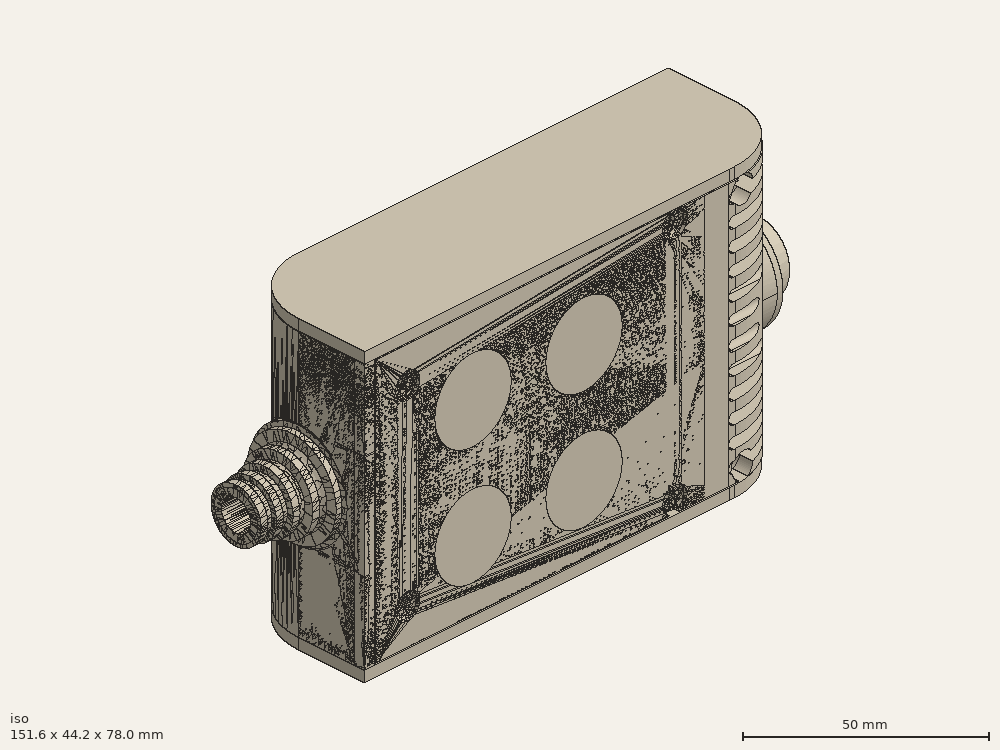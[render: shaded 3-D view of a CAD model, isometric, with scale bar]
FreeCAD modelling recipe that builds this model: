
FCSTD DOCUMENT  (FreeCAD 0.19R0.19.2)
Label: enclosure_199FCStd
License: All rights reserved
LicenseURL: http://en.wikipedia.org/wiki/All_rights_reserved
objects: Part::Revolution×152, Part::MultiFuse×146, Part::Feature×146, Sketcher::SketchObject×84, Part::Cut×70, Part::Cylinder×70, Part::Extrusion×67, Part::Fillet×58, Part::Box×36, App::MeasureDistance×4, PartDesign::Body×2, Image::ImagePlane×1
note: 831 computed .brp shape members not serialized (recipe doc carries the construction recipe); baked Part::Feature solids carry a one-line shape summary decoded from their .brp

FEATURE [Sketcher::SketchObject] Sketch  label="topSketch"
  FullyConstrained = true
  sketch-geometry (20):
    g0: LineSegment StartX=5.21097e-06 StartY=3 StartZ=0 EndX=5.21097e-06 EndY=19 EndZ=0
    g1: ArcOfCircle CenterX=19 CenterY=19 CenterZ=0 NormalX=0 NormalY=0 NormalZ=1 AngleXU=0 Radius=19 StartAngle=1.5708 EndAngle=3.14159
    g2: ArcOfCircle CenterX=19 CenterY=19 CenterZ=0 NormalX=0 NormalY=0 NormalZ=1 AngleXU=0 Radius=16 StartAngle=1.5708 EndAngle=3.14159
    g3: LineSegment StartX=114 StartY=35 StartZ=0 EndX=19 EndY=35 EndZ=0
    g4: LineSegment StartX=5.21097e-06 StartY=3 StartZ=0 EndX=5.21097e-06 EndY=0 EndZ=0
    g5: LineSegment StartX=3 StartY=0 StartZ=0 EndX=5.21097e-06 EndY=0 EndZ=0
    g6: LineSegment StartX=3 StartY=19 StartZ=0 EndX=3 EndY=0 EndZ=0
    g7: LineSegment StartX=19 StartY=38 StartZ=0 EndX=124 EndY=38 EndZ=0
    g8: Circle CenterX=119 CenterY=35 CenterZ=0 NormalX=0 NormalY=0 NormalZ=1 AngleXU=0 Radius=1
    g9: Circle CenterX=121 CenterY=35 CenterZ=0 NormalX=0 NormalY=0 NormalZ=1 AngleXU=0 Radius=1
    g10: Circle CenterX=121 CenterY=33 CenterZ=0 NormalX=0 NormalY=0 NormalZ=1 AngleXU=0 Radius=1
    g11: BSplineCurve PolesCount=3 KnotsCount=2 Degree=2 IsPeriodic=0
    g12: GeomPoint X=119 Y=35 Z=0
    g13: GeomPoint X=121 Y=33 Z=0
    g14: LineSegment StartX=119 StartY=35 StartZ=0 EndX=114 EndY=35 EndZ=0
    g15: ArcOfCircle CenterX=105 CenterY=19 CenterZ=0 NormalX=0 NormalY=0 NormalZ=1 AngleXU=0 Radius=19 StartAngle=5.7297 EndAngle=6.28319
    g16: ArcOfCircle CenterX=105 CenterY=19 CenterZ=0 NormalX=0 NormalY=0 NormalZ=1 AngleXU=0 Radius=16 StartAngle=5.60905 EndAngle=6.28319
    g17: LineSegment StartX=121 StartY=33 StartZ=0 EndX=121 EndY=19 EndZ=0
    g18: LineSegment StartX=124 StartY=38 StartZ=0 EndX=124 EndY=19 EndZ=0
    g19: LineSegment StartX=117.5 StartY=9.01251 StartZ=0 EndX=121.163 EndY=9.0125 EndZ=0
  constraints (46):
    c: Vertical(g0)
    c: Block(g0)
    c: Coincident(g1,g0)
    c: Block(g1)
    c: Coincident(g2,g1)
    c: Block(g2)
    c: Coincident(g3,g2)
    c: Horizontal(g3)
    c: Tangent(g3,g2)
    c: Coincident(g4,g0)
    c: Distance(g4) = 3
    c: Vertical(g4)
    c: Coincident(g5,g4)
    c: Horizontal(g5)
    c: Coincident(g6,g2)
    c: Coincident(g6,g5)
    c: Vertical(g6)
    c: Horizontal(g7)
    c: Distance(g7) = 105
    c: Coincident(g7,g1)
    c: Block(g3)
    c: Weight(g8) = 1
    c: Equal(g8,g9)
    c: Equal(g8,g10)
    c: InternalAlignment(g8,g11)
    c: InternalAlignment(g9,g11)
    c: InternalAlignment(g10,g11)
    c: InternalAlignment(g12,g11)
    c: InternalAlignment(g13,g11)
    c: Block(g11)
    c: Coincident(g14,g11)
    c: Coincident(g14,g3)
    c: Horizontal(g14)
    c: Block(g15)
    c: Coincident(g16,g15)
    c: Block(g16)
    c: Coincident(g17,g11)
    c: Coincident(g17,g16)
    c: Vertical(g17)
    c: Distance(g17) = 14
    c: Coincident(g18,g7)
    c: Coincident(g18,g15)
    c: Vertical(g18)
    c: Distance(g18) = 19
    c: Coincident(g19,g16)
    c: Coincident(g19,g15)
FEATURE [Sketcher::SketchObject] Sketch001  label="bottomSketch"
  FullyConstrained = true
  sketch-geometry (32):
    g0: LineSegment StartX=3.3 StartY=-6.03275e-07 StartZ=0 EndX=98 EndY=-6.03275e-07 EndZ=0
    g1: ArcOfCircle CenterX=98 CenterY=19 CenterZ=0 NormalX=0 NormalY=0 NormalZ=1 AngleXU=0 Radius=19 StartAngle=4.71239 EndAngle=5.71103
    g2: LineSegment StartX=6.3 StartY=8 StartZ=0 EndX=3.3 EndY=8 EndZ=0
    g3: LineSegment StartX=3.3 StartY=8 StartZ=0 EndX=3.3 EndY=-6.03275e-07 EndZ=0
    g4: ArcOfCircle CenterX=8.3 CenterY=5 CenterZ=0 NormalX=0 NormalY=0 NormalZ=1 AngleXU=0 Radius=2 StartAngle=3.14159 EndAngle=4.71239
    g5: LineSegment StartX=6.3 StartY=8 StartZ=0 EndX=6.3 EndY=5 EndZ=0
    g6: ArcOfCircle CenterX=98 CenterY=19 CenterZ=0 NormalX=0 NormalY=0 NormalZ=1 AngleXU=0 Radius=12.7 StartAngle=4.71239 EndAngle=6.28319
    g7: LineSegment StartX=94.7 StartY=3 StartZ=0 EndX=8.3 EndY=3 EndZ=0
    g8-g12: Circle x5 (B-spline internal-alignment scaffolding for g13; pole/knot coordinates omitted)
    g13: BSplineCurve PolesCount=5 KnotsCount=3 Degree=3 IsPeriodic=0
    g14: GeomPoint X=98 Y=6.3 Z=0
    g15: GeomPoint X=96.3938 Y=4.71946 Z=0
    g16: GeomPoint X=94.7 Y=3 Z=0
    g17-g23: Circle x7 (B-spline internal-alignment scaffolding for g24; pole/knot coordinates omitted)
    g24: BSplineCurve PolesCount=7 KnotsCount=5 Degree=3 IsPeriodic=0
    g25-g29: GeomPoint x5 (B-spline internal-alignment scaffolding for g24; pole/knot coordinates omitted)
    g30: ArcOfCircle CenterX=98 CenterY=19 CenterZ=0 NormalX=0 NormalY=0 NormalZ=1 AngleXU=0 Radius=15.7 StartAngle=5.81226 EndAngle=6.28319
    g31: LineSegment StartX=110.7 StartY=19 StartZ=0 EndX=113.7 EndY=19 EndZ=0
  constraints (41):
    c: Horizontal(g0)
    c: Coincident(g1,g0)
    c: Block(g1)
    c: Horizontal(g2)
    c: Distance(g2) = 3
    c: Coincident(g3,g2)
    c: Vertical(g3)
    c: Coincident(g3,g0)
    c: Block(g4)
    c: Block(g2)
    c: Coincident(g5,g2)
    c: Coincident(g5,g4)
    c: Vertical(g5)
    c: Coincident(g6,g1)
    c: Block(g6)
    c: Coincident(g7,g4)
    c: Horizontal(g7)
    c: Block(g0)
    c: Block(g7)
    c: Block(g3)
    c: Coincident(g13,g6)
    c: Weight(g8) = 1
    c: Equal(g8, g9-g12) x4
    c: Coincident(g13,g7)
    c: InternalAlignment(g8-g12 -> g13) x5
    c: InternalAlignment(g14,g13)
    c: InternalAlignment(g15,g13)
    c: InternalAlignment(g16,g13)
    c: Block(g13)
    c: Weight(g17) = 1
    c: Equal(g17, g18-g23) x6
    c: Coincident(g24,g1)
    c: InternalAlignment(g17-g23 -> g24) x7
    c: InternalAlignment(g25-g29 -> g24) x5
    c: Block(g24)
    c: Coincident(g30,g24)
    c: Coincident(g31,g6)
    c: Coincident(g31,g30)
    c: Horizontal(g31)
    c: Block(g31)
    c: Block(g30)
FEATURE [Part::Extrusion] Extrude  label="top"
  Base = -> Sketch
  Dir = (0,0,1)
  DirMode = 2
  FaceMakerClass = Part::FaceMakerBullseye
  LengthFwd = 72
  LengthRev = 0
  Solid = true
  Symmetric = false
FEATURE [Part::Extrusion] Extrude001  label="bottom"
  Base = -> Sketch001
  Dir = (0,0,1)
  DirMode = 2
  FaceMakerClass = Part::FaceMakerBullseye
  LengthFwd = 71.4
  LengthRev = 0
  Placement = pos=(0,0,0.3) rot=(0,0,1;0rad)
  Solid = true
  Symmetric = false
FEATURE [Sketcher::SketchObject] Sketch002  label="topSketch001"
  FullyConstrained = true
  sketch-geometry (8):
    g0: ArcOfCircle CenterX=19 CenterY=19.0975 CenterZ=0 NormalX=0 NormalY=0 NormalZ=1 AngleXU=0 Radius=18.9025 StartAngle=1.5708 EndAngle=3.14674
    g1: LineSegment StartX=0.0977805 StartY=19.0003 StartZ=0 EndX=0.0977805 EndY=0.000251602 EndZ=0
    g2: LineSegment StartX=19 StartY=38 StartZ=0 EndX=124 EndY=38 EndZ=0
    g3: LineSegment StartX=0.0977805 StartY=0.000251602 StartZ=0 EndX=105.098 EndY=0.000251602 EndZ=0
    g4: LineSegment StartX=124 StartY=38 StartZ=0 EndX=125.616 EndY=38 EndZ=0
    g5: LineSegment StartX=105.098 StartY=0.000251602 StartZ=0 EndX=106.713 EndY=0.000251602 EndZ=0
    g6: ArcOfCircle CenterX=106.616 CenterY=19 CenterZ=0 NormalX=0 NormalY=0 NormalZ=1 AngleXU=0 Radius=19 StartAngle=4.71754 EndAngle=6.28319
    g7: LineSegment StartX=125.616 StartY=38 StartZ=0 EndX=125.616 EndY=19 EndZ=0
  constraints (21):
    c: Block(g0)
    c: Coincident(g1,g0)
    c: Vertical(g1)
    c: Horizontal(g2)
    c: Distance(g2) = 105
    c: Coincident(g2,g0)
    c: Distance(g1) = 19
    c: Coincident(g3,g1)
    c: Horizontal(g3)
    c: Distance(g3) = 105
    c: Coincident(g4,g2)
    c: Horizontal(g4)
    c: Distance(g4) = 1.61553
    c: Horizontal(g5)
    c: Equal(g4,g5) = 1.61553
    c: Coincident(g5,g3)
    c: Block(g6)
    c: Coincident(g6,g5)
    c: Coincident(g7,g4)
    c: Coincident(g7,g6)
    c: Vertical(g7)
FEATURE [Part::Extrusion] Extrude002  label="sideA"
  Base = -> Sketch002
  Dir = (0,0,1)
  DirMode = 2
  FaceMakerClass = Part::FaceMakerBullseye
  LengthFwd = 3
  LengthRev = 0
  Placement = pos=(0,0,-3) rot=(0,0,1;0rad)
  Solid = true
  Symmetric = false
FEATURE [Sketcher::SketchObject] Sketch003  label="topSketch002"
  FullyConstrained = true
  sketch-geometry (6):
    g0: LineSegment StartX=19 StartY=38 StartZ=0 EndX=117 EndY=38 EndZ=0
    g1: ArcOfCircle CenterX=19 CenterY=19 CenterZ=0 NormalX=0 NormalY=0 NormalZ=1 AngleXU=0 Radius=19 StartAngle=1.5708 EndAngle=3.14159
    g2: LineSegment StartX=117 StartY=38 StartZ=0 EndX=117 EndY=19 EndZ=0
    g3: LineSegment StartX=98 StartY=1.0161e-12 StartZ=0 EndX=5.22862e-06 EndY=1.0161e-12 EndZ=0
    g4: LineSegment StartX=5.22862e-06 StartY=19 StartZ=0 EndX=5.22862e-06 EndY=1.0161e-12 EndZ=0
    g5: ArcOfCircle CenterX=98 CenterY=19 CenterZ=0 NormalX=0 NormalY=0 NormalZ=1 AngleXU=0 Radius=19 StartAngle=4.71239 EndAngle=6.28319
  constraints (16):
    c: Horizontal(g0)
    c: Distance(g0) = 98
    c: Coincident(g1,g0)
    c: Block(g1)
    c: Coincident(g2,g0)
    c: Vertical(g2)
    c: Distance(g2) = 19
    c: Horizontal(g3)
    c: Coincident(g4,g1)
    c: Vertical(g4)
    c: Coincident(g3,g4)
    c: Block(g3)
    c: Coincident(g5,g2)
    c: Coincident(g5,g3)
    c: Block(g0)
    c: Block(g5)
FEATURE [Sketcher::SketchObject] Sketch004
  FullyConstrained = true
  MapMode = 3
  Placement = pos=(0,0,0) rot=(1,0,0;1.5708rad)
  Support = -> [Extrude]
  sketch-geometry (8):
    g0: Circle CenterX=80.351 CenterY=-67.6202 CenterZ=0 NormalX=0 NormalY=0 NormalZ=1 AngleXU=0 Radius=2
    g1: Circle CenterX=80.351 CenterY=-67.6202 CenterZ=0 NormalX=0 NormalY=0 NormalZ=1 AngleXU=0 Radius=3
    g2: Circle CenterX=80.351 CenterY=-4.92017 CenterZ=0 NormalX=0 NormalY=0 NormalZ=1 AngleXU=0 Radius=2
    g3: Circle CenterX=80.351 CenterY=-4.92017 CenterZ=0 NormalX=0 NormalY=0 NormalZ=1 AngleXU=0 Radius=3
    g4: Circle CenterX=23.851 CenterY=-4.92017 CenterZ=0 NormalX=0 NormalY=0 NormalZ=1 AngleXU=0 Radius=2
    g5: Circle CenterX=23.851 CenterY=-4.92017 CenterZ=0 NormalX=0 NormalY=0 NormalZ=1 AngleXU=0 Radius=3
    g6: Circle CenterX=23.851 CenterY=-67.6202 CenterZ=0 NormalX=0 NormalY=0 NormalZ=1 AngleXU=0 Radius=2
    g7: Circle CenterX=23.851 CenterY=-67.6202 CenterZ=0 NormalX=0 NormalY=0 NormalZ=1 AngleXU=0 Radius=3
  constraints (8):
    c: Block(g3)
    c: Block(g2)
    c: Block(g1)
    c: Block(g0)
    c: Block(g6)
    c: Block(g7)
    c: Block(g4)
    c: Block(g5)
FEATURE [Part::Extrusion] Extrude004
  Base = -> Sketch004
  Dir = (0,-1,2e-16)
  DirMode = 2
  FaceMakerClass = Part::FaceMakerBullseye
  LengthFwd = 6
  LengthRev = 0
  Placement = pos=(0,9,0) rot=(0,0,1;0rad)
  Solid = true
  Symmetric = false
FEATURE [Sketcher::SketchObject] Sketch005
  FullyConstrained = true
  MapMode = 3
  Placement = pos=(0,0,0) rot=(1,0,0;1.5708rad)
  Support = -> [Extrude]
  sketch-geometry (8):
    g0: Circle CenterX=80.351 CenterY=-67.6202 CenterZ=0 NormalX=0 NormalY=0 NormalZ=1 AngleXU=0 Radius=3
    g1: Circle CenterX=80.351 CenterY=-4.92017 CenterZ=0 NormalX=0 NormalY=0 NormalZ=1 AngleXU=0 Radius=3
    g2: Circle CenterX=23.851 CenterY=-4.92017 CenterZ=0 NormalX=0 NormalY=0 NormalZ=1 AngleXU=0 Radius=3
    g3: Circle CenterX=23.851 CenterY=-67.6202 CenterZ=0 NormalX=0 NormalY=0 NormalZ=1 AngleXU=0 Radius=3
    g4: Circle CenterX=23.851 CenterY=-67.6202 CenterZ=0 NormalX=0 NormalY=0 NormalZ=1 AngleXU=0 Radius=5
    g5: Circle CenterX=80.351 CenterY=-67.6202 CenterZ=0 NormalX=0 NormalY=0 NormalZ=1 AngleXU=0 Radius=5
    g6: Circle CenterX=23.851 CenterY=-4.92017 CenterZ=0 NormalX=0 NormalY=0 NormalZ=1 AngleXU=0 Radius=5
    g7: Circle CenterX=80.351 CenterY=-4.92017 CenterZ=0 NormalX=0 NormalY=0 NormalZ=1 AngleXU=0 Radius=5
  constraints (8):
    c: Block(g1)
    c: Block(g0)
    c: Block(g3)
    c: Block(g2)
    c: Block(g5)
    c: Block(g4)
    c: Block(g6)
    c: Block(g7)
FEATURE [Part::Extrusion] Extrude005
  Base = -> Sketch005
  Dir = (0,-1,2e-16)
  DirMode = 2
  FaceMakerClass = Part::FaceMakerBullseye
  LengthFwd = 2
  LengthRev = 0
  Solid = true
  Symmetric = false
FEATURE [Sketcher::SketchObject] Sketch006
  FullyConstrained = true
  MapMode = 3
  Placement = pos=(0,0,0) rot=(1,0,0;1.5708rad)
  sketch-geometry (8):
    g0: Circle CenterX=80.351 CenterY=-67.6202 CenterZ=0 NormalX=0 NormalY=0 NormalZ=1 AngleXU=0 Radius=3
    g1: Circle CenterX=80.351 CenterY=-4.92017 CenterZ=0 NormalX=0 NormalY=0 NormalZ=1 AngleXU=0 Radius=3
    g2: Circle CenterX=23.851 CenterY=-4.92017 CenterZ=0 NormalX=0 NormalY=0 NormalZ=1 AngleXU=0 Radius=3
    g3: Circle CenterX=23.851 CenterY=-67.6202 CenterZ=0 NormalX=0 NormalY=0 NormalZ=1 AngleXU=0 Radius=3
    g4: Circle CenterX=23.851 CenterY=-67.6202 CenterZ=0 NormalX=0 NormalY=0 NormalZ=1 AngleXU=0 Radius=5
    g5: Circle CenterX=80.351 CenterY=-67.6202 CenterZ=0 NormalX=0 NormalY=0 NormalZ=1 AngleXU=0 Radius=5
    g6: Circle CenterX=23.851 CenterY=-4.92017 CenterZ=0 NormalX=0 NormalY=0 NormalZ=1 AngleXU=0 Radius=5
    g7: Circle CenterX=80.351 CenterY=-4.92017 CenterZ=0 NormalX=0 NormalY=0 NormalZ=1 AngleXU=0 Radius=5
  constraints (8):
    c: Block(g1)
    c: Block(g0)
    c: Block(g3)
    c: Block(g2)
    c: Block(g5)
    c: Block(g4)
    c: Block(g6)
    c: Block(g7)
FEATURE [Part::Extrusion] Extrude007
  Base = -> Sketch006
  Dir = (0,-1,2e-16)
  DirMode = 2
  FaceMakerClass = Part::FaceMakerBullseye
  LengthFwd = 2
  LengthRev = 0
  Solid = true
  Symmetric = false
FEATURE [Part::Fillet] Fillet
  Base = -> Extrude007
  Edges = 4 edges r=1.99: [Edge6,Edge12,Edge18,Edge24]
FEATURE [Part::Cut] Cut
  Base = -> Extrude005
  Placement = pos=(0,5,0) rot=(0,0,1;0rad)
  Tool = -> Fillet
FEATURE [Part::MultiFuse] Fusion  label="pCBScrews"
  Placement = pos=(-2.5,0,72.3) rot=(0,0,1;0rad)
  Shapes = -> [Extrude004,Cut]
FEATURE [App::MeasureDistance] Distance  label="Distance: 0.69 mm"
  Distance = 0.685967
  P1 = (24.0138,2.9647,0.3)
  P2 = (23.8901,3,-0.373787)
FEATURE [App::MeasureDistance] Distance001  label="Distance: 0.53 mm"
  Distance = 0.533607
  P1 = (80.2939,3,72.2334)
  P2 = (80.281,2.99661,71.7)
FEATURE [Part::Fillet] Fillet001
  Base = -> Extrude001
  Edges = 1 edges r=2.4: [Edge17]
FEATURE [Part::Fillet] Fillet002  label="bottom001"
  Base = -> Fillet001
  Edges = 1 edges r=2.4: [Edge36]
FEATURE [Part::Fillet] Fillet003  label="top001"
  Base = -> Extrude
  Edges = 1 edges r=2: [Edge1]
FEATURE [Sketcher::SketchObject] Sketch007
  FullyConstrained = true
  sketch-geometry (16):
    g0: LineSegment StartX=4 StartY=0 StartZ=0 EndX=4 EndY=2.4 EndZ=0
    g1: LineSegment StartX=4 StartY=2.4 StartZ=0 EndX=7 EndY=2.4 EndZ=0
    g2: LineSegment StartX=4 StartY=0 StartZ=0 EndX=5.7 EndY=0 EndZ=0
    g3: LineSegment StartX=5.7 StartY=0 StartZ=0 EndX=5.7 EndY=-5.6 EndZ=0
    g4-g8: Circle x5 (B-spline internal-alignment scaffolding for g9; pole/knot coordinates omitted)
    g9: BSplineCurve PolesCount=5 KnotsCount=3 Degree=3 IsPeriodic=0
    g10: GeomPoint X=7 Y=2.4 Z=0
    g11: GeomPoint X=10.4582 Y=-1.55472 Z=0
    g12: GeomPoint X=14 Y=-5.6 Z=0
    g13: LineSegment StartX=14 StartY=-5.6 StartZ=0 EndX=14 EndY=-14.1 EndZ=0
    g14: LineSegment StartX=14 StartY=-14.1 StartZ=0 EndX=6.5 EndY=-14.1 EndZ=0
    g15: LineSegment StartX=5.7 StartY=-5.6 StartZ=0 EndX=6.5 EndY=-14.1 EndZ=0
  constraints (28):
    c: Distance(g0) = 2.4
    c: Vertical(g0)
    c: Block(g0)
    c: Coincident(g1,g0)
    c: Horizontal(g1)
    c: Distance(g1) = 3
    c: Coincident(g2,g0)
    c: Horizontal(g2)
    c: Distance(g2) = 1.7
    c: Coincident(g3,g2)
    c: Vertical(g3)
    c: Distance(g3) = 5.6
    c: Coincident(g9,g1)
    c: Weight(g4) = 1
    c: Equal(g4, g5-g8) x4
    c: InternalAlignment(g4-g8 -> g9) x5
    c: InternalAlignment(g10,g9)
    c: InternalAlignment(g11,g9)
    c: InternalAlignment(g12,g9)
    c: Block(g9)
    c: Coincident(g13,g9)
    c: Vertical(g13)
    c: Distance(g13) = 8.5
    c: Coincident(g14,g13)
    c: Horizontal(g14)
    c: Distance(g14) = 7.5
    c: Coincident(g15,g3)
    c: Coincident(g15,g14)
FEATURE [Part::Feature] Face
  shape: bbox 10 x 16.5 x 2e-07 mm, 1 faces, 0 solids (baked)
FEATURE [Part::Revolution] Revolve  label="plugHousing"
  Angle = 360
  Axis = (0,1,0)
  Base = (0,0,0)
  FaceMakerClass = Part::FaceMakerBullseye
  Placement = pos=(0,0,36.15) rot=(0,0,1;0rad)
  Solid = false
  Source = -> Face
  Symmetric = false
FEATURE [Part::Feature] Face001
  shape: bbox 10 x 16.5 x 2e-07 mm, 1 faces, 0 solids (baked)
FEATURE [Part::Revolution] Revolve001  label="plugHousing001"
  Angle = 360
  Axis = (0,1,0)
  Base = (0,0,0)
  FaceMakerClass = Part::FaceMakerBullseye
  Placement = pos=(0,0,36.15) rot=(0,0,1;0rad)
  Solid = false
  Source = -> Face001
  Symmetric = false
FEATURE [Part::MultiFuse] Fusion001  label="plugHousing002"
  Placement = pos=(0,0,0) rot=(0,0,1;1.5708rad)
  Shapes = -> [Revolve001,Revolve]
FEATURE [Part::Feature] Face002
  shape: bbox 10 x 16.5 x 2e-07 mm, 1 faces, 0 solids (baked)
FEATURE [Part::Revolution] Revolve003  label="plugHousing005"
  Angle = 360
  Axis = (0,1,0)
  Base = (0,0,0)
  FaceMakerClass = Part::FaceMakerBullseye
  Placement = pos=(0,0,36.15) rot=(0,0,1;0rad)
  Solid = false
  Source = -> Face002
  Symmetric = false
FEATURE [Part::Feature] Face003
  shape: bbox 10 x 16.5 x 2e-07 mm, 1 faces, 0 solids (baked)
FEATURE [Part::Revolution] Revolve002  label="plugHousing003"
  Angle = 360
  Axis = (0,1,0)
  Base = (0,0,0)
  FaceMakerClass = Part::FaceMakerBullseye
  Placement = pos=(0,0,36.15) rot=(0,0,1;0rad)
  Solid = false
  Source = -> Face003
  Symmetric = false
FEATURE [Part::MultiFuse] Fusion002  label="plugHousing004"
  Placement = pos=(0,0,0) rot=(0,0,1;1.5708rad)
  Shapes = -> [Revolve002,Revolve003]
FEATURE [Part::MultiFuse] Fusion003  label="plugHousing006"
  Placement = pos=(0,19,0) rot=(0,0,1;3.14159rad)
  Shapes = -> [Fusion002,Fusion001]
FEATURE [Part::Feature] Face004
  shape: bbox 10 x 16.5 x 2e-07 mm, 1 faces, 0 solids (baked)
FEATURE [Part::Revolution] Revolve006  label="plugHousing010"
  Angle = 360
  Axis = (0,1,0)
  Base = (0,0,0)
  FaceMakerClass = Part::FaceMakerBullseye
  Placement = pos=(0,0,36.15) rot=(0,0,1;0rad)
  Solid = false
  Source = -> Face004
  Symmetric = false
FEATURE [Part::Feature] Face005
  shape: bbox 10 x 16.5 x 2e-07 mm, 1 faces, 0 solids (baked)
FEATURE [Part::Revolution] Revolve007  label="plugHousing011"
  Angle = 360
  Axis = (0,1,0)
  Base = (0,0,0)
  FaceMakerClass = Part::FaceMakerBullseye
  Placement = pos=(0,0,36.15) rot=(0,0,1;0rad)
  Solid = false
  Source = -> Face005
  Symmetric = false
FEATURE [Part::Feature] Face006
  shape: bbox 10 x 16.5 x 2e-07 mm, 1 faces, 0 solids (baked)
FEATURE [Part::Revolution] Revolve004  label="plugHousing007"
  Angle = 360
  Axis = (0,1,0)
  Base = (0,0,0)
  FaceMakerClass = Part::FaceMakerBullseye
  Placement = pos=(0,0,36.15) rot=(0,0,1;0rad)
  Solid = false
  Source = -> Face006
  Symmetric = false
FEATURE [Part::MultiFuse] Fusion004  label="plugHousing009"
  Placement = pos=(0,0,0) rot=(0,0,1;1.5708rad)
  Shapes = -> [Revolve004,Revolve007]
FEATURE [Part::Feature] Face007
  shape: bbox 10 x 16.5 x 2e-07 mm, 1 faces, 0 solids (baked)
FEATURE [Part::Revolution] Revolve005  label="plugHousing008"
  Angle = 360
  Axis = (0,1,0)
  Base = (0,0,0)
  FaceMakerClass = Part::FaceMakerBullseye
  Placement = pos=(0,0,36.15) rot=(0,0,1;0rad)
  Solid = false
  Source = -> Face007
  Symmetric = false
FEATURE [Part::MultiFuse] Fusion005  label="plugHousing012"
  Placement = pos=(0,0,0) rot=(0,0,1;1.5708rad)
  Shapes = -> [Revolve006,Revolve005]
FEATURE [Part::MultiFuse] Fusion006  label="plugHousing013"
  Placement = pos=(0,19,0) rot=(0,0,1;3.14159rad)
  Shapes = -> [Fusion005,Fusion004]
FEATURE [Part::MultiFuse] Fusion007  label="plugHousing014"
  Placement = pos=(122.621,0,-0.15) rot=(0,0,1;0rad)
  Shapes = -> [Fusion003,Fusion006]
FEATURE [Part::Cylinder] Cylinder002
  Angle = 360
  AttacherType = Attacher::AttachEngine3D
  Height = 20
  Placement = pos=(0,0,36.15) rot=(0,0,1;0rad)
  Radius = 4
FEATURE [Part::Cylinder] Cylinder003
  Angle = 360
  AttacherType = Attacher::AttachEngine3D
  Height = 10
  Placement = pos=(0,0,36.15) rot=(0,0,1;0rad)
  Radius = 4
FEATURE [Part::MultiFuse] Fusion009  label="removeToCreateHoleForPlugHousing"
  Placement = pos=(70,19,36.15) rot=(0,1,0;1.5708rad)
  Shapes = -> [Cylinder002,Cylinder003]
FEATURE [Part::Cylinder] Cylinder004
  Angle = 360
  AttacherType = Attacher::AttachEngine3D
  Height = 20
  Placement = pos=(0,0,36.15) rot=(0,0,1;0rad)
  Radius = 4
FEATURE [Part::Cylinder] Cylinder005
  Angle = 360
  AttacherType = Attacher::AttachEngine3D
  Height = 10
  Placement = pos=(0,0,36.15) rot=(0,0,1;0rad)
  Radius = 4
FEATURE [Part::MultiFuse] Fusion010  label="removeToCreateHoleForPlugHousing001"
  Placement = pos=(70,19,36.15) rot=(0,1,0;1.5708rad)
  Shapes = -> [Cylinder004,Cylinder005]
FEATURE [Part::Cut] Cut001
  Base = -> Fillet003
  Tool = -> Fusion010
FEATURE [Part::Cut] Cut002  label="Bottom"
  Base = -> Fillet002
  Tool = -> Fusion009
FEATURE [Part::Feature] Face008
  shape: bbox 10 x 16.5 x 2e-07 mm, 1 faces, 0 solids (baked)
FEATURE [Part::Revolution] Revolve011  label="plugHousing021"
  Angle = 360
  Axis = (0,1,0)
  Base = (0,0,0)
  FaceMakerClass = Part::FaceMakerBullseye
  Placement = pos=(0,0,36.15) rot=(0,0,1;0rad)
  Solid = false
  Source = -> Face008
  Symmetric = false
FEATURE [Part::Feature] Face009
  shape: bbox 10 x 16.5 x 2e-07 mm, 1 faces, 0 solids (baked)
FEATURE [Part::Revolution] Revolve012  label="plugHousing022"
  Angle = 360
  Axis = (0,1,0)
  Base = (0,0,0)
  FaceMakerClass = Part::FaceMakerBullseye
  Placement = pos=(0,0,36.15) rot=(0,0,1;0rad)
  Solid = false
  Source = -> Face009
  Symmetric = false
FEATURE [Part::Feature] Face010 .. Face013  x4 (patterned run collapsed; names and placements below)
  shape: bbox 10 x 16.5 x 2e-07 mm, 1 faces, 0 solids (baked)
FEATURE [Part::Revolution] Revolve015  label="plugHousing027"
  Angle = 360
  Axis = (0,1,0)
  Base = (0,0,0)
  FaceMakerClass = Part::FaceMakerBullseye
  Placement = pos=(0,0,36.15) rot=(0,0,1;0rad)
  Solid = false
  Source = -> Face013
  Symmetric = false
FEATURE [Part::Feature] Face014
  shape: bbox 10 x 16.5 x 2e-07 mm, 1 faces, 0 solids (baked)
FEATURE [Part::Feature] Face015
  shape: bbox 10 x 16.5 x 2e-07 mm, 1 faces, 0 solids (baked)
FEATURE [Part::Feature] Face016
  shape: bbox 10 x 16.5 x 2e-07 mm, 1 faces, 0 solids (baked)
FEATURE [Part::Revolution] Revolve019  label="plugHousing033"
  Angle = 360
  Axis = (0,1,0)
  Base = (0,0,0)
  FaceMakerClass = Part::FaceMakerBullseye
  Placement = pos=(0,0,36.15) rot=(0,0,1;0rad)
  Solid = false
  Source = -> Face016
  Symmetric = false
FEATURE [Part::Feature] Face017
  shape: bbox 10 x 16.5 x 2e-07 mm, 1 faces, 0 solids (baked)
FEATURE [Part::Revolution] Revolve020  label="plugHousing034"
  Angle = 360
  Axis = (0,1,0)
  Base = (0,0,0)
  FaceMakerClass = Part::FaceMakerBullseye
  Placement = pos=(0,0,36.15) rot=(0,0,1;0rad)
  Solid = false
  Source = -> Face017
  Symmetric = false
FEATURE [Part::Feature] Face018
  shape: bbox 10 x 16.5 x 2e-07 mm, 1 faces, 0 solids (baked)
FEATURE [Part::Revolution] Revolve016  label="plugHousing030"
  Angle = 360
  Axis = (0,1,0)
  Base = (0,0,0)
  FaceMakerClass = Part::FaceMakerBullseye
  Placement = pos=(0,0,36.15) rot=(0,0,1;0rad)
  Solid = false
  Source = -> Face018
  Symmetric = false
FEATURE [Part::MultiFuse] Fusion020  label="plugHousing038"
  Placement = pos=(0,0,0) rot=(0,0,1;1.5708rad)
  Shapes = -> [Revolve016,Revolve020]
FEATURE [Part::Feature] Face019
  shape: bbox 10 x 16.5 x 2e-07 mm, 1 faces, 0 solids (baked)
FEATURE [Part::Feature] Face020
  shape: bbox 10 x 16.5 x 2e-07 mm, 1 faces, 0 solids (baked)
FEATURE [Part::Revolution] Revolve017  label="plugHousing031"
  Angle = 360
  Axis = (0,1,0)
  Base = (0,0,0)
  FaceMakerClass = Part::FaceMakerBullseye
  Placement = pos=(0,0,36.15) rot=(0,0,1;0rad)
  Solid = false
  Source = -> Face020
  Symmetric = false
FEATURE [Part::MultiFuse] Fusion021  label="plugHousing039"
  Placement = pos=(0,0,0) rot=(0,0,1;1.5708rad)
  Shapes = -> [Revolve019,Revolve017]
FEATURE [Part::MultiFuse] Fusion023  label="plugHousing041"
  Placement = pos=(0,19,0) rot=(0,0,1;3.14159rad)
  Shapes = -> [Fusion021,Fusion020]
FEATURE [Part::Revolution] Revolve022  label="plugHousing043"
  Angle = 360
  Axis = (0,1,0)
  Base = (0,0,0)
  FaceMakerClass = Part::FaceMakerBullseye
  Placement = pos=(0,0,36.15) rot=(0,0,1;0rad)
  Solid = false
  Source = -> Face019
  Symmetric = false
FEATURE [Part::Feature] Face021
  shape: bbox 10 x 16.5 x 2e-07 mm, 1 faces, 0 solids (baked)
FEATURE [Part::Revolution] Revolve023  label="plugHousing044"
  Angle = 360
  Axis = (0,1,0)
  Base = (0,0,0)
  FaceMakerClass = Part::FaceMakerBullseye
  Placement = pos=(0,0,36.15) rot=(0,0,1;0rad)
  Solid = false
  Source = -> Face021
  Symmetric = false
FEATURE [Part::Feature] Face022
  shape: bbox 10 x 16.5 x 2e-07 mm, 1 faces, 0 solids (baked)
FEATURE [Part::Revolution] Revolve018  label="plugHousing032"
  Angle = 360
  Axis = (0,1,0)
  Base = (0,0,0)
  FaceMakerClass = Part::FaceMakerBullseye
  Placement = pos=(0,0,36.15) rot=(0,0,1;0rad)
  Solid = false
  Source = -> Face022
  Symmetric = false
FEATURE [Part::MultiFuse] Fusion022  label="plugHousing040"
  Placement = pos=(0,0,0) rot=(0,0,1;1.5708rad)
  Shapes = -> [Revolve018,Revolve023]
FEATURE [Part::Feature] Face023
  shape: bbox 10 x 16.5 x 2e-07 mm, 1 faces, 0 solids (baked)
FEATURE [Part::Revolution] Revolve021  label="plugHousing035"
  Angle = 360
  Axis = (0,1,0)
  Base = (0,0,0)
  FaceMakerClass = Part::FaceMakerBullseye
  Placement = pos=(0,0,36.15) rot=(0,0,1;0rad)
  Solid = false
  Source = -> Face023
  Symmetric = false
FEATURE [Part::MultiFuse] Fusion018  label="plugHousing036"
  Placement = pos=(0,0,0) rot=(0,0,1;1.5708rad)
  Shapes = -> [Revolve022,Revolve021]
FEATURE [Part::MultiFuse] Fusion019  label="plugHousing037"
  Placement = pos=(0,19,0) rot=(0,0,1;3.14159rad)
  Shapes = -> [Fusion018,Fusion022]
FEATURE [Part::MultiFuse] Fusion024  label="plugHousing042"
  Placement = pos=(122.621,0,-0.15) rot=(0,0,1;0rad)
  Shapes = -> [Fusion023,Fusion019]
FEATURE [Part::Cylinder] Cylinder006
  Angle = 360
  AttacherType = Attacher::AttachEngine3D
  Height = 20
  Placement = pos=(0,0,36.15) rot=(0,0,1;0rad)
  Radius = 14.3
FEATURE [Part::Cylinder] Cylinder007
  Angle = 360
  AttacherType = Attacher::AttachEngine3D
  Height = 10
  Placement = pos=(0,0,36.15) rot=(0,0,1;0rad)
  Radius = 4
FEATURE [Part::MultiFuse] Fusion026  label="removeToCreteHoleForPlugHousing"
  Placement = pos=(70,19,36) rot=(0,1,0;1.5708rad)
  Shapes = -> [Cylinder006,Cylinder007]
FEATURE [Part::Box] Box001  label="Cube001"
  AttacherType = Attacher::AttachEngine3D
  Height = 28
  Length = 3
  Placement = pos=(110.7,19,22) rot=(0,0,1;0rad)
  Width = 15.7
FEATURE [Part::Cut] Cut003  label="top002"
  Base = -> Cut001
  Tool = -> Fusion007
FEATURE [Part::Revolution] Revolve008  label="plugHousing015"
  Angle = 360
  Axis = (0,1,0)
  Base = (0,0,0)
  FaceMakerClass = Part::FaceMakerBullseye
  Placement = pos=(0,0,36.15) rot=(0,0,1;0rad)
  Solid = false
  Source = -> Face010
  Symmetric = false
FEATURE [Part::MultiFuse] Fusion013  label="plugHousing020"
  Placement = pos=(0,0,0) rot=(0,0,1;1.5708rad)
  Shapes = -> [Revolve008,Revolve012]
FEATURE [Part::Cut] Cut004  label="top003"
  Base = -> Cut003
  Placement = pos=(1,0,0) rot=(0,0,1;0rad)
  Tool = -> Fusion026
FEATURE [Part::Cylinder] Cylinder008
  Angle = 360
  AttacherType = Attacher::AttachEngine3D
  Height = 20
  Placement = pos=(0,0,36.15) rot=(0,0,1;0rad)
  Radius = 10.3
FEATURE [Part::Cylinder] Cylinder009
  Angle = 360
  AttacherType = Attacher::AttachEngine3D
  Height = 10
  Placement = pos=(0,0,36.15) rot=(0,0,1;0rad)
  Radius = 4
FEATURE [Part::MultiFuse] Fusion027  label="removeToCreteHoleForPlugHousing001"
  Placement = pos=(70,19,36) rot=(0,1,0;1.5708rad)
  Shapes = -> [Cylinder008,Cylinder009]
FEATURE [Part::Cut] Cut005  label="plugHousingTab"
  Base = -> Box001
  Tool = -> Fusion027
FEATURE [Part::MultiFuse] Fusion028  label="plugHousing045"
  Shapes = -> [Fusion024,Cut005]
FEATURE [Part::Box] Box002  label="Cube002"
  AttacherType = Attacher::AttachEngine3D
  Height = 28.8
  Length = 3
  Placement = pos=(107.3,28,21.6) rot=(0,0,1;0rad)
  Width = 7
FEATURE [Part::Box] Box003  label="Cube003"
  AttacherType = Attacher::AttachEngine3D
  Height = 3
  Length = 6.4
  Placement = pos=(107.3,28,18.6) rot=(0,0,1;0rad)
  Width = 7
FEATURE [Part::Box] Box004  label="Cube004"
  AttacherType = Attacher::AttachEngine3D
  Height = 3
  Length = 6.4
  Placement = pos=(107.3,28,50.4) rot=(0,0,1;0rad)
  Width = 7
FEATURE [Part::MultiFuse] Fusion029  label="plugHousingBracketHolder"
  Shapes = -> [Box004,Box002,Box003]
FEATURE [Part::Cylinder] Cylinder010
  Angle = 360
  AttacherType = Attacher::AttachEngine3D
  Height = 20
  Placement = pos=(0,0,36.15) rot=(0,0,1;0rad)
  Radius = 14.3
FEATURE [Part::Cylinder] Cylinder011
  Angle = 360
  AttacherType = Attacher::AttachEngine3D
  Height = 10
  Placement = pos=(0,0,36.15) rot=(0,0,1;0rad)
  Radius = 4
FEATURE [Part::MultiFuse] Fusion030  label="removeToCreteHoleForPlugHousing002"
  Placement = pos=(70,19,36) rot=(0,1,0;1.5708rad)
  Shapes = -> [Cylinder010,Cylinder011]
FEATURE [Part::Cut] Cut006  label="plugHousingBracketHolder001"
  Base = -> Fusion029
  Tool = -> Fusion030
FEATURE [Part::Cylinder] Cylinder012
  Angle = 360
  AttacherType = Attacher::AttachEngine3D
  Height = 20
  Placement = pos=(0,0,36.15) rot=(0,0,1;0rad)
  Radius = 7
FEATURE [Part::Cylinder] Cylinder013
  Angle = 360
  AttacherType = Attacher::AttachEngine3D
  Height = 10
  Placement = pos=(0,0,36.15) rot=(0,0,1;0rad)
  Radius = 4
FEATURE [Part::MultiFuse] Fusion032  label="removeToCreteHoleForPlugHousing003"
  Placement = pos=(70,19,36) rot=(0,1,0;1.5708rad)
  Shapes = -> [Cylinder012,Cylinder013]
FEATURE [Part::Cut] Cut007  label="bottom002"
  Base = -> Cut002
  Tool = -> Fusion032
FEATURE [Sketcher::SketchObject] Sketch008
  FullyConstrained = true
  sketch-geometry (54):
    g0: LineSegment StartX=-4.2 StartY=0 StartZ=0 EndX=-6.2 EndY=0 EndZ=0
    g1: LineSegment StartX=-14 StartY=-18 StartZ=0 EndX=-14 EndY=-26.5 EndZ=0
    g2: LineSegment StartX=-4.2 StartY=0 StartZ=0 EndX=-4.2 EndY=-13.4877 EndZ=0
    g3: Circle CenterX=-4.2 CenterY=-13.4877 CenterZ=0 NormalX=0 NormalY=0 NormalZ=1 AngleXU=0 Radius=1
    g4: Circle CenterX=-4.2 CenterY=-26.5 CenterZ=0 NormalX=0 NormalY=0 NormalZ=1 AngleXU=0 Radius=1
    g5: Circle CenterX=-8.2 CenterY=-26.5 CenterZ=0 NormalX=0 NormalY=0 NormalZ=1 AngleXU=0 Radius=1
    g6: BSplineCurve PolesCount=3 KnotsCount=2 Degree=2 IsPeriodic=0
    g7: GeomPoint X=-4.2 Y=-13.4877 Z=0
    g8: GeomPoint X=-8.2 Y=-26.5 Z=0
    g9: LineSegment StartX=-14 StartY=-26.5 StartZ=0 EndX=-8.2 EndY=-26.5 EndZ=0
    g10: LineSegment StartX=-10.15 StartY=-12 StartZ=0 EndX=-10.15 EndY=-14 EndZ=0
    g11: LineSegment StartX=-12.8401 StartY=-16 StartZ=0 EndX=-10.1571 EndY=-16 EndZ=0
    g12: LineSegment StartX=-10.15 StartY=-14 StartZ=0 EndX=-8.70761 EndY=-14 EndZ=0
    g13: LineSegment StartX=-12.8401 StartY=-16 StartZ=0 EndX=-12.8401 EndY=-17.6958 EndZ=0
    g14: LineSegment StartX=-10.15 StartY=-12 StartZ=0 EndX=-7.79258 EndY=-12 EndZ=0
    g15: Circle CenterX=-6.2215 CenterY=-2 CenterZ=0 NormalX=0 NormalY=0 NormalZ=1 AngleXU=0 Radius=1
    g16: Circle CenterX=-6.22762 CenterY=-2.58724 CenterZ=0 NormalX=0 NormalY=0 NormalZ=1 AngleXU=0 Radius=1
    g17: Circle CenterX=-6.32538 CenterY=-4 CenterZ=0 NormalX=0 NormalY=0 NormalZ=1 AngleXU=0 Radius=1
    g18: BSplineCurve PolesCount=3 KnotsCount=2 Degree=2 IsPeriodic=0
    g19: GeomPoint X=-6.2215 Y=-2 Z=0
    g20: GeomPoint X=-6.32538 Y=-4 Z=0
    g21: Circle CenterX=-6.48644 CenterY=-5.99526 CenterZ=0 NormalX=0 NormalY=0 NormalZ=1 AngleXU=0 Radius=1
    g22: Circle CenterX=-6.58486 CenterY=-6.99526 CenterZ=0 NormalX=0 NormalY=0 NormalZ=1 AngleXU=0 Radius=1
    g23: Circle CenterX=-6.77343 CenterY=-8 CenterZ=0 NormalX=0 NormalY=0 NormalZ=1 AngleXU=0 Radius=1
    g24: BSplineCurve PolesCount=3 KnotsCount=2 Degree=2 IsPeriodic=0
    g25: GeomPoint X=-6.48644 Y=-5.99526 Z=0
    g26: GeomPoint X=-6.77343 Y=-8 Z=0
    g27: Circle CenterX=-7.19003 CenterY=-10 CenterZ=0 NormalX=0 NormalY=0 NormalZ=1 AngleXU=0 Radius=1
    g28: Circle CenterX=-7.44407 CenterY=-11.0915 CenterZ=0 NormalX=0 NormalY=0 NormalZ=1 AngleXU=0 Radius=1
    g29: Circle CenterX=-7.79258 CenterY=-12 CenterZ=0 NormalX=0 NormalY=0 NormalZ=1 AngleXU=0 Radius=1
    g30: BSplineCurve PolesCount=3 KnotsCount=2 Degree=2 IsPeriodic=0
    g31: GeomPoint X=-7.19003 Y=-10 Z=0
    g32: GeomPoint X=-7.79258 Y=-12 Z=0
    g33: Circle CenterX=-8.70761 CenterY=-14 CenterZ=0 NormalX=0 NormalY=0 NormalZ=1 AngleXU=0 Radius=1
    g34: Circle CenterX=-9.33087 CenterY=-15.1837 CenterZ=0 NormalX=0 NormalY=0 NormalZ=1 AngleXU=0 Radius=1
    g35: Circle CenterX=-10.1571 CenterY=-16 CenterZ=0 NormalX=0 NormalY=0 NormalZ=1 AngleXU=0 Radius=1
    g36: BSplineCurve PolesCount=3 KnotsCount=2 Degree=2 IsPeriodic=0
    g37: GeomPoint X=-8.70761 Y=-14 Z=0
    g38: GeomPoint X=-10.1571 Y=-16 Z=0
    g39: Circle CenterX=-12.8401 CenterY=-17.6958 CenterZ=0 NormalX=0 NormalY=0 NormalZ=1 AngleXU=0 Radius=1
    g40: Circle CenterX=-13.3521 CenterY=-17.9027 CenterZ=0 NormalX=0 NormalY=0 NormalZ=1 AngleXU=0 Radius=1
    g41: Circle CenterX=-14 CenterY=-18 CenterZ=0 NormalX=0 NormalY=0 NormalZ=1 AngleXU=0 Radius=1
    g42: BSplineCurve PolesCount=3 KnotsCount=2 Degree=2 IsPeriodic=0
    g43: GeomPoint X=-12.8401 Y=-17.6958 Z=0
    g44: GeomPoint X=-14 Y=-18 Z=0
    g45: LineSegment StartX=-6.2 StartY=0 StartZ=0 EndX=-7.2 EndY=0 EndZ=0
    g46: LineSegment StartX=-7.2 StartY=0 StartZ=0 EndX=-7.2 EndY=-2 EndZ=0
    g47: LineSegment StartX=-7.2 StartY=-2 StartZ=0 EndX=-6.2215 EndY=-2 EndZ=0
    g48: LineSegment StartX=-6.32538 StartY=-4 StartZ=0 EndX=-7.65538 EndY=-4 EndZ=0
    g49: LineSegment StartX=-7.65538 StartY=-4 StartZ=0 EndX=-7.65538 EndY=-5.99526 EndZ=0
    g50: LineSegment StartX=-7.65538 StartY=-5.99526 StartZ=0 EndX=-6.48644 EndY=-5.99526 EndZ=0
    g51: LineSegment StartX=-6.77343 StartY=-8 StartZ=0 EndX=-8.43343 EndY=-8 EndZ=0
    g52: LineSegment StartX=-8.43343 StartY=-8 StartZ=0 EndX=-8.43343 EndY=-10 EndZ=0
    g53: LineSegment StartX=-8.43343 StartY=-10 StartZ=0 EndX=-7.19003 EndY=-10 EndZ=0
  constraints (112):
    c: Horizontal(g0)
    c: Distance(g0) = 2
    c: Block(g0)
    c: Vertical(g1)
    c: Coincident(g2,g0)
    c: Vertical(g2)
    c: Block(g2)
    c: Coincident(g6,g2)
    c: Weight(g3) = 1
    c: Equal(g3,g4)
    c: Equal(g3,g5)
    c: InternalAlignment(g3,g6)
    c: InternalAlignment(g4,g6)
    c: InternalAlignment(g5,g6)
    c: InternalAlignment(g7,g6)
    c: InternalAlignment(g8,g6)
    c: Block(g6)
    c: Coincident(g9,g1)
    c: Coincident(g9,g6)
    c: Horizontal(g9)
    c: Vertical(g10)
    c: Block(g10)
    c: Horizontal(g11)
    c: Block(g11)
    c: Coincident(g12,g10)
    c: Horizontal(g12)
    c: Block(g12)
    c: Coincident(g13,g11)
    c: Vertical(g13)
    c: Block(g13)
    c: Coincident(g14,g10)
    c: Horizontal(g14)
    c: Block(g14)
    c: Block(g9)
    c: Block(g1)
    c: Weight(g15) = 1
    c: Equal(g15,g16)
    c: Equal(g15,g17)
    c: InternalAlignment(g15,g18)
    c: InternalAlignment(g16,g18)
    c: InternalAlignment(g17,g18)
    c: InternalAlignment(g19,g18)
    c: InternalAlignment(g20,g18)
    c: Weight(g21) = 1
    c: Equal(g21,g22)
    c: Equal(g21,g23)
    c: InternalAlignment(g21,g24)
    c: InternalAlignment(g22,g24)
    c: InternalAlignment(g23,g24)
    c: InternalAlignment(g25,g24)
    c: InternalAlignment(g26,g24)
    c: Weight(g27) = 1
    c: Equal(g27,g28)
    c: Equal(g27,g29)
    c: Coincident(g30,g14)
    c: InternalAlignment(g27,g30)
    c: InternalAlignment(g28,g30)
    c: InternalAlignment(g29,g30)
    c: InternalAlignment(g31,g30)
    c: InternalAlignment(g32,g30)
    c: Coincident(g36,g12)
    c: Weight(g33) = 1
    c: Equal(g33,g34)
    c: Equal(g33,g35)
    c: Coincident(g36,g11)
    c: InternalAlignment(g33,g36)
    c: InternalAlignment(g34,g36)
    c: InternalAlignment(g35,g36)
    c: InternalAlignment(g37,g36)
    c: InternalAlignment(g38,g36)
    c: Coincident(g42,g13)
    c: Weight(g39) = 1
    c: Equal(g39,g40)
    c: Equal(g39,g41)
    c: Coincident(g42,g1)
    c: InternalAlignment(g39,g42)
    c: InternalAlignment(g40,g42)
    c: InternalAlignment(g41,g42)
    c: InternalAlignment(g43,g42)
    c: InternalAlignment(g44,g42)
    c: Block(g18)
    c: Block(g24)
    c: Block(g30)
    c: Block(g36)
    c: Block(g42)
    c: Horizontal(g45)
    c: Coincident(g45,g0)
    c: Vertical(g46)
    c: Coincident(g46,g45)
    c: Coincident(g47,g46)
    c: Coincident(g47,g18)
    c: Horizontal(g47)
    c: Block(g46)
    c: Coincident(g48,g18)
    c: Horizontal(g48)
    c: Distance(g48) = 1.33
    c: Vertical(g49)
    c: Coincident(g49,g48)
    c: Coincident(g50,g49)
    c: Coincident(g50,g24)
    c: Horizontal(g50)
    c: Tangent(g50,g22)
    c: Horizontal(g51)
    c: Coincident(g51,g24)
    c: Block(g51)
    c: Vertical(g52)
    c: Block(g52)
    c: Coincident(g52,g51)
    c: Coincident(g53,g52)
    c: Coincident(g53,g30)
    c: Horizontal(g53)
    c: Distance(g1) = 8.5
FEATURE [Part::Feature] Face024
  shape: bbox 9.8 x 26.5 x 2e-07 mm, 1 faces, 0 solids (baked)
FEATURE [Part::Revolution] Revolve024
  Angle = 360
  Axis = (0,1,0)
  Base = (0,0,0)
  FaceMakerClass = Part::FaceMakerBullseye
  Placement = pos=(0,0,0) rot=(0,0,1;1.5708rad)
  Solid = false
  Source = -> Face024
  Symmetric = false
FEATURE [Part::Feature] Face025
  shape: bbox 9.8 x 26.5 x 2e-07 mm, 1 faces, 0 solids (baked)
FEATURE [Part::Revolution] Revolve025
  Angle = 360
  Axis = (0,1,0)
  Base = (0,0,0)
  FaceMakerClass = Part::FaceMakerBullseye
  Placement = pos=(0,0,0) rot=(0,0,1;1.5708rad)
  Solid = false
  Source = -> Face025
  Symmetric = false
FEATURE [Part::MultiFuse] Fusion033
  Placement = pos=(-18,19,36) rot=(0,0,1;0rad)
  Shapes = -> [Revolve025,Revolve024]
FEATURE [Part::Cylinder] Cylinder014
  Angle = 360
  AttacherType = Attacher::AttachEngine3D
  Height = 20
  Placement = pos=(0,0,36.15) rot=(0,0,1;0rad)
  Radius = 14.3
FEATURE [Part::Cylinder] Cylinder015
  Angle = 360
  AttacherType = Attacher::AttachEngine3D
  Height = 10
  Placement = pos=(0,0,36.15) rot=(0,0,1;0rad)
  Radius = 4
FEATURE [Part::MultiFuse] Fusion034  label="removeToCreteHoleForPlugHousing004"
  Placement = pos=(-42,19,36) rot=(0,1,0;1.5708rad)
  Shapes = -> [Cylinder014,Cylinder015]
FEATURE [Part::Cut] Cut008  label="top004"
  Base = -> Cut004
  Placement = pos=(-1,0,0) rot=(0,0,1;0rad)
  Tool = -> Fusion034
FEATURE [Part::Box] Box005  label="Cube005"
  AttacherType = Attacher::AttachEngine3D
  Height = 28
  Length = 3
  Placement = pos=(110.7,19,22) rot=(0,0,1;0rad)
  Width = 15.7
FEATURE [Part::Cylinder] Cylinder016
  Angle = 360
  AttacherType = Attacher::AttachEngine3D
  Height = 10
  Placement = pos=(0,0,36.15) rot=(0,0,1;0rad)
  Radius = 4
FEATURE [Part::Cylinder] Cylinder017
  Angle = 360
  AttacherType = Attacher::AttachEngine3D
  Height = 20
  Placement = pos=(0,0,36.15) rot=(0,0,1;0rad)
  Radius = 10.3
FEATURE [Part::MultiFuse] Fusion035  label="removeToCreteHoleForPlugHousing005"
  Placement = pos=(70,19,36) rot=(0,1,0;1.5708rad)
  Shapes = -> [Cylinder017,Cylinder016]
FEATURE [Part::Cut] Cut009  label="plugHousingTab001"
  Base = -> Box005
  Placement = pos=(-107.4,-14,0) rot=(0,0,1;0rad)
  Tool = -> Fusion035
FEATURE [Part::Box] Box006  label="Cube006"
  AttacherType = Attacher::AttachEngine3D
  Height = 28
  Length = 3
  Placement = pos=(110.7,19,22) rot=(0,0,1;0rad)
  Width = 15.7
FEATURE [Part::Cylinder] Cylinder018
  Angle = 360
  AttacherType = Attacher::AttachEngine3D
  Height = 10
  Placement = pos=(0,0,36.15) rot=(0,0,1;0rad)
  Radius = 4
FEATURE [Part::Cylinder] Cylinder019
  Angle = 360
  AttacherType = Attacher::AttachEngine3D
  Height = 20
  Placement = pos=(0,0,36.15) rot=(0,0,1;0rad)
  Radius = 10.3
FEATURE [Part::MultiFuse] Fusion036  label="removeToCreteHoleForPlugHousing006"
  Placement = pos=(70,19,36) rot=(0,1,0;1.5708rad)
  Shapes = -> [Cylinder019,Cylinder018]
FEATURE [Part::Cut] Cut010  label="plugHousingTab002"
  Base = -> Box006
  Placement = pos=(-107.4,-14,0) rot=(0,0,1;0rad)
  Tool = -> Fusion036
FEATURE [Part::MultiFuse] Fusion037
  Placement = pos=(9.6,23,0) rot=(0,0,1;3.14159rad)
  Shapes = -> [Cut009,Cut010]
FEATURE [Part::Box] Box  label="Cube"
  AttacherType = Attacher::AttachEngine3D
  Height = 10
  Length = 3
  Placement = pos=(3.3,4,12) rot=(0,0,1;0rad)
  Width = 10
FEATURE [Part::Fillet] Fillet004
  Base = -> Fusion028
  Edges = 1 edges r=2: [Edge25]
FEATURE [Part::Fillet] Fillet005  label="plugHousing046"
  Base = -> Fillet004
  Edges = 1 edges r=2: [Edge8]
FEATURE [Part::Fillet] Fillet006
  Base = -> Box
  Edges = 1 edges r=2: [Edge11]
FEATURE [Part::Box] Box007  label="Cube007"
  AttacherType = Attacher::AttachEngine3D
  Height = 10
  Length = 3
  Placement = pos=(3.3,4,50) rot=(0,0,1;0rad)
  Width = 10
FEATURE [Part::Fillet] Fillet007
  Base = -> Box007
  Edges = 1 edges r=2: [Edge12]
FEATURE [Part::Box] Box008  label="Cube008"
  AttacherType = Attacher::AttachEngine3D
  Height = 28
  Length = 4
  Placement = pos=(5,0,22) rot=(0,0,1;0rad)
  Width = 10
FEATURE [Part::Fillet] Fillet008
  Base = -> Box008
  Edges = 1 edges r=1: [Edge7]
FEATURE [Part::Fillet] Fillet009
  Base = -> Fillet008
  Edges = 1 edges r=2: [Edge5]
FEATURE [Part::Fillet] Fillet010
  Base = -> Fillet009
  Edges = 1 edges r=2: [Edge2]
FEATURE [Sketcher::SketchObject] Sketch009  label="topSketch003"
  FullyConstrained = true
  sketch-geometry (4):
    g0: LineSegment StartX=16.8446 StartY=31.512 StartZ=0 EndX=16.3251 EndY=34.4666 EndZ=0
    g1: ArcOfCircle CenterX=19 CenterY=19.2524 CenterZ=0 NormalX=0 NormalY=0 NormalZ=1 AngleXU=0 Radius=15.4476 StartAngle=1.74483 EndAngle=2.72717
    g2: ArcOfCircle CenterX=19 CenterY=19.2524 CenterZ=0 NormalX=0 NormalY=0 NormalZ=1 AngleXU=0 Radius=12.4476 StartAngle=1.74483 EndAngle=2.73189
    g3: LineSegment StartX=4.86004 StartY=25.4725 StartZ=0 EndX=7.58253 EndY=24.2107 EndZ=0
  constraints (7):
    c: Block(g0)
    c: Coincident(g1,g0)
    c: Coincident(g2,g0)
    c: Coincident(g3,g1)
    c: Coincident(g3,g2)
    c: Block(g1)
    c: Block(g2)
FEATURE [Part::Extrusion] Extrude008
  Base = -> Sketch009
  Dir = (0,0,1)
  DirMode = 2
  FaceMakerClass = Part::FaceMakerBullseye
  LengthFwd = 10
  LengthRev = 0
  Placement = pos=(0,0,31) rot=(0,0,1;0rad)
  Solid = true
  Symmetric = false
FEATURE [Part::Cylinder] Cylinder020
  Angle = 360
  AttacherType = Attacher::AttachEngine3D
  Height = 20
  Placement = pos=(0,0,36.15) rot=(0,0,1;0rad)
  Radius = 8.2
FEATURE [Part::Cylinder] Cylinder021
  Angle = 360
  AttacherType = Attacher::AttachEngine3D
  Height = 10
  Placement = pos=(0,0,36.15) rot=(0,0,1;0rad)
  Radius = 4
FEATURE [Part::MultiFuse] Fusion038  label="removeToCreteHoleForPlugHousing007"
  Placement = pos=(-42,19,36) rot=(0,1,0;1.5708rad)
  Shapes = -> [Cylinder020,Cylinder021]
FEATURE [Part::Cut] Cut011
  Base = -> Extrude008
  Tool = -> Fusion038
FEATURE [Part::Fillet] Fillet011
  Base = -> Cut011
  Edges = 1 edges r=2: [Edge1]
FEATURE [Part::Fillet] Fillet012
  Base = -> Fillet011
  Edges = 1 edges r=2.5: [Edge1]
FEATURE [Part::Fillet] Fillet013
  Base = -> Fillet012
  Edges = 1 edges r=2.5: [Edge2]
FEATURE [Part::Box] Box010  label="Cube010"
  AttacherType = Attacher::AttachEngine3D
  Height = 16
  Length = 8
  Placement = pos=(12.7,31.52,28) rot=(0,0,1;0rad)
  Width = 4
FEATURE [Sketcher::SketchObject] Sketch010  label="topSketch004"
  FullyConstrained = true
  sketch-geometry (4):
    g0: LineSegment StartX=16.8446 StartY=31.512 StartZ=0 EndX=16.3251 EndY=34.4666 EndZ=0
    g1: ArcOfCircle CenterX=19 CenterY=19.2524 CenterZ=0 NormalX=0 NormalY=0 NormalZ=1 AngleXU=0 Radius=15.4476 StartAngle=1.74483 EndAngle=2.72717
    g2: ArcOfCircle CenterX=19 CenterY=19.2524 CenterZ=0 NormalX=0 NormalY=0 NormalZ=1 AngleXU=0 Radius=12.4476 StartAngle=1.74483 EndAngle=2.73189
    g3: LineSegment StartX=4.86004 StartY=25.4725 StartZ=0 EndX=7.58253 EndY=24.2107 EndZ=0
  constraints (7):
    c: Block(g0)
    c: Coincident(g1,g0)
    c: Coincident(g2,g0)
    c: Coincident(g3,g1)
    c: Coincident(g3,g2)
    c: Block(g1)
    c: Block(g2)
FEATURE [Part::Cylinder] Cylinder022
  Angle = 360
  AttacherType = Attacher::AttachEngine3D
  Height = 10
  Placement = pos=(0,0,36.15) rot=(0,0,1;0rad)
  Radius = 4
FEATURE [Sketcher::SketchObject] Sketch011  label="topSketch005"
  FullyConstrained = true
  sketch-geometry (4):
    g0: LineSegment StartX=16.8446 StartY=31.512 StartZ=0 EndX=16.3251 EndY=34.4666 EndZ=0
    g1: ArcOfCircle CenterX=19 CenterY=19.2524 CenterZ=0 NormalX=0 NormalY=0 NormalZ=1 AngleXU=0 Radius=15.4476 StartAngle=1.74483 EndAngle=2.72717
    g2: ArcOfCircle CenterX=19 CenterY=19.2524 CenterZ=0 NormalX=0 NormalY=0 NormalZ=1 AngleXU=0 Radius=12.4476 StartAngle=1.74483 EndAngle=2.73189
    g3: LineSegment StartX=4.86004 StartY=25.4725 StartZ=0 EndX=7.58253 EndY=24.2107 EndZ=0
  constraints (7):
    c: Block(g0)
    c: Coincident(g1,g0)
    c: Coincident(g2,g0)
    c: Coincident(g3,g1)
    c: Coincident(g3,g2)
    c: Block(g1)
    c: Block(g2)
FEATURE [Part::Extrusion] Extrude010
  Base = -> Sketch011
  Dir = (0,0,1)
  DirMode = 2
  FaceMakerClass = Part::FaceMakerBullseye
  LengthFwd = 10.6
  LengthRev = 0
  Placement = pos=(0,0,31) rot=(0,0,1;0rad)
  Solid = true
  Symmetric = false
FEATURE [Part::Cylinder] Cylinder023
  Angle = 360
  AttacherType = Attacher::AttachEngine3D
  Height = 20
  Placement = pos=(0,0,36.15) rot=(0,0,1;0rad)
  Radius = 8.2
FEATURE [Part::MultiFuse] Fusion039  label="removeToCreteHoleForPlugHousing008"
  Placement = pos=(-42,19,36) rot=(0,1,0;1.5708rad)
  Shapes = -> [Cylinder023,Cylinder022]
FEATURE [Part::Cut] Cut012
  Base = -> Extrude010
  Placement = pos=(0,0,-0.3) rot=(0,0,1;0rad)
  Tool = -> Fusion039
FEATURE [Part::Cut] Cut013
  Base = -> Box010
  Tool = -> Cut012
FEATURE [Part::Fillet] Fillet014
  Base = -> Cut013
  Edges = 1 edges r=0.7: [Edge13]
FEATURE [Part::Fillet] Fillet015
  Base = -> Fillet014
  Edges = 1 edges r=0.7: [Edge13]
FEATURE [Part::Fillet] Fillet016
  Base = -> Fillet015
  Edges = 1 edges r=0.7: [Edge16]
FEATURE [Part::Fillet] Fillet017
  Base = -> Fillet016
  Edges = 1 edges r=0.7: [Edge11]
FEATURE [Part::Fillet] Fillet018
  Base = -> Fillet017
  Edges = 1 edges r=0.7: [Edge10]
FEATURE [Part::Fillet] Fillet019
  Base = -> Fillet018
  Edges = 1 edges r=1.2: [Edge5]
FEATURE [Part::Fillet] Fillet020
  Base = -> Fillet019
  Edges = 1 edges r=1.2: [Edge12]
FEATURE [Part::Fillet] Fillet021
  Base = -> Fillet020
  Edges = 1 edges r=2: [Edge1]
  Placement = pos=(0.3,0,0) rot=(0,0,1;0rad)
FEATURE [Part::MultiFuse] Fusion040  label="top005"
  Shapes = -> [Cut008,Fillet021]
FEATURE [Part::MultiFuse] Fusion041  label="wireHolder"
  Shapes = -> [Fusion033,Fillet013]
FEATURE [Part::MultiFuse] Fusion042
  Shapes = -> [Fillet007,Fusion041]
FEATURE [Part::MultiFuse] Fusion043  label="wireHolder001"
  Shapes = -> [Fusion042,Fillet010]
FEATURE [Part::MultiFuse] Fusion044  label="wireHolder002"
  Shapes = -> [Fillet006,Fusion037,Fusion043]
FEATURE [Part::Feature] Face026
  shape: bbox 11 x 6 x 2e-07 mm, 1 faces, 0 solids (baked)
FEATURE [Part::Revolution] Revolve026
  Angle = 360
  Axis = (0,1,0)
  Base = (0,0,0)
  FaceMakerClass = Part::FaceMakerBullseye
  Placement = pos=(30.3,-1,19.7) rot=(0,0,1;0rad)
  Solid = false
  Source = -> Face026
  Symmetric = false
FEATURE [Sketcher::SketchObject] Sketch013  label="topSketch006"
  FullyConstrained = true
  sketch-geometry (13):
    g0: LineSegment StartX=117 StartY=19 StartZ=0 EndX=117 EndY=38 EndZ=0
    g1: ArcOfCircle CenterX=98 CenterY=19 CenterZ=0 NormalX=0 NormalY=0 NormalZ=1 AngleXU=0 Radius=19 StartAngle=5.7297 EndAngle=6.28319
    g2: LineSegment StartX=0 StartY=3 StartZ=0 EndX=0 EndY=19 EndZ=0
    g3: LineSegment StartX=19 StartY=38 StartZ=0 EndX=117 EndY=38 EndZ=0
    g4: ArcOfCircle CenterX=19 CenterY=19 CenterZ=0 NormalX=0 NormalY=0 NormalZ=1 AngleXU=0 Radius=19 StartAngle=1.5708 EndAngle=3.14159
    g5: ArcOfCircle CenterX=19 CenterY=19 CenterZ=0 NormalX=0 NormalY=0 NormalZ=1 AngleXU=0 Radius=16 StartAngle=1.5708 EndAngle=3.14159
    g6: ArcOfCircle CenterX=98 CenterY=19 CenterZ=0 NormalX=0 NormalY=0 NormalZ=1 AngleXU=0 Radius=16 StartAngle=5.60905 EndAngle=6.28319
    g7: LineSegment StartX=114 StartY=19 StartZ=0 EndX=114 EndY=35 EndZ=0
    g8: LineSegment StartX=110.5 StartY=9.01251 StartZ=0 EndX=114.163 EndY=9.01251 EndZ=0
    g9: LineSegment StartX=114 StartY=35 StartZ=0 EndX=19 EndY=35 EndZ=0
    g10: LineSegment StartX=0 StartY=3 StartZ=0 EndX=0 EndY=0 EndZ=0
    g11: LineSegment StartX=3 StartY=0 StartZ=0 EndX=0 EndY=0 EndZ=0
    g12: LineSegment StartX=3 StartY=19 StartZ=0 EndX=3 EndY=0 EndZ=0
  constraints (33):
    c: Vertical(g0)
    c: Distance(g0) = 19
    c: Block(g0)
    c: Coincident(g1,g0)
    c: Block(g1)
    c: Vertical(g2)
    c: Block(g2)
    c: Coincident(g3,g0)
    c: Horizontal(g3)
    c: Distance(g3) = 98
    c: Coincident(g4,g3)
    c: Coincident(g4,g2)
    c: Block(g4)
    c: Coincident(g5,g4)
    c: Coincident(g6,g1)
    c: Block(g6)
    c: Block(g5)
    c: Coincident(g7,g6)
    c: Vertical(g7)
    c: Coincident(g8,g6)
    c: Coincident(g8,g1)
    c: Coincident(g9,g7)
    c: Coincident(g9,g5)
    c: Horizontal(g9)
    c: Tangent(g9,g5)
    c: Coincident(g10,g2)
    c: Distance(g10) = 3
    c: Vertical(g10)
    c: Coincident(g11,g10)
    c: Horizontal(g11)
    c: Coincident(g12,g5)
    c: Coincident(g12,g11)
    c: Vertical(g12)
FEATURE [Part::Extrusion] Extrude011  label="top006"
  Base = -> Sketch013
  Dir = (0,0,1)
  DirMode = 2
  FaceMakerClass = Part::FaceMakerBullseye
  LengthFwd = 72
  LengthRev = 0
  Solid = true
  Symmetric = false
FEATURE [Sketcher::SketchObject] Sketch014
  FullyConstrained = true
  MapMode = 3
  Placement = pos=(0,0,0) rot=(1,0,0;1.5708rad)
  Support = -> [Extrude011]
  sketch-geometry (8):
    g0: Circle CenterX=80.351 CenterY=-67.6202 CenterZ=0 NormalX=0 NormalY=0 NormalZ=1 AngleXU=0 Radius=2
    g1: Circle CenterX=80.351 CenterY=-67.6202 CenterZ=0 NormalX=0 NormalY=0 NormalZ=1 AngleXU=0 Radius=3
    g2: Circle CenterX=80.351 CenterY=-4.92017 CenterZ=0 NormalX=0 NormalY=0 NormalZ=1 AngleXU=0 Radius=2
    g3: Circle CenterX=80.351 CenterY=-4.92017 CenterZ=0 NormalX=0 NormalY=0 NormalZ=1 AngleXU=0 Radius=3
    g4: Circle CenterX=23.851 CenterY=-4.92017 CenterZ=0 NormalX=0 NormalY=0 NormalZ=1 AngleXU=0 Radius=2
    g5: Circle CenterX=23.851 CenterY=-4.92017 CenterZ=0 NormalX=0 NormalY=0 NormalZ=1 AngleXU=0 Radius=3
    g6: Circle CenterX=23.851 CenterY=-67.6202 CenterZ=0 NormalX=0 NormalY=0 NormalZ=1 AngleXU=0 Radius=2
    g7: Circle CenterX=23.851 CenterY=-67.6202 CenterZ=0 NormalX=0 NormalY=0 NormalZ=1 AngleXU=0 Radius=3
  constraints (8):
    c: Block(g3)
    c: Block(g2)
    c: Block(g1)
    c: Block(g0)
    c: Block(g6)
    c: Block(g7)
    c: Block(g4)
    c: Block(g5)
FEATURE [Part::Feature] Face027
  shape: bbox 11 x 6 x 2e-07 mm, 1 faces, 0 solids (baked)
FEATURE [Part::Revolution] Revolve027
  Angle = 360
  Axis = (0,1,0)
  Base = (0,0,0)
  FaceMakerClass = Part::FaceMakerBullseye
  Placement = pos=(30.3,-1,51.7) rot=(0,0,1;0rad)
  Solid = false
  Source = -> Face027
  Symmetric = false
FEATURE [Part::Feature] Face028
  shape: bbox 11 x 6 x 2e-07 mm, 1 faces, 0 solids (baked)
FEATURE [Part::Revolution] Revolve028
  Angle = 360
  Axis = (0,1,0)
  Base = (0,0,0)
  FaceMakerClass = Part::FaceMakerBullseye
  Placement = pos=(62.3,-1,19.7) rot=(0,0,1;0rad)
  Solid = false
  Source = -> Face028
  Symmetric = false
FEATURE [Part::Feature] Face029
  shape: bbox 11 x 6 x 2e-07 mm, 1 faces, 0 solids (baked)
FEATURE [Part::Revolution] Revolve029
  Angle = 360
  Axis = (0,1,0)
  Base = (0,0,0)
  FaceMakerClass = Part::FaceMakerBullseye
  Placement = pos=(62.3,-1,51.7) rot=(0,0,1;0rad)
  Solid = false
  Source = -> Face029
  Symmetric = false
FEATURE [Part::Feature] Wire
  shape: bbox 11 x 5.2 x 2e-07 mm, 0 faces, 0 solids (baked)
FEATURE [Part::Revolution] Revolve030
  Angle = 360
  Axis = (0,1,0)
  Base = (0,0,0)
  FaceMakerClass = Part::FaceMakerBullseye
  Placement = pos=(30.3,38,19.7) rot=(0,0,1;0rad)
  Solid = true
  Source = -> Wire
  Symmetric = false
FEATURE [Part::Feature] Wire001
  shape: bbox 11 x 5.2 x 2e-07 mm, 0 faces, 0 solids (baked)
FEATURE [Part::Revolution] Revolve031
  Angle = 360
  Axis = (0,1,0)
  Base = (0,0,0)
  FaceMakerClass = Part::FaceMakerBullseye
  Placement = pos=(30.3,38,51.7) rot=(0,0,1;0rad)
  Solid = true
  Source = -> Wire001
  Symmetric = false
FEATURE [Part::Feature] Wire002
  shape: bbox 11 x 5.2 x 2e-07 mm, 0 faces, 0 solids (baked)
FEATURE [Part::Revolution] Revolve032
  Angle = 360
  Axis = (0,1,0)
  Base = (0,0,0)
  FaceMakerClass = Part::FaceMakerBullseye
  Placement = pos=(62.3,38,51.7) rot=(0,0,1;0rad)
  Solid = true
  Source = -> Wire002
  Symmetric = false
FEATURE [Part::Feature] Wire003
  shape: bbox 11 x 5.2 x 2e-07 mm, 0 faces, 0 solids (baked)
FEATURE [Part::Revolution] Revolve033
  Angle = 360
  Axis = (0,1,0)
  Base = (0,0,0)
  FaceMakerClass = Part::FaceMakerBullseye
  Placement = pos=(62.3,38,19.7) rot=(0,0,1;0rad)
  Solid = true
  Source = -> Wire003
  Symmetric = false
FEATURE [Part::MultiFuse] Fusion045  label="altRandScrewHousing"
  Shapes = -> [Revolve029,Revolve027,Revolve028,Revolve026]
FEATURE [Part::MultiFuse] Fusion046  label="fanScrewHousing"
  Shapes = -> [Revolve033,Revolve032,Revolve031,Revolve030]
FEATURE [Sketcher::SketchObject] Sketch015
  FullyConstrained = true
  sketch-geometry (17):
    g0: Circle CenterX=-3.5 CenterY=23.5 CenterZ=0 NormalX=0 NormalY=0 NormalZ=1 AngleXU=0 Radius=1
    g1: Circle CenterX=-1 CenterY=15.25 CenterZ=0 NormalX=0 NormalY=0 NormalZ=1 AngleXU=0 Radius=1
    g2: Circle CenterX=-3.5 CenterY=7 CenterZ=0 NormalX=0 NormalY=0 NormalZ=1 AngleXU=0 Radius=1
    g3: BSplineCurve PolesCount=3 KnotsCount=2 Degree=2 IsPeriodic=0
    g4: GeomPoint X=-3.5 Y=23.5 Z=0
    g5: GeomPoint X=-3.5 Y=7 Z=0
    g6: Circle CenterX=-4.8 CenterY=30.5 CenterZ=0 NormalX=0 NormalY=0 NormalZ=1 AngleXU=0 Radius=1
    g7: Circle CenterX=-3.5 CenterY=30.5 CenterZ=0 NormalX=0 NormalY=0 NormalZ=1 AngleXU=0 Radius=1
    g8: Circle CenterX=-3.5 CenterY=29.2 CenterZ=0 NormalX=0 NormalY=0 NormalZ=1 AngleXU=0 Radius=1
    g9: BSplineCurve PolesCount=3 KnotsCount=2 Degree=2 IsPeriodic=0
    g10: GeomPoint X=-4.8 Y=30.5 Z=0
    g11: GeomPoint X=-3.5 Y=29.2 Z=0
    g12: LineSegment StartX=-3.5 StartY=29.2 StartZ=0 EndX=-3.5 EndY=23.5 EndZ=0
    g13: LineSegment StartX=-4.8 StartY=30.5 StartZ=0 EndX=0 EndY=30.5 EndZ=0
    g14: LineSegment StartX=-3.5 StartY=0.3 StartZ=0 EndX=0 EndY=0.3 EndZ=0
    g15: LineSegment StartX=-3.5 StartY=0.3 StartZ=0 EndX=-3.5 EndY=7 EndZ=0
    g16: LineSegment StartX=0 StartY=0.3 StartZ=0 EndX=0 EndY=30.5 EndZ=0
  constraints (33):
    c: Weight(g0) = 1
    c: Equal(g0,g1)
    c: Equal(g0,g2)
    c: InternalAlignment(g0,g3)
    c: InternalAlignment(g1,g3)
    c: InternalAlignment(g2,g3)
    c: InternalAlignment(g4,g3)
    c: InternalAlignment(g5,g3)
    c: Block(g3)
    c: Weight(g6) = 1
    c: Equal(g6,g7)
    c: Equal(g6,g8)
    c: InternalAlignment(g6,g9)
    c: InternalAlignment(g7,g9)
    c: InternalAlignment(g8,g9)
    c: InternalAlignment(g10,g9)
    c: InternalAlignment(g11,g9)
    c: Block(g9)
    c: Coincident(g12,g9)
    c: Coincident(g12,g3)
    c: Vertical(g12)
    c: Coincident(g13,g9)
    c: Horizontal(g13)
    c: Distance(g13) = 4.8
    c: Horizontal(g14)
    c: Block(g14)
    c: Coincident(g15,g14)
    c: Coincident(g15,g3)
    c: Vertical(g15)
    c: Coincident(g16,g14)
    c: Coincident(g16,g13)
    c: Vertical(g16)
    c: Tangent(g16,g1)
FEATURE [Sketcher::SketchObject] Sketch016
  FullyConstrained = true
  sketch-geometry (16):
    g0: Circle CenterX=-3.5 CenterY=23.5 CenterZ=0 NormalX=0 NormalY=0 NormalZ=1 AngleXU=0 Radius=1
    g1: Circle CenterX=-1 CenterY=15.25 CenterZ=0 NormalX=0 NormalY=0 NormalZ=1 AngleXU=0 Radius=1
    g2: Circle CenterX=-3.5 CenterY=7 CenterZ=0 NormalX=0 NormalY=0 NormalZ=1 AngleXU=0 Radius=1
    g3: BSplineCurve PolesCount=3 KnotsCount=2 Degree=2 IsPeriodic=0
    g4: GeomPoint X=-3.5 Y=23.5 Z=0
    g5: GeomPoint X=-3.5 Y=7 Z=0
    g6: LineSegment StartX=-3.5 StartY=28.2 StartZ=0 EndX=-3.5 EndY=23.5 EndZ=0
    g7: LineSegment StartX=0 StartY=29.5 StartZ=0 EndX=0 EndY=30 EndZ=0
    g8: LineSegment StartX=-3.5 StartY=28.2 StartZ=0 EndX=-3.5 EndY=30 EndZ=0
    g9: LineSegment StartX=0 StartY=30 StartZ=0 EndX=0 EndY=30.5 EndZ=0
    g10: LineSegment StartX=0 StartY=30.5 StartZ=0 EndX=-3.5 EndY=30.5 EndZ=0
    g11: LineSegment StartX=-3.5 StartY=30.5 StartZ=0 EndX=-3.5 EndY=30 EndZ=0
    g12: LineSegment StartX=0 StartY=29.5 StartZ=0 EndX=0 EndY=5 EndZ=0
    g13: LineSegment StartX=-3.5 StartY=0.3 StartZ=0 EndX=-3.5 EndY=7 EndZ=0
    g14: LineSegment StartX=-3.5 StartY=0.3 StartZ=0 EndX=0 EndY=0.3 EndZ=0
    g15: LineSegment StartX=0 StartY=5 StartZ=0 EndX=0 EndY=0.3 EndZ=0
  constraints (39):
    c: Weight(g0) = 1
    c: Equal(g0,g1)
    c: Equal(g0,g2)
    c: InternalAlignment(g0,g3)
    c: InternalAlignment(g1,g3)
    c: InternalAlignment(g2,g3)
    c: InternalAlignment(g4,g3)
    c: InternalAlignment(g5,g3)
    c: Block(g3)
    c: Coincident(g6,g3)
    c: Vertical(g6)
    c: Vertical(g7)
    c: Distance(g7) = 0.5
    c: Coincident(g8,g6)
    c: Vertical(g8)
    c: Block(g6)
    c: Block(g7)
    c: Vertical(g9)
    c: Equal(g7,g9) = 0.5
    c: Block(g9)
    c: Coincident(g9,g7)
    c: Horizontal(g10)
    c: Coincident(g10,g9)
    c: Coincident(g11,g10)
    c: Coincident(g11,g8)
    c: Vertical(g11)
    c: Block(g11)
    c: Coincident(g12,g7)
    c: Vertical(g12)
    c: Coincident(g13,g3)
    c: Vertical(g13)
    c: Distance(g13) = 6.7
    c: Coincident(g14,g13)
    c: Horizontal(g14)
    c: Block(g14)
    c: Coincident(g15,g12)
    c: Coincident(g15,g14)
    c: Vertical(g15)
    c: Block(g15)
FEATURE [Sketcher::SketchObject] Sketch017
  FullyConstrained = true
  sketch-geometry (11):
    g0: LineSegment StartX=-3.5 StartY=1e-16 StartZ=0 EndX=-1.6 EndY=1e-16 EndZ=0
    g1: LineSegment StartX=-1.6 StartY=1e-16 StartZ=0 EndX=-1.6 EndY=1.5 EndZ=0
    g2: LineSegment StartX=-3.5 StartY=1.5 StartZ=0 EndX=-1.6 EndY=1.5 EndZ=0
    g3: LineSegment StartX=-3.5 StartY=1e-16 StartZ=0 EndX=-4.8 EndY=1e-16 EndZ=0
    g4: Circle CenterX=-3.5 CenterY=1.3 CenterZ=0 NormalX=0 NormalY=0 NormalZ=1 AngleXU=0 Radius=1
    g5: Circle CenterX=-3.5 CenterY=1e-16 CenterZ=0 NormalX=0 NormalY=0 NormalZ=1 AngleXU=0 Radius=1
    g6: Circle CenterX=-4.8 CenterY=1e-16 CenterZ=0 NormalX=0 NormalY=0 NormalZ=1 AngleXU=0 Radius=1
    g7: BSplineCurve PolesCount=3 KnotsCount=2 Degree=2 IsPeriodic=0
    g8: GeomPoint X=-3.5 Y=1.3 Z=0
    g9: GeomPoint X=-4.8 Y=1e-16 Z=0
    g10: LineSegment StartX=-3.5 StartY=1.3 StartZ=0 EndX=-3.5 EndY=1.5 EndZ=0
  constraints (24):
    c: Horizontal(g0)
    c: Distance(g0) = 1.9
    c: Block(g0)
    c: Coincident(g1,g0)
    c: Vertical(g1)
    c: Coincident(g2,g1)
    c: Horizontal(g2)
    c: Coincident(g3,g0)
    c: Horizontal(g3)
    c: Distance(g3) = 1.3
    c: Weight(g4) = 1
    c: Equal(g4,g5)
    c: Coincident(g5,g0)
    c: Equal(g4,g6)
    c: Coincident(g7,g3)
    c: InternalAlignment(g4,g7)
    c: InternalAlignment(g5,g7)
    c: InternalAlignment(g6,g7)
    c: InternalAlignment(g8,g7)
    c: InternalAlignment(g9,g7)
    c: Coincident(g10,g7)
    c: Coincident(g10,g2)
    c: Vertical(g10)
    c: Block(g10)
FEATURE [Part::Feature] Face035
  shape: bbox 3.2 x 1.5 x 2e-07 mm, 1 faces, 0 solids (baked)
FEATURE [Part::Revolution] Revolve039  label="backCaseScrewRetainer"
  Angle = 360
  Axis = (0,1,0)
  Base = (0,0,0)
  FaceMakerClass = Part::FaceMakerBullseye
  Placement = pos=(12.5,3,62) rot=(0,0,1;0rad)
  Solid = false
  Source = -> Face035
  Symmetric = false
FEATURE [Part::Feature] Face036
  shape: bbox 3.2 x 1.5 x 2e-07 mm, 1 faces, 0 solids (baked)
FEATURE [Part::Feature] Face039
  shape: bbox 4.8 x 30.2 x 2e-07 mm, 1 faces, 0 solids (baked)
FEATURE [Part::Revolution] Revolve043  label="frontCaseScrewPost002"
  Angle = 360
  Axis = (0,1,0)
  Base = (0,0,0)
  FaceMakerClass = Part::FaceMakerBullseye
  Placement = pos=(89.5,4.5,3.5) rot=(0,0,1;0rad)
  Solid = false
  Source = -> Face039
  Symmetric = false
FEATURE [Part::Feature] Face042
  shape: bbox 4.8 x 30.2 x 2e-07 mm, 1 faces, 0 solids (baked)
FEATURE [Part::Revolution] Revolve046  label="frontCaseScrewPost003"
  Angle = 360
  Axis = (0,1,0)
  Base = (0,0,0)
  FaceMakerClass = Part::FaceMakerBullseye
  Placement = pos=(89.5,4.5,68.5) rot=(0,0,1;0rad)
  Solid = false
  Source = -> Face042
  Symmetric = false
FEATURE [Part::Feature] Face043
  shape: bbox 3.2 x 1.5 x 2e-07 mm, 1 faces, 0 solids (baked)
FEATURE [Part::Revolution] Revolve047  label="frontCaseScrewRetainer002"
  Angle = 360
  Axis = (0,1,0)
  Base = (0,0,0)
  FaceMakerClass = Part::FaceMakerBullseye
  Placement = pos=(89.5,3,68.5) rot=(0,0,1;0rad)
  Solid = false
  Source = -> Face043
  Symmetric = false
FEATURE [Part::Feature] Face044
  shape: bbox 3.2 x 1.5 x 2e-07 mm, 1 faces, 0 solids (baked)
FEATURE [Part::Revolution] Revolve048  label="frontCaseScrewRetainer003"
  Angle = 360
  Axis = (0,1,0)
  Base = (0,0,0)
  FaceMakerClass = Part::FaceMakerBullseye
  Placement = pos=(89.5,3,3.5) rot=(0,0,1;0rad)
  Solid = false
  Source = -> Face044
  Symmetric = false
FEATURE [App::MeasureDistance] Distance002  label="Distance: 1.67 mm"
  Distance = 1.66921
  P1 = (99.2361,4.7524,71.7)
  P2 = (99.2347,6.42161,71.7)
FEATURE [Sketcher::SketchObject] Sketch018
  FullyConstrained = true
  sketch-geometry (7):
    g0: LineSegment StartX=0 StartY=0 StartZ=0 EndX=0 EndY=6 EndZ=0
    g1: Circle CenterX=0 CenterY=0 CenterZ=0 NormalX=0 NormalY=0 NormalZ=1 AngleXU=0 Radius=1
    g2: Circle CenterX=8 CenterY=6 CenterZ=0 NormalX=0 NormalY=0 NormalZ=1 AngleXU=0 Radius=1
    g3: BSplineCurve PolesCount=3 KnotsCount=2 Degree=2 IsPeriodic=0
    g4: GeomPoint X=0 Y=0 Z=0
    g5: GeomPoint X=8 Y=6 Z=0
    g6: LineSegment StartX=0 StartY=6 StartZ=0 EndX=8 EndY=6 EndZ=0
  constraints (14):
    c: Coincident(g0,g-1)
    c: Distance(g0) = 6
    c: Vertical(g0)
    c: Coincident(g3,g0)
    c: Weight(g1) = 1
    c: Equal(g1,g2)
    c: InternalAlignment(g1,g3)
    c: InternalAlignment(g2,g3)
    c: InternalAlignment(g4,g3)
    c: InternalAlignment(g5,g3)
    c: Block(g3)
    c: Coincident(g6,g0)
    c: Coincident(g6,g3)
    c: Horizontal(g6)
FEATURE [Part::Extrusion] Extrude012  label="caseScrewPillarBracket"
  Base = -> Sketch018
  Dir = (0,0,1)
  DirMode = 2
  FaceMakerClass = Part::FaceMakerBullseye
  LengthFwd = 2.4
  LengthRev = 0
  Placement = pos=(15.76,29,8.8) rot=(0,1,0;0rad)
  Solid = true
  Symmetric = false
FEATURE [Sketcher::SketchObject] Sketch019
  FullyConstrained = true
  sketch-geometry (7):
    g0: LineSegment StartX=0 StartY=0 StartZ=0 EndX=0 EndY=6 EndZ=0
    g1: Circle CenterX=0 CenterY=0 CenterZ=0 NormalX=0 NormalY=0 NormalZ=1 AngleXU=0 Radius=1
    g2: Circle CenterX=8 CenterY=6 CenterZ=0 NormalX=0 NormalY=0 NormalZ=1 AngleXU=0 Radius=1
    g3: BSplineCurve PolesCount=3 KnotsCount=2 Degree=2 IsPeriodic=0
    g4: GeomPoint X=0 Y=0 Z=0
    g5: GeomPoint X=8 Y=6 Z=0
    g6: LineSegment StartX=0 StartY=6 StartZ=0 EndX=8 EndY=6 EndZ=0
  constraints (14):
    c: Coincident(g0,g-1)
    c: Distance(g0) = 6
    c: Vertical(g0)
    c: Coincident(g3,g0)
    c: Weight(g1) = 1
    c: Equal(g1,g2)
    c: InternalAlignment(g1,g3)
    c: InternalAlignment(g2,g3)
    c: InternalAlignment(g4,g3)
    c: InternalAlignment(g5,g3)
    c: Block(g3)
    c: Coincident(g6,g0)
    c: Coincident(g6,g3)
    c: Horizontal(g6)
FEATURE [Part::Extrusion] Extrude013  label="caseScrewPillarBracket001"
  Base = -> Sketch019
  Dir = (0,0,1)
  DirMode = 2
  FaceMakerClass = Part::FaceMakerBullseye
  LengthFwd = 2.4
  LengthRev = 0
  Placement = pos=(15.76,29,60.8) rot=(0,0,1;0rad)
  Solid = true
  Symmetric = false
FEATURE [Sketcher::SketchObject] Sketch020
  FullyConstrained = true
  sketch-geometry (7):
    g0: LineSegment StartX=0 StartY=0 StartZ=0 EndX=0 EndY=6 EndZ=0
    g1: Circle CenterX=0 CenterY=0 CenterZ=0 NormalX=0 NormalY=0 NormalZ=1 AngleXU=0 Radius=1
    g2: Circle CenterX=8 CenterY=6 CenterZ=0 NormalX=0 NormalY=0 NormalZ=1 AngleXU=0 Radius=1
    g3: BSplineCurve PolesCount=3 KnotsCount=2 Degree=2 IsPeriodic=0
    g4: GeomPoint X=0 Y=0 Z=0
    g5: GeomPoint X=8 Y=6 Z=0
    g6: LineSegment StartX=0 StartY=6 StartZ=0 EndX=8 EndY=6 EndZ=0
  constraints (14):
    c: Coincident(g0,g-1)
    c: Distance(g0) = 6
    c: Vertical(g0)
    c: Coincident(g3,g0)
    c: Weight(g1) = 1
    c: Equal(g1,g2)
    c: InternalAlignment(g1,g3)
    c: InternalAlignment(g2,g3)
    c: InternalAlignment(g4,g3)
    c: InternalAlignment(g5,g3)
    c: Block(g3)
    c: Coincident(g6,g0)
    c: Coincident(g6,g3)
    c: Horizontal(g6)
FEATURE [Part::Extrusion] Extrude014  label="caseScrewPillarBracket002"
  Base = -> Sketch020
  Dir = (0,0,1)
  DirMode = 2
  FaceMakerClass = Part::FaceMakerBullseye
  LengthFwd = 2.4
  LengthRev = 0
  Placement = pos=(13.7,29,13.26) rot=(0,-1,0;1.5708rad)
  Solid = true
  Symmetric = false
FEATURE [Sketcher::SketchObject] Sketch021
  FullyConstrained = true
  sketch-geometry (7):
    g0: LineSegment StartX=0 StartY=0 StartZ=0 EndX=0 EndY=6 EndZ=0
    g1: Circle CenterX=0 CenterY=0 CenterZ=0 NormalX=0 NormalY=0 NormalZ=1 AngleXU=0 Radius=1
    g2: Circle CenterX=8 CenterY=6 CenterZ=0 NormalX=0 NormalY=0 NormalZ=1 AngleXU=0 Radius=1
    g3: BSplineCurve PolesCount=3 KnotsCount=2 Degree=2 IsPeriodic=0
    g4: GeomPoint X=0 Y=0 Z=0
    g5: GeomPoint X=8 Y=6 Z=0
    g6: LineSegment StartX=0 StartY=6 StartZ=0 EndX=8 EndY=6 EndZ=0
  constraints (14):
    c: Coincident(g0,g-1)
    c: Distance(g0) = 6
    c: Vertical(g0)
    c: Coincident(g3,g0)
    c: Weight(g1) = 1
    c: Equal(g1,g2)
    c: InternalAlignment(g1,g3)
    c: InternalAlignment(g2,g3)
    c: InternalAlignment(g4,g3)
    c: InternalAlignment(g5,g3)
    c: Block(g3)
    c: Coincident(g6,g0)
    c: Coincident(g6,g3)
    c: Horizontal(g6)
FEATURE [Part::Extrusion] Extrude015  label="caseScrewPillarBracket003"
  Base = -> Sketch021
  Dir = (0,0,1)
  DirMode = 2
  FaceMakerClass = Part::FaceMakerBullseye
  LengthFwd = 2.4
  LengthRev = 0
  Placement = pos=(11.3,29,58.74) rot=(0,1,0;1.5708rad)
  Solid = true
  Symmetric = false
FEATURE [Sketcher::SketchObject] Sketch022
  FullyConstrained = true
  sketch-geometry (7):
    g0: LineSegment StartX=0 StartY=0 StartZ=0 EndX=0 EndY=6 EndZ=0
    g1: Circle CenterX=0 CenterY=0 CenterZ=0 NormalX=0 NormalY=0 NormalZ=1 AngleXU=0 Radius=1
    g2: Circle CenterX=8 CenterY=6 CenterZ=0 NormalX=0 NormalY=0 NormalZ=1 AngleXU=0 Radius=1
    g3: BSplineCurve PolesCount=3 KnotsCount=2 Degree=2 IsPeriodic=0
    g4: GeomPoint X=0 Y=0 Z=0
    g5: GeomPoint X=8 Y=6 Z=0
    g6: LineSegment StartX=0 StartY=6 StartZ=0 EndX=8 EndY=6 EndZ=0
  constraints (14):
    c: Coincident(g0,g-1)
    c: Distance(g0) = 6
    c: Vertical(g0)
    c: Coincident(g3,g0)
    c: Weight(g1) = 1
    c: Equal(g1,g2)
    c: InternalAlignment(g1,g3)
    c: InternalAlignment(g2,g3)
    c: InternalAlignment(g4,g3)
    c: InternalAlignment(g5,g3)
    c: Block(g3)
    c: Coincident(g6,g0)
    c: Coincident(g6,g3)
    c: Horizontal(g6)
FEATURE [Part::Extrusion] Extrude016  label="caseScrewPillarBracket004"
  Base = -> Sketch022
  Dir = (0,0,1)
  DirMode = 2
  FaceMakerClass = Part::FaceMakerBullseye
  LengthFwd = 2.4
  LengthRev = 0
  Placement = pos=(88.3,29,65.23) rot=(0,1,0;1.5708rad)
  Solid = true
  Symmetric = false
FEATURE [Sketcher::SketchObject] Sketch023
  FullyConstrained = true
  sketch-geometry (7):
    g0: LineSegment StartX=0 StartY=0 StartZ=0 EndX=0 EndY=6 EndZ=0
    g1: Circle CenterX=0 CenterY=0 CenterZ=0 NormalX=0 NormalY=0 NormalZ=1 AngleXU=0 Radius=1
    g2: Circle CenterX=8 CenterY=6 CenterZ=0 NormalX=0 NormalY=0 NormalZ=1 AngleXU=0 Radius=1
    g3: BSplineCurve PolesCount=3 KnotsCount=2 Degree=2 IsPeriodic=0
    g4: GeomPoint X=0 Y=0 Z=0
    g5: GeomPoint X=8 Y=6 Z=0
    g6: LineSegment StartX=0 StartY=6 StartZ=0 EndX=8 EndY=6 EndZ=0
  constraints (14):
    c: Coincident(g0,g-1)
    c: Distance(g0) = 6
    c: Vertical(g0)
    c: Coincident(g3,g0)
    c: Weight(g1) = 1
    c: Equal(g1,g2)
    c: InternalAlignment(g1,g3)
    c: InternalAlignment(g2,g3)
    c: InternalAlignment(g4,g3)
    c: InternalAlignment(g5,g3)
    c: Block(g3)
    c: Coincident(g6,g0)
    c: Coincident(g6,g3)
    c: Horizontal(g6)
FEATURE [Part::Extrusion] Extrude017  label="caseScrewPillarBracket005"
  Base = -> Sketch023
  Dir = (0,0,1)
  DirMode = 2
  FaceMakerClass = Part::FaceMakerBullseye
  LengthFwd = 2.4
  LengthRev = 0
  Placement = pos=(90.7,29,6.77) rot=(0,-1,0;1.5708rad)
  Solid = true
  Symmetric = false
FEATURE [Sketcher::SketchObject] Sketch024
  FullyConstrained = true
  sketch-geometry (7):
    g0: LineSegment StartX=0 StartY=0 StartZ=0 EndX=0 EndY=6 EndZ=0
    g1: Circle CenterX=0 CenterY=0 CenterZ=0 NormalX=0 NormalY=0 NormalZ=1 AngleXU=0 Radius=1
    g2: Circle CenterX=8 CenterY=6 CenterZ=0 NormalX=0 NormalY=0 NormalZ=1 AngleXU=0 Radius=1
    g3: BSplineCurve PolesCount=3 KnotsCount=2 Degree=2 IsPeriodic=0
    g4: GeomPoint X=0 Y=0 Z=0
    g5: GeomPoint X=8 Y=6 Z=0
    g6: LineSegment StartX=0 StartY=6 StartZ=0 EndX=8 EndY=6 EndZ=0
  constraints (14):
    c: Coincident(g0,g-1)
    c: Distance(g0) = 6
    c: Vertical(g0)
    c: Coincident(g3,g0)
    c: Weight(g1) = 1
    c: Equal(g1,g2)
    c: InternalAlignment(g1,g3)
    c: InternalAlignment(g2,g3)
    c: InternalAlignment(g4,g3)
    c: InternalAlignment(g5,g3)
    c: Block(g3)
    c: Coincident(g6,g0)
    c: Coincident(g6,g3)
    c: Horizontal(g6)
FEATURE [Part::Extrusion] Extrude018  label="caseScrewPillarBracket006"
  Base = -> Sketch024
  Dir = (0,0,1)
  DirMode = 2
  FaceMakerClass = Part::FaceMakerBullseye
  LengthFwd = 2.4
  LengthRev = 0
  Placement = pos=(103.7,29,6.77) rot=(0,-1,0;1.5708rad)
  Solid = true
  Symmetric = false
FEATURE [Sketcher::SketchObject] Sketch025
  FullyConstrained = true
  sketch-geometry (7):
    g0: LineSegment StartX=0 StartY=0 StartZ=0 EndX=0 EndY=6 EndZ=0
    g1: Circle CenterX=0 CenterY=0 CenterZ=0 NormalX=0 NormalY=0 NormalZ=1 AngleXU=0 Radius=1
    g2: Circle CenterX=8 CenterY=6 CenterZ=0 NormalX=0 NormalY=0 NormalZ=1 AngleXU=0 Radius=1
    g3: BSplineCurve PolesCount=3 KnotsCount=2 Degree=2 IsPeriodic=0
    g4: GeomPoint X=0 Y=0 Z=0
    g5: GeomPoint X=8 Y=6 Z=0
    g6: LineSegment StartX=0 StartY=6 StartZ=0 EndX=8 EndY=6 EndZ=0
  constraints (14):
    c: Coincident(g0,g-1)
    c: Distance(g0) = 6
    c: Vertical(g0)
    c: Coincident(g3,g0)
    c: Weight(g1) = 1
    c: Equal(g1,g2)
    c: InternalAlignment(g1,g3)
    c: InternalAlignment(g2,g3)
    c: InternalAlignment(g4,g3)
    c: InternalAlignment(g5,g3)
    c: Block(g3)
    c: Coincident(g6,g0)
    c: Coincident(g6,g3)
    c: Horizontal(g6)
FEATURE [Part::Extrusion] Extrude019  label="caseScrewPillarBracket007"
  Base = -> Sketch025
  Dir = (0,0,1)
  DirMode = 2
  FaceMakerClass = Part::FaceMakerBullseye
  LengthFwd = 2.4
  LengthRev = 0
  Placement = pos=(101.3,29,65.23) rot=(0,1,0;1.5708rad)
  Solid = true
  Symmetric = false
FEATURE [Part::Box] Box011  label="frontCaseScrewPillarBracket"
  AttacherType = Attacher::AttachEngine3D
  Height = 2.4
  Length = 16
  Placement = pos=(87,28,2.3) rot=(0,0,1;0rad)
  Width = 7
FEATURE [Part::Box] Box012  label="frontCaseScrewPillarBracket001"
  AttacherType = Attacher::AttachEngine3D
  Height = 2.4
  Length = 16
  Placement = pos=(87,28,67.3) rot=(0,0,1;0rad)
  Width = 7
FEATURE [Sketcher::SketchObject] Sketch026
  FullyConstrained = true
  sketch-geometry (17):
    g0: Circle CenterX=-3.5 CenterY=23.5 CenterZ=0 NormalX=0 NormalY=0 NormalZ=1 AngleXU=0 Radius=1
    g1: Circle CenterX=-1 CenterY=15.25 CenterZ=0 NormalX=0 NormalY=0 NormalZ=1 AngleXU=0 Radius=1
    g2: Circle CenterX=-3.5 CenterY=7 CenterZ=0 NormalX=0 NormalY=0 NormalZ=1 AngleXU=0 Radius=1
    g3: BSplineCurve PolesCount=3 KnotsCount=2 Degree=2 IsPeriodic=0
    g4: GeomPoint X=-3.5 Y=23.5 Z=0
    g5: GeomPoint X=-3.5 Y=7 Z=0
    g6: Circle CenterX=-4.8 CenterY=30.5 CenterZ=0 NormalX=0 NormalY=0 NormalZ=1 AngleXU=0 Radius=1
    g7: Circle CenterX=-3.5 CenterY=30.5 CenterZ=0 NormalX=0 NormalY=0 NormalZ=1 AngleXU=0 Radius=1
    g8: Circle CenterX=-3.5 CenterY=29.2 CenterZ=0 NormalX=0 NormalY=0 NormalZ=1 AngleXU=0 Radius=1
    g9: BSplineCurve PolesCount=3 KnotsCount=2 Degree=2 IsPeriodic=0
    g10: GeomPoint X=-4.8 Y=30.5 Z=0
    g11: GeomPoint X=-3.5 Y=29.2 Z=0
    g12: LineSegment StartX=-3.5 StartY=29.2 StartZ=0 EndX=-3.5 EndY=23.5 EndZ=0
    g13: LineSegment StartX=-4.8 StartY=30.5 StartZ=0 EndX=0 EndY=30.5 EndZ=0
    g14: LineSegment StartX=-3.5 StartY=5 StartZ=0 EndX=-3.5 EndY=7 EndZ=0
    g15: LineSegment StartX=0 StartY=5 StartZ=0 EndX=0 EndY=30.5 EndZ=0
    g16: LineSegment StartX=-3.5 StartY=5 StartZ=0 EndX=0 EndY=5 EndZ=0
  constraints (33):
    c: Weight(g0) = 1
    c: Equal(g0,g1)
    c: Equal(g0,g2)
    c: InternalAlignment(g0,g3)
    c: InternalAlignment(g1,g3)
    c: InternalAlignment(g2,g3)
    c: InternalAlignment(g4,g3)
    c: InternalAlignment(g5,g3)
    c: Block(g3)
    c: Weight(g6) = 1
    c: Equal(g6,g7)
    c: Equal(g6,g8)
    c: InternalAlignment(g6,g9)
    c: InternalAlignment(g7,g9)
    c: InternalAlignment(g8,g9)
    c: InternalAlignment(g10,g9)
    c: InternalAlignment(g11,g9)
    c: Block(g9)
    c: Coincident(g12,g9)
    c: Coincident(g12,g3)
    c: Vertical(g12)
    c: Coincident(g13,g9)
    c: Horizontal(g13)
    c: Distance(g13) = 4.8
    c: Coincident(g14,g3)
    c: Vertical(g14)
    c: Coincident(g15,g13)
    c: Vertical(g15)
    c: Tangent(g15,g1)
    c: Distance(g14) = 2
    c: Coincident(g16,g14)
    c: Horizontal(g16)
    c: Coincident(g15,g16)
FEATURE [Part::Feature] Face050
  shape: bbox 4.8 x 25.5 x 2e-07 mm, 1 faces, 0 solids (baked)
FEATURE [Part::Revolution] Revolve054  label="moreFrontCaseScrewPost001"
  Angle = 360
  Axis = (0,1,0)
  Base = (0,0,0)
  FaceMakerClass = Part::FaceMakerBullseye
  Placement = pos=(102.5,4.5,3.5) rot=(0,0,1;0rad)
  Solid = false
  Source = -> Face050
  Symmetric = false
FEATURE [Part::Feature] Face051
  shape: bbox 4.8 x 25.5 x 2e-07 mm, 1 faces, 0 solids (baked)
FEATURE [Part::Revolution] Revolve055  label="moreFrontCaseScrewPost002"
  Angle = 360
  Axis = (0,1,0)
  Base = (0,0,0)
  FaceMakerClass = Part::FaceMakerBullseye
  Placement = pos=(102.5,4.5,68.5) rot=(0,0,1;0rad)
  Solid = false
  Source = -> Face051
  Symmetric = false
FEATURE [Sketcher::SketchObject] Sketch027
  FullyConstrained = true
  sketch-geometry (10):
    g0: LineSegment StartX=-1.6 StartY=4.7 StartZ=0 EndX=-1.6 EndY=1.7 EndZ=0
    g1: LineSegment StartX=-3.5 StartY=4.7 StartZ=0 EndX=-1.6 EndY=4.7 EndZ=0
    g2: LineSegment StartX=-1.6 StartY=1.7 StartZ=0 EndX=-1.6 EndY=1.5 EndZ=0
    g3: LineSegment StartX=-1.6 StartY=1.5 StartZ=0 EndX=-5.2 EndY=1.5 EndZ=0
    g4: Circle CenterX=-3.5 CenterY=4.7 CenterZ=0 NormalX=0 NormalY=0 NormalZ=1 AngleXU=0 Radius=1
    g5: Circle CenterX=-3.59627 CenterY=2.99743 CenterZ=0 NormalX=0 NormalY=0 NormalZ=1 AngleXU=0 Radius=1
    g6: Circle CenterX=-5.2 CenterY=1.5 CenterZ=0 NormalX=0 NormalY=0 NormalZ=1 AngleXU=0 Radius=1
    g7: BSplineCurve PolesCount=3 KnotsCount=2 Degree=2 IsPeriodic=0
    g8: GeomPoint X=-3.5 Y=4.7 Z=0
    g9: GeomPoint X=-5.2 Y=1.5 Z=0
  constraints (23):
    c: Vertical(g0)
    c: Distance(g0) = 3
    c: Coincident(g1,g0)
    c: Horizontal(g1)
    c: Block(g0)
    c: Block(g1)
    c: Coincident(g2,g0)
    c: Vertical(g2)
    c: Distance(g2) = 0.2
    c: Coincident(g3,g2)
    c: Horizontal(g3)
    c: Block(g3)
    c: Coincident(g7,g1)
    c: Weight(g4) = 1
    c: Equal(g4,g5)
    c: Equal(g4,g6)
    c: Coincident(g7,g3)
    c: InternalAlignment(g4,g7)
    c: InternalAlignment(g5,g7)
    c: InternalAlignment(g6,g7)
    c: InternalAlignment(g8,g7)
    c: InternalAlignment(g9,g7)
    c: Block(g7)
FEATURE [Sketcher::SketchObject] Sketch028
  FullyConstrained = true
  sketch-geometry (18):
    g0: LineSegment StartX=0 StartY=3e-16 StartZ=0 EndX=0 EndY=1.7 EndZ=0
    g1: LineSegment StartX=-3.5 StartY=0 StartZ=0 EndX=-3.5 EndY=0.9 EndZ=0
    g2: Circle CenterX=-2.7 CenterY=1.7 CenterZ=0 NormalX=0 NormalY=0 NormalZ=1 AngleXU=0 Radius=1
    g3: Circle CenterX=-3.5 CenterY=1.7 CenterZ=0 NormalX=0 NormalY=0 NormalZ=1 AngleXU=0 Radius=1
    g4: Circle CenterX=-3.5 CenterY=0.9 CenterZ=0 NormalX=0 NormalY=0 NormalZ=1 AngleXU=0 Radius=1
    g5: BSplineCurve PolesCount=3 KnotsCount=2 Degree=2 IsPeriodic=0
    g6: GeomPoint X=-2.7 Y=1.7 Z=0
    g7: GeomPoint X=-3.5 Y=0.9 Z=0
    g8: LineSegment StartX=-3.5 StartY=0 StartZ=0 EndX=-3.5 EndY=-7 EndZ=0
    g9: LineSegment StartX=0 StartY=3e-16 StartZ=0 EndX=0 EndY=-7 EndZ=0
    g10: LineSegment StartX=-3.5 StartY=-7 StartZ=0 EndX=0 EndY=-7 EndZ=0
    g11: LineSegment StartX=-2.7 StartY=1.7 StartZ=0 EndX=-1.6 EndY=1.7 EndZ=0
    g12: LineSegment StartX=0 StartY=1.7 StartZ=0 EndX=0 EndY=4.5 EndZ=0
    g13: LineSegment StartX=0 StartY=4.5 StartZ=0 EndX=0 EndY=10.8 EndZ=0
    g14: LineSegment StartX=0 StartY=10.8 StartZ=0 EndX=-2 EndY=10.8 EndZ=0
    g15: LineSegment StartX=-1.6 StartY=4.7 StartZ=0 EndX=-1.6 EndY=1.7 EndZ=0
    g16: LineSegment StartX=-1.6 StartY=4.7 StartZ=0 EndX=-2 EndY=4.7 EndZ=0
    g17: LineSegment StartX=-2 StartY=4.7 StartZ=0 EndX=-2 EndY=10.8 EndZ=0
  constraints (44):
    c: Vertical(g0)
    c: Vertical(g1)
    c: Distance(g1) = 0.9
    c: Block(g0)
    c: Distance(g0) = 1.7
    c: Weight(g2) = 1
    c: Equal(g2,g3)
    c: Equal(g2,g4)
    c: Coincident(g5,g1)
    c: InternalAlignment(g2,g5)
    c: InternalAlignment(g3,g5)
    c: InternalAlignment(g4,g5)
    c: InternalAlignment(g6,g5)
    c: InternalAlignment(g7,g5)
    c: Block(g5)
    c: Coincident(g8,g1)
    c: Vertical(g8)
    c: Distance(g8) = 7
    c: Vertical(g9)
    c: Equal(g8,g9) = 7
    c: Coincident(g9,g0)
    c: Coincident(g10,g8)
    c: Coincident(g10,g9)
    c: Horizontal(g10)
    c: Coincident(g11,g5)
    c: Horizontal(g11)
    c: Coincident(g12,g0)
    c: Vertical(g12)
    c: Distance(g12) = 2.8
    c: Coincident(g13,g12)
    c: Vertical(g13)
    c: Distance(g13) = 6.3
    c: Coincident(g14,g13)
    c: Horizontal(g14)
    c: Distance(g14) = 2
    c: Vertical(g15)
    c: Distance(g15) = 3
    c: Block(g11)
    c: Coincident(g15,g11)
    c: Coincident(g16,g15)
    c: Horizontal(g16)
    c: Coincident(g17,g16)
    c: Coincident(g17,g14)
    c: Vertical(g17)
FEATURE [Part::Revolution] Revolve040  label="backCaseScrewRetainer001"
  Angle = 360
  Axis = (0,1,0)
  Base = (0,0,0)
  FaceMakerClass = Part::FaceMakerBullseye
  Placement = pos=(12.5,3,10) rot=(0,0,1;0rad)
  Solid = false
  Source = -> Face036
  Symmetric = false
FEATURE [Part::Feature] Face055
  shape: bbox 3.5 x 30.2 x 2e-07 mm, 1 faces, 0 solids (baked)
FEATURE [Part::Revolution] Revolve059  label="backCaseScrewPost"
  Angle = 360
  Axis = (0,1,0)
  Base = (0,0,0)
  FaceMakerClass = Part::FaceMakerBullseye
  Placement = pos=(12.5,4.5,10) rot=(0,0,1;0rad)
  Solid = false
  Source = -> Face055
  Symmetric = false
FEATURE [Part::Feature] Face056
  shape: bbox 3.5 x 30.2 x 2e-07 mm, 1 faces, 0 solids (baked)
FEATURE [Part::Revolution] Revolve060  label="backCaseScrewPost001"
  Angle = 360
  Axis = (0,1,0)
  Base = (0,0,0)
  FaceMakerClass = Part::FaceMakerBullseye
  Placement = pos=(12.5,4.5,62) rot=(0,0,1;0rad)
  Solid = false
  Source = -> Face056
  Symmetric = false
FEATURE [Part::Feature] Face057
  shape: bbox 3.5 x 17.8 x 2e-07 mm, 1 faces, 0 solids (baked)
FEATURE [Part::Revolution] Revolve061  label="removeToCreateScrewAndThreadedInsertHole"
  Angle = 360
  Axis = (0,1,0)
  Base = (0,0,0)
  FaceMakerClass = Part::FaceMakerBullseye
  Placement = pos=(12.5,0,10) rot=(0,0,1;0rad)
  Solid = false
  Source = -> Face057
  Symmetric = false
FEATURE [Part::Feature] Face058
  shape: bbox 3.5 x 17.8 x 2e-07 mm, 1 faces, 0 solids (baked)
FEATURE [Part::Revolution] Revolve062  label="removeToCreateScrewAndThreadedInsertHole001"
  Angle = 360
  Axis = (0,1,0)
  Base = (0,0,0)
  FaceMakerClass = Part::FaceMakerBullseye
  Placement = pos=(12.5,0,62) rot=(0,0,1;0rad)
  Solid = false
  Source = -> Face058
  Symmetric = false
FEATURE [Part::Feature] Face059
  shape: bbox 3.5 x 17.8 x 2e-07 mm, 1 faces, 0 solids (baked)
FEATURE [Part::Revolution] Revolve063  label="removeToCreateScrewAndThreadedInsertHole002"
  Angle = 360
  Axis = (0,1,0)
  Base = (0,0,0)
  FaceMakerClass = Part::FaceMakerBullseye
  Placement = pos=(89.5,0,68.5) rot=(0,0,1;0rad)
  Solid = false
  Source = -> Face059
  Symmetric = false
FEATURE [Part::Feature] Face060
  shape: bbox 3.5 x 17.8 x 2e-07 mm, 1 faces, 0 solids (baked)
FEATURE [Part::Revolution] Revolve064  label="removeToCreateScrewAndThreadedInsertHole003"
  Angle = 360
  Axis = (0,1,0)
  Base = (0,0,0)
  FaceMakerClass = Part::FaceMakerBullseye
  Placement = pos=(89.5,0,3.5) rot=(0,0,1;0rad)
  Solid = false
  Source = -> Face060
  Symmetric = false
FEATURE [Part::Feature] Face061
  shape: bbox 3.5 x 17.8 x 2e-07 mm, 1 faces, 0 solids (baked)
FEATURE [Part::Revolution] Revolve065  label="removeToCreateScrewAndThreadedInsertHole004"
  Angle = 360
  Axis = (0,1,0)
  Base = (0,0,0)
  FaceMakerClass = Part::FaceMakerBullseye
  Placement = pos=(102.5,4.7,3.5) rot=(0,0,1;0rad)
  Solid = false
  Source = -> Face061
  Symmetric = false
FEATURE [Part::Feature] Face062
  shape: bbox 3.5 x 17.8 x 2e-07 mm, 1 faces, 0 solids (baked)
FEATURE [Part::Revolution] Revolve066  label="removeToCreateScrewAndThreadedInsertHole005"
  Angle = 360
  Axis = (0,1,0)
  Base = (0,0,0)
  FaceMakerClass = Part::FaceMakerBullseye
  Placement = pos=(102.5,4.7,68.5) rot=(0,0,1;0rad)
  Solid = false
  Source = -> Face062
  Symmetric = false
FEATURE [Part::MultiFuse] Fusion047  label="makeHoles"
  Shapes = -> [Revolve066,Revolve065,Revolve064,Revolve063,Revolve062,Revolve061]
FEATURE [Part::Feature] Face063
  shape: bbox 3.6 x 3.2 x 2e-07 mm, 1 faces, 0 solids (baked)
FEATURE [Part::Revolution] Revolve067  label="moreFrontCaseScrewRetainer002"
  Angle = 360
  Axis = (0,1,0)
  Base = (0,0,0)
  FaceMakerClass = Part::FaceMakerBullseye
  Placement = pos=(102.5,4.5,68.5) rot=(0,0,1;0rad)
  Solid = false
  Source = -> Face063
  Symmetric = false
FEATURE [Part::Feature] Face064
  shape: bbox 3.6 x 3.2 x 2e-07 mm, 1 faces, 0 solids (baked)
FEATURE [Part::Revolution] Revolve068  label="moreFrontCaseScrewRetainer003"
  Angle = 360
  Axis = (0,1,0)
  Base = (0,0,0)
  FaceMakerClass = Part::FaceMakerBullseye
  Placement = pos=(102.5,4.5,3.5) rot=(0,0,1;0rad)
  Solid = false
  Source = -> Face064
  Symmetric = false
FEATURE [Part::Feature] Face065
  shape: bbox 3.5 x 17.8 x 2e-07 mm, 1 faces, 0 solids (baked)
FEATURE [Part::Revolution] Revolve069  label="removeToCreateScrewAndThreadedInsertHole006"
  Angle = 360
  Axis = (0,1,0)
  Base = (0,0,0)
  FaceMakerClass = Part::FaceMakerBullseye
  Placement = pos=(12.5,0,10) rot=(0,0,1;0rad)
  Solid = false
  Source = -> Face065
  Symmetric = false
FEATURE [Part::Feature] Face066
  shape: bbox 3.5 x 17.8 x 2e-07 mm, 1 faces, 0 solids (baked)
FEATURE [Part::Revolution] Revolve070  label="removeToCreateScrewAndThreadedInsertHole007"
  Angle = 360
  Axis = (0,1,0)
  Base = (0,0,0)
  FaceMakerClass = Part::FaceMakerBullseye
  Placement = pos=(12.5,0,62) rot=(0,0,1;0rad)
  Solid = false
  Source = -> Face066
  Symmetric = false
FEATURE [Part::Feature] Face067
  shape: bbox 3.5 x 17.8 x 2e-07 mm, 1 faces, 0 solids (baked)
FEATURE [Part::Revolution] Revolve071  label="removeToCreateScrewAndThreadedInsertHole008"
  Angle = 360
  Axis = (0,1,0)
  Base = (0,0,0)
  FaceMakerClass = Part::FaceMakerBullseye
  Placement = pos=(89.5,0,68.5) rot=(0,0,1;0rad)
  Solid = false
  Source = -> Face067
  Symmetric = false
FEATURE [Part::Feature] Face068
  shape: bbox 3.5 x 17.8 x 2e-07 mm, 1 faces, 0 solids (baked)
FEATURE [Part::Revolution] Revolve072  label="removeToCreateScrewAndThreadedInsertHole009"
  Angle = 360
  Axis = (0,1,0)
  Base = (0,0,0)
  FaceMakerClass = Part::FaceMakerBullseye
  Placement = pos=(89.5,0,3.5) rot=(0,0,1;0rad)
  Solid = false
  Source = -> Face068
  Symmetric = false
FEATURE [Part::Feature] Face069
  shape: bbox 3.5 x 17.8 x 2e-07 mm, 1 faces, 0 solids (baked)
FEATURE [Part::Feature] Face070
  shape: bbox 3.5 x 17.8 x 2e-07 mm, 1 faces, 0 solids (baked)
FEATURE [Part::Revolution] Revolve073  label="removeToCreateScrewAndThreadedInsertHole010"
  Angle = 360
  Axis = (0,1,0)
  Base = (0,0,0)
  FaceMakerClass = Part::FaceMakerBullseye
  Placement = pos=(102.5,4.7,3.5) rot=(0,0,1;0rad)
  Solid = false
  Source = -> Face069
  Symmetric = false
FEATURE [Part::Revolution] Revolve074  label="removeToCreateScrewAndThreadedInsertHole011"
  Angle = 360
  Axis = (0,1,0)
  Base = (0,0,0)
  FaceMakerClass = Part::FaceMakerBullseye
  Placement = pos=(102.5,4.7,68.5) rot=(0,0,1;0rad)
  Solid = false
  Source = -> Face070
  Symmetric = false
FEATURE [Part::MultiFuse] Fusion048  label="makeHoles001"
  Shapes = -> [Revolve074,Revolve073,Revolve072,Revolve071,Revolve070,Revolve069]
FEATURE [Part::MultiFuse] Fusion049  label="caseScrewRetainers"
  Shapes = -> [Revolve067,Revolve068,Revolve048,Revolve047,Revolve039,Revolve040]
FEATURE [Part::Cut] Cut015  label="caseScrewRetainers001"
  Base = -> Fusion049
  Tool = -> Fusion048
FEATURE [Part::MultiFuse] Fusion050  label="casePillars"
  Shapes = -> [Revolve055,Revolve054,Revolve043,Revolve046,Revolve059,Revolve060]
FEATURE [Part::Feature] Face071 .. Face076  x6 (patterned run collapsed; names and placements below)
  shape: bbox 3.5 x 17.8 x 2e-07 mm, 1 faces, 0 solids (baked)
FEATURE [Part::Revolution] Revolve075  label="removeToCreateScrewAndThreadedInsertHole012"
  Angle = 360
  Axis = (0,1,0)
  Base = (0,0,0)
  FaceMakerClass = Part::FaceMakerBullseye
  Placement = pos=(12.5,0,10) rot=(0,0,1;0rad)
  Solid = false
  Source = -> Face071
  Symmetric = false
FEATURE [Part::Revolution] Revolve076  label="removeToCreateScrewAndThreadedInsertHole013"
  Angle = 360
  Axis = (0,1,0)
  Base = (0,0,0)
  FaceMakerClass = Part::FaceMakerBullseye
  Placement = pos=(12.5,0,62) rot=(0,0,1;0rad)
  Solid = false
  Source = -> Face072
  Symmetric = false
FEATURE [Part::Revolution] Revolve077  label="removeToCreateScrewAndThreadedInsertHole014"
  Angle = 360
  Axis = (0,1,0)
  Base = (0,0,0)
  FaceMakerClass = Part::FaceMakerBullseye
  Placement = pos=(89.5,0,68.5) rot=(0,0,1;0rad)
  Solid = false
  Source = -> Face073
  Symmetric = false
FEATURE [Part::Revolution] Revolve078  label="removeToCreateScrewAndThreadedInsertHole015"
  Angle = 360
  Axis = (0,1,0)
  Base = (0,0,0)
  FaceMakerClass = Part::FaceMakerBullseye
  Placement = pos=(89.5,0,3.5) rot=(0,0,1;0rad)
  Solid = false
  Source = -> Face074
  Symmetric = false
FEATURE [Part::Revolution] Revolve079  label="removeToCreateScrewAndThreadedInsertHole016"
  Angle = 360
  Axis = (0,1,0)
  Base = (0,0,0)
  FaceMakerClass = Part::FaceMakerBullseye
  Placement = pos=(102.5,4.7,3.5) rot=(0,0,1;0rad)
  Solid = false
  Source = -> Face075
  Symmetric = false
FEATURE [Part::Revolution] Revolve080  label="removeToCreateScrewAndThreadedInsertHole017"
  Angle = 360
  Axis = (0,1,0)
  Base = (0,0,0)
  FaceMakerClass = Part::FaceMakerBullseye
  Placement = pos=(102.5,4.7,68.5) rot=(0,0,1;0rad)
  Solid = false
  Source = -> Face076
  Symmetric = false
FEATURE [Part::MultiFuse] Fusion051  label="makeHoles002"
  Shapes = -> [Revolve080,Revolve079,Revolve078,Revolve077,Revolve076,Revolve075]
FEATURE [Part::Cut] Cut016  label="caesPillars"
  Base = -> Fusion050
  Tool = -> Fusion051
FEATURE [Part::Revolution] Revolve009  label="plugHousing016"
  Angle = 360
  Axis = (0,1,0)
  Base = (0,0,0)
  FaceMakerClass = Part::FaceMakerBullseye
  Placement = pos=(0,0,36.15) rot=(0,0,1;0rad)
  Solid = false
  Source = -> Face012
  Symmetric = false
FEATURE [Part::MultiFuse] Fusion014  label="plugHousing023"
  Placement = pos=(0,0,0) rot=(0,0,1;1.5708rad)
  Shapes = -> [Revolve011,Revolve009]
FEATURE [Part::Revolution] Revolve010  label="plugHousing017"
  Angle = 360
  Axis = (0,1,0)
  Base = (0,0,0)
  FaceMakerClass = Part::FaceMakerBullseye
  Placement = pos=(0,0,36.15) rot=(0,0,1;0rad)
  Solid = false
  Source = -> Face014
  Symmetric = false
FEATURE [Part::MultiFuse] Fusion015  label="plugHousing024"
  Placement = pos=(0,0,0) rot=(0,0,1;1.5708rad)
  Shapes = -> [Revolve010,Revolve015]
FEATURE [Part::Revolution] Revolve014  label="plugHousing026"
  Angle = 360
  Axis = (0,1,0)
  Base = (0,0,0)
  FaceMakerClass = Part::FaceMakerBullseye
  Placement = pos=(0,0,36.15) rot=(0,0,1;0rad)
  Solid = false
  Source = -> Face011
  Symmetric = false
FEATURE [Part::Revolution] Revolve013  label="plugHousing025"
  Angle = 360
  Axis = (0,1,0)
  Base = (0,0,0)
  FaceMakerClass = Part::FaceMakerBullseye
  Placement = pos=(0,0,36.15) rot=(0,0,1;0rad)
  Solid = false
  Source = -> Face015
  Symmetric = false
FEATURE [Part::MultiFuse] Fusion016  label="plugHousing028"
  Placement = pos=(0,19,0) rot=(0,0,1;3.14159rad)
  Shapes = -> [Fusion014,Fusion013]
FEATURE [Part::MultiFuse] Fusion011  label="plugHousing018"
  Placement = pos=(0,0,0) rot=(0,0,1;1.5708rad)
  Shapes = -> [Revolve014,Revolve013]
FEATURE [Part::MultiFuse] Fusion012  label="plugHousing019"
  Placement = pos=(0,19,0) rot=(0,0,1;3.14159rad)
  Shapes = -> [Fusion011,Fusion015]
FEATURE [Part::MultiFuse] Fusion017  label="plugHousing029"
  Placement = pos=(122.621,0,-0.15) rot=(0,0,1;0rad)
  Shapes = -> [Fusion016,Fusion012]
FEATURE [Part::MultiFuse] Fusion052  label="casePillarRetainers"
  Shapes = -> [Extrude012,Extrude013,Extrude014,Extrude015,Extrude016,Extrude017,Extrude018,Extrude019,Box011,Box012]
FEATURE [Part::Feature] Face077
  shape: bbox 3.5 x 17.8 x 2e-07 mm, 1 faces, 0 solids (baked)
FEATURE [Part::Revolution] Revolve081  label="removeToCreateScrewAndThreadedInsertHole018"
  Angle = 360
  Axis = (0,1,0)
  Base = (0,0,0)
  FaceMakerClass = Part::FaceMakerBullseye
  Placement = pos=(62.3,30.3,19.7) rot=(0,0,1;0rad)
  Solid = false
  Source = -> Face077
  Symmetric = false
FEATURE [Part::Feature] Face078
  shape: bbox 3.5 x 17.8 x 2e-07 mm, 1 faces, 0 solids (baked)
FEATURE [Part::Revolution] Revolve082  label="removeToCreateScrewAndThreadedInsertHole019"
  Angle = 360
  Axis = (0,1,0)
  Base = (0,0,0)
  FaceMakerClass = Part::FaceMakerBullseye
  Placement = pos=(62.3,30.3,51.7) rot=(0,0,1;0rad)
  Solid = false
  Source = -> Face078
  Symmetric = false
FEATURE [Part::Feature] Face079
  shape: bbox 3.5 x 17.8 x 2e-07 mm, 1 faces, 0 solids (baked)
FEATURE [Part::Revolution] Revolve083  label="removeToCreateScrewAndThreadedInsertHole020"
  Angle = 360
  Axis = (0,1,0)
  Base = (0,0,0)
  FaceMakerClass = Part::FaceMakerBullseye
  Placement = pos=(30.3,30.3,19.7) rot=(0,0,1;0rad)
  Solid = false
  Source = -> Face079
  Symmetric = false
FEATURE [Part::Feature] Face080
  shape: bbox 3.5 x 17.8 x 2e-07 mm, 1 faces, 0 solids (baked)
FEATURE [Part::Revolution] Revolve084  label="removeToCreateScrewAndThreadedInsertHole021"
  Angle = 360
  Axis = (0,1,0)
  Base = (0,0,0)
  FaceMakerClass = Part::FaceMakerBullseye
  Placement = pos=(30.3,30.3,51.7) rot=(0,0,1;0rad)
  Solid = false
  Source = -> Face080
  Symmetric = false
FEATURE [Part::MultiFuse] Fusion053  label="createThreadedInsertHolesForFan"
  Shapes = -> [Revolve081,Revolve082,Revolve083,Revolve084]
FEATURE [Part::Cut] Cut017  label="fanScrewHousing001"
  Base = -> Fusion046
  Tool = -> Fusion053
FEATURE [Part::Feature] Face081
  shape: bbox 3.5 x 17.8 x 2e-07 mm, 1 faces, 0 solids (baked)
FEATURE [Part::Revolution] Revolve085  label="removeToCreateScrewAndThreadedInsertHole022"
  Angle = 360
  Axis = (0,1,0)
  Base = (0,0,0)
  FaceMakerClass = Part::FaceMakerBullseye
  Placement = pos=(62.3,30.3,19.7) rot=(0,0,1;0rad)
  Solid = false
  Source = -> Face081
  Symmetric = false
FEATURE [Part::Feature] Face082
  shape: bbox 3.5 x 17.8 x 2e-07 mm, 1 faces, 0 solids (baked)
FEATURE [Part::Revolution] Revolve086  label="removeToCreateScrewAndThreadedInsertHole023"
  Angle = 360
  Axis = (0,1,0)
  Base = (0,0,0)
  FaceMakerClass = Part::FaceMakerBullseye
  Placement = pos=(62.3,30.3,51.7) rot=(0,0,1;0rad)
  Solid = false
  Source = -> Face082
  Symmetric = false
FEATURE [Part::Feature] Face083
  shape: bbox 3.5 x 17.8 x 2e-07 mm, 1 faces, 0 solids (baked)
FEATURE [Part::Revolution] Revolve087  label="removeToCreateScrewAndThreadedInsertHole024"
  Angle = 360
  Axis = (0,1,0)
  Base = (0,0,0)
  FaceMakerClass = Part::FaceMakerBullseye
  Placement = pos=(30.3,30.3,19.7) rot=(0,0,1;0rad)
  Solid = false
  Source = -> Face083
  Symmetric = false
FEATURE [Part::Feature] Face084
  shape: bbox 3.5 x 17.8 x 2e-07 mm, 1 faces, 0 solids (baked)
FEATURE [Part::Revolution] Revolve088  label="removeToCreateScrewAndThreadedInsertHole025"
  Angle = 360
  Axis = (0,1,0)
  Base = (0,0,0)
  FaceMakerClass = Part::FaceMakerBullseye
  Placement = pos=(30.3,30.3,51.7) rot=(0,0,1;0rad)
  Solid = false
  Source = -> Face084
  Symmetric = false
FEATURE [Part::MultiFuse] Fusion054  label="createThreadedInsertHolesForFan001"
  Shapes = -> [Revolve085,Revolve086,Revolve087,Revolve088]
FEATURE [Part::Cut] Cut018  label="top007"
  Base = -> Fusion040
  Tool = -> Fusion054
FEATURE [Sketcher::SketchObject] Sketch029
  FullyConstrained = false
  Placement = pos=(0,0,0) rot=(1,0,0;1.5708rad)
  sketch-geometry (24):
    g0: ArcOfCircle CenterX=-4 CenterY=-10.5 CenterZ=0 NormalX=0 NormalY=0 NormalZ=1 AngleXU=0 Radius=1.5 StartAngle=6e-16 EndAngle=3.14159
    g1: ArcOfCircle CenterX=-34.2 CenterY=-10.5 CenterZ=0 NormalX=0 NormalY=0 NormalZ=1 AngleXU=0 Radius=1.5 StartAngle=0 EndAngle=3.14159
    g2: ArcOfCircle CenterX=-34.2 CenterY=-27.7 CenterZ=0 NormalX=0 NormalY=0 NormalZ=1 AngleXU=0 Radius=1.5 StartAngle=3.14159 EndAngle=6.28319
    g3: ArcOfCircle CenterX=-4 CenterY=-27.7 CenterZ=0 NormalX=0 NormalY=0 NormalZ=1 AngleXU=0 Radius=1.5 StartAngle=3.1416 EndAngle=6.28319
    g4: ArcOfCircle CenterX=-10 CenterY=-4.3 CenterZ=0 NormalX=0 NormalY=0 NormalZ=1 AngleXU=0 Radius=1.5 StartAngle=2e-16 EndAngle=3.14159
    g5: ArcOfCircle CenterX=-16.1 CenterY=-1.8 CenterZ=0 NormalX=0 NormalY=0 NormalZ=1 AngleXU=0 Radius=1.5 StartAngle=5e-16 EndAngle=3.14159
    g6: ArcOfCircle CenterX=-22.1 CenterY=-1.8 CenterZ=0 NormalX=0 NormalY=0 NormalZ=1 AngleXU=0 Radius=1.5 StartAngle=5e-16 EndAngle=3.14159
    g7: ArcOfCircle CenterX=-28.2 CenterY=-4.3 CenterZ=0 NormalX=0 NormalY=0 NormalZ=1 AngleXU=0 Radius=1.5 StartAngle=2e-16 EndAngle=3.14159
    g8: ArcOfCircle CenterX=-10 CenterY=-33.9 CenterZ=0 NormalX=0 NormalY=0 NormalZ=1 AngleXU=0 Radius=1.5 StartAngle=3.14159 EndAngle=6.28319
    g9: ArcOfCircle CenterX=-16.1 CenterY=-36.4 CenterZ=0 NormalX=0 NormalY=0 NormalZ=1 AngleXU=0 Radius=1.5 StartAngle=3.14159 EndAngle=6.28319
    g10: ArcOfCircle CenterX=-22.1 CenterY=-36.4 CenterZ=0 NormalX=0 NormalY=0 NormalZ=1 AngleXU=0 Radius=1.5 StartAngle=3.14159 EndAngle=6.28319
    g11: ArcOfCircle CenterX=-28.2 CenterY=-33.9 CenterZ=0 NormalX=0 NormalY=0 NormalZ=1 AngleXU=0 Radius=1.5 StartAngle=3.14159 EndAngle=6.28319
    g12: LineSegment StartX=-35.7 StartY=-10.5 StartZ=0 EndX=-35.7 EndY=-27.7 EndZ=0
    g13: LineSegment StartX=-32.7 StartY=-10.5 StartZ=0 EndX=-32.7 EndY=-27.7 EndZ=0
    g14: LineSegment StartX=-29.7 StartY=-33.9 StartZ=0 EndX=-29.7 EndY=-4.3 EndZ=0
    g15: LineSegment StartX=-26.7 StartY=-33.9 StartZ=0 EndX=-26.7 EndY=-4.3 EndZ=0
    g16: LineSegment StartX=-2.5 StartY=-10.5 StartZ=0 EndX=-2.5 EndY=-27.7 EndZ=0
    g17: LineSegment StartX=-8.5 StartY=-4.3 StartZ=0 EndX=-8.5 EndY=-33.9 EndZ=0
    g18: LineSegment StartX=-5.5 StartY=-10.5 StartZ=0 EndX=-5.5 EndY=-27.7 EndZ=0
    g19: LineSegment StartX=-11.5 StartY=-4.3 StartZ=0 EndX=-11.5 EndY=-33.9 EndZ=0
    g20: LineSegment StartX=-14.6 StartY=-1.8 StartZ=0 EndX=-14.6 EndY=-36.4 EndZ=0
    g21: LineSegment StartX=-17.6 StartY=-1.8 StartZ=0 EndX=-17.6 EndY=-36.4 EndZ=0
    g22: LineSegment StartX=-20.6 StartY=-36.4 StartZ=0 EndX=-20.6 EndY=-1.8 EndZ=0
    g23: LineSegment StartX=-23.6 StartY=-1.8 StartZ=0 EndX=-23.6 EndY=-36.4 EndZ=0
  constraints (48):
    c: Block(g0)
    c: Block(g1)
    c: Block(g2)
    c: Block(g3)
    c: Block(g4)
    c: Block(g5)
    c: Block(g6)
    c: Block(g7)
    c: Block(g8)
    c: Block(g9)
    c: Block(g10)
    c: Block(g11)
    c: Coincident(g12,g1)
    c: Coincident(g12,g2)
    c: Vertical(g12)
    c: Coincident(g13,g1)
    c: Coincident(g13,g2)
    c: Vertical(g13)
    c: Coincident(g14,g11)
    c: Coincident(g14,g7)
    c: Vertical(g14)
    c: Coincident(g15,g11)
    c: Coincident(g15,g7)
    c: Vertical(g15)
    c: Coincident(g16,g0)
    c: Coincident(g16,g3)
    c: Vertical(g16)
    c: Coincident(g17,g4)
    c: Coincident(g17,g8)
    c: Vertical(g17)
    c: Coincident(g18,g0)
    c: Coincident(g18,g3)
    c: Vertical(g18)
    c: Coincident(g19,g4)
    c: Coincident(g19,g8)
    c: Vertical(g19)
    c: Coincident(g20,g5)
    c: Coincident(g20,g9)
    c: Vertical(g20)
    c: Coincident(g21,g5)
    c: Coincident(g21,g9)
    c: Vertical(g21)
    c: Coincident(g22,g10)
    c: Coincident(g22,g6)
    c: Vertical(g22)
    c: Coincident(g23,g6)
    c: Coincident(g23,g10)
    c: Vertical(g23)
FEATURE [Part::Extrusion] Extrude020  label="removeToCreateFanGrillHoles"
  Base = -> Sketch029
  Dir = (0,-1,6e-16)
  DirMode = 2
  FaceMakerClass = Part::FaceMakerBullseye
  LengthFwd = 10
  LengthRev = 0
  Placement = pos=(65.4,44,54.82) rot=(0,0,1;0rad)
  Solid = true
  Symmetric = false
FEATURE [Part::MultiFuse] Fusion055  label="top008"
  Shapes = -> [Cut017,Cut018]
FEATURE [Part::Cut] Cut019  label="top009"
  Base = -> Fusion055
  Tool = -> Extrude020
FEATURE [App::MeasureDistance] Distance003  label="Distance: 71.95 mm"
  Distance = 71.9513
  P1 = (117,38,72)
  P2 = (117,38,0.0487319)
FEATURE [Sketcher::SketchObject] Sketch030
  FullyConstrained = true
  Placement = pos=(117,19,0) rot=(0.57735,0.57735,0.57735;2.0944rad)
  sketch-geometry (48):
    g0: LineSegment StartX=-49.19 StartY=69.25 StartZ=0 EndX=-49.19 EndY=66.25 EndZ=0
    g1: LineSegment StartX=-49.19 StartY=63.5 StartZ=0 EndX=-49.19 EndY=60.5 EndZ=0
    g2: LineSegment StartX=-49.19 StartY=57.75 StartZ=0 EndX=-49.19 EndY=54.75 EndZ=0
    g3: LineSegment StartX=-49.19 StartY=52 StartZ=0 EndX=-49.19 EndY=49 EndZ=0
    g4: LineSegment StartX=-49.19 StartY=46.25 StartZ=0 EndX=-49.19 EndY=43.25 EndZ=0
    g5: LineSegment StartX=-49.19 StartY=40.5 StartZ=0 EndX=-49.19 EndY=37.5 EndZ=0
    g6: LineSegment StartX=-49.19 StartY=34.5 StartZ=0 EndX=-49.19 EndY=31.5 EndZ=0
    g7: LineSegment StartX=-49.19 StartY=28.75 StartZ=0 EndX=-49.19 EndY=25.75 EndZ=0
    g8: LineSegment StartX=-49.19 StartY=23 StartZ=0 EndX=-49.19 EndY=20 EndZ=0
    g9: LineSegment StartX=-49.19 StartY=17.25 StartZ=0 EndX=-49.19 EndY=14.25 EndZ=0
    g10: LineSegment StartX=-49.19 StartY=11.5 StartZ=0 EndX=-49.19 EndY=8.5 EndZ=0
    g11: LineSegment StartX=-49.19 StartY=5.75 StartZ=0 EndX=-49.19 EndY=2.75 EndZ=0
    g12: ArcOfCircle CenterX=-1.5 CenterY=67.75 CenterZ=0 NormalX=0 NormalY=0 NormalZ=1 AngleXU=0 Radius=1.5 StartAngle=4.71239 EndAngle=7.85398
    g13: ArcOfCircle CenterX=-1.5 CenterY=62 CenterZ=0 NormalX=0 NormalY=0 NormalZ=1 AngleXU=0 Radius=1.5 StartAngle=4.71239 EndAngle=7.85398
    g14: ArcOfCircle CenterX=-1.5 CenterY=56.25 CenterZ=0 NormalX=0 NormalY=0 NormalZ=1 AngleXU=0 Radius=1.5 StartAngle=4.71239 EndAngle=7.85398
    g15: ArcOfCircle CenterX=-11.49 CenterY=50.5 CenterZ=0 NormalX=0 NormalY=0 NormalZ=1 AngleXU=0 Radius=1.5 StartAngle=4.71239 EndAngle=7.85398
    g16: ArcOfCircle CenterX=-16.28 CenterY=44.75 CenterZ=0 NormalX=0 NormalY=0 NormalZ=1 AngleXU=0 Radius=1.5 StartAngle=4.71239 EndAngle=7.85398
    g17: ArcOfCircle CenterX=-18.2337 CenterY=39 CenterZ=0 NormalX=0 NormalY=0 NormalZ=1 AngleXU=0 Radius=1.5 StartAngle=4.71485 EndAngle=7.85398
    g18: ArcOfCircle CenterX=-16.2837 CenterY=27.25 CenterZ=0 NormalX=0 NormalY=0 NormalZ=1 AngleXU=0 Radius=1.5 StartAngle=4.71485 EndAngle=7.85398
    g19: ArcOfCircle CenterX=-18.2337 CenterY=33 CenterZ=0 NormalX=0 NormalY=0 NormalZ=1 AngleXU=0 Radius=1.5 StartAngle=4.71485 EndAngle=7.85398
    g20: ArcOfCircle CenterX=-11.49 CenterY=21.5 CenterZ=0 NormalX=0 NormalY=0 NormalZ=1 AngleXU=0 Radius=1.5 StartAngle=4.71239 EndAngle=7.85398
    g21: ArcOfCircle CenterX=-1.5 CenterY=4.25 CenterZ=0 NormalX=0 NormalY=0 NormalZ=1 AngleXU=0 Radius=1.5 StartAngle=4.71239 EndAngle=7.85398
    g22: ArcOfCircle CenterX=-1.5 CenterY=10 CenterZ=0 NormalX=0 NormalY=0 NormalZ=1 AngleXU=0 Radius=1.5 StartAngle=4.71239 EndAngle=7.85398
    g23: ArcOfCircle CenterX=-1.5 CenterY=15.75 CenterZ=0 NormalX=0 NormalY=0 NormalZ=1 AngleXU=0 Radius=1.5 StartAngle=4.71239 EndAngle=7.85398
    g24: LineSegment StartX=-49.19 StartY=69.25 StartZ=0 EndX=-1.5 EndY=69.25 EndZ=0
    g25: LineSegment StartX=-49.19 StartY=66.25 StartZ=0 EndX=-1.5 EndY=66.25 EndZ=0
    g26: LineSegment StartX=-49.19 StartY=63.5 StartZ=0 EndX=-1.5 EndY=63.5 EndZ=0
    g27: LineSegment StartX=-49.19 StartY=60.5 StartZ=0 EndX=-1.5 EndY=60.5 EndZ=0
    g28: LineSegment StartX=-49.19 StartY=57.75 StartZ=0 EndX=-1.5 EndY=57.75 EndZ=0
    g29: LineSegment StartX=-49.19 StartY=54.75 StartZ=0 EndX=-1.5 EndY=54.75 EndZ=0
    g30: LineSegment StartX=-49.19 StartY=52 StartZ=0 EndX=-11.49 EndY=52 EndZ=0
    g31: LineSegment StartX=-49.19 StartY=49 StartZ=0 EndX=-11.49 EndY=49 EndZ=0
    g32: LineSegment StartX=-49.19 StartY=46.25 StartZ=0 EndX=-16.28 EndY=46.25 EndZ=0
    g33: LineSegment StartX=-49.19 StartY=43.25 StartZ=0 EndX=-16.28 EndY=43.25 EndZ=0
    g34: LineSegment StartX=-49.19 StartY=40.5 StartZ=0 EndX=-18.2337 EndY=40.5 EndZ=0
    g35: LineSegment StartX=-49.19 StartY=37.5 StartZ=0 EndX=-18.23 EndY=37.5 EndZ=0
    g36: LineSegment StartX=-49.19 StartY=34.5 StartZ=0 EndX=-18.2337 EndY=34.5 EndZ=0
    g37: LineSegment StartX=-49.19 StartY=31.5 StartZ=0 EndX=-18.23 EndY=31.5 EndZ=0
    g38: LineSegment StartX=-49.19 StartY=28.75 StartZ=0 EndX=-16.2837 EndY=28.75 EndZ=0
    g39: LineSegment StartX=-49.19 StartY=25.75 StartZ=0 EndX=-16.28 EndY=25.75 EndZ=0
    g40: LineSegment StartX=-49.19 StartY=23 StartZ=0 EndX=-11.49 EndY=23 EndZ=0
    g41: LineSegment StartX=-49.19 StartY=20 StartZ=0 EndX=-11.49 EndY=20 EndZ=0
    g42: LineSegment StartX=-49.19 StartY=17.25 StartZ=0 EndX=-1.5 EndY=17.25 EndZ=0
    g43: LineSegment StartX=-49.19 StartY=14.25 StartZ=0 EndX=-1.5 EndY=14.25 EndZ=0
    g44: LineSegment StartX=-49.19 StartY=11.5 StartZ=0 EndX=-1.5 EndY=11.5 EndZ=0
    g45: LineSegment StartX=-49.19 StartY=8.5 StartZ=0 EndX=-1.5 EndY=8.5 EndZ=0
    g46: LineSegment StartX=-49.19 StartY=5.75 StartZ=0 EndX=-1.5 EndY=5.75 EndZ=0
    g47: LineSegment StartX=-49.19 StartY=2.75 StartZ=0 EndX=-1.5 EndY=2.75 EndZ=0
  constraints (120):
    c: Vertical(g0)
    c: Distance(g0) = 3
    c: Block(g0)
    c: Vertical(g1)
    c: Distance(g1) = 3
    c: Vertical(g2)
    c: Equal(g0,g2) = 3
    c: Block(g2)
    c: Vertical(g3)
    c: Equal(g1,g3) = 3
    c: Vertical(g4)
    c: Equal(g0,g4) = 3
    c: Block(g4)
    c: Vertical(g5)
    c: Equal(g1,g5) = 3
    c: Vertical(g6)
    c: Equal(g0,g6) = 3
    c: Block(g6)
    c: Vertical(g7)
    c: Equal(g1,g7) = 3
    c: Vertical(g8)
    c: Equal(g0,g8) = 3
    c: Block(g8)
    c: Vertical(g9)
    c: Equal(g1,g9) = 3
    c: Vertical(g10)
    c: Equal(g0,g10) = 3
    c: Block(g10)
    c: Vertical(g11)
    c: Equal(g1,g11) = 3
    c: Block(g12)
    c: Block(g13)
    c: Block(g14)
    c: Block(g15)
    c: Block(g16)
    c: Block(g17)
    c: Block(g18)
    c: Block(g19)
    c: Block(g20)
    c: Block(g21)
    c: Block(g22)
    c: Block(g23)
    c: Block(g11)
    c: Block(g9)
    c: Block(g7)
    c: Block(g5)
    c: Block(g3)
    c: Block(g1)
    c: Coincident(g24,g0)
    c: Coincident(g24,g12)
    c: Horizontal(g24)
    c: Coincident(g25,g0)
    c: Coincident(g25,g12)
    c: Horizontal(g25)
    c: Coincident(g26,g1)
    c: Coincident(g26,g13)
    c: Horizontal(g26)
    c: Coincident(g27,g1)
    c: Coincident(g27,g13)
    c: Horizontal(g27)
    c: Coincident(g28,g2)
    c: Coincident(g28,g14)
    c: Horizontal(g28)
    c: Coincident(g29,g2)
    c: Coincident(g29,g14)
    c: Horizontal(g29)
    c: Coincident(g30,g3)
    c: Coincident(g30,g15)
    c: Horizontal(g30)
    c: Coincident(g31,g3)
    c: Coincident(g31,g15)
    c: Horizontal(g31)
    c: Coincident(g32,g4)
    c: Coincident(g32,g16)
    c: Horizontal(g32)
    c: Coincident(g33,g4)
    c: Coincident(g33,g16)
    c: Horizontal(g33)
    c: Coincident(g34,g5)
    c: Coincident(g34,g17)
    c: Horizontal(g34)
    c: Coincident(g35,g5)
    c: Coincident(g35,g17)
    c: Horizontal(g35)
    c: Coincident(g36,g6)
    c: Coincident(g36,g19)
    c: Horizontal(g36)
    c: Coincident(g37,g6)
    c: Coincident(g37,g19)
    c: Horizontal(g37)
    c: Coincident(g38,g7)
    c: Coincident(g38,g18)
    c: Horizontal(g38)
    c: Coincident(g39,g7)
    c: Coincident(g39,g18)
    c: Horizontal(g39)
    c: Coincident(g40,g8)
    c: Coincident(g40,g20)
    c: Horizontal(g40)
    c: Coincident(g41,g8)
    c: Coincident(g41,g20)
    c: Horizontal(g41)
    c: Coincident(g42,g9)
    c: Coincident(g42,g23)
    c: Horizontal(g42)
    c: Coincident(g43,g9)
    c: Coincident(g43,g23)
    c: Horizontal(g43)
    c: Coincident(g44,g10)
    c: Coincident(g44,g22)
    c: Horizontal(g44)
    c: Coincident(g45,g10)
    c: Coincident(g45,g22)
    c: Horizontal(g45)
    c: Coincident(g46,g11)
    c: Coincident(g46,g21)
    c: Horizontal(g46)
    c: Coincident(g47,g11)
    c: Coincident(g47,g21)
    c: Horizontal(g47)
FEATURE [Sketcher::SketchObject] Sketch031
  FullyConstrained = true
  Placement = pos=(117,19,0) rot=(0.57735,0.57735,0.57735;2.0944rad)
  sketch-geometry (24):
    g0: ArcOfCircle CenterX=-49.19 CenterY=67.75 CenterZ=0 NormalX=0 NormalY=0 NormalZ=1 AngleXU=0 Radius=1.5 StartAngle=1.5708 EndAngle=4.71239
    g1: ArcOfCircle CenterX=-49.19 CenterY=62 CenterZ=0 NormalX=0 NormalY=0 NormalZ=1 AngleXU=0 Radius=1.5 StartAngle=1.5708 EndAngle=4.71239
    g2: ArcOfCircle CenterX=-49.19 CenterY=56.25 CenterZ=0 NormalX=0 NormalY=0 NormalZ=1 AngleXU=0 Radius=1.5 StartAngle=1.5708 EndAngle=4.71239
    g3: ArcOfCircle CenterX=-49.19 CenterY=50.5 CenterZ=0 NormalX=0 NormalY=0 NormalZ=1 AngleXU=0 Radius=1.5 StartAngle=1.5708 EndAngle=4.71239
    g4: ArcOfCircle CenterX=-49.19 CenterY=44.75 CenterZ=0 NormalX=0 NormalY=0 NormalZ=1 AngleXU=0 Radius=1.5 StartAngle=1.5708 EndAngle=4.71239
    g5: ArcOfCircle CenterX=-49.19 CenterY=39 CenterZ=0 NormalX=0 NormalY=0 NormalZ=1 AngleXU=0 Radius=1.5 StartAngle=1.5708 EndAngle=4.71239
    g6: ArcOfCircle CenterX=-49.19 CenterY=33 CenterZ=0 NormalX=0 NormalY=0 NormalZ=1 AngleXU=0 Radius=1.5 StartAngle=1.5708 EndAngle=4.71239
    g7: ArcOfCircle CenterX=-49.19 CenterY=27.25 CenterZ=0 NormalX=0 NormalY=0 NormalZ=1 AngleXU=0 Radius=1.5 StartAngle=1.5708 EndAngle=4.71239
    g8: ArcOfCircle CenterX=-49.19 CenterY=21.5 CenterZ=0 NormalX=0 NormalY=0 NormalZ=1 AngleXU=0 Radius=1.5 StartAngle=1.5708 EndAngle=4.71239
    g9: ArcOfCircle CenterX=-49.19 CenterY=15.75 CenterZ=0 NormalX=0 NormalY=0 NormalZ=1 AngleXU=0 Radius=1.5 StartAngle=1.5708 EndAngle=4.71239
    g10: ArcOfCircle CenterX=-49.19 CenterY=10 CenterZ=0 NormalX=0 NormalY=0 NormalZ=1 AngleXU=0 Radius=1.5 StartAngle=1.5708 EndAngle=4.71239
    g11: ArcOfCircle CenterX=-49.19 CenterY=4.25 CenterZ=0 NormalX=0 NormalY=0 NormalZ=1 AngleXU=0 Radius=1.5 StartAngle=1.5708 EndAngle=4.71239
    g12: LineSegment StartX=-49.19 StartY=69.25 StartZ=0 EndX=-49.19 EndY=66.25 EndZ=0
    g13: LineSegment StartX=-49.19 StartY=63.5 StartZ=0 EndX=-49.19 EndY=60.5 EndZ=0
    g14: LineSegment StartX=-49.19 StartY=57.75 StartZ=0 EndX=-49.19 EndY=54.75 EndZ=0
    g15: LineSegment StartX=-49.19 StartY=52 StartZ=0 EndX=-49.19 EndY=49 EndZ=0
    g16: LineSegment StartX=-49.19 StartY=46.25 StartZ=0 EndX=-49.19 EndY=43.25 EndZ=0
    g17: LineSegment StartX=-49.19 StartY=40.5 StartZ=0 EndX=-49.19 EndY=37.5 EndZ=0
    g18: LineSegment StartX=-49.19 StartY=34.5 StartZ=0 EndX=-49.19 EndY=31.5 EndZ=0
    g19: LineSegment StartX=-49.19 StartY=28.75 StartZ=0 EndX=-49.19 EndY=25.75 EndZ=0
    g20: LineSegment StartX=-49.19 StartY=23 StartZ=0 EndX=-49.19 EndY=20 EndZ=0
    g21: LineSegment StartX=-49.19 StartY=17.25 StartZ=0 EndX=-49.19 EndY=14.25 EndZ=0
    g22: LineSegment StartX=-49.19 StartY=11.5 StartZ=0 EndX=-49.19 EndY=8.5 EndZ=0
    g23: LineSegment StartX=-49.19 StartY=5.75 StartZ=0 EndX=-49.19 EndY=2.75 EndZ=0
  constraints (48):
    c: Block(g0)
    c: Block(g1)
    c: Block(g2)
    c: Block(g3)
    c: Block(g4)
    c: Block(g5)
    c: Block(g6)
    c: Block(g7)
    c: Block(g8)
    c: Block(g9)
    c: Block(g10)
    c: Block(g11)
    c: Coincident(g12,g0)
    c: Coincident(g12,g0)
    c: Vertical(g12)
    c: Vertical(g13)
    c: Coincident(g13,g1)
    c: Vertical(g14)
    c: Coincident(g14,g2)
    c: Vertical(g15)
    c: Coincident(g15,g3)
    c: Vertical(g16)
    c: Coincident(g16,g4)
    c: Vertical(g17)
    c: Coincident(g17,g5)
    c: Vertical(g18)
    c: Coincident(g18,g6)
    c: Vertical(g19)
    c: Coincident(g19,g7)
    c: Vertical(g20)
    c: Coincident(g20,g8)
    c: Vertical(g21)
    c: Coincident(g21,g9)
    c: Vertical(g22)
    c: Coincident(g22,g10)
    c: Vertical(g23)
    c: Coincident(g23,g11)
    c: Block(g23)
    c: Block(g22)
    c: Block(g21)
    c: Block(g20)
    c: Block(g13)
    c: Block(g14)
    c: Block(g15)
    c: Block(g16)
    c: Block(g17)
    c: Block(g18)
    c: Block(g19)
FEATURE [Part::Extrusion] Extrude022
  Base = -> Sketch030
  Dir = (1,-2e-16,2e-16)
  DirMode = 2
  FaceMakerClass = Part::FaceMakerBullseye
  LengthFwd = 19
  LengthRev = 0
  Placement = pos=(-19,0,0) rot=(0,0,1;0rad)
  Solid = true
  Symmetric = false
FEATURE [Part::Fillet] Fillet022
  Base = -> Extrude022
  Edges = 24 edges r=1.49: [Edge6,Edge11,Edge18,Edge23,Edge30,Edge35,Edge42,Edge47,Edge54,Edge59,Edge66,Edge71,Edge78,Edge83,Edge90,Edge95,Edge102,Edge107,Edge114,Edge119,Edge126,Edge131,Edge138,Edge143]
FEATURE [Part::Cut] Cut020  label="top010"
  Base = -> Cut019
  Tool = -> Fillet022
FEATURE [Sketcher::SketchObject] Sketch032
  FullyConstrained = true
  Placement = pos=(117,19,0) rot=(0.57735,0.57735,0.57735;2.0944rad)
  sketch-geometry (48):
    g0: LineSegment StartX=-49.19 StartY=69.25 StartZ=0 EndX=-49.19 EndY=66.25 EndZ=0
    g1: LineSegment StartX=-49.19 StartY=63.5 StartZ=0 EndX=-49.19 EndY=60.5 EndZ=0
    g2: LineSegment StartX=-49.19 StartY=57.75 StartZ=0 EndX=-49.19 EndY=54.75 EndZ=0
    g3: LineSegment StartX=-49.19 StartY=52 StartZ=0 EndX=-49.19 EndY=49 EndZ=0
    g4: LineSegment StartX=-49.19 StartY=46.25 StartZ=0 EndX=-49.19 EndY=43.25 EndZ=0
    g5: LineSegment StartX=-49.19 StartY=40.5 StartZ=0 EndX=-49.19 EndY=37.5 EndZ=0
    g6: LineSegment StartX=-49.19 StartY=34.5 StartZ=0 EndX=-49.19 EndY=31.5 EndZ=0
    g7: LineSegment StartX=-49.19 StartY=28.75 StartZ=0 EndX=-49.19 EndY=25.75 EndZ=0
    g8: LineSegment StartX=-49.19 StartY=23 StartZ=0 EndX=-49.19 EndY=20 EndZ=0
    g9: LineSegment StartX=-49.19 StartY=17.25 StartZ=0 EndX=-49.19 EndY=14.25 EndZ=0
    g10: LineSegment StartX=-49.19 StartY=11.5 StartZ=0 EndX=-49.19 EndY=8.5 EndZ=0
    g11: LineSegment StartX=-49.19 StartY=5.75 StartZ=0 EndX=-49.19 EndY=2.75 EndZ=0
    g12: ArcOfCircle CenterX=-1.5 CenterY=67.75 CenterZ=0 NormalX=0 NormalY=0 NormalZ=1 AngleXU=0 Radius=1.5 StartAngle=4.71239 EndAngle=7.85398
    g13: ArcOfCircle CenterX=-1.5 CenterY=62 CenterZ=0 NormalX=0 NormalY=0 NormalZ=1 AngleXU=0 Radius=1.5 StartAngle=4.71239 EndAngle=7.85398
    g14: ArcOfCircle CenterX=-1.5 CenterY=56.25 CenterZ=0 NormalX=0 NormalY=0 NormalZ=1 AngleXU=0 Radius=1.5 StartAngle=4.71239 EndAngle=7.85398
    g15: ArcOfCircle CenterX=-11.49 CenterY=50.5 CenterZ=0 NormalX=0 NormalY=0 NormalZ=1 AngleXU=0 Radius=1.5 StartAngle=4.71239 EndAngle=7.85398
    g16: ArcOfCircle CenterX=-16.28 CenterY=44.75 CenterZ=0 NormalX=0 NormalY=0 NormalZ=1 AngleXU=0 Radius=1.5 StartAngle=4.71239 EndAngle=7.85398
    g17: ArcOfCircle CenterX=-18.2337 CenterY=39 CenterZ=0 NormalX=0 NormalY=0 NormalZ=1 AngleXU=0 Radius=1.5 StartAngle=4.71485 EndAngle=7.85398
    g18: ArcOfCircle CenterX=-16.2837 CenterY=27.25 CenterZ=0 NormalX=0 NormalY=0 NormalZ=1 AngleXU=0 Radius=1.5 StartAngle=4.71485 EndAngle=7.85398
    g19: ArcOfCircle CenterX=-18.2337 CenterY=33 CenterZ=0 NormalX=0 NormalY=0 NormalZ=1 AngleXU=0 Radius=1.5 StartAngle=4.71485 EndAngle=7.85398
    g20: ArcOfCircle CenterX=-11.49 CenterY=21.5 CenterZ=0 NormalX=0 NormalY=0 NormalZ=1 AngleXU=0 Radius=1.5 StartAngle=4.71239 EndAngle=7.85398
    g21: ArcOfCircle CenterX=-1.5 CenterY=4.25 CenterZ=0 NormalX=0 NormalY=0 NormalZ=1 AngleXU=0 Radius=1.5 StartAngle=4.71239 EndAngle=7.85398
    g22: ArcOfCircle CenterX=-1.5 CenterY=10 CenterZ=0 NormalX=0 NormalY=0 NormalZ=1 AngleXU=0 Radius=1.5 StartAngle=4.71239 EndAngle=7.85398
    g23: ArcOfCircle CenterX=-1.5 CenterY=15.75 CenterZ=0 NormalX=0 NormalY=0 NormalZ=1 AngleXU=0 Radius=1.5 StartAngle=4.71239 EndAngle=7.85398
    g24: LineSegment StartX=-49.19 StartY=69.25 StartZ=0 EndX=-1.5 EndY=69.25 EndZ=0
    g25: LineSegment StartX=-49.19 StartY=66.25 StartZ=0 EndX=-1.5 EndY=66.25 EndZ=0
    g26: LineSegment StartX=-49.19 StartY=63.5 StartZ=0 EndX=-1.5 EndY=63.5 EndZ=0
    g27: LineSegment StartX=-49.19 StartY=60.5 StartZ=0 EndX=-1.5 EndY=60.5 EndZ=0
    g28: LineSegment StartX=-49.19 StartY=57.75 StartZ=0 EndX=-1.5 EndY=57.75 EndZ=0
    g29: LineSegment StartX=-49.19 StartY=54.75 StartZ=0 EndX=-1.5 EndY=54.75 EndZ=0
    g30: LineSegment StartX=-49.19 StartY=52 StartZ=0 EndX=-11.49 EndY=52 EndZ=0
    g31: LineSegment StartX=-49.19 StartY=49 StartZ=0 EndX=-11.49 EndY=49 EndZ=0
    g32: LineSegment StartX=-49.19 StartY=46.25 StartZ=0 EndX=-16.28 EndY=46.25 EndZ=0
    g33: LineSegment StartX=-49.19 StartY=43.25 StartZ=0 EndX=-16.28 EndY=43.25 EndZ=0
    g34: LineSegment StartX=-49.19 StartY=40.5 StartZ=0 EndX=-18.2337 EndY=40.5 EndZ=0
    g35: LineSegment StartX=-49.19 StartY=37.5 StartZ=0 EndX=-18.23 EndY=37.5 EndZ=0
    g36: LineSegment StartX=-49.19 StartY=34.5 StartZ=0 EndX=-18.2337 EndY=34.5 EndZ=0
    g37: LineSegment StartX=-49.19 StartY=31.5 StartZ=0 EndX=-18.23 EndY=31.5 EndZ=0
    g38: LineSegment StartX=-49.19 StartY=28.75 StartZ=0 EndX=-16.2837 EndY=28.75 EndZ=0
    g39: LineSegment StartX=-49.19 StartY=25.75 StartZ=0 EndX=-16.28 EndY=25.75 EndZ=0
    g40: LineSegment StartX=-49.19 StartY=23 StartZ=0 EndX=-11.49 EndY=23 EndZ=0
    g41: LineSegment StartX=-49.19 StartY=20 StartZ=0 EndX=-11.49 EndY=20 EndZ=0
    g42: LineSegment StartX=-49.19 StartY=17.25 StartZ=0 EndX=-1.5 EndY=17.25 EndZ=0
    g43: LineSegment StartX=-49.19 StartY=14.25 StartZ=0 EndX=-1.5 EndY=14.25 EndZ=0
    g44: LineSegment StartX=-49.19 StartY=11.5 StartZ=0 EndX=-1.5 EndY=11.5 EndZ=0
    g45: LineSegment StartX=-49.19 StartY=8.5 StartZ=0 EndX=-1.5 EndY=8.5 EndZ=0
    g46: LineSegment StartX=-49.19 StartY=5.75 StartZ=0 EndX=-1.5 EndY=5.75 EndZ=0
    g47: LineSegment StartX=-49.19 StartY=2.75 StartZ=0 EndX=-1.5 EndY=2.75 EndZ=0
  constraints (120):
    c: Vertical(g0)
    c: Distance(g0) = 3
    c: Block(g0)
    c: Vertical(g1)
    c: Distance(g1) = 3
    c: Vertical(g2)
    c: Equal(g0,g2) = 3
    c: Block(g2)
    c: Vertical(g3)
    c: Equal(g1,g3) = 3
    c: Vertical(g4)
    c: Equal(g0,g4) = 3
    c: Block(g4)
    c: Vertical(g5)
    c: Equal(g1,g5) = 3
    c: Vertical(g6)
    c: Equal(g0,g6) = 3
    c: Block(g6)
    c: Vertical(g7)
    c: Equal(g1,g7) = 3
    c: Vertical(g8)
    c: Equal(g0,g8) = 3
    c: Block(g8)
    c: Vertical(g9)
    c: Equal(g1,g9) = 3
    c: Vertical(g10)
    c: Equal(g0,g10) = 3
    c: Block(g10)
    c: Vertical(g11)
    c: Equal(g1,g11) = 3
    c: Block(g12)
    c: Block(g13)
    c: Block(g14)
    c: Block(g15)
    c: Block(g16)
    c: Block(g17)
    c: Block(g18)
    c: Block(g19)
    c: Block(g20)
    c: Block(g21)
    c: Block(g22)
    c: Block(g23)
    c: Block(g11)
    c: Block(g9)
    c: Block(g7)
    c: Block(g5)
    c: Block(g3)
    c: Block(g1)
    c: Coincident(g24,g0)
    c: Coincident(g24,g12)
    c: Horizontal(g24)
    c: Coincident(g25,g0)
    c: Coincident(g25,g12)
    c: Horizontal(g25)
    c: Coincident(g26,g1)
    c: Coincident(g26,g13)
    c: Horizontal(g26)
    c: Coincident(g27,g1)
    c: Coincident(g27,g13)
    c: Horizontal(g27)
    c: Coincident(g28,g2)
    c: Coincident(g28,g14)
    c: Horizontal(g28)
    c: Coincident(g29,g2)
    c: Coincident(g29,g14)
    c: Horizontal(g29)
    c: Coincident(g30,g3)
    c: Coincident(g30,g15)
    c: Horizontal(g30)
    c: Coincident(g31,g3)
    c: Coincident(g31,g15)
    c: Horizontal(g31)
    c: Coincident(g32,g4)
    c: Coincident(g32,g16)
    c: Horizontal(g32)
    c: Coincident(g33,g4)
    c: Coincident(g33,g16)
    c: Horizontal(g33)
    c: Coincident(g34,g5)
    c: Coincident(g34,g17)
    c: Horizontal(g34)
    c: Coincident(g35,g5)
    c: Coincident(g35,g17)
    c: Horizontal(g35)
    c: Coincident(g36,g6)
    c: Coincident(g36,g19)
    c: Horizontal(g36)
    c: Coincident(g37,g6)
    c: Coincident(g37,g19)
    c: Horizontal(g37)
    c: Coincident(g38,g7)
    c: Coincident(g38,g18)
    c: Horizontal(g38)
    c: Coincident(g39,g7)
    c: Coincident(g39,g18)
    c: Horizontal(g39)
    c: Coincident(g40,g8)
    c: Coincident(g40,g20)
    c: Horizontal(g40)
    c: Coincident(g41,g8)
    c: Coincident(g41,g20)
    c: Horizontal(g41)
    c: Coincident(g42,g9)
    c: Coincident(g42,g23)
    c: Horizontal(g42)
    c: Coincident(g43,g9)
    c: Coincident(g43,g23)
    c: Horizontal(g43)
    c: Coincident(g44,g10)
    c: Coincident(g44,g22)
    c: Horizontal(g44)
    c: Coincident(g45,g10)
    c: Coincident(g45,g22)
    c: Horizontal(g45)
    c: Coincident(g46,g11)
    c: Coincident(g46,g21)
    c: Horizontal(g46)
    c: Coincident(g47,g11)
    c: Coincident(g47,g21)
    c: Horizontal(g47)
FEATURE [Part::Extrusion] Extrude023
  Base = -> Sketch032
  Dir = (1,-2e-16,2e-16)
  DirMode = 2
  FaceMakerClass = Part::FaceMakerBullseye
  LengthFwd = 19
  LengthRev = 0
  Placement = pos=(-19,0,0) rot=(0,0,1;0rad)
  Solid = true
  Symmetric = false
FEATURE [Part::Fillet] Fillet023
  Base = -> Extrude023
  Edges = <same value as first occurrence — deduplicated (x6 in doc)>
  Placement = pos=(0,0.05,0) rot=(0,0,1;0rad)
FEATURE [Part::Cut] Cut014  label="bottom003"
  Base = -> Cut007
  Tool = -> Fusion047
FEATURE [Part::Cut] Cut021  label="bottom004"
  Base = -> Cut014
  Tool = -> Fillet023
FEATURE [Sketcher::SketchObject] Sketch033
  FullyConstrained = true
  Placement = pos=(117,19,0) rot=(0.57735,0.57735,0.57735;2.0944rad)
  sketch-geometry (8):
    g0: LineSegment StartX=-49.19 StartY=69.25 StartZ=0 EndX=-49.19 EndY=66.25 EndZ=0
    g1: LineSegment StartX=-49.19 StartY=5.75 StartZ=0 EndX=-49.19 EndY=2.75 EndZ=0
    g2: ArcOfCircle CenterX=-1.5 CenterY=67.75 CenterZ=0 NormalX=0 NormalY=0 NormalZ=1 AngleXU=0 Radius=1.5 StartAngle=4.71239 EndAngle=7.85398
    g3: ArcOfCircle CenterX=-1.5 CenterY=4.25 CenterZ=0 NormalX=0 NormalY=0 NormalZ=1 AngleXU=0 Radius=1.5 StartAngle=4.71239 EndAngle=7.85398
    g4: LineSegment StartX=-49.19 StartY=69.25 StartZ=0 EndX=-1.5 EndY=69.25 EndZ=0
    g5: LineSegment StartX=-49.19 StartY=66.25 StartZ=0 EndX=-1.5 EndY=66.25 EndZ=0
    g6: LineSegment StartX=-49.19 StartY=5.75 StartZ=0 EndX=-1.5 EndY=5.75 EndZ=0
    g7: LineSegment StartX=-49.19 StartY=2.75 StartZ=0 EndX=-1.5 EndY=2.75 EndZ=0
  constraints (19):
    c: Vertical(g0)
    c: Distance(g0) = 3
    c: Block(g0)
    c: Vertical(g1)
    c: Block(g2)
    c: Block(g3)
    c: Block(g1)
    c: Coincident(g4,g0)
    c: Coincident(g4,g2)
    c: Horizontal(g4)
    c: Coincident(g5,g0)
    c: Coincident(g5,g2)
    c: Horizontal(g5)
    c: Coincident(g6,g1)
    c: Coincident(g6,g3)
    c: Horizontal(g6)
    c: Coincident(g7,g1)
    c: Coincident(g7,g3)
    c: Horizontal(g7)
FEATURE [Sketcher::SketchObject] Sketch034
  FullyConstrained = true
  Placement = pos=(117,19,0) rot=(0.57735,0.57735,0.57735;2.0944rad)
  sketch-geometry (8):
    g0: LineSegment StartX=-49.19 StartY=63.5 StartZ=0 EndX=-49.19 EndY=60.5 EndZ=0
    g1: LineSegment StartX=-49.19 StartY=11.5 StartZ=0 EndX=-49.19 EndY=8.5 EndZ=0
    g2: ArcOfCircle CenterX=-1.5 CenterY=62 CenterZ=0 NormalX=0 NormalY=0 NormalZ=1 AngleXU=0 Radius=1.5 StartAngle=4.71239 EndAngle=7.85398
    g3: ArcOfCircle CenterX=-1.5 CenterY=10 CenterZ=0 NormalX=0 NormalY=0 NormalZ=1 AngleXU=0 Radius=1.5 StartAngle=4.71239 EndAngle=7.85398
    g4: LineSegment StartX=-49.19 StartY=63.5 StartZ=0 EndX=-1.5 EndY=63.5 EndZ=0
    g5: LineSegment StartX=-49.19 StartY=60.5 StartZ=0 EndX=-1.5 EndY=60.5 EndZ=0
    g6: LineSegment StartX=-49.19 StartY=11.5 StartZ=0 EndX=-1.5 EndY=11.5 EndZ=0
    g7: LineSegment StartX=-49.19 StartY=8.5 StartZ=0 EndX=-1.5 EndY=8.5 EndZ=0
  constraints (19):
    c: Vertical(g0)
    c: Distance(g0) = 3
    c: Vertical(g1)
    c: Block(g1)
    c: Block(g2)
    c: Block(g3)
    c: Block(g0)
    c: Coincident(g4,g0)
    c: Coincident(g4,g2)
    c: Horizontal(g4)
    c: Coincident(g5,g0)
    c: Coincident(g5,g2)
    c: Horizontal(g5)
    c: Coincident(g6,g1)
    c: Coincident(g6,g3)
    c: Horizontal(g6)
    c: Coincident(g7,g1)
    c: Coincident(g7,g3)
    c: Horizontal(g7)
FEATURE [Part::Extrusion] Extrude024
  Base = -> Sketch033
  Dir = (1,0,0)
  DirMode = 2
  FaceMakerClass = Part::FaceMakerBullseye
  LengthFwd = 10
  LengthRev = 0
  Solid = true
  Symmetric = false
FEATURE [Part::Extrusion] Extrude025
  Base = -> Sketch034
  Dir = (1,0,0)
  DirMode = 2
  FaceMakerClass = Part::FaceMakerBullseye
  LengthFwd = 10
  LengthRev = 0
  Solid = true
  Symmetric = false
FEATURE [Part::Fillet] Fillet024  label="removeFromtMoreFrontCaseScrewRetainers"
  Base = -> Extrude024
  Edges = 4 edges r=1.49: [Edge6,Edge11,Edge18,Edge23]
  Placement = pos=(-11,0,0) rot=(0,0,1;0rad)
FEATURE [Part::Fillet] Fillet025  label="removeFromtMoreFrontCaseScrewRetainers001"
  Base = -> Extrude025
  Edges = 4 edges r=1.49: [Edge6,Edge11,Edge18,Edge23]
  Placement = pos=(-19,0,0) rot=(0,0,1;0rad)
FEATURE [Part::Cut] Cut022
  Base = -> Cut015
  Tool = -> Fillet025
FEATURE [Part::Cut] Cut023  label="screwRetainers"
  Base = -> Cut022
  Tool = -> Fillet024
FEATURE [Part::MultiFuse] Fusion056  label="bottom005"
  Shapes = -> [Fusion044,Cut021]
FEATURE [Part::MultiFuse] Fusion057  label="casePillars001"
  Shapes = -> [Cut016,Fusion052]
FEATURE [Part::MultiFuse] Fusion058  label="bottom006"
  Shapes = -> [Fusion056,Cut023]
FEATURE [Part::MultiFuse] Fusion059  label="bottom007"
  Shapes = -> [Fusion058,Fillet005]
FEATURE [Part::MultiFuse] Fusion060  label="bottom008"
  Shapes = -> [Fusion059,Fusion]
FEATURE [Part::MultiFuse] Fusion061  label="top011"
  Shapes = -> [Cut006,Cut020]
FEATURE [Part::MultiFuse] Fusion062  label="top012"
  Shapes = -> [Fusion057,Fusion061]
FEATURE [Sketcher::SketchObject] Sketch035  label="topSketch007"
  FullyConstrained = true
  sketch-geometry (6):
    g0: LineSegment StartX=19 StartY=38 StartZ=0 EndX=117 EndY=38 EndZ=0
    g1: ArcOfCircle CenterX=19 CenterY=19 CenterZ=0 NormalX=0 NormalY=0 NormalZ=1 AngleXU=0 Radius=19 StartAngle=1.5708 EndAngle=3.14159
    g2: LineSegment StartX=117 StartY=38 StartZ=0 EndX=117 EndY=19 EndZ=0
    g3: LineSegment StartX=98 StartY=1.0161e-12 StartZ=0 EndX=5.22862e-06 EndY=1.0161e-12 EndZ=0
    g4: LineSegment StartX=5.22862e-06 StartY=19 StartZ=0 EndX=5.22862e-06 EndY=1.0161e-12 EndZ=0
    g5: ArcOfCircle CenterX=98 CenterY=19 CenterZ=0 NormalX=0 NormalY=0 NormalZ=1 AngleXU=0 Radius=19 StartAngle=4.71239 EndAngle=6.28319
  constraints (16):
    c: Horizontal(g0)
    c: Distance(g0) = 98
    c: Coincident(g1,g0)
    c: Block(g1)
    c: Coincident(g2,g0)
    c: Vertical(g2)
    c: Distance(g2) = 19
    c: Horizontal(g3)
    c: Coincident(g4,g1)
    c: Vertical(g4)
    c: Coincident(g3,g4)
    c: Block(g3)
    c: Coincident(g5,g2)
    c: Coincident(g5,g3)
    c: Block(g0)
    c: Block(g5)
FEATURE [Part::Extrusion] Extrude026  label="sideA001"
  Base = -> Sketch035
  Dir = (0,0,1)
  DirMode = 2
  FaceMakerClass = Part::FaceMakerBullseye
  LengthFwd = 3
  LengthRev = 0
  Placement = pos=(0,0,-2.7) rot=(0,0,1;0rad)
  Solid = true
  Symmetric = false
FEATURE [Sketcher::SketchObject] Sketch036  label="topSketch008"
  FullyConstrained = true
  sketch-geometry (6):
    g0: LineSegment StartX=19 StartY=38 StartZ=0 EndX=117 EndY=38 EndZ=0
    g1: ArcOfCircle CenterX=19 CenterY=19 CenterZ=0 NormalX=0 NormalY=0 NormalZ=1 AngleXU=0 Radius=19 StartAngle=1.5708 EndAngle=3.14159
    g2: LineSegment StartX=117 StartY=38 StartZ=0 EndX=117 EndY=19 EndZ=0
    g3: LineSegment StartX=98 StartY=1.0161e-12 StartZ=0 EndX=5.22862e-06 EndY=1.0161e-12 EndZ=0
    g4: LineSegment StartX=5.22862e-06 StartY=19 StartZ=0 EndX=5.22862e-06 EndY=1.0161e-12 EndZ=0
    g5: ArcOfCircle CenterX=98 CenterY=19 CenterZ=0 NormalX=0 NormalY=0 NormalZ=1 AngleXU=0 Radius=19 StartAngle=4.71239 EndAngle=6.28319
  constraints (16):
    c: Horizontal(g0)
    c: Distance(g0) = 98
    c: Coincident(g1,g0)
    c: Block(g1)
    c: Coincident(g2,g0)
    c: Vertical(g2)
    c: Distance(g2) = 19
    c: Horizontal(g3)
    c: Coincident(g4,g1)
    c: Vertical(g4)
    c: Coincident(g3,g4)
    c: Block(g3)
    c: Coincident(g5,g2)
    c: Coincident(g5,g3)
    c: Block(g0)
    c: Block(g5)
FEATURE [Part::Extrusion] Extrude027  label="sideB001"
  Base = -> Sketch036
  Dir = (0,0,1)
  DirMode = 2
  FaceMakerClass = Part::FaceMakerBullseye
  LengthFwd = 3
  LengthRev = 0
  Placement = pos=(0,0,71.7) rot=(0,0,1;0rad)
  Solid = true
  Symmetric = false
FEATURE [Part::MultiFuse] Fusion064  label="removeFromBottom"
  Shapes = -> [Extrude026,Extrude027]
FEATURE [Part::Cut] Cut024  label="bottom009"
  Base = -> Fusion060
  Tool = -> Fusion064
FEATURE [Sketcher::SketchObject] Sketch037  label="topSketch009"
  FullyConstrained = true
  sketch-geometry (8):
    g0: ArcOfCircle CenterX=19 CenterY=19.1201 CenterZ=0 NormalX=0 NormalY=0 NormalZ=1 AngleXU=0 Radius=18.8799 StartAngle=1.5708 EndAngle=3.14793
    g1: LineSegment StartX=0.120501 StartY=19.0004 StartZ=0 EndX=0.120501 EndY=0.000382114 EndZ=0
    g2: LineSegment StartX=19 StartY=38 StartZ=0 EndX=124 EndY=38 EndZ=0
    g3: LineSegment StartX=0.120501 StartY=0.000382114 StartZ=0 EndX=105.121 EndY=0.000382114 EndZ=0
    g4: LineSegment StartX=124 StartY=38 StartZ=0 EndX=125.616 EndY=38 EndZ=0
    g5: LineSegment StartX=105.121 StartY=0.000382114 StartZ=0 EndX=106.736 EndY=0.000382114 EndZ=0
    g6: ArcOfCircle CenterX=106.616 CenterY=19 CenterZ=0 NormalX=0 NormalY=0 NormalZ=1 AngleXU=0 Radius=19 StartAngle=4.71873 EndAngle=6.28319
    g7: LineSegment StartX=125.616 StartY=38 StartZ=0 EndX=125.616 EndY=19 EndZ=0
  constraints (21):
    c: Block(g0)
    c: Coincident(g1,g0)
    c: Vertical(g1)
    c: Horizontal(g2)
    c: Distance(g2) = 105
    c: Coincident(g2,g0)
    c: Distance(g1) = 19
    c: Coincident(g3,g1)
    c: Horizontal(g3)
    c: Distance(g3) = 105
    c: Coincident(g4,g2)
    c: Horizontal(g4)
    c: Distance(g4) = 1.61553
    c: Horizontal(g5)
    c: Equal(g4,g5) = 1.61553
    c: Coincident(g5,g3)
    c: Block(g6)
    c: Coincident(g6,g5)
    c: Coincident(g7,g4)
    c: Coincident(g7,g6)
    c: Vertical(g7)
FEATURE [Part::Extrusion] Extrude028  label="sideB"
  Base = -> Sketch037
  Dir = (0,0,1)
  DirMode = 2
  FaceMakerClass = Part::FaceMakerBullseye
  LengthFwd = 3
  LengthRev = 0
  Placement = pos=(0,0,72) rot=(0,0,1;0rad)
  Solid = true
  Symmetric = false
FEATURE [Sketcher::SketchObject] Sketch038  label="topSketch010"
  FullyConstrained = true
  sketch-geometry (22):
    g0: LineSegment StartX=5.21097e-06 StartY=3 StartZ=0 EndX=5.21097e-06 EndY=19 EndZ=0
    g1: ArcOfCircle CenterX=19 CenterY=19 CenterZ=0 NormalX=0 NormalY=0 NormalZ=1 AngleXU=0 Radius=19 StartAngle=1.5708 EndAngle=3.14159
    g2: ArcOfCircle CenterX=19 CenterY=19 CenterZ=0 NormalX=0 NormalY=0 NormalZ=1 AngleXU=0 Radius=16 StartAngle=1.5708 EndAngle=3.14159
    g3: LineSegment StartX=114 StartY=35 StartZ=0 EndX=19 EndY=35 EndZ=0
    g4: LineSegment StartX=5.21097e-06 StartY=3 StartZ=0 EndX=5.21097e-06 EndY=0 EndZ=0
    g5: LineSegment StartX=3 StartY=0 StartZ=0 EndX=5.21097e-06 EndY=0 EndZ=0
    g6: LineSegment StartX=3 StartY=19 StartZ=0 EndX=3 EndY=0 EndZ=0
    g7: LineSegment StartX=19 StartY=38 StartZ=0 EndX=124 EndY=38 EndZ=0
    g8: Circle CenterX=119 CenterY=35 CenterZ=0 NormalX=0 NormalY=0 NormalZ=1 AngleXU=0 Radius=1
    g9: Circle CenterX=121 CenterY=35 CenterZ=0 NormalX=0 NormalY=0 NormalZ=1 AngleXU=0 Radius=1
    g10: Circle CenterX=121 CenterY=33 CenterZ=0 NormalX=0 NormalY=0 NormalZ=1 AngleXU=0 Radius=1
    g11: BSplineCurve PolesCount=3 KnotsCount=2 Degree=2 IsPeriodic=0
    g12: GeomPoint X=119 Y=35 Z=0
    g13: GeomPoint X=121 Y=33 Z=0
    g14: LineSegment StartX=119 StartY=35 StartZ=0 EndX=114 EndY=35 EndZ=0
    g15: ArcOfCircle CenterX=105 CenterY=19 CenterZ=0 NormalX=0 NormalY=0 NormalZ=1 AngleXU=0 Radius=16 StartAngle=5.60905 EndAngle=6.28319
    g16: LineSegment StartX=121 StartY=33 StartZ=0 EndX=121 EndY=19 EndZ=0
    g17: LineSegment StartX=117.5 StartY=9.01251 StartZ=0 EndX=121.163 EndY=9.0125 EndZ=0
    g18: ArcOfCircle CenterX=105 CenterY=19 CenterZ=0 NormalX=0 NormalY=0 NormalZ=1 AngleXU=0 Radius=20.6155 StartAngle=5.7297 EndAngle=6.28319
    g19: LineSegment StartX=121.163 StartY=9.0125 StartZ=0 EndX=122.538 EndY=8.16329 EndZ=0
    g20: LineSegment StartX=124 StartY=38 StartZ=0 EndX=125.616 EndY=38 EndZ=0
    g21: LineSegment StartX=125.616 StartY=19 StartZ=0 EndX=125.616 EndY=38 EndZ=0
  constraints (49):
    c: Vertical(g0)
    c: Block(g0)
    c: Coincident(g1,g0)
    c: Block(g1)
    c: Coincident(g2,g1)
    c: Block(g2)
    c: Coincident(g3,g2)
    c: Horizontal(g3)
    c: Tangent(g3,g2)
    c: Coincident(g4,g0)
    c: Distance(g4) = 3
    c: Vertical(g4)
    c: Coincident(g5,g4)
    c: Horizontal(g5)
    c: Coincident(g6,g2)
    c: Coincident(g6,g5)
    c: Vertical(g6)
    c: Horizontal(g7)
    c: Distance(g7) = 105
    c: Coincident(g7,g1)
    c: Block(g3)
    c: Weight(g8) = 1
    c: Equal(g8,g9)
    c: Equal(g8,g10)
    c: InternalAlignment(g8,g11)
    c: InternalAlignment(g9,g11)
    c: InternalAlignment(g10,g11)
    c: InternalAlignment(g12,g11)
    c: InternalAlignment(g13,g11)
    c: Block(g11)
    c: Coincident(g14,g11)
    c: Coincident(g14,g3)
    c: Horizontal(g14)
    c: Block(g15)
    c: Coincident(g16,g11)
    c: Coincident(g16,g15)
    c: Vertical(g16)
    c: Distance(g16) = 14
    c: Coincident(g17,g15)
    c: Block(g18)
    c: Coincident(g19,g18)
    c: Coincident(g20,g7)
    c: Horizontal(g20)
    c: Vertical(g21)
    c: Coincident(g20,g21)
    c: Block(g20)
    c: Block(g21)
    c: Block(g19)
    c: Block(g17)
FEATURE [Part::Extrusion] Extrude029
  Base = -> Sketch038
  Dir = (0,0,1)
  DirMode = 2
  FaceMakerClass = Part::FaceMakerBullseye
  LengthFwd = 72
  LengthRev = 0
  Solid = true
  Symmetric = false
FEATURE [Part::Feature] Face085
  shape: bbox 4.8 x 25.5 x 2e-07 mm, 1 faces, 0 solids (baked)
FEATURE [Part::Revolution] Revolve089  label="moreFrontCaseScrewPost003"
  Angle = 360
  Axis = (0,1,0)
  Base = (0,0,0)
  FaceMakerClass = Part::FaceMakerBullseye
  Placement = pos=(109.5,4.5,3.5) rot=(0,0,1;0rad)
  Solid = false
  Source = -> Face085
  Symmetric = false
FEATURE [Part::Feature] Face086
  shape: bbox 4.8 x 25.5 x 2e-07 mm, 1 faces, 0 solids (baked)
FEATURE [Part::Revolution] Revolve090  label="moreFrontCaseScrewPost004"
  Angle = 360
  Axis = (0,1,0)
  Base = (0,0,0)
  FaceMakerClass = Part::FaceMakerBullseye
  Placement = pos=(109.5,4.5,68.5) rot=(0,0,1;0rad)
  Solid = false
  Source = -> Face086
  Symmetric = false
FEATURE [Part::Fillet] Fillet026  label="top013"
  Base = -> Extrude029
  Edges = 1 edges r=2: [Edge35]
FEATURE [Sketcher::SketchObject] Sketch039
  FullyConstrained = true
  sketch-geometry (7):
    g0: LineSegment StartX=0 StartY=0 StartZ=0 EndX=0 EndY=6 EndZ=0
    g1: Circle CenterX=0 CenterY=0 CenterZ=0 NormalX=0 NormalY=0 NormalZ=1 AngleXU=0 Radius=1
    g2: Circle CenterX=8 CenterY=6 CenterZ=0 NormalX=0 NormalY=0 NormalZ=1 AngleXU=0 Radius=1
    g3: BSplineCurve PolesCount=3 KnotsCount=2 Degree=2 IsPeriodic=0
    g4: GeomPoint X=0 Y=0 Z=0
    g5: GeomPoint X=8 Y=6 Z=0
    g6: LineSegment StartX=0 StartY=6 StartZ=0 EndX=8 EndY=6 EndZ=0
  constraints (14):
    c: Coincident(g0,g-1)
    c: Distance(g0) = 6
    c: Vertical(g0)
    c: Coincident(g3,g0)
    c: Weight(g1) = 1
    c: Equal(g1,g2)
    c: InternalAlignment(g1,g3)
    c: InternalAlignment(g2,g3)
    c: InternalAlignment(g4,g3)
    c: InternalAlignment(g5,g3)
    c: Block(g3)
    c: Coincident(g6,g0)
    c: Coincident(g6,g3)
    c: Horizontal(g6)
FEATURE [Sketcher::SketchObject] Sketch040
  FullyConstrained = true
  sketch-geometry (7):
    g0: LineSegment StartX=0 StartY=0 StartZ=0 EndX=0 EndY=6 EndZ=0
    g1: Circle CenterX=0 CenterY=0 CenterZ=0 NormalX=0 NormalY=0 NormalZ=1 AngleXU=0 Radius=1
    g2: Circle CenterX=8 CenterY=6 CenterZ=0 NormalX=0 NormalY=0 NormalZ=1 AngleXU=0 Radius=1
    g3: BSplineCurve PolesCount=3 KnotsCount=2 Degree=2 IsPeriodic=0
    g4: GeomPoint X=0 Y=0 Z=0
    g5: GeomPoint X=8 Y=6 Z=0
    g6: LineSegment StartX=0 StartY=6 StartZ=0 EndX=8 EndY=6 EndZ=0
  constraints (14):
    c: Coincident(g0,g-1)
    c: Distance(g0) = 6
    c: Vertical(g0)
    c: Coincident(g3,g0)
    c: Weight(g1) = 1
    c: Equal(g1,g2)
    c: InternalAlignment(g1,g3)
    c: InternalAlignment(g2,g3)
    c: InternalAlignment(g4,g3)
    c: InternalAlignment(g5,g3)
    c: Block(g3)
    c: Coincident(g6,g0)
    c: Coincident(g6,g3)
    c: Horizontal(g6)
FEATURE [Sketcher::SketchObject] Sketch041
  FullyConstrained = true
  sketch-geometry (7):
    g0: LineSegment StartX=0 StartY=0 StartZ=0 EndX=0 EndY=6 EndZ=0
    g1: Circle CenterX=0 CenterY=0 CenterZ=0 NormalX=0 NormalY=0 NormalZ=1 AngleXU=0 Radius=1
    g2: Circle CenterX=8 CenterY=6 CenterZ=0 NormalX=0 NormalY=0 NormalZ=1 AngleXU=0 Radius=1
    g3: BSplineCurve PolesCount=3 KnotsCount=2 Degree=2 IsPeriodic=0
    g4: GeomPoint X=0 Y=0 Z=0
    g5: GeomPoint X=8 Y=6 Z=0
    g6: LineSegment StartX=0 StartY=6 StartZ=0 EndX=8 EndY=6 EndZ=0
  constraints (14):
    c: Coincident(g0,g-1)
    c: Distance(g0) = 6
    c: Vertical(g0)
    c: Coincident(g3,g0)
    c: Weight(g1) = 1
    c: Equal(g1,g2)
    c: InternalAlignment(g1,g3)
    c: InternalAlignment(g2,g3)
    c: InternalAlignment(g4,g3)
    c: InternalAlignment(g5,g3)
    c: Block(g3)
    c: Coincident(g6,g0)
    c: Coincident(g6,g3)
    c: Horizontal(g6)
FEATURE [Sketcher::SketchObject] Sketch042
  FullyConstrained = true
  sketch-geometry (7):
    g0: LineSegment StartX=0 StartY=0 StartZ=0 EndX=0 EndY=6 EndZ=0
    g1: Circle CenterX=0 CenterY=0 CenterZ=0 NormalX=0 NormalY=0 NormalZ=1 AngleXU=0 Radius=1
    g2: Circle CenterX=8 CenterY=6 CenterZ=0 NormalX=0 NormalY=0 NormalZ=1 AngleXU=0 Radius=1
    g3: BSplineCurve PolesCount=3 KnotsCount=2 Degree=2 IsPeriodic=0
    g4: GeomPoint X=0 Y=0 Z=0
    g5: GeomPoint X=8 Y=6 Z=0
    g6: LineSegment StartX=0 StartY=6 StartZ=0 EndX=8 EndY=6 EndZ=0
  constraints (14):
    c: Coincident(g0,g-1)
    c: Distance(g0) = 6
    c: Vertical(g0)
    c: Coincident(g3,g0)
    c: Weight(g1) = 1
    c: Equal(g1,g2)
    c: InternalAlignment(g1,g3)
    c: InternalAlignment(g2,g3)
    c: InternalAlignment(g4,g3)
    c: InternalAlignment(g5,g3)
    c: Block(g3)
    c: Coincident(g6,g0)
    c: Coincident(g6,g3)
    c: Horizontal(g6)
FEATURE [Part::Extrusion] Extrude030  label="caseScrewPillarBracket008"
  Base = -> Sketch039
  Dir = (0,0,1)
  DirMode = 2
  FaceMakerClass = Part::FaceMakerBullseye
  LengthFwd = 2.4
  LengthRev = 0
  Placement = pos=(15.76,29,8.8) rot=(0,1,0;0rad)
  Solid = true
  Symmetric = false
FEATURE [Part::Extrusion] Extrude031  label="caseScrewPillarBracket009"
  Base = -> Sketch040
  Dir = (0,0,1)
  DirMode = 2
  FaceMakerClass = Part::FaceMakerBullseye
  LengthFwd = 2.4
  LengthRev = 0
  Placement = pos=(15.76,29,60.8) rot=(0,0,1;0rad)
  Solid = true
  Symmetric = false
FEATURE [Part::Extrusion] Extrude032  label="caseScrewPillarBracket010"
  Base = -> Sketch041
  Dir = (0,0,1)
  DirMode = 2
  FaceMakerClass = Part::FaceMakerBullseye
  LengthFwd = 2.4
  LengthRev = 0
  Placement = pos=(13.7,29,13.26) rot=(0,-1,0;1.5708rad)
  Solid = true
  Symmetric = false
FEATURE [Part::Extrusion] Extrude033  label="caseScrewPillarBracket011"
  Base = -> Sketch042
  Dir = (0,0,1)
  DirMode = 2
  FaceMakerClass = Part::FaceMakerBullseye
  LengthFwd = 2.4
  LengthRev = 0
  Placement = pos=(11.3,29,58.74) rot=(0,1,0;1.5708rad)
  Solid = true
  Symmetric = false
FEATURE [Sketcher::SketchObject] Sketch043
  FullyConstrained = true
  sketch-geometry (7):
    g0: LineSegment StartX=0 StartY=0 StartZ=0 EndX=0 EndY=6 EndZ=0
    g1: Circle CenterX=0 CenterY=0 CenterZ=0 NormalX=0 NormalY=0 NormalZ=1 AngleXU=0 Radius=1
    g2: Circle CenterX=8 CenterY=6 CenterZ=0 NormalX=0 NormalY=0 NormalZ=1 AngleXU=0 Radius=1
    g3: BSplineCurve PolesCount=3 KnotsCount=2 Degree=2 IsPeriodic=0
    g4: GeomPoint X=0 Y=0 Z=0
    g5: GeomPoint X=8 Y=6 Z=0
    g6: LineSegment StartX=0 StartY=6 StartZ=0 EndX=8 EndY=6 EndZ=0
  constraints (14):
    c: Coincident(g0,g-1)
    c: Distance(g0) = 6
    c: Vertical(g0)
    c: Coincident(g3,g0)
    c: Weight(g1) = 1
    c: Equal(g1,g2)
    c: InternalAlignment(g1,g3)
    c: InternalAlignment(g2,g3)
    c: InternalAlignment(g4,g3)
    c: InternalAlignment(g5,g3)
    c: Block(g3)
    c: Coincident(g6,g0)
    c: Coincident(g6,g3)
    c: Horizontal(g6)
FEATURE [Part::Extrusion] Extrude034  label="caseScrewPillarBracket012"
  Base = -> Sketch043
  Dir = (0,0,1)
  DirMode = 2
  FaceMakerClass = Part::FaceMakerBullseye
  LengthFwd = 2.4
  LengthRev = 0
  Placement = pos=(88.3,29,65.23) rot=(0,1,0;1.5708rad)
  Solid = true
  Symmetric = false
FEATURE [Sketcher::SketchObject] Sketch044
  FullyConstrained = true
  sketch-geometry (7):
    g0: LineSegment StartX=0 StartY=0 StartZ=0 EndX=0 EndY=6 EndZ=0
    g1: Circle CenterX=0 CenterY=0 CenterZ=0 NormalX=0 NormalY=0 NormalZ=1 AngleXU=0 Radius=1
    g2: Circle CenterX=8 CenterY=6 CenterZ=0 NormalX=0 NormalY=0 NormalZ=1 AngleXU=0 Radius=1
    g3: BSplineCurve PolesCount=3 KnotsCount=2 Degree=2 IsPeriodic=0
    g4: GeomPoint X=0 Y=0 Z=0
    g5: GeomPoint X=8 Y=6 Z=0
    g6: LineSegment StartX=0 StartY=6 StartZ=0 EndX=8 EndY=6 EndZ=0
  constraints (14):
    c: Coincident(g0,g-1)
    c: Distance(g0) = 6
    c: Vertical(g0)
    c: Coincident(g3,g0)
    c: Weight(g1) = 1
    c: Equal(g1,g2)
    c: InternalAlignment(g1,g3)
    c: InternalAlignment(g2,g3)
    c: InternalAlignment(g4,g3)
    c: InternalAlignment(g5,g3)
    c: Block(g3)
    c: Coincident(g6,g0)
    c: Coincident(g6,g3)
    c: Horizontal(g6)
FEATURE [Part::Extrusion] Extrude035  label="caseScrewPillarBracket013"
  Base = -> Sketch044
  Dir = (0,0,1)
  DirMode = 2
  FaceMakerClass = Part::FaceMakerBullseye
  LengthFwd = 2.4
  LengthRev = 0
  Placement = pos=(90.7,29,6.77) rot=(0,-1,0;1.5708rad)
  Solid = true
  Symmetric = false
FEATURE [Sketcher::SketchObject] Sketch045
  FullyConstrained = true
  sketch-geometry (7):
    g0: LineSegment StartX=0 StartY=0 StartZ=0 EndX=0 EndY=6 EndZ=0
    g1: Circle CenterX=0 CenterY=0 CenterZ=0 NormalX=0 NormalY=0 NormalZ=1 AngleXU=0 Radius=1
    g2: Circle CenterX=8 CenterY=6 CenterZ=0 NormalX=0 NormalY=0 NormalZ=1 AngleXU=0 Radius=1
    g3: BSplineCurve PolesCount=3 KnotsCount=2 Degree=2 IsPeriodic=0
    g4: GeomPoint X=0 Y=0 Z=0
    g5: GeomPoint X=8 Y=6 Z=0
    g6: LineSegment StartX=0 StartY=6 StartZ=0 EndX=8 EndY=6 EndZ=0
  constraints (14):
    c: Coincident(g0,g-1)
    c: Distance(g0) = 6
    c: Vertical(g0)
    c: Coincident(g3,g0)
    c: Weight(g1) = 1
    c: Equal(g1,g2)
    c: InternalAlignment(g1,g3)
    c: InternalAlignment(g2,g3)
    c: InternalAlignment(g4,g3)
    c: InternalAlignment(g5,g3)
    c: Block(g3)
    c: Coincident(g6,g0)
    c: Coincident(g6,g3)
    c: Horizontal(g6)
FEATURE [Sketcher::SketchObject] Sketch046
  FullyConstrained = true
  sketch-geometry (7):
    g0: LineSegment StartX=0 StartY=0 StartZ=0 EndX=0 EndY=6 EndZ=0
    g1: Circle CenterX=0 CenterY=0 CenterZ=0 NormalX=0 NormalY=0 NormalZ=1 AngleXU=0 Radius=1
    g2: Circle CenterX=8 CenterY=6 CenterZ=0 NormalX=0 NormalY=0 NormalZ=1 AngleXU=0 Radius=1
    g3: BSplineCurve PolesCount=3 KnotsCount=2 Degree=2 IsPeriodic=0
    g4: GeomPoint X=0 Y=0 Z=0
    g5: GeomPoint X=8 Y=6 Z=0
    g6: LineSegment StartX=0 StartY=6 StartZ=0 EndX=8 EndY=6 EndZ=0
  constraints (14):
    c: Coincident(g0,g-1)
    c: Distance(g0) = 6
    c: Vertical(g0)
    c: Coincident(g3,g0)
    c: Weight(g1) = 1
    c: Equal(g1,g2)
    c: InternalAlignment(g1,g3)
    c: InternalAlignment(g2,g3)
    c: InternalAlignment(g4,g3)
    c: InternalAlignment(g5,g3)
    c: Block(g3)
    c: Coincident(g6,g0)
    c: Coincident(g6,g3)
    c: Horizontal(g6)
FEATURE [Part::Extrusion] Extrude036  label="caseScrewPillarBracket014"
  Base = -> Sketch045
  Dir = (0,0,1)
  DirMode = 2
  FaceMakerClass = Part::FaceMakerBullseye
  LengthFwd = 2.4
  LengthRev = 0
  Placement = pos=(110.7,29,6.77) rot=(0,-1,0;1.5708rad)
  Solid = true
  Symmetric = false
FEATURE [Part::Extrusion] Extrude037  label="caseScrewPillarBracket015"
  Base = -> Sketch046
  Dir = (0,0,1)
  DirMode = 2
  FaceMakerClass = Part::FaceMakerBullseye
  LengthFwd = 2.4
  LengthRev = 0
  Placement = pos=(108.3,29,65.23) rot=(0,1,0;1.5708rad)
  Solid = true
  Symmetric = false
FEATURE [Part::Box] Box013  label="frontCaseScrewPillarBracket002"
  AttacherType = Attacher::AttachEngine3D
  Height = 2.4
  Length = 22
  Placement = pos=(87,28,2.3) rot=(0,0,1;0rad)
  Width = 7
FEATURE [Part::Box] Box014  label="frontCaseScrewPillarBracket003"
  AttacherType = Attacher::AttachEngine3D
  Height = 2.4
  Length = 22
  Placement = pos=(87,28,67.3) rot=(0,0,1;0rad)
  Width = 7
FEATURE [Part::Feature] Face087
  shape: bbox 4.8 x 30.2 x 2e-07 mm, 1 faces, 0 solids (baked)
FEATURE [Part::Revolution] Revolve091  label="frontCaseScrewPost004"
  Angle = 360
  Axis = (0,1,0)
  Base = (0,0,0)
  FaceMakerClass = Part::FaceMakerBullseye
  Placement = pos=(89.5,4.5,3.5) rot=(0,0,1;0rad)
  Solid = false
  Source = -> Face087
  Symmetric = false
FEATURE [Part::Feature] Face088
  shape: bbox 4.8 x 30.2 x 2e-07 mm, 1 faces, 0 solids (baked)
FEATURE [Part::Revolution] Revolve092  label="frontCaseScrewPost005"
  Angle = 360
  Axis = (0,1,0)
  Base = (0,0,0)
  FaceMakerClass = Part::FaceMakerBullseye
  Placement = pos=(89.5,4.5,68.5) rot=(0,0,1;0rad)
  Solid = false
  Source = -> Face088
  Symmetric = false
FEATURE [Part::Feature] Face089
  shape: bbox 3.5 x 30.2 x 2e-07 mm, 1 faces, 0 solids (baked)
FEATURE [Part::Revolution] Revolve093  label="backCaseScrewPost002"
  Angle = 360
  Axis = (0,1,0)
  Base = (0,0,0)
  FaceMakerClass = Part::FaceMakerBullseye
  Placement = pos=(12.5,4.5,10) rot=(0,0,1;0rad)
  Solid = false
  Source = -> Face089
  Symmetric = false
FEATURE [Part::Feature] Face090
  shape: bbox 3.5 x 30.2 x 2e-07 mm, 1 faces, 0 solids (baked)
FEATURE [Part::Revolution] Revolve094  label="backCaseScrewPost003"
  Angle = 360
  Axis = (0,1,0)
  Base = (0,0,0)
  FaceMakerClass = Part::FaceMakerBullseye
  Placement = pos=(12.5,4.5,62) rot=(0,0,1;0rad)
  Solid = false
  Source = -> Face090
  Symmetric = false
FEATURE [Part::Box] Box015  label="Cube011"
  AttacherType = Attacher::AttachEngine3D
  Height = 28.8
  Length = 3
  Placement = pos=(107.3,28,21.6) rot=(0,0,1;0rad)
  Width = 7
FEATURE [Part::Box] Box016  label="Cube012"
  AttacherType = Attacher::AttachEngine3D
  Height = 3
  Length = 7.4
  Placement = pos=(107.3,28,18.6) rot=(0,0,1;0rad)
  Width = 7
FEATURE [Part::Box] Box017  label="Cube013"
  AttacherType = Attacher::AttachEngine3D
  Height = 3
  Length = 7.4
  Placement = pos=(107.3,28,50.4) rot=(0,0,1;0rad)
  Width = 7
FEATURE [Part::Cylinder] Cylinder024
  Angle = 360
  AttacherType = Attacher::AttachEngine3D
  Height = 20
  Placement = pos=(0,0,36.15) rot=(0,0,1;0rad)
  Radius = 14.3
FEATURE [Part::Cylinder] Cylinder025
  Angle = 360
  AttacherType = Attacher::AttachEngine3D
  Height = 10
  Placement = pos=(0,0,36.15) rot=(0,0,1;0rad)
  Radius = 4
FEATURE [Part::MultiFuse] Fusion066  label="removeToCreteHoleForPlugHousing009"
  Placement = pos=(70,19,36) rot=(0,1,0;1.5708rad)
  Shapes = -> [Cylinder024,Cylinder025]
FEATURE [Part::MultiFuse] Fusion065  label="plugHousingBracketHolder002"
  Shapes = -> [Box017,Box015,Box016]
FEATURE [Part::Cut] Cut025  label="plugHousingBracketHolder003"
  Base = -> Fusion065
  Placement = pos=(7,0,0) rot=(0,0,1;0rad)
  Tool = -> Fusion066
FEATURE [Sketcher::SketchObject] Sketch047
  FullyConstrained = false
  Placement = pos=(0,0,0) rot=(1,0,0;1.5708rad)
  sketch-geometry (24):
    g0: ArcOfCircle CenterX=-4 CenterY=-10.5 CenterZ=0 NormalX=0 NormalY=0 NormalZ=1 AngleXU=0 Radius=1.5 StartAngle=6e-16 EndAngle=3.14159
    g1: ArcOfCircle CenterX=-34.2 CenterY=-10.5 CenterZ=0 NormalX=0 NormalY=0 NormalZ=1 AngleXU=0 Radius=1.5 StartAngle=0 EndAngle=3.14159
    g2: ArcOfCircle CenterX=-34.2 CenterY=-27.7 CenterZ=0 NormalX=0 NormalY=0 NormalZ=1 AngleXU=0 Radius=1.5 StartAngle=3.14159 EndAngle=6.28319
    g3: ArcOfCircle CenterX=-4 CenterY=-27.7 CenterZ=0 NormalX=0 NormalY=0 NormalZ=1 AngleXU=0 Radius=1.5 StartAngle=3.1416 EndAngle=6.28319
    g4: ArcOfCircle CenterX=-10 CenterY=-4.3 CenterZ=0 NormalX=0 NormalY=0 NormalZ=1 AngleXU=0 Radius=1.5 StartAngle=2e-16 EndAngle=3.14159
    g5: ArcOfCircle CenterX=-16.1 CenterY=-1.8 CenterZ=0 NormalX=0 NormalY=0 NormalZ=1 AngleXU=0 Radius=1.5 StartAngle=5e-16 EndAngle=3.14159
    g6: ArcOfCircle CenterX=-22.1 CenterY=-1.8 CenterZ=0 NormalX=0 NormalY=0 NormalZ=1 AngleXU=0 Radius=1.5 StartAngle=5e-16 EndAngle=3.14159
    g7: ArcOfCircle CenterX=-28.2 CenterY=-4.3 CenterZ=0 NormalX=0 NormalY=0 NormalZ=1 AngleXU=0 Radius=1.5 StartAngle=2e-16 EndAngle=3.14159
    g8: ArcOfCircle CenterX=-10 CenterY=-33.9 CenterZ=0 NormalX=0 NormalY=0 NormalZ=1 AngleXU=0 Radius=1.5 StartAngle=3.14159 EndAngle=6.28319
    g9: ArcOfCircle CenterX=-16.1 CenterY=-36.4 CenterZ=0 NormalX=0 NormalY=0 NormalZ=1 AngleXU=0 Radius=1.5 StartAngle=3.14159 EndAngle=6.28319
    g10: ArcOfCircle CenterX=-22.1 CenterY=-36.4 CenterZ=0 NormalX=0 NormalY=0 NormalZ=1 AngleXU=0 Radius=1.5 StartAngle=3.14159 EndAngle=6.28319
    g11: ArcOfCircle CenterX=-28.2 CenterY=-33.9 CenterZ=0 NormalX=0 NormalY=0 NormalZ=1 AngleXU=0 Radius=1.5 StartAngle=3.14159 EndAngle=6.28319
    g12: LineSegment StartX=-35.7 StartY=-10.5 StartZ=0 EndX=-35.7 EndY=-27.7 EndZ=0
    g13: LineSegment StartX=-32.7 StartY=-10.5 StartZ=0 EndX=-32.7 EndY=-27.7 EndZ=0
    g14: LineSegment StartX=-29.7 StartY=-33.9 StartZ=0 EndX=-29.7 EndY=-4.3 EndZ=0
    g15: LineSegment StartX=-26.7 StartY=-33.9 StartZ=0 EndX=-26.7 EndY=-4.3 EndZ=0
    g16: LineSegment StartX=-2.5 StartY=-10.5 StartZ=0 EndX=-2.5 EndY=-27.7 EndZ=0
    g17: LineSegment StartX=-8.5 StartY=-4.3 StartZ=0 EndX=-8.5 EndY=-33.9 EndZ=0
    g18: LineSegment StartX=-5.5 StartY=-10.5 StartZ=0 EndX=-5.5 EndY=-27.7 EndZ=0
    g19: LineSegment StartX=-11.5 StartY=-4.3 StartZ=0 EndX=-11.5 EndY=-33.9 EndZ=0
    g20: LineSegment StartX=-14.6 StartY=-1.8 StartZ=0 EndX=-14.6 EndY=-36.4 EndZ=0
    g21: LineSegment StartX=-17.6 StartY=-1.8 StartZ=0 EndX=-17.6 EndY=-36.4 EndZ=0
    g22: LineSegment StartX=-20.6 StartY=-36.4 StartZ=0 EndX=-20.6 EndY=-1.8 EndZ=0
    g23: LineSegment StartX=-23.6 StartY=-1.8 StartZ=0 EndX=-23.6 EndY=-36.4 EndZ=0
  constraints (48):
    c: Block(g0)
    c: Block(g1)
    c: Block(g2)
    c: Block(g3)
    c: Block(g4)
    c: Block(g5)
    c: Block(g6)
    c: Block(g7)
    c: Block(g8)
    c: Block(g9)
    c: Block(g10)
    c: Block(g11)
    c: Coincident(g12,g1)
    c: Coincident(g12,g2)
    c: Vertical(g12)
    c: Coincident(g13,g1)
    c: Coincident(g13,g2)
    c: Vertical(g13)
    c: Coincident(g14,g11)
    c: Coincident(g14,g7)
    c: Vertical(g14)
    c: Coincident(g15,g11)
    c: Coincident(g15,g7)
    c: Vertical(g15)
    c: Coincident(g16,g0)
    c: Coincident(g16,g3)
    c: Vertical(g16)
    c: Coincident(g17,g4)
    c: Coincident(g17,g8)
    c: Vertical(g17)
    c: Coincident(g18,g0)
    c: Coincident(g18,g3)
    c: Vertical(g18)
    c: Coincident(g19,g4)
    c: Coincident(g19,g8)
    c: Vertical(g19)
    c: Coincident(g20,g5)
    c: Coincident(g20,g9)
    c: Vertical(g20)
    c: Coincident(g21,g5)
    c: Coincident(g21,g9)
    c: Vertical(g21)
    c: Coincident(g22,g10)
    c: Coincident(g22,g6)
    c: Vertical(g22)
    c: Coincident(g23,g6)
    c: Coincident(g23,g10)
    c: Vertical(g23)
FEATURE [Part::Extrusion] Extrude038  label="removeToCreateFanGrillHoles001"
  Base = -> Sketch047
  Dir = (0,-1,6e-16)
  DirMode = 2
  FaceMakerClass = Part::FaceMakerBullseye
  LengthFwd = 10
  LengthRev = 0
  Placement = pos=(65.4,44,54.82) rot=(0,0,1;0rad)
  Solid = true
  Symmetric = false
FEATURE [Part::Feature] Wire004
  shape: bbox 11 x 5.2 x 2e-07 mm, 0 faces, 0 solids (baked)
FEATURE [Part::Revolution] Revolve095
  Angle = 360
  Axis = (0,1,0)
  Base = (0,0,0)
  FaceMakerClass = Part::FaceMakerBullseye
  Placement = pos=(30.3,38,19.7) rot=(0,0,1;0rad)
  Solid = true
  Source = -> Wire004
  Symmetric = false
FEATURE [Part::Feature] Wire005
  shape: bbox 11 x 5.2 x 2e-07 mm, 0 faces, 0 solids (baked)
FEATURE [Part::Revolution] Revolve096
  Angle = 360
  Axis = (0,1,0)
  Base = (0,0,0)
  FaceMakerClass = Part::FaceMakerBullseye
  Placement = pos=(30.3,38,51.7) rot=(0,0,1;0rad)
  Solid = true
  Source = -> Wire005
  Symmetric = false
FEATURE [Part::Feature] Wire006
  shape: bbox 11 x 5.2 x 2e-07 mm, 0 faces, 0 solids (baked)
FEATURE [Part::Revolution] Revolve097
  Angle = 360
  Axis = (0,1,0)
  Base = (0,0,0)
  FaceMakerClass = Part::FaceMakerBullseye
  Placement = pos=(62.3,38,51.7) rot=(0,0,1;0rad)
  Solid = true
  Source = -> Wire006
  Symmetric = false
FEATURE [Part::Feature] Wire007
  shape: bbox 11 x 5.2 x 2e-07 mm, 0 faces, 0 solids (baked)
FEATURE [Part::Revolution] Revolve098
  Angle = 360
  Axis = (0,1,0)
  Base = (0,0,0)
  FaceMakerClass = Part::FaceMakerBullseye
  Placement = pos=(62.3,38,19.7) rot=(0,0,1;0rad)
  Solid = true
  Source = -> Wire007
  Symmetric = false
FEATURE [Part::MultiFuse] Fusion067  label="fanScrewHousing002"
  Shapes = -> [Revolve098,Revolve097,Revolve096,Revolve095]
FEATURE [Part::Feature] Face091 .. Face094  x4 (patterned run collapsed; names and placements below)
  shape: bbox 3.5 x 17.8 x 2e-07 mm, 1 faces, 0 solids (baked)
FEATURE [Part::Revolution] Revolve099  label="removeToCreateScrewAndThreadedInsertHole026"
  Angle = 360
  Axis = (0,1,0)
  Base = (0,0,0)
  FaceMakerClass = Part::FaceMakerBullseye
  Placement = pos=(62.3,30.3,19.7) rot=(0,0,1;0rad)
  Solid = false
  Source = -> Face091
  Symmetric = false
FEATURE [Part::Revolution] Revolve100  label="removeToCreateScrewAndThreadedInsertHole027"
  Angle = 360
  Axis = (0,1,0)
  Base = (0,0,0)
  FaceMakerClass = Part::FaceMakerBullseye
  Placement = pos=(62.3,30.3,51.7) rot=(0,0,1;0rad)
  Solid = false
  Source = -> Face092
  Symmetric = false
FEATURE [Part::Revolution] Revolve101  label="removeToCreateScrewAndThreadedInsertHole028"
  Angle = 360
  Axis = (0,1,0)
  Base = (0,0,0)
  FaceMakerClass = Part::FaceMakerBullseye
  Placement = pos=(30.3,30.3,19.7) rot=(0,0,1;0rad)
  Solid = false
  Source = -> Face093
  Symmetric = false
FEATURE [Part::Revolution] Revolve102  label="removeToCreateScrewAndThreadedInsertHole029"
  Angle = 360
  Axis = (0,1,0)
  Base = (0,0,0)
  FaceMakerClass = Part::FaceMakerBullseye
  Placement = pos=(30.3,30.3,51.7) rot=(0,0,1;0rad)
  Solid = false
  Source = -> Face094
  Symmetric = false
FEATURE [Part::MultiFuse] Fusion068  label="createThreadedInsertHolesForFan002"
  Shapes = -> [Revolve099,Revolve100,Revolve101,Revolve102]
FEATURE [Part::Cut] Cut026  label="fanScrewHousing003"
  Base = -> Fusion067
  Tool = -> Fusion068
FEATURE [Sketcher::SketchObject] Sketch048
  FullyConstrained = false
  Placement = pos=(0,0,0) rot=(1,0,0;1.5708rad)
  sketch-geometry (24):
    g0: ArcOfCircle CenterX=-4 CenterY=-10.5 CenterZ=0 NormalX=0 NormalY=0 NormalZ=1 AngleXU=0 Radius=1.5 StartAngle=6e-16 EndAngle=3.14159
    g1: ArcOfCircle CenterX=-34.2 CenterY=-10.5 CenterZ=0 NormalX=0 NormalY=0 NormalZ=1 AngleXU=0 Radius=1.5 StartAngle=0 EndAngle=3.14159
    g2: ArcOfCircle CenterX=-34.2 CenterY=-27.7 CenterZ=0 NormalX=0 NormalY=0 NormalZ=1 AngleXU=0 Radius=1.5 StartAngle=3.14159 EndAngle=6.28319
    g3: ArcOfCircle CenterX=-4 CenterY=-27.7 CenterZ=0 NormalX=0 NormalY=0 NormalZ=1 AngleXU=0 Radius=1.5 StartAngle=3.1416 EndAngle=6.28319
    g4: ArcOfCircle CenterX=-10 CenterY=-4.3 CenterZ=0 NormalX=0 NormalY=0 NormalZ=1 AngleXU=0 Radius=1.5 StartAngle=2e-16 EndAngle=3.14159
    g5: ArcOfCircle CenterX=-16.1 CenterY=-1.8 CenterZ=0 NormalX=0 NormalY=0 NormalZ=1 AngleXU=0 Radius=1.5 StartAngle=5e-16 EndAngle=3.14159
    g6: ArcOfCircle CenterX=-22.1 CenterY=-1.8 CenterZ=0 NormalX=0 NormalY=0 NormalZ=1 AngleXU=0 Radius=1.5 StartAngle=5e-16 EndAngle=3.14159
    g7: ArcOfCircle CenterX=-28.2 CenterY=-4.3 CenterZ=0 NormalX=0 NormalY=0 NormalZ=1 AngleXU=0 Radius=1.5 StartAngle=2e-16 EndAngle=3.14159
    g8: ArcOfCircle CenterX=-10 CenterY=-33.9 CenterZ=0 NormalX=0 NormalY=0 NormalZ=1 AngleXU=0 Radius=1.5 StartAngle=3.14159 EndAngle=6.28319
    g9: ArcOfCircle CenterX=-16.1 CenterY=-36.4 CenterZ=0 NormalX=0 NormalY=0 NormalZ=1 AngleXU=0 Radius=1.5 StartAngle=3.14159 EndAngle=6.28319
    g10: ArcOfCircle CenterX=-22.1 CenterY=-36.4 CenterZ=0 NormalX=0 NormalY=0 NormalZ=1 AngleXU=0 Radius=1.5 StartAngle=3.14159 EndAngle=6.28319
    g11: ArcOfCircle CenterX=-28.2 CenterY=-33.9 CenterZ=0 NormalX=0 NormalY=0 NormalZ=1 AngleXU=0 Radius=1.5 StartAngle=3.14159 EndAngle=6.28319
    g12: LineSegment StartX=-35.7 StartY=-10.5 StartZ=0 EndX=-35.7 EndY=-27.7 EndZ=0
    g13: LineSegment StartX=-32.7 StartY=-10.5 StartZ=0 EndX=-32.7 EndY=-27.7 EndZ=0
    g14: LineSegment StartX=-29.7 StartY=-33.9 StartZ=0 EndX=-29.7 EndY=-4.3 EndZ=0
    g15: LineSegment StartX=-26.7 StartY=-33.9 StartZ=0 EndX=-26.7 EndY=-4.3 EndZ=0
    g16: LineSegment StartX=-2.5 StartY=-10.5 StartZ=0 EndX=-2.5 EndY=-27.7 EndZ=0
    g17: LineSegment StartX=-8.5 StartY=-4.3 StartZ=0 EndX=-8.5 EndY=-33.9 EndZ=0
    g18: LineSegment StartX=-5.5 StartY=-10.5 StartZ=0 EndX=-5.5 EndY=-27.7 EndZ=0
    g19: LineSegment StartX=-11.5 StartY=-4.3 StartZ=0 EndX=-11.5 EndY=-33.9 EndZ=0
    g20: LineSegment StartX=-14.6 StartY=-1.8 StartZ=0 EndX=-14.6 EndY=-36.4 EndZ=0
    g21: LineSegment StartX=-17.6 StartY=-1.8 StartZ=0 EndX=-17.6 EndY=-36.4 EndZ=0
    g22: LineSegment StartX=-20.6 StartY=-36.4 StartZ=0 EndX=-20.6 EndY=-1.8 EndZ=0
    g23: LineSegment StartX=-23.6 StartY=-1.8 StartZ=0 EndX=-23.6 EndY=-36.4 EndZ=0
  constraints (48):
    c: Block(g0)
    c: Block(g1)
    c: Block(g2)
    c: Block(g3)
    c: Block(g4)
    c: Block(g5)
    c: Block(g6)
    c: Block(g7)
    c: Block(g8)
    c: Block(g9)
    c: Block(g10)
    c: Block(g11)
    c: Coincident(g12,g1)
    c: Coincident(g12,g2)
    c: Vertical(g12)
    c: Coincident(g13,g1)
    c: Coincident(g13,g2)
    c: Vertical(g13)
    c: Coincident(g14,g11)
    c: Coincident(g14,g7)
    c: Vertical(g14)
    c: Coincident(g15,g11)
    c: Coincident(g15,g7)
    c: Vertical(g15)
    c: Coincident(g16,g0)
    c: Coincident(g16,g3)
    c: Vertical(g16)
    c: Coincident(g17,g4)
    c: Coincident(g17,g8)
    c: Vertical(g17)
    c: Coincident(g18,g0)
    c: Coincident(g18,g3)
    c: Vertical(g18)
    c: Coincident(g19,g4)
    c: Coincident(g19,g8)
    c: Vertical(g19)
    c: Coincident(g20,g5)
    c: Coincident(g20,g9)
    c: Vertical(g20)
    c: Coincident(g21,g5)
    c: Coincident(g21,g9)
    c: Vertical(g21)
    c: Coincident(g22,g10)
    c: Coincident(g22,g6)
    c: Vertical(g22)
    c: Coincident(g23,g6)
    c: Coincident(g23,g10)
    c: Vertical(g23)
FEATURE [Part::Extrusion] Extrude039  label="removeToCreateFanGrillHoles002"
  Base = -> Sketch048
  Dir = (0,-1,6e-16)
  DirMode = 2
  FaceMakerClass = Part::FaceMakerBullseye
  LengthFwd = 10
  LengthRev = 0
  Placement = pos=(65.4,44,54.82) rot=(0,0,1;0rad)
  Solid = true
  Symmetric = false
FEATURE [Part::Cut] Cut027  label="fanScrewHousing004"
  Base = -> Cut026
  Tool = -> Extrude038
FEATURE [Part::Cut] Cut028  label="top014"
  Base = -> Fillet026
  Tool = -> Extrude039
FEATURE [Part::Feature] Face095 .. Face098  x4 (patterned run collapsed; names and placements below)
  shape: bbox 3.5 x 17.8 x 2e-07 mm, 1 faces, 0 solids (baked)
FEATURE [Part::Revolution] Revolve103  label="removeToCreateScrewAndThreadedInsertHole030"
  Angle = 360
  Axis = (0,1,0)
  Base = (0,0,0)
  FaceMakerClass = Part::FaceMakerBullseye
  Placement = pos=(62.3,30.3,19.7) rot=(0,0,1;0rad)
  Solid = false
  Source = -> Face095
  Symmetric = false
FEATURE [Part::Revolution] Revolve104  label="removeToCreateScrewAndThreadedInsertHole031"
  Angle = 360
  Axis = (0,1,0)
  Base = (0,0,0)
  FaceMakerClass = Part::FaceMakerBullseye
  Placement = pos=(62.3,30.3,51.7) rot=(0,0,1;0rad)
  Solid = false
  Source = -> Face096
  Symmetric = false
FEATURE [Part::Revolution] Revolve105  label="removeToCreateScrewAndThreadedInsertHole032"
  Angle = 360
  Axis = (0,1,0)
  Base = (0,0,0)
  FaceMakerClass = Part::FaceMakerBullseye
  Placement = pos=(30.3,30.3,19.7) rot=(0,0,1;0rad)
  Solid = false
  Source = -> Face097
  Symmetric = false
FEATURE [Part::Revolution] Revolve106  label="removeToCreateScrewAndThreadedInsertHole033"
  Angle = 360
  Axis = (0,1,0)
  Base = (0,0,0)
  FaceMakerClass = Part::FaceMakerBullseye
  Placement = pos=(30.3,30.3,51.7) rot=(0,0,1;0rad)
  Solid = false
  Source = -> Face098
  Symmetric = false
FEATURE [Part::MultiFuse] Fusion069  label="createThreadedInsertHolesForFan003"
  Shapes = -> [Revolve103,Revolve104,Revolve105,Revolve106]
FEATURE [Part::Cut] Cut029  label="top015"
  Base = -> Cut028
  Tool = -> Fusion054
FEATURE [Part::Cut] Cut030  label="fanScrewHousing005"
  Base = -> Cut027
  Tool = -> Fusion069
FEATURE [Part::Cylinder] Cylinder026  label="removeToCreteHoleForPlugHousing010"
  Angle = 360
  AttacherType = Attacher::AttachEngine3D
  Height = 20
  Placement = pos=(-2,19,36) rot=(0,1,0;1.5708rad)
  Radius = 14.3
FEATURE [Part::Box] Box018  label="removeToCreteHoleForPlugHousing011"
  AttacherType = Attacher::AttachEngine3D
  Height = 28.6
  Length = 10
  Placement = pos=(-2,0,21.7) rot=(0,0,1;0rad)
  Width = 19
FEATURE [Part::Box] Box019  label="wireHolderBottomCaseBit"
  AttacherType = Attacher::AttachEngine3D
  Height = 28
  Length = 3
  Placement = pos=(0,0,22) rot=(0,0,1;0rad)
  Width = 21
FEATURE [Part::Cylinder] Cylinder027  label="removeToCreteHoleForPlugHousing012"
  Angle = 360
  AttacherType = Attacher::AttachEngine3D
  Height = 20
  Placement = pos=(-2,19,36) rot=(0,1,0;1.5708rad)
  Radius = 14.3
FEATURE [Part::Cut] Cut031  label="wireHolderBottomCaseBit001"
  Base = -> Box019
  Tool = -> Cylinder027
FEATURE [Part::MultiFuse] Fusion070  label="removeToCreteHoleForPlugHousing013"
  Shapes = -> [Box018,Cylinder026]
FEATURE [Part::Cut] Cut032  label="top016"
  Base = -> Cut029
  Tool = -> Fusion070
FEATURE [Part::Cylinder] Cylinder028
  Angle = 360
  AttacherType = Attacher::AttachEngine3D
  Height = 20
  Placement = pos=(0,0,36.15) rot=(0,0,1;0rad)
  Radius = 14.3
FEATURE [Part::Cylinder] Cylinder029
  Angle = 360
  AttacherType = Attacher::AttachEngine3D
  Height = 10
  Placement = pos=(0,0,36.15) rot=(0,0,1;0rad)
  Radius = 4
FEATURE [Part::MultiFuse] Fusion071  label="removeToCreteHoleForPlugHousing014"
  Placement = pos=(70,19,36) rot=(0,1,0;1.5708rad)
  Shapes = -> [Cylinder028,Cylinder029]
FEATURE [Sketcher::SketchObject] Sketch049  label="topSketch011"
  FullyConstrained = true
  sketch-geometry (4):
    g0: ArcOfCircle CenterX=105 CenterY=19 CenterZ=0 NormalX=0 NormalY=0 NormalZ=1 AngleXU=0 Radius=20.6155 StartAngle=5.54125 EndAngle=6.28319
    g1: ArcOfCircle CenterX=105 CenterY=19 CenterZ=0 NormalX=0 NormalY=0 NormalZ=1 AngleXU=0 Radius=13 StartAngle=5.54125 EndAngle=6.28319
    g2: LineSegment StartX=118 StartY=19 StartZ=0 EndX=125.616 EndY=19 EndZ=0
    g3: LineSegment StartX=114.583 StartY=10.2157 StartZ=0 EndX=120.197 EndY=5.06982 EndZ=0
  constraints (7):
    c: Block(g0)
    c: Block(g1)
    c: Coincident(g2,g1)
    c: Coincident(g2,g0)
    c: Horizontal(g2)
    c: Coincident(g3,g1)
    c: Coincident(g3,g0)
FEATURE [Part::Box] Box020  label="removeToCreteHoleForPlugHousing015"
  AttacherType = Attacher::AttachEngine3D
  Height = 28.6
  Length = 20
  Placement = pos=(106.15,0,21.7) rot=(0,0,1;0rad)
  Width = 19
FEATURE [Part::MultiFuse] Fusion072  label="removeToCreteHoleForPlugHousing016"
  Shapes = -> [Box020,Fusion071]
FEATURE [Part::Cut] Cut033  label="removeToCreteHoleForPlugHousing017"
  Base = -> Cut032
  Tool = -> Fusion072
FEATURE [Part::Cylinder] Cylinder030
  Angle = 360
  AttacherType = Attacher::AttachEngine3D
  Height = 20
  Placement = pos=(0,0,36.15) rot=(0,0,1;0rad)
  Radius = 14.3
FEATURE [Part::Cylinder] Cylinder031
  Angle = 360
  AttacherType = Attacher::AttachEngine3D
  Height = 10
  Placement = pos=(0,0,36.15) rot=(0,0,1;0rad)
  Radius = 4
FEATURE [Part::Box] Box021  label="removeToCreteHoleForPlugHousing019"
  AttacherType = Attacher::AttachEngine3D
  Height = 28.6
  Length = 20
  Placement = pos=(106.15,0,21.7) rot=(0,0,1;0rad)
  Width = 19
FEATURE [Part::MultiFuse] Fusion074  label="removeToCreteHoleForPlugHousing020"
  Placement = pos=(70,19,36) rot=(0,1,0;1.5708rad)
  Shapes = -> [Cylinder030,Cylinder031]
FEATURE [Part::MultiFuse] Fusion073  label="removeToCreteHoleForPlugHousing018"
  Placement = pos=(0,0,28.3) rot=(0,0,1;0rad)
  Shapes = -> [Box021,Fusion074]
FEATURE [Part::Cylinder] Cylinder032
  Angle = 360
  AttacherType = Attacher::AttachEngine3D
  Height = 20
  Placement = pos=(0,0,36.15) rot=(0,0,1;0rad)
  Radius = 14.3
FEATURE [Part::Cylinder] Cylinder033
  Angle = 360
  AttacherType = Attacher::AttachEngine3D
  Height = 10
  Placement = pos=(0,0,36.15) rot=(0,0,1;0rad)
  Radius = 4
FEATURE [Part::Box] Box022  label="removeToCreteHoleForPlugHousing021"
  AttacherType = Attacher::AttachEngine3D
  Height = 28.6
  Length = 20
  Placement = pos=(106.15,0,21.7) rot=(0,0,1;0rad)
  Width = 19
FEATURE [Part::MultiFuse] Fusion076  label="removeToCreteHoleForPlugHousing023"
  Placement = pos=(70,19,36) rot=(0,1,0;1.5708rad)
  Shapes = -> [Cylinder032,Cylinder033]
FEATURE [Part::MultiFuse] Fusion075  label="removeToCreteHoleForPlugHousing022"
  Placement = pos=(0,0,-28.3) rot=(0,0,1;0rad)
  Shapes = -> [Box022,Fusion076]
FEATURE [Part::MultiFuse] Fusion077  label="removeToCreatePlugHousingBottomBit"
  Shapes = -> [Fusion075,Fusion073]
FEATURE [Part::Cylinder] Cylinder034
  Angle = 360
  AttacherType = Attacher::AttachEngine3D
  Height = 20
  Placement = pos=(0,0,36.15) rot=(0,0,1;0rad)
  Radius = 14
FEATURE [Part::Cylinder] Cylinder035
  Angle = 360
  AttacherType = Attacher::AttachEngine3D
  Height = 10
  Placement = pos=(0,0,36.15) rot=(0,0,1;0rad)
  Radius = 4
FEATURE [Part::MultiFuse] Fusion078  label="removeToCreteHoleForPlugHousing024"
  Placement = pos=(70,19,36) rot=(0,1,0;1.5708rad)
  Shapes = -> [Cylinder034,Cylinder035]
FEATURE [Part::MultiFuse] Fusion079  label="removeToCreatePlugHousingBottomBit001"
  Shapes = -> [Fusion078,Fusion077]
FEATURE [Part::Extrusion] Extrude040  label="bottomPlugHousingBit"
  Base = -> Sketch049
  Dir = (0,0,1)
  DirMode = 2
  FaceMakerClass = Part::FaceMakerBullseye
  LengthFwd = 72
  LengthRev = 0
  Solid = true
  Symmetric = false
FEATURE [Part::Cut] Cut034  label="bottomPlugHousingBit001"
  Base = -> Extrude040
  Placement = pos=(-0.09,0,0) rot=(0,0,1;0rad)
  Tool = -> Fusion079
FEATURE [Part::Box] Box023  label="Cube014"
  AttacherType = Attacher::AttachEngine3D
  Height = 16
  Length = 8
  Placement = pos=(12.7,31.52,28) rot=(0,0,1;0rad)
  Width = 4
FEATURE [Part::Cylinder] Cylinder036
  Angle = 360
  AttacherType = Attacher::AttachEngine3D
  Height = 10
  Placement = pos=(0,0,36.15) rot=(0,0,1;0rad)
  Radius = 4
FEATURE [Part::Cylinder] Cylinder037
  Angle = 360
  AttacherType = Attacher::AttachEngine3D
  Height = 20
  Placement = pos=(0,0,36.15) rot=(0,0,1;0rad)
  Radius = 8.2
FEATURE [Part::MultiFuse] Fusion080  label="removeToCreteHoleForPlugHousing025"
  Placement = pos=(-42,19,36) rot=(0,1,0;1.5708rad)
  Shapes = -> [Cylinder037,Cylinder036]
FEATURE [Sketcher::SketchObject] Sketch050  label="topSketch012"
  FullyConstrained = true
  sketch-geometry (4):
    g0: LineSegment StartX=16.8446 StartY=31.512 StartZ=0 EndX=16.3251 EndY=34.4666 EndZ=0
    g1: ArcOfCircle CenterX=19 CenterY=19.2524 CenterZ=0 NormalX=0 NormalY=0 NormalZ=1 AngleXU=0 Radius=15.4476 StartAngle=1.74483 EndAngle=2.72717
    g2: ArcOfCircle CenterX=19 CenterY=19.2524 CenterZ=0 NormalX=0 NormalY=0 NormalZ=1 AngleXU=0 Radius=12.4476 StartAngle=1.74483 EndAngle=2.73189
    g3: LineSegment StartX=4.86004 StartY=25.4725 StartZ=0 EndX=7.58253 EndY=24.2107 EndZ=0
  constraints (7):
    c: Block(g0)
    c: Coincident(g1,g0)
    c: Coincident(g2,g0)
    c: Coincident(g3,g1)
    c: Coincident(g3,g2)
    c: Block(g1)
    c: Block(g2)
FEATURE [Part::Extrusion] Extrude041
  Base = -> Sketch050
  Dir = (0,0,1)
  DirMode = 2
  FaceMakerClass = Part::FaceMakerBullseye
  LengthFwd = 10.6
  LengthRev = 0
  Placement = pos=(0,0,31) rot=(0,0,1;0rad)
  Solid = true
  Symmetric = false
FEATURE [Part::Cut] Cut035
  Base = -> Extrude041
  Placement = pos=(0,0,-0.3) rot=(0,0,1;0rad)
  Tool = -> Fusion080
FEATURE [Part::Cut] Cut036
  Base = -> Box023
  Tool = -> Cut035
FEATURE [Part::Fillet] Fillet027
  Base = -> Cut036
  Edges = 1 edges r=0.7: [Edge13]
FEATURE [Part::Fillet] Fillet028
  Base = -> Fillet027
  Edges = 1 edges r=0.7: [Edge13]
FEATURE [Part::Fillet] Fillet029
  Base = -> Fillet028
  Edges = 1 edges r=0.7: [Edge16]
FEATURE [Part::Fillet] Fillet030
  Base = -> Fillet029
  Edges = 1 edges r=0.7: [Edge11]
FEATURE [Part::Fillet] Fillet031
  Base = -> Fillet030
  Edges = 1 edges r=0.7: [Edge10]
FEATURE [Part::Fillet] Fillet032
  Base = -> Fillet031
  Edges = 1 edges r=1.2: [Edge5]
FEATURE [Part::Fillet] Fillet033
  Base = -> Fillet032
  Edges = 1 edges r=1.2: [Edge12]
FEATURE [Part::Fillet] Fillet034  label="wireHousingRetainer"
  Base = -> Fillet033
  Edges = 1 edges r=2: [Edge1]
  Placement = pos=(0.3,0,0) rot=(0,0,1;0rad)
FEATURE [Part::Feature] Face099
  shape: bbox 3.5 x 17.8 x 2e-07 mm, 1 faces, 0 solids (baked)
FEATURE [Part::Revolution] Revolve107  label="removeToCreateScrewAndThreadedInsertHole034"
  Angle = 360
  Axis = (0,1,0)
  Base = (0,0,0)
  FaceMakerClass = Part::FaceMakerBullseye
  Placement = pos=(12.5,0,10) rot=(0,0,1;0rad)
  Solid = false
  Source = -> Face099
  Symmetric = false
FEATURE [Part::Feature] Face100
  shape: bbox 3.5 x 17.8 x 2e-07 mm, 1 faces, 0 solids (baked)
FEATURE [Part::Revolution] Revolve108  label="removeToCreateScrewAndThreadedInsertHole035"
  Angle = 360
  Axis = (0,1,0)
  Base = (0,0,0)
  FaceMakerClass = Part::FaceMakerBullseye
  Placement = pos=(12.5,0,62) rot=(0,0,1;0rad)
  Solid = false
  Source = -> Face100
  Symmetric = false
FEATURE [Part::Feature] Face101
  shape: bbox 3.5 x 17.8 x 2e-07 mm, 1 faces, 0 solids (baked)
FEATURE [Part::Revolution] Revolve109  label="removeToCreateScrewAndThreadedInsertHole036"
  Angle = 360
  Axis = (0,1,0)
  Base = (0,0,0)
  FaceMakerClass = Part::FaceMakerBullseye
  Placement = pos=(89.5,0,68.5) rot=(0,0,1;0rad)
  Solid = false
  Source = -> Face101
  Symmetric = false
FEATURE [Part::Feature] Face102
  shape: bbox 3.5 x 17.8 x 2e-07 mm, 1 faces, 0 solids (baked)
FEATURE [Part::Revolution] Revolve110  label="removeToCreateScrewAndThreadedInsertHole037"
  Angle = 360
  Axis = (0,1,0)
  Base = (0,0,0)
  FaceMakerClass = Part::FaceMakerBullseye
  Placement = pos=(89.5,0,3.5) rot=(0,0,1;0rad)
  Solid = false
  Source = -> Face102
  Symmetric = false
FEATURE [Part::Feature] Face103
  shape: bbox 3.5 x 17.8 x 2e-07 mm, 1 faces, 0 solids (baked)
FEATURE [Part::Revolution] Revolve111  label="removeToCreateScrewAndThreadedInsertHole038"
  Angle = 360
  Axis = (0,1,0)
  Base = (0,0,0)
  FaceMakerClass = Part::FaceMakerBullseye
  Placement = pos=(109.5,4.7,3.5) rot=(0,0,1;0rad)
  Solid = false
  Source = -> Face103
  Symmetric = false
FEATURE [Part::Feature] Face104
  shape: bbox 3.5 x 17.8 x 2e-07 mm, 1 faces, 0 solids (baked)
FEATURE [Part::Revolution] Revolve112  label="removeToCreateScrewAndThreadedInsertHole039"
  Angle = 360
  Axis = (0,1,0)
  Base = (0,0,0)
  FaceMakerClass = Part::FaceMakerBullseye
  Placement = pos=(109.5,4.7,68.5) rot=(0,0,1;0rad)
  Solid = false
  Source = -> Face104
  Symmetric = false
FEATURE [Part::MultiFuse] Fusion081  label="removeToCreateScrewAndThreadedInsertHole040"
  Shapes = -> [Revolve107,Revolve108,Revolve109,Revolve110,Revolve111,Revolve112]
FEATURE [Part::MultiFuse] Fusion082  label="casePillars002"
  Shapes = -> [Revolve094,Revolve092,Revolve090,Revolve089,Revolve091,Revolve093]
FEATURE [Part::Cut] Cut037  label="casePillars003"
  Base = -> Fusion082
  Tool = -> Fusion081
FEATURE [Sketcher::SketchObject] Sketch051
  FullyConstrained = true
  Placement = pos=(117,19,0) rot=(0.57735,0.57735,0.57735;2.0944rad)
  sketch-geometry (48):
    g0: LineSegment StartX=-49.19 StartY=69.25 StartZ=0 EndX=-49.19 EndY=66.25 EndZ=0
    g1: LineSegment StartX=-49.19 StartY=63.5 StartZ=0 EndX=-49.19 EndY=60.5 EndZ=0
    g2: LineSegment StartX=-49.19 StartY=57.75 StartZ=0 EndX=-49.19 EndY=54.75 EndZ=0
    g3: LineSegment StartX=-49.19 StartY=52 StartZ=0 EndX=-49.19 EndY=49 EndZ=0
    g4: LineSegment StartX=-49.19 StartY=46.25 StartZ=0 EndX=-49.19 EndY=43.25 EndZ=0
    g5: LineSegment StartX=-49.19 StartY=40.5 StartZ=0 EndX=-49.19 EndY=37.5 EndZ=0
    g6: LineSegment StartX=-49.19 StartY=34.5 StartZ=0 EndX=-49.19 EndY=31.5 EndZ=0
    g7: LineSegment StartX=-49.19 StartY=28.75 StartZ=0 EndX=-49.19 EndY=25.75 EndZ=0
    g8: LineSegment StartX=-49.19 StartY=23 StartZ=0 EndX=-49.19 EndY=20 EndZ=0
    g9: LineSegment StartX=-49.19 StartY=17.25 StartZ=0 EndX=-49.19 EndY=14.25 EndZ=0
    g10: LineSegment StartX=-49.19 StartY=11.5 StartZ=0 EndX=-49.19 EndY=8.5 EndZ=0
    g11: LineSegment StartX=-49.19 StartY=5.75 StartZ=0 EndX=-49.19 EndY=2.75 EndZ=0
    g12: ArcOfCircle CenterX=-1.5 CenterY=67.75 CenterZ=0 NormalX=0 NormalY=0 NormalZ=1 AngleXU=0 Radius=1.5 StartAngle=4.71239 EndAngle=7.85398
    g13: ArcOfCircle CenterX=-1.5 CenterY=62 CenterZ=0 NormalX=0 NormalY=0 NormalZ=1 AngleXU=0 Radius=1.5 StartAngle=4.71239 EndAngle=7.85398
    g14: ArcOfCircle CenterX=-1.5 CenterY=56.25 CenterZ=0 NormalX=0 NormalY=0 NormalZ=1 AngleXU=0 Radius=1.5 StartAngle=4.71239 EndAngle=7.85398
    g15: ArcOfCircle CenterX=-11.49 CenterY=50.5 CenterZ=0 NormalX=0 NormalY=0 NormalZ=1 AngleXU=0 Radius=1.5 StartAngle=4.71239 EndAngle=7.85398
    g16: ArcOfCircle CenterX=-16.28 CenterY=44.75 CenterZ=0 NormalX=0 NormalY=0 NormalZ=1 AngleXU=0 Radius=1.5 StartAngle=4.71239 EndAngle=7.85398
    g17: ArcOfCircle CenterX=-18.2337 CenterY=39 CenterZ=0 NormalX=0 NormalY=0 NormalZ=1 AngleXU=0 Radius=1.5 StartAngle=4.71485 EndAngle=7.85398
    g18: ArcOfCircle CenterX=-16.2837 CenterY=27.25 CenterZ=0 NormalX=0 NormalY=0 NormalZ=1 AngleXU=0 Radius=1.5 StartAngle=4.71485 EndAngle=7.85398
    g19: ArcOfCircle CenterX=-18.2337 CenterY=33 CenterZ=0 NormalX=0 NormalY=0 NormalZ=1 AngleXU=0 Radius=1.5 StartAngle=4.71485 EndAngle=7.85398
    g20: ArcOfCircle CenterX=-11.49 CenterY=21.5 CenterZ=0 NormalX=0 NormalY=0 NormalZ=1 AngleXU=0 Radius=1.5 StartAngle=4.71239 EndAngle=7.85398
    g21: ArcOfCircle CenterX=-1.5 CenterY=4.25 CenterZ=0 NormalX=0 NormalY=0 NormalZ=1 AngleXU=0 Radius=1.5 StartAngle=4.71239 EndAngle=7.85398
    g22: ArcOfCircle CenterX=-1.5 CenterY=10 CenterZ=0 NormalX=0 NormalY=0 NormalZ=1 AngleXU=0 Radius=1.5 StartAngle=4.71239 EndAngle=7.85398
    g23: ArcOfCircle CenterX=-1.5 CenterY=15.75 CenterZ=0 NormalX=0 NormalY=0 NormalZ=1 AngleXU=0 Radius=1.5 StartAngle=4.71239 EndAngle=7.85398
    g24: LineSegment StartX=-49.19 StartY=69.25 StartZ=0 EndX=-1.5 EndY=69.25 EndZ=0
    g25: LineSegment StartX=-49.19 StartY=66.25 StartZ=0 EndX=-1.5 EndY=66.25 EndZ=0
    g26: LineSegment StartX=-49.19 StartY=63.5 StartZ=0 EndX=-1.5 EndY=63.5 EndZ=0
    g27: LineSegment StartX=-49.19 StartY=60.5 StartZ=0 EndX=-1.5 EndY=60.5 EndZ=0
    g28: LineSegment StartX=-49.19 StartY=57.75 StartZ=0 EndX=-1.5 EndY=57.75 EndZ=0
    g29: LineSegment StartX=-49.19 StartY=54.75 StartZ=0 EndX=-1.5 EndY=54.75 EndZ=0
    g30: LineSegment StartX=-49.19 StartY=52 StartZ=0 EndX=-11.49 EndY=52 EndZ=0
    g31: LineSegment StartX=-49.19 StartY=49 StartZ=0 EndX=-11.49 EndY=49 EndZ=0
    g32: LineSegment StartX=-49.19 StartY=46.25 StartZ=0 EndX=-16.28 EndY=46.25 EndZ=0
    g33: LineSegment StartX=-49.19 StartY=43.25 StartZ=0 EndX=-16.28 EndY=43.25 EndZ=0
    g34: LineSegment StartX=-49.19 StartY=40.5 StartZ=0 EndX=-18.2337 EndY=40.5 EndZ=0
    g35: LineSegment StartX=-49.19 StartY=37.5 StartZ=0 EndX=-18.23 EndY=37.5 EndZ=0
    g36: LineSegment StartX=-49.19 StartY=34.5 StartZ=0 EndX=-18.2337 EndY=34.5 EndZ=0
    g37: LineSegment StartX=-49.19 StartY=31.5 StartZ=0 EndX=-18.23 EndY=31.5 EndZ=0
    g38: LineSegment StartX=-49.19 StartY=28.75 StartZ=0 EndX=-16.2837 EndY=28.75 EndZ=0
    g39: LineSegment StartX=-49.19 StartY=25.75 StartZ=0 EndX=-16.28 EndY=25.75 EndZ=0
    g40: LineSegment StartX=-49.19 StartY=23 StartZ=0 EndX=-11.49 EndY=23 EndZ=0
    g41: LineSegment StartX=-49.19 StartY=20 StartZ=0 EndX=-11.49 EndY=20 EndZ=0
    g42: LineSegment StartX=-49.19 StartY=17.25 StartZ=0 EndX=-1.5 EndY=17.25 EndZ=0
    g43: LineSegment StartX=-49.19 StartY=14.25 StartZ=0 EndX=-1.5 EndY=14.25 EndZ=0
    g44: LineSegment StartX=-49.19 StartY=11.5 StartZ=0 EndX=-1.5 EndY=11.5 EndZ=0
    g45: LineSegment StartX=-49.19 StartY=8.5 StartZ=0 EndX=-1.5 EndY=8.5 EndZ=0
    g46: LineSegment StartX=-49.19 StartY=5.75 StartZ=0 EndX=-1.5 EndY=5.75 EndZ=0
    g47: LineSegment StartX=-49.19 StartY=2.75 StartZ=0 EndX=-1.5 EndY=2.75 EndZ=0
  constraints (120):
    c: Vertical(g0)
    c: Distance(g0) = 3
    c: Block(g0)
    c: Vertical(g1)
    c: Distance(g1) = 3
    c: Vertical(g2)
    c: Equal(g0,g2) = 3
    c: Block(g2)
    c: Vertical(g3)
    c: Equal(g1,g3) = 3
    c: Vertical(g4)
    c: Equal(g0,g4) = 3
    c: Block(g4)
    c: Vertical(g5)
    c: Equal(g1,g5) = 3
    c: Vertical(g6)
    c: Equal(g0,g6) = 3
    c: Block(g6)
    c: Vertical(g7)
    c: Equal(g1,g7) = 3
    c: Vertical(g8)
    c: Equal(g0,g8) = 3
    c: Block(g8)
    c: Vertical(g9)
    c: Equal(g1,g9) = 3
    c: Vertical(g10)
    c: Equal(g0,g10) = 3
    c: Block(g10)
    c: Vertical(g11)
    c: Equal(g1,g11) = 3
    c: Block(g12)
    c: Block(g13)
    c: Block(g14)
    c: Block(g15)
    c: Block(g16)
    c: Block(g17)
    c: Block(g18)
    c: Block(g19)
    c: Block(g20)
    c: Block(g21)
    c: Block(g22)
    c: Block(g23)
    c: Block(g11)
    c: Block(g9)
    c: Block(g7)
    c: Block(g5)
    c: Block(g3)
    c: Block(g1)
    c: Coincident(g24,g0)
    c: Coincident(g24,g12)
    c: Horizontal(g24)
    c: Coincident(g25,g0)
    c: Coincident(g25,g12)
    c: Horizontal(g25)
    c: Coincident(g26,g1)
    c: Coincident(g26,g13)
    c: Horizontal(g26)
    c: Coincident(g27,g1)
    c: Coincident(g27,g13)
    c: Horizontal(g27)
    c: Coincident(g28,g2)
    c: Coincident(g28,g14)
    c: Horizontal(g28)
    c: Coincident(g29,g2)
    c: Coincident(g29,g14)
    c: Horizontal(g29)
    c: Coincident(g30,g3)
    c: Coincident(g30,g15)
    c: Horizontal(g30)
    c: Coincident(g31,g3)
    c: Coincident(g31,g15)
    c: Horizontal(g31)
    c: Coincident(g32,g4)
    c: Coincident(g32,g16)
    c: Horizontal(g32)
    c: Coincident(g33,g4)
    c: Coincident(g33,g16)
    c: Horizontal(g33)
    c: Coincident(g34,g5)
    c: Coincident(g34,g17)
    c: Horizontal(g34)
    c: Coincident(g35,g5)
    c: Coincident(g35,g17)
    c: Horizontal(g35)
    c: Coincident(g36,g6)
    c: Coincident(g36,g19)
    c: Horizontal(g36)
    c: Coincident(g37,g6)
    c: Coincident(g37,g19)
    c: Horizontal(g37)
    c: Coincident(g38,g7)
    c: Coincident(g38,g18)
    c: Horizontal(g38)
    c: Coincident(g39,g7)
    c: Coincident(g39,g18)
    c: Horizontal(g39)
    c: Coincident(g40,g8)
    c: Coincident(g40,g20)
    c: Horizontal(g40)
    c: Coincident(g41,g8)
    c: Coincident(g41,g20)
    c: Horizontal(g41)
    c: Coincident(g42,g9)
    c: Coincident(g42,g23)
    c: Horizontal(g42)
    c: Coincident(g43,g9)
    c: Coincident(g43,g23)
    c: Horizontal(g43)
    c: Coincident(g44,g10)
    c: Coincident(g44,g22)
    c: Horizontal(g44)
    c: Coincident(g45,g10)
    c: Coincident(g45,g22)
    c: Horizontal(g45)
    c: Coincident(g46,g11)
    c: Coincident(g46,g21)
    c: Horizontal(g46)
    c: Coincident(g47,g11)
    c: Coincident(g47,g21)
    c: Horizontal(g47)
FEATURE [Part::Extrusion] Extrude042
  Base = -> Sketch051
  Dir = (1,-2e-16,2e-16)
  DirMode = 2
  FaceMakerClass = Part::FaceMakerBullseye
  LengthFwd = 19
  LengthRev = 0
  Placement = pos=(-19,0,0) rot=(0,0,1;0rad)
  Solid = true
  Symmetric = false
FEATURE [Part::Fillet] Fillet035  label="removeToCreateVentalationHoles"
  Base = -> Extrude042
  Edges = <same value as first occurrence — deduplicated (x6 in doc)>
  Placement = pos=(7,0,0) rot=(0,0,1;0rad)
FEATURE [Part::Cut] Cut038  label="top017"
  Base = -> Cut033
  Tool = -> Fillet035
FEATURE [Sketcher::SketchObject] Sketch052  label="bottomSketch001"
  FullyConstrained = true
  sketch-geometry (45):
    g0: LineSegment StartX=6.29999 StartY=8 StartZ=0 EndX=3.29999 EndY=8 EndZ=0
    g1: LineSegment StartX=3.29999 StartY=8 StartZ=0 EndX=3.29999 EndY=-6.03275e-07 EndZ=0
    g2: ArcOfCircle CenterX=8.29999 CenterY=5 CenterZ=0 NormalX=0 NormalY=0 NormalZ=1 AngleXU=0 Radius=2 StartAngle=3.14159 EndAngle=4.71239
    g3: LineSegment StartX=6.29999 StartY=8 StartZ=0 EndX=6.29999 EndY=5 EndZ=0
    g4: ArcOfCircle CenterX=105 CenterY=19 CenterZ=0 NormalX=0 NormalY=0 NormalZ=1 AngleXU=0 Radius=12.7 StartAngle=4.71239 EndAngle=5.94289
    g5-g11: Circle x7 (B-spline internal-alignment scaffolding for g12; pole/knot coordinates omitted)
    g12: BSplineCurve PolesCount=7 KnotsCount=5 Degree=3 IsPeriodic=0
    g13-g17: GeomPoint x5 (B-spline internal-alignment scaffolding for g12; pole/knot coordinates omitted)
    g18: ArcOfCircle CenterX=105 CenterY=19 CenterZ=0 NormalX=0 NormalY=0 NormalZ=1 AngleXU=0 Radius=15.7 StartAngle=5.81226 EndAngle=6.28319
    g19: BSplineCurve PolesCount=5 KnotsCount=3 Degree=3 IsPeriodic=0
    g20: LineSegment StartX=8.29999 StartY=3 StartZ=0 EndX=101.7 EndY=3 EndZ=0
    g21: LineSegment StartX=3.29999 StartY=-6.03275e-07 StartZ=0 EndX=105 EndY=-6.03275e-07 EndZ=0
    g22: LineSegment StartX=120.974 StartY=8.71251 StartZ=0 EndX=122.332 EndY=7.83778 EndZ=0
    g23: LineSegment StartX=105 StartY=-6.03274e-07 StartZ=0 EndX=113 EndY=-6.03274e-07 EndZ=0
    g24: ArcOfCircle CenterX=105 CenterY=19 CenterZ=0 NormalX=0 NormalY=0 NormalZ=1 AngleXU=0 Radius=20.6155 StartAngle=5.11091 EndAngle=5.71103
    g25: ArcOfCircle CenterX=117.7 CenterY=19 CenterZ=0 NormalX=0 NormalY=0 NormalZ=1 AngleXU=0 Radius=3 StartAngle=1.2e-15 EndAngle=2.10468
    g26: Circle CenterX=116.345 CenterY=16.3232 CenterZ=0 NormalX=0 NormalY=0 NormalZ=1 AngleXU=0 Radius=1
    g27: Circle CenterX=117.24 CenterY=15.7584 CenterZ=0 NormalX=0 NormalY=0 NormalZ=1 AngleXU=0 Radius=1
    g28: Circle CenterX=116.972 CenterY=14.7612 CenterZ=0 NormalX=0 NormalY=0 NormalZ=1 AngleXU=0 Radius=1
    g29: BSplineCurve PolesCount=3 KnotsCount=2 Degree=2 IsPeriodic=0
    g30: GeomPoint X=116.345 Y=16.3232 Z=0
    g31: GeomPoint X=116.972 Y=14.7612 Z=0
    g32: Circle CenterX=115.828 CenterY=17.157 CenterZ=0 NormalX=0 NormalY=0 NormalZ=1 AngleXU=0 Radius=1
    g33: Circle CenterX=115.841 CenterY=16.639 CenterZ=0 NormalX=0 NormalY=0 NormalZ=1 AngleXU=0 Radius=1
    g34: Circle CenterX=116.345 CenterY=16.3232 CenterZ=0 NormalX=0 NormalY=0 NormalZ=1 AngleXU=0 Radius=1
    g35: BSplineCurve PolesCount=3 KnotsCount=2 Degree=2 IsPeriodic=0
    g36: GeomPoint X=115.828 Y=17.157 Z=0
    g37: GeomPoint X=116.345 Y=16.3232 Z=0
    g38: LineSegment StartX=115.828 StartY=17.157 StartZ=0 EndX=115.828 EndY=20.8307 EndZ=0
    g39: Circle CenterX=115.828 CenterY=20.8307 CenterZ=0 NormalX=0 NormalY=0 NormalZ=1 AngleXU=0 Radius=1
    g40: Circle CenterX=115.831 CenterY=21.3396 CenterZ=0 NormalX=0 NormalY=0 NormalZ=1 AngleXU=0 Radius=1
    g41: Circle CenterX=116.173 CenterY=21.5825 CenterZ=0 NormalX=0 NormalY=0 NormalZ=1 AngleXU=0 Radius=1
    g42: BSplineCurve PolesCount=3 KnotsCount=2 Degree=2 IsPeriodic=0
    g43: GeomPoint X=115.828 Y=20.8307 Z=0
    g44: GeomPoint X=116.173 Y=21.5825 Z=0
  constraints (70):
    c: Horizontal(g0)
    c: Distance(g0) = 3
    c: Coincident(g1,g0)
    c: Vertical(g1)
    c: Block(g2)
    c: Block(g0)
    c: Coincident(g3,g0)
    c: Coincident(g3,g2)
    c: Vertical(g3)
    c: Block(g1)
    c: Block(g4)
    c: Coincident(g19,g4)
    c: Block(g19)
    c: Equal(g5, g6-g11) x6
    c: InternalAlignment(g5-g11 -> g12) x7
    c: InternalAlignment(g13-g17 -> g12) x5
    c: Block(g12)
    c: Coincident(g18,g12)
    c: Block(g18)
    c: Coincident(g20,g2)
    c: Coincident(g20,g19)
    c: Horizontal(g20)
    c: Distance(g20) = 93.4
    c: Coincident(g21,g1)
    c: Horizontal(g21)
    c: Distance(g21) = 101.7
    c: Horizontal(g23)
    c: Distance(g23) = 8
    c: Coincident(g24,g23)
    c: Block(g23)
    c: Coincident(g22,g24)
    c: Block(g24)
    c: Block(g22)
    c: Distance(g22) = 1.61553
    c: Coincident(g25,g18)
    c: Block(g25)
    c: Weight(g26) = 1
    c: Equal(g26,g27)
    c: Equal(g26,g28)
    c: Coincident(g29,g4)
    c: InternalAlignment(g26,g29)
    c: InternalAlignment(g27,g29)
    c: InternalAlignment(g28,g29)
    c: InternalAlignment(g30,g29)
    c: InternalAlignment(g31,g29)
    c: Block(g29)
    c: Weight(g32) = 1
    c: Equal(g32,g33)
    c: Equal(g32,g34)
    c: Coincident(g35,g29)
    c: InternalAlignment(g32,g35)
    c: InternalAlignment(g33,g35)
    c: InternalAlignment(g34,g35)
    c: InternalAlignment(g36,g35)
    c: InternalAlignment(g37,g35)
    c: Block(g35)
    c: Coincident(g38,g35)
    c: Vertical(g38)
    c: Block(g38)
    c: Coincident(g42,g38)
    c: Weight(g39) = 1
    c: Equal(g39,g40)
    c: Equal(g39,g41)
    c: Coincident(g42,g25)
    c: InternalAlignment(g39,g42)
    c: InternalAlignment(g40,g42)
    c: InternalAlignment(g41,g42)
    c: InternalAlignment(g43,g42)
    c: InternalAlignment(g44,g42)
    c: Block(g42)
FEATURE [Part::Extrusion] Extrude043  label="bottom010"
  Base = -> Sketch052
  Dir = (0,0,1)
  DirMode = 2
  FaceMakerClass = Part::FaceMakerBullseye
  LengthFwd = 71.4
  LengthRev = 0
  Placement = pos=(0,0,0.3) rot=(0,0,1;0rad)
  Solid = true
  Symmetric = false
FEATURE [Sketcher::SketchObject] Sketch053  label="topSketch013"
  FullyConstrained = true
  sketch-geometry (22):
    g0: LineSegment StartX=5.21097e-06 StartY=3 StartZ=0 EndX=5.21097e-06 EndY=19 EndZ=0
    g1: ArcOfCircle CenterX=19 CenterY=19 CenterZ=0 NormalX=0 NormalY=0 NormalZ=1 AngleXU=0 Radius=19 StartAngle=1.5708 EndAngle=3.14159
    g2: ArcOfCircle CenterX=19 CenterY=19 CenterZ=0 NormalX=0 NormalY=0 NormalZ=1 AngleXU=0 Radius=16 StartAngle=1.5708 EndAngle=3.14159
    g3: LineSegment StartX=114 StartY=35 StartZ=0 EndX=19 EndY=35 EndZ=0
    g4: LineSegment StartX=5.21097e-06 StartY=3 StartZ=0 EndX=5.21097e-06 EndY=0 EndZ=0
    g5: LineSegment StartX=3 StartY=0 StartZ=0 EndX=5.21097e-06 EndY=0 EndZ=0
    g6: LineSegment StartX=3 StartY=19 StartZ=0 EndX=3 EndY=0 EndZ=0
    g7: LineSegment StartX=19 StartY=38 StartZ=0 EndX=124 EndY=38 EndZ=0
    g8: Circle CenterX=119 CenterY=35 CenterZ=0 NormalX=0 NormalY=0 NormalZ=1 AngleXU=0 Radius=1
    g9: Circle CenterX=121 CenterY=35 CenterZ=0 NormalX=0 NormalY=0 NormalZ=1 AngleXU=0 Radius=1
    g10: Circle CenterX=121 CenterY=33 CenterZ=0 NormalX=0 NormalY=0 NormalZ=1 AngleXU=0 Radius=1
    g11: BSplineCurve PolesCount=3 KnotsCount=2 Degree=2 IsPeriodic=0
    g12: GeomPoint X=119 Y=35 Z=0
    g13: GeomPoint X=121 Y=33 Z=0
    g14: LineSegment StartX=119 StartY=35 StartZ=0 EndX=114 EndY=35 EndZ=0
    g15: ArcOfCircle CenterX=105 CenterY=19 CenterZ=0 NormalX=0 NormalY=0 NormalZ=1 AngleXU=0 Radius=16 StartAngle=5.60905 EndAngle=6.28319
    g16: LineSegment StartX=121 StartY=33 StartZ=0 EndX=121 EndY=19 EndZ=0
    g17: LineSegment StartX=117.5 StartY=9.01251 StartZ=0 EndX=121.163 EndY=9.0125 EndZ=0
    g18: ArcOfCircle CenterX=105 CenterY=19 CenterZ=0 NormalX=0 NormalY=0 NormalZ=1 AngleXU=0 Radius=20.6155 StartAngle=5.7297 EndAngle=6.28319
    g19: LineSegment StartX=121.163 StartY=9.0125 StartZ=0 EndX=122.538 EndY=8.16329 EndZ=0
    g20: LineSegment StartX=124 StartY=38 StartZ=0 EndX=125.616 EndY=38 EndZ=0
    g21: LineSegment StartX=125.616 StartY=19 StartZ=0 EndX=125.616 EndY=38 EndZ=0
  constraints (50):
    c: Vertical(g0)
    c: Block(g0)
    c: Coincident(g1,g0)
    c: Block(g1)
    c: Coincident(g2,g1)
    c: Block(g2)
    c: Coincident(g3,g2)
    c: Horizontal(g3)
    c: Tangent(g3,g2)
    c: Coincident(g4,g0)
    c: Distance(g4) = 3
    c: Vertical(g4)
    c: Coincident(g5,g4)
    c: Horizontal(g5)
    c: Coincident(g6,g2)
    c: Coincident(g6,g5)
    c: Vertical(g6)
    c: Horizontal(g7)
    c: Distance(g7) = 105
    c: Coincident(g7,g1)
    c: Block(g3)
    c: Weight(g8) = 1
    c: Equal(g8,g9)
    c: Equal(g8,g10)
    c: InternalAlignment(g8,g11)
    c: InternalAlignment(g9,g11)
    c: InternalAlignment(g10,g11)
    c: InternalAlignment(g12,g11)
    c: InternalAlignment(g13,g11)
    c: Block(g11)
    c: Coincident(g14,g11)
    c: Coincident(g14,g3)
    c: Horizontal(g14)
    c: Block(g15)
    c: Coincident(g16,g11)
    c: Coincident(g16,g15)
    c: Vertical(g16)
    c: Distance(g16) = 14
    c: Coincident(g17,g15)
    c: Block(g18)
    c: Coincident(g19,g18)
    c: Coincident(g20,g7)
    c: Horizontal(g20)
    c: Vertical(g21)
    c: Coincident(g20,g21)
    c: Block(g20)
    c: Block(g21)
    c: Block(g19)
    c: Block(g17)
    c: Distance(g20) = 1.61553
FEATURE [Part::Extrusion] Extrude044
  Base = -> Sketch053
  Dir = (0,0,1)
  DirMode = 2
  FaceMakerClass = Part::FaceMakerBullseye
  LengthFwd = 72
  LengthRev = 0
  Solid = true
  Symmetric = false
FEATURE [Part::Fillet] Fillet036  label="top018"
  Base = -> Extrude044
  Edges = 1 edges r=2: [Edge41]
FEATURE [Sketcher::SketchObject] Sketch054
  FullyConstrained = false
  Placement = pos=(0,0,0) rot=(1,0,0;1.5708rad)
  sketch-geometry (24):
    g0: ArcOfCircle CenterX=-4 CenterY=-10.5 CenterZ=0 NormalX=0 NormalY=0 NormalZ=1 AngleXU=0 Radius=1.5 StartAngle=6e-16 EndAngle=3.14159
    g1: ArcOfCircle CenterX=-34.2 CenterY=-10.5 CenterZ=0 NormalX=0 NormalY=0 NormalZ=1 AngleXU=0 Radius=1.5 StartAngle=0 EndAngle=3.14159
    g2: ArcOfCircle CenterX=-34.2 CenterY=-27.7 CenterZ=0 NormalX=0 NormalY=0 NormalZ=1 AngleXU=0 Radius=1.5 StartAngle=3.14159 EndAngle=6.28319
    g3: ArcOfCircle CenterX=-4 CenterY=-27.7 CenterZ=0 NormalX=0 NormalY=0 NormalZ=1 AngleXU=0 Radius=1.5 StartAngle=3.1416 EndAngle=6.28319
    g4: ArcOfCircle CenterX=-10 CenterY=-4.3 CenterZ=0 NormalX=0 NormalY=0 NormalZ=1 AngleXU=0 Radius=1.5 StartAngle=2e-16 EndAngle=3.14159
    g5: ArcOfCircle CenterX=-16.1 CenterY=-1.8 CenterZ=0 NormalX=0 NormalY=0 NormalZ=1 AngleXU=0 Radius=1.5 StartAngle=5e-16 EndAngle=3.14159
    g6: ArcOfCircle CenterX=-22.1 CenterY=-1.8 CenterZ=0 NormalX=0 NormalY=0 NormalZ=1 AngleXU=0 Radius=1.5 StartAngle=5e-16 EndAngle=3.14159
    g7: ArcOfCircle CenterX=-28.2 CenterY=-4.3 CenterZ=0 NormalX=0 NormalY=0 NormalZ=1 AngleXU=0 Radius=1.5 StartAngle=2e-16 EndAngle=3.14159
    g8: ArcOfCircle CenterX=-10 CenterY=-33.9 CenterZ=0 NormalX=0 NormalY=0 NormalZ=1 AngleXU=0 Radius=1.5 StartAngle=3.14159 EndAngle=6.28319
    g9: ArcOfCircle CenterX=-16.1 CenterY=-36.4 CenterZ=0 NormalX=0 NormalY=0 NormalZ=1 AngleXU=0 Radius=1.5 StartAngle=3.14159 EndAngle=6.28319
    g10: ArcOfCircle CenterX=-22.1 CenterY=-36.4 CenterZ=0 NormalX=0 NormalY=0 NormalZ=1 AngleXU=0 Radius=1.5 StartAngle=3.14159 EndAngle=6.28319
    g11: ArcOfCircle CenterX=-28.2 CenterY=-33.9 CenterZ=0 NormalX=0 NormalY=0 NormalZ=1 AngleXU=0 Radius=1.5 StartAngle=3.14159 EndAngle=6.28319
    g12: LineSegment StartX=-35.7 StartY=-10.5 StartZ=0 EndX=-35.7 EndY=-27.7 EndZ=0
    g13: LineSegment StartX=-32.7 StartY=-10.5 StartZ=0 EndX=-32.7 EndY=-27.7 EndZ=0
    g14: LineSegment StartX=-29.7 StartY=-33.9 StartZ=0 EndX=-29.7 EndY=-4.3 EndZ=0
    g15: LineSegment StartX=-26.7 StartY=-33.9 StartZ=0 EndX=-26.7 EndY=-4.3 EndZ=0
    g16: LineSegment StartX=-2.5 StartY=-10.5 StartZ=0 EndX=-2.5 EndY=-27.7 EndZ=0
    g17: LineSegment StartX=-8.5 StartY=-4.3 StartZ=0 EndX=-8.5 EndY=-33.9 EndZ=0
    g18: LineSegment StartX=-5.5 StartY=-10.5 StartZ=0 EndX=-5.5 EndY=-27.7 EndZ=0
    g19: LineSegment StartX=-11.5 StartY=-4.3 StartZ=0 EndX=-11.5 EndY=-33.9 EndZ=0
    g20: LineSegment StartX=-14.6 StartY=-1.8 StartZ=0 EndX=-14.6 EndY=-36.4 EndZ=0
    g21: LineSegment StartX=-17.6 StartY=-1.8 StartZ=0 EndX=-17.6 EndY=-36.4 EndZ=0
    g22: LineSegment StartX=-20.6 StartY=-36.4 StartZ=0 EndX=-20.6 EndY=-1.8 EndZ=0
    g23: LineSegment StartX=-23.6 StartY=-1.8 StartZ=0 EndX=-23.6 EndY=-36.4 EndZ=0
  constraints (48):
    c: Block(g0)
    c: Block(g1)
    c: Block(g2)
    c: Block(g3)
    c: Block(g4)
    c: Block(g5)
    c: Block(g6)
    c: Block(g7)
    c: Block(g8)
    c: Block(g9)
    c: Block(g10)
    c: Block(g11)
    c: Coincident(g12,g1)
    c: Coincident(g12,g2)
    c: Vertical(g12)
    c: Coincident(g13,g1)
    c: Coincident(g13,g2)
    c: Vertical(g13)
    c: Coincident(g14,g11)
    c: Coincident(g14,g7)
    c: Vertical(g14)
    c: Coincident(g15,g11)
    c: Coincident(g15,g7)
    c: Vertical(g15)
    c: Coincident(g16,g0)
    c: Coincident(g16,g3)
    c: Vertical(g16)
    c: Coincident(g17,g4)
    c: Coincident(g17,g8)
    c: Vertical(g17)
    c: Coincident(g18,g0)
    c: Coincident(g18,g3)
    c: Vertical(g18)
    c: Coincident(g19,g4)
    c: Coincident(g19,g8)
    c: Vertical(g19)
    c: Coincident(g20,g5)
    c: Coincident(g20,g9)
    c: Vertical(g20)
    c: Coincident(g21,g5)
    c: Coincident(g21,g9)
    c: Vertical(g21)
    c: Coincident(g22,g10)
    c: Coincident(g22,g6)
    c: Vertical(g22)
    c: Coincident(g23,g6)
    c: Coincident(g23,g10)
    c: Vertical(g23)
FEATURE [Part::Extrusion] Extrude045  label="removeToCreateFanGrillHoles003"
  Base = -> Sketch054
  Dir = (0,-1,6e-16)
  DirMode = 2
  FaceMakerClass = Part::FaceMakerBullseye
  LengthFwd = 10
  LengthRev = 0
  Placement = pos=(65.4,44,54.82) rot=(0,0,1;0rad)
  Solid = true
  Symmetric = false
FEATURE [Part::Feature] Face105 .. Face108  x4 (patterned run collapsed; names and placements below)
  shape: bbox 3.5 x 17.8 x 2e-07 mm, 1 faces, 0 solids (baked)
FEATURE [Part::Revolution] Revolve113  label="removeToCreateScrewAndThreadedInsertHole041"
  Angle = 360
  Axis = (0,1,0)
  Base = (0,0,0)
  FaceMakerClass = Part::FaceMakerBullseye
  Placement = pos=(62.3,30.3,19.7) rot=(0,0,1;0rad)
  Solid = false
  Source = -> Face105
  Symmetric = false
FEATURE [Part::Revolution] Revolve114  label="removeToCreateScrewAndThreadedInsertHole042"
  Angle = 360
  Axis = (0,1,0)
  Base = (0,0,0)
  FaceMakerClass = Part::FaceMakerBullseye
  Placement = pos=(62.3,30.3,51.7) rot=(0,0,1;0rad)
  Solid = false
  Source = -> Face106
  Symmetric = false
FEATURE [Part::Revolution] Revolve115  label="removeToCreateScrewAndThreadedInsertHole043"
  Angle = 360
  Axis = (0,1,0)
  Base = (0,0,0)
  FaceMakerClass = Part::FaceMakerBullseye
  Placement = pos=(30.3,30.3,19.7) rot=(0,0,1;0rad)
  Solid = false
  Source = -> Face107
  Symmetric = false
FEATURE [Part::Revolution] Revolve116  label="removeToCreateScrewAndThreadedInsertHole044"
  Angle = 360
  Axis = (0,1,0)
  Base = (0,0,0)
  FaceMakerClass = Part::FaceMakerBullseye
  Placement = pos=(30.3,30.3,51.7) rot=(0,0,1;0rad)
  Solid = false
  Source = -> Face108
  Symmetric = false
FEATURE [Part::MultiFuse] Fusion083  label="createThreadedInsertHolesForFan004"
  Shapes = -> [Revolve113,Revolve114,Revolve115,Revolve116]
FEATURE [Part::Box] Box024  label="removeToCreteHoleForPlugHousing026"
  AttacherType = Attacher::AttachEngine3D
  Height = 28.6
  Length = 10
  Placement = pos=(-2,0,21.7) rot=(0,0,1;0rad)
  Width = 19
FEATURE [Part::Cylinder] Cylinder038  label="removeToCreteHoleForPlugHousing027"
  Angle = 360
  AttacherType = Attacher::AttachEngine3D
  Height = 20
  Placement = pos=(-2,19,36) rot=(0,1,0;1.5708rad)
  Radius = 14.3
FEATURE [Part::MultiFuse] Fusion084  label="removeToCreteHoleForPlugHousing028"
  Shapes = -> [Box024,Cylinder038]
FEATURE [Part::Cylinder] Cylinder039
  Angle = 360
  AttacherType = Attacher::AttachEngine3D
  Height = 20
  Placement = pos=(0,0,36.15) rot=(0,0,1;0rad)
  Radius = 14.3
FEATURE [Part::Cylinder] Cylinder040
  Angle = 360
  AttacherType = Attacher::AttachEngine3D
  Height = 10
  Placement = pos=(0,0,36.15) rot=(0,0,1;0rad)
  Radius = 4
FEATURE [Part::Box] Box025  label="removeToCreteHoleForPlugHousing030"
  AttacherType = Attacher::AttachEngine3D
  Height = 28.6
  Length = 20
  Placement = pos=(106.15,0,21.7) rot=(0,0,1;0rad)
  Width = 19
FEATURE [Part::MultiFuse] Fusion086  label="removeToCreteHoleForPlugHousing031"
  Placement = pos=(70,19,36) rot=(0,1,0;1.5708rad)
  Shapes = -> [Cylinder039,Cylinder040]
FEATURE [Part::MultiFuse] Fusion085  label="removeToCreteHoleForPlugHousing029"
  Shapes = -> [Box025,Fusion086]
FEATURE [Sketcher::SketchObject] Sketch055
  FullyConstrained = true
  Placement = pos=(117,19,0) rot=(0.57735,0.57735,0.57735;2.0944rad)
  sketch-geometry (48):
    g0: LineSegment StartX=-49.19 StartY=69.25 StartZ=0 EndX=-49.19 EndY=66.25 EndZ=0
    g1: LineSegment StartX=-49.19 StartY=63.5 StartZ=0 EndX=-49.19 EndY=60.5 EndZ=0
    g2: LineSegment StartX=-49.19 StartY=57.75 StartZ=0 EndX=-49.19 EndY=54.75 EndZ=0
    g3: LineSegment StartX=-49.19 StartY=52 StartZ=0 EndX=-49.19 EndY=49 EndZ=0
    g4: LineSegment StartX=-49.19 StartY=46.25 StartZ=0 EndX=-49.19 EndY=43.25 EndZ=0
    g5: LineSegment StartX=-49.19 StartY=40.5 StartZ=0 EndX=-49.19 EndY=37.5 EndZ=0
    g6: LineSegment StartX=-49.19 StartY=34.5 StartZ=0 EndX=-49.19 EndY=31.5 EndZ=0
    g7: LineSegment StartX=-49.19 StartY=28.75 StartZ=0 EndX=-49.19 EndY=25.75 EndZ=0
    g8: LineSegment StartX=-49.19 StartY=23 StartZ=0 EndX=-49.19 EndY=20 EndZ=0
    g9: LineSegment StartX=-49.19 StartY=17.25 StartZ=0 EndX=-49.19 EndY=14.25 EndZ=0
    g10: LineSegment StartX=-49.19 StartY=11.5 StartZ=0 EndX=-49.19 EndY=8.5 EndZ=0
    g11: LineSegment StartX=-49.19 StartY=5.75 StartZ=0 EndX=-49.19 EndY=2.75 EndZ=0
    g12: ArcOfCircle CenterX=-1.5 CenterY=67.75 CenterZ=0 NormalX=0 NormalY=0 NormalZ=1 AngleXU=0 Radius=1.5 StartAngle=4.71239 EndAngle=7.85398
    g13: ArcOfCircle CenterX=-1.5 CenterY=62 CenterZ=0 NormalX=0 NormalY=0 NormalZ=1 AngleXU=0 Radius=1.5 StartAngle=4.71239 EndAngle=7.85398
    g14: ArcOfCircle CenterX=-1.5 CenterY=56.25 CenterZ=0 NormalX=0 NormalY=0 NormalZ=1 AngleXU=0 Radius=1.5 StartAngle=4.71239 EndAngle=7.85398
    g15: ArcOfCircle CenterX=-11.49 CenterY=50.5 CenterZ=0 NormalX=0 NormalY=0 NormalZ=1 AngleXU=0 Radius=1.5 StartAngle=4.71239 EndAngle=7.85398
    g16: ArcOfCircle CenterX=-16.28 CenterY=44.75 CenterZ=0 NormalX=0 NormalY=0 NormalZ=1 AngleXU=0 Radius=1.5 StartAngle=4.71239 EndAngle=7.85398
    g17: ArcOfCircle CenterX=-18.2337 CenterY=39 CenterZ=0 NormalX=0 NormalY=0 NormalZ=1 AngleXU=0 Radius=1.5 StartAngle=4.71485 EndAngle=7.85398
    g18: ArcOfCircle CenterX=-16.2837 CenterY=27.25 CenterZ=0 NormalX=0 NormalY=0 NormalZ=1 AngleXU=0 Radius=1.5 StartAngle=4.71485 EndAngle=7.85398
    g19: ArcOfCircle CenterX=-18.2337 CenterY=33 CenterZ=0 NormalX=0 NormalY=0 NormalZ=1 AngleXU=0 Radius=1.5 StartAngle=4.71485 EndAngle=7.85398
    g20: ArcOfCircle CenterX=-11.49 CenterY=21.5 CenterZ=0 NormalX=0 NormalY=0 NormalZ=1 AngleXU=0 Radius=1.5 StartAngle=4.71239 EndAngle=7.85398
    g21: ArcOfCircle CenterX=-1.5 CenterY=4.25 CenterZ=0 NormalX=0 NormalY=0 NormalZ=1 AngleXU=0 Radius=1.5 StartAngle=4.71239 EndAngle=7.85398
    g22: ArcOfCircle CenterX=-1.5 CenterY=10 CenterZ=0 NormalX=0 NormalY=0 NormalZ=1 AngleXU=0 Radius=1.5 StartAngle=4.71239 EndAngle=7.85398
    g23: ArcOfCircle CenterX=-1.5 CenterY=15.75 CenterZ=0 NormalX=0 NormalY=0 NormalZ=1 AngleXU=0 Radius=1.5 StartAngle=4.71239 EndAngle=7.85398
    g24: LineSegment StartX=-49.19 StartY=69.25 StartZ=0 EndX=-1.5 EndY=69.25 EndZ=0
    g25: LineSegment StartX=-49.19 StartY=66.25 StartZ=0 EndX=-1.5 EndY=66.25 EndZ=0
    g26: LineSegment StartX=-49.19 StartY=63.5 StartZ=0 EndX=-1.5 EndY=63.5 EndZ=0
    g27: LineSegment StartX=-49.19 StartY=60.5 StartZ=0 EndX=-1.5 EndY=60.5 EndZ=0
    g28: LineSegment StartX=-49.19 StartY=57.75 StartZ=0 EndX=-1.5 EndY=57.75 EndZ=0
    g29: LineSegment StartX=-49.19 StartY=54.75 StartZ=0 EndX=-1.5 EndY=54.75 EndZ=0
    g30: LineSegment StartX=-49.19 StartY=52 StartZ=0 EndX=-11.49 EndY=52 EndZ=0
    g31: LineSegment StartX=-49.19 StartY=49 StartZ=0 EndX=-11.49 EndY=49 EndZ=0
    g32: LineSegment StartX=-49.19 StartY=46.25 StartZ=0 EndX=-16.28 EndY=46.25 EndZ=0
    g33: LineSegment StartX=-49.19 StartY=43.25 StartZ=0 EndX=-16.28 EndY=43.25 EndZ=0
    g34: LineSegment StartX=-49.19 StartY=40.5 StartZ=0 EndX=-18.2337 EndY=40.5 EndZ=0
    g35: LineSegment StartX=-49.19 StartY=37.5 StartZ=0 EndX=-18.23 EndY=37.5 EndZ=0
    g36: LineSegment StartX=-49.19 StartY=34.5 StartZ=0 EndX=-18.2337 EndY=34.5 EndZ=0
    g37: LineSegment StartX=-49.19 StartY=31.5 StartZ=0 EndX=-18.23 EndY=31.5 EndZ=0
    g38: LineSegment StartX=-49.19 StartY=28.75 StartZ=0 EndX=-16.2837 EndY=28.75 EndZ=0
    g39: LineSegment StartX=-49.19 StartY=25.75 StartZ=0 EndX=-16.28 EndY=25.75 EndZ=0
    g40: LineSegment StartX=-49.19 StartY=23 StartZ=0 EndX=-11.49 EndY=23 EndZ=0
    g41: LineSegment StartX=-49.19 StartY=20 StartZ=0 EndX=-11.49 EndY=20 EndZ=0
    g42: LineSegment StartX=-49.19 StartY=17.25 StartZ=0 EndX=-1.5 EndY=17.25 EndZ=0
    g43: LineSegment StartX=-49.19 StartY=14.25 StartZ=0 EndX=-1.5 EndY=14.25 EndZ=0
    g44: LineSegment StartX=-49.19 StartY=11.5 StartZ=0 EndX=-1.5 EndY=11.5 EndZ=0
    g45: LineSegment StartX=-49.19 StartY=8.5 StartZ=0 EndX=-1.5 EndY=8.5 EndZ=0
    g46: LineSegment StartX=-49.19 StartY=5.75 StartZ=0 EndX=-1.5 EndY=5.75 EndZ=0
    g47: LineSegment StartX=-49.19 StartY=2.75 StartZ=0 EndX=-1.5 EndY=2.75 EndZ=0
  constraints (120):
    c: Vertical(g0)
    c: Distance(g0) = 3
    c: Block(g0)
    c: Vertical(g1)
    c: Distance(g1) = 3
    c: Vertical(g2)
    c: Equal(g0,g2) = 3
    c: Block(g2)
    c: Vertical(g3)
    c: Equal(g1,g3) = 3
    c: Vertical(g4)
    c: Equal(g0,g4) = 3
    c: Block(g4)
    c: Vertical(g5)
    c: Equal(g1,g5) = 3
    c: Vertical(g6)
    c: Equal(g0,g6) = 3
    c: Block(g6)
    c: Vertical(g7)
    c: Equal(g1,g7) = 3
    c: Vertical(g8)
    c: Equal(g0,g8) = 3
    c: Block(g8)
    c: Vertical(g9)
    c: Equal(g1,g9) = 3
    c: Vertical(g10)
    c: Equal(g0,g10) = 3
    c: Block(g10)
    c: Vertical(g11)
    c: Equal(g1,g11) = 3
    c: Block(g12)
    c: Block(g13)
    c: Block(g14)
    c: Block(g15)
    c: Block(g16)
    c: Block(g17)
    c: Block(g18)
    c: Block(g19)
    c: Block(g20)
    c: Block(g21)
    c: Block(g22)
    c: Block(g23)
    c: Block(g11)
    c: Block(g9)
    c: Block(g7)
    c: Block(g5)
    c: Block(g3)
    c: Block(g1)
    c: Coincident(g24,g0)
    c: Coincident(g24,g12)
    c: Horizontal(g24)
    c: Coincident(g25,g0)
    c: Coincident(g25,g12)
    c: Horizontal(g25)
    c: Coincident(g26,g1)
    c: Coincident(g26,g13)
    c: Horizontal(g26)
    c: Coincident(g27,g1)
    c: Coincident(g27,g13)
    c: Horizontal(g27)
    c: Coincident(g28,g2)
    c: Coincident(g28,g14)
    c: Horizontal(g28)
    c: Coincident(g29,g2)
    c: Coincident(g29,g14)
    c: Horizontal(g29)
    c: Coincident(g30,g3)
    c: Coincident(g30,g15)
    c: Horizontal(g30)
    c: Coincident(g31,g3)
    c: Coincident(g31,g15)
    c: Horizontal(g31)
    c: Coincident(g32,g4)
    c: Coincident(g32,g16)
    c: Horizontal(g32)
    c: Coincident(g33,g4)
    c: Coincident(g33,g16)
    c: Horizontal(g33)
    c: Coincident(g34,g5)
    c: Coincident(g34,g17)
    c: Horizontal(g34)
    c: Coincident(g35,g5)
    c: Coincident(g35,g17)
    c: Horizontal(g35)
    c: Coincident(g36,g6)
    c: Coincident(g36,g19)
    c: Horizontal(g36)
    c: Coincident(g37,g6)
    c: Coincident(g37,g19)
    c: Horizontal(g37)
    c: Coincident(g38,g7)
    c: Coincident(g38,g18)
    c: Horizontal(g38)
    c: Coincident(g39,g7)
    c: Coincident(g39,g18)
    c: Horizontal(g39)
    c: Coincident(g40,g8)
    c: Coincident(g40,g20)
    c: Horizontal(g40)
    c: Coincident(g41,g8)
    c: Coincident(g41,g20)
    c: Horizontal(g41)
    c: Coincident(g42,g9)
    c: Coincident(g42,g23)
    c: Horizontal(g42)
    c: Coincident(g43,g9)
    c: Coincident(g43,g23)
    c: Horizontal(g43)
    c: Coincident(g44,g10)
    c: Coincident(g44,g22)
    c: Horizontal(g44)
    c: Coincident(g45,g10)
    c: Coincident(g45,g22)
    c: Horizontal(g45)
    c: Coincident(g46,g11)
    c: Coincident(g46,g21)
    c: Horizontal(g46)
    c: Coincident(g47,g11)
    c: Coincident(g47,g21)
    c: Horizontal(g47)
FEATURE [Part::Extrusion] Extrude046
  Base = -> Sketch055
  Dir = (1,0,0)
  DirMode = 2
  FaceMakerClass = Part::FaceMakerBullseye
  LengthFwd = 23
  LengthRev = 0
  Placement = pos=(-19,0,0) rot=(0,0,1;0rad)
  Solid = true
  Symmetric = false
FEATURE [Part::Fillet] Fillet038  label="removeToCreateVentalationHoles001"
  Base = -> Extrude046
  Edges = <same value as first occurrence — deduplicated (x6 in doc)>
  Placement = pos=(7,0,0) rot=(0,0,1;0rad)
FEATURE [Sketcher::SketchObject] Sketch056  label="topSketch014"
  FullyConstrained = true
  sketch-geometry (22):
    g0: LineSegment StartX=5.21097e-06 StartY=3 StartZ=0 EndX=5.21097e-06 EndY=19 EndZ=0
    g1: ArcOfCircle CenterX=19 CenterY=19 CenterZ=0 NormalX=0 NormalY=0 NormalZ=1 AngleXU=0 Radius=19 StartAngle=1.5708 EndAngle=3.14159
    g2: ArcOfCircle CenterX=19 CenterY=19 CenterZ=0 NormalX=0 NormalY=0 NormalZ=1 AngleXU=0 Radius=16 StartAngle=1.5708 EndAngle=3.14159
    g3: LineSegment StartX=114 StartY=35 StartZ=0 EndX=19 EndY=35 EndZ=0
    g4: LineSegment StartX=5.21097e-06 StartY=3 StartZ=0 EndX=5.21097e-06 EndY=0 EndZ=0
    g5: LineSegment StartX=3 StartY=0 StartZ=0 EndX=5.21097e-06 EndY=0 EndZ=0
    g6: LineSegment StartX=3 StartY=19 StartZ=0 EndX=3 EndY=0 EndZ=0
    g7: LineSegment StartX=19 StartY=38 StartZ=0 EndX=124 EndY=38 EndZ=0
    g8: Circle CenterX=119 CenterY=35 CenterZ=0 NormalX=0 NormalY=0 NormalZ=1 AngleXU=0 Radius=1
    g9: Circle CenterX=121 CenterY=35 CenterZ=0 NormalX=0 NormalY=0 NormalZ=1 AngleXU=0 Radius=1
    g10: Circle CenterX=121 CenterY=33 CenterZ=0 NormalX=0 NormalY=0 NormalZ=1 AngleXU=0 Radius=1
    g11: BSplineCurve PolesCount=3 KnotsCount=2 Degree=2 IsPeriodic=0
    g12: GeomPoint X=119 Y=35 Z=0
    g13: GeomPoint X=121 Y=33 Z=0
    g14: LineSegment StartX=119 StartY=35 StartZ=0 EndX=114 EndY=35 EndZ=0
    g15: ArcOfCircle CenterX=105 CenterY=19 CenterZ=0 NormalX=0 NormalY=0 NormalZ=1 AngleXU=0 Radius=16 StartAngle=5.60905 EndAngle=6.28319
    g16: LineSegment StartX=121 StartY=33 StartZ=0 EndX=121 EndY=19 EndZ=0
    g17: LineSegment StartX=117.5 StartY=9.01251 StartZ=0 EndX=121.163 EndY=9.0125 EndZ=0
    g18: ArcOfCircle CenterX=105 CenterY=19 CenterZ=0 NormalX=0 NormalY=0 NormalZ=1 AngleXU=0 Radius=20.6155 StartAngle=5.7297 EndAngle=6.28319
    g19: LineSegment StartX=121.163 StartY=9.0125 StartZ=0 EndX=122.538 EndY=8.16329 EndZ=0
    g20: LineSegment StartX=124 StartY=38 StartZ=0 EndX=125.616 EndY=38 EndZ=0
    g21: LineSegment StartX=125.616 StartY=19 StartZ=0 EndX=125.616 EndY=38 EndZ=0
  constraints (49):
    c: Vertical(g0)
    c: Block(g0)
    c: Coincident(g1,g0)
    c: Block(g1)
    c: Coincident(g2,g1)
    c: Block(g2)
    c: Coincident(g3,g2)
    c: Horizontal(g3)
    c: Tangent(g3,g2)
    c: Coincident(g4,g0)
    c: Distance(g4) = 3
    c: Vertical(g4)
    c: Coincident(g5,g4)
    c: Horizontal(g5)
    c: Coincident(g6,g2)
    c: Coincident(g6,g5)
    c: Vertical(g6)
    c: Horizontal(g7)
    c: Distance(g7) = 105
    c: Coincident(g7,g1)
    c: Block(g3)
    c: Weight(g8) = 1
    c: Equal(g8,g9)
    c: Equal(g8,g10)
    c: InternalAlignment(g8,g11)
    c: InternalAlignment(g9,g11)
    c: InternalAlignment(g10,g11)
    c: InternalAlignment(g12,g11)
    c: InternalAlignment(g13,g11)
    c: Block(g11)
    c: Coincident(g14,g11)
    c: Coincident(g14,g3)
    c: Horizontal(g14)
    c: Block(g15)
    c: Coincident(g16,g11)
    c: Coincident(g16,g15)
    c: Vertical(g16)
    c: Distance(g16) = 14
    c: Coincident(g17,g15)
    c: Block(g18)
    c: Coincident(g19,g18)
    c: Coincident(g20,g7)
    c: Horizontal(g20)
    c: Vertical(g21)
    c: Coincident(g20,g21)
    c: Block(g20)
    c: Block(g21)
    c: Block(g19)
    c: Block(g17)
FEATURE [Part::Box] Box026  label="removeToCreteHoleForPlugHousing032"
  AttacherType = Attacher::AttachEngine3D
  Height = 28.6
  Length = 10
  Placement = pos=(-2,0,21.7) rot=(0,0,1;0rad)
  Width = 19
FEATURE [Part::Feature] Face109 .. Face112  x4 (patterned run collapsed; names and placements below)
  shape: bbox 3.5 x 17.8 x 2e-07 mm, 1 faces, 0 solids (baked)
FEATURE [Part::Revolution] Revolve117  label="removeToCreateScrewAndThreadedInsertHole045"
  Angle = 360
  Axis = (0,1,0)
  Base = (0,0,0)
  FaceMakerClass = Part::FaceMakerBullseye
  Placement = pos=(62.3,30.3,19.7) rot=(0,0,1;0rad)
  Solid = false
  Source = -> Face109
  Symmetric = false
FEATURE [Part::Revolution] Revolve118  label="removeToCreateScrewAndThreadedInsertHole046"
  Angle = 360
  Axis = (0,1,0)
  Base = (0,0,0)
  FaceMakerClass = Part::FaceMakerBullseye
  Placement = pos=(62.3,30.3,51.7) rot=(0,0,1;0rad)
  Solid = false
  Source = -> Face110
  Symmetric = false
FEATURE [Part::Revolution] Revolve119  label="removeToCreateScrewAndThreadedInsertHole047"
  Angle = 360
  Axis = (0,1,0)
  Base = (0,0,0)
  FaceMakerClass = Part::FaceMakerBullseye
  Placement = pos=(30.3,30.3,19.7) rot=(0,0,1;0rad)
  Solid = false
  Source = -> Face111
  Symmetric = false
FEATURE [Part::Revolution] Revolve120  label="removeToCreateScrewAndThreadedInsertHole048"
  Angle = 360
  Axis = (0,1,0)
  Base = (0,0,0)
  FaceMakerClass = Part::FaceMakerBullseye
  Placement = pos=(30.3,30.3,51.7) rot=(0,0,1;0rad)
  Solid = false
  Source = -> Face112
  Symmetric = false
FEATURE [Part::MultiFuse] Fusion087  label="createThreadedInsertHolesForFan005"
  Shapes = -> [Revolve117,Revolve118,Revolve119,Revolve120]
FEATURE [Part::Extrusion] Extrude047
  Base = -> Sketch056
  Dir = (0,0,1)
  DirMode = 2
  FaceMakerClass = Part::FaceMakerBullseye
  LengthFwd = 72
  LengthRev = 0
  Solid = true
  Symmetric = false
FEATURE [Part::Fillet] Fillet039  label="top019"
  Base = -> Extrude047
  Edges = 1 edges r=2: [Edge35]
FEATURE [Sketcher::SketchObject] Sketch057
  FullyConstrained = false
  Placement = pos=(0,0,0) rot=(1,0,0;1.5708rad)
  sketch-geometry (24):
    g0: ArcOfCircle CenterX=-4 CenterY=-10.5 CenterZ=0 NormalX=0 NormalY=0 NormalZ=1 AngleXU=0 Radius=1.5 StartAngle=6e-16 EndAngle=3.14159
    g1: ArcOfCircle CenterX=-34.2 CenterY=-10.5 CenterZ=0 NormalX=0 NormalY=0 NormalZ=1 AngleXU=0 Radius=1.5 StartAngle=0 EndAngle=3.14159
    g2: ArcOfCircle CenterX=-34.2 CenterY=-27.7 CenterZ=0 NormalX=0 NormalY=0 NormalZ=1 AngleXU=0 Radius=1.5 StartAngle=3.14159 EndAngle=6.28319
    g3: ArcOfCircle CenterX=-4 CenterY=-27.7 CenterZ=0 NormalX=0 NormalY=0 NormalZ=1 AngleXU=0 Radius=1.5 StartAngle=3.1416 EndAngle=6.28319
    g4: ArcOfCircle CenterX=-10 CenterY=-4.3 CenterZ=0 NormalX=0 NormalY=0 NormalZ=1 AngleXU=0 Radius=1.5 StartAngle=2e-16 EndAngle=3.14159
    g5: ArcOfCircle CenterX=-16.1 CenterY=-1.8 CenterZ=0 NormalX=0 NormalY=0 NormalZ=1 AngleXU=0 Radius=1.5 StartAngle=5e-16 EndAngle=3.14159
    g6: ArcOfCircle CenterX=-22.1 CenterY=-1.8 CenterZ=0 NormalX=0 NormalY=0 NormalZ=1 AngleXU=0 Radius=1.5 StartAngle=5e-16 EndAngle=3.14159
    g7: ArcOfCircle CenterX=-28.2 CenterY=-4.3 CenterZ=0 NormalX=0 NormalY=0 NormalZ=1 AngleXU=0 Radius=1.5 StartAngle=2e-16 EndAngle=3.14159
    g8: ArcOfCircle CenterX=-10 CenterY=-33.9 CenterZ=0 NormalX=0 NormalY=0 NormalZ=1 AngleXU=0 Radius=1.5 StartAngle=3.14159 EndAngle=6.28319
    g9: ArcOfCircle CenterX=-16.1 CenterY=-36.4 CenterZ=0 NormalX=0 NormalY=0 NormalZ=1 AngleXU=0 Radius=1.5 StartAngle=3.14159 EndAngle=6.28319
    g10: ArcOfCircle CenterX=-22.1 CenterY=-36.4 CenterZ=0 NormalX=0 NormalY=0 NormalZ=1 AngleXU=0 Radius=1.5 StartAngle=3.14159 EndAngle=6.28319
    g11: ArcOfCircle CenterX=-28.2 CenterY=-33.9 CenterZ=0 NormalX=0 NormalY=0 NormalZ=1 AngleXU=0 Radius=1.5 StartAngle=3.14159 EndAngle=6.28319
    g12: LineSegment StartX=-35.7 StartY=-10.5 StartZ=0 EndX=-35.7 EndY=-27.7 EndZ=0
    g13: LineSegment StartX=-32.7 StartY=-10.5 StartZ=0 EndX=-32.7 EndY=-27.7 EndZ=0
    g14: LineSegment StartX=-29.7 StartY=-33.9 StartZ=0 EndX=-29.7 EndY=-4.3 EndZ=0
    g15: LineSegment StartX=-26.7 StartY=-33.9 StartZ=0 EndX=-26.7 EndY=-4.3 EndZ=0
    g16: LineSegment StartX=-2.5 StartY=-10.5 StartZ=0 EndX=-2.5 EndY=-27.7 EndZ=0
    g17: LineSegment StartX=-8.5 StartY=-4.3 StartZ=0 EndX=-8.5 EndY=-33.9 EndZ=0
    g18: LineSegment StartX=-5.5 StartY=-10.5 StartZ=0 EndX=-5.5 EndY=-27.7 EndZ=0
    g19: LineSegment StartX=-11.5 StartY=-4.3 StartZ=0 EndX=-11.5 EndY=-33.9 EndZ=0
    g20: LineSegment StartX=-14.6 StartY=-1.8 StartZ=0 EndX=-14.6 EndY=-36.4 EndZ=0
    g21: LineSegment StartX=-17.6 StartY=-1.8 StartZ=0 EndX=-17.6 EndY=-36.4 EndZ=0
    g22: LineSegment StartX=-20.6 StartY=-36.4 StartZ=0 EndX=-20.6 EndY=-1.8 EndZ=0
    g23: LineSegment StartX=-23.6 StartY=-1.8 StartZ=0 EndX=-23.6 EndY=-36.4 EndZ=0
  constraints (48):
    c: Block(g0)
    c: Block(g1)
    c: Block(g2)
    c: Block(g3)
    c: Block(g4)
    c: Block(g5)
    c: Block(g6)
    c: Block(g7)
    c: Block(g8)
    c: Block(g9)
    c: Block(g10)
    c: Block(g11)
    c: Coincident(g12,g1)
    c: Coincident(g12,g2)
    c: Vertical(g12)
    c: Coincident(g13,g1)
    c: Coincident(g13,g2)
    c: Vertical(g13)
    c: Coincident(g14,g11)
    c: Coincident(g14,g7)
    c: Vertical(g14)
    c: Coincident(g15,g11)
    c: Coincident(g15,g7)
    c: Vertical(g15)
    c: Coincident(g16,g0)
    c: Coincident(g16,g3)
    c: Vertical(g16)
    c: Coincident(g17,g4)
    c: Coincident(g17,g8)
    c: Vertical(g17)
    c: Coincident(g18,g0)
    c: Coincident(g18,g3)
    c: Vertical(g18)
    c: Coincident(g19,g4)
    c: Coincident(g19,g8)
    c: Vertical(g19)
    c: Coincident(g20,g5)
    c: Coincident(g20,g9)
    c: Vertical(g20)
    c: Coincident(g21,g5)
    c: Coincident(g21,g9)
    c: Vertical(g21)
    c: Coincident(g22,g10)
    c: Coincident(g22,g6)
    c: Vertical(g22)
    c: Coincident(g23,g6)
    c: Coincident(g23,g10)
    c: Vertical(g23)
FEATURE [Part::Extrusion] Extrude048  label="removeToCreateFanGrillHoles004"
  Base = -> Sketch057
  Dir = (0,-1,6e-16)
  DirMode = 2
  FaceMakerClass = Part::FaceMakerBullseye
  LengthFwd = 10
  LengthRev = 0
  Placement = pos=(65.4,44,54.82) rot=(0,0,1;0rad)
  Solid = true
  Symmetric = false
FEATURE [Part::Cut] Cut040  label="top021"
  Base = -> Fillet039
  Tool = -> Extrude048
FEATURE [Part::Cylinder] Cylinder041  label="removeToCreteHoleForPlugHousing034"
  Angle = 360
  AttacherType = Attacher::AttachEngine3D
  Height = 20
  Placement = pos=(-2,19,36) rot=(0,1,0;1.5708rad)
  Radius = 14.3
FEATURE [Part::MultiFuse] Fusion089  label="removeToCreteHoleForPlugHousing035"
  Shapes = -> [Box026,Cylinder041]
FEATURE [Part::Cylinder] Cylinder042
  Angle = 360
  AttacherType = Attacher::AttachEngine3D
  Height = 20
  Placement = pos=(0,0,36.15) rot=(0,0,1;0rad)
  Radius = 14.3
FEATURE [Part::Cylinder] Cylinder043
  Angle = 360
  AttacherType = Attacher::AttachEngine3D
  Height = 10
  Placement = pos=(0,0,36.15) rot=(0,0,1;0rad)
  Radius = 4
FEATURE [Part::Box] Box027  label="removeToCreteHoleForPlugHousing036"
  AttacherType = Attacher::AttachEngine3D
  Height = 28.6
  Length = 20
  Placement = pos=(106.15,0,21.7) rot=(0,0,1;0rad)
  Width = 19
FEATURE [Part::Cut] Cut041  label="top022"
  Base = -> Cut040
  Tool = -> Fusion087
FEATURE [Part::Cut] Cut039  label="top020"
  Base = -> Cut041
  Tool = -> Fusion089
FEATURE [Part::MultiFuse] Fusion090  label="removeToCreteHoleForPlugHousing037"
  Placement = pos=(70,19,36) rot=(0,1,0;1.5708rad)
  Shapes = -> [Cylinder042,Cylinder043]
FEATURE [Part::MultiFuse] Fusion088  label="removeToCreteHoleForPlugHousing033"
  Shapes = -> [Box027,Fusion090]
FEATURE [Part::Cut] Cut042  label="removeToCreteHoleForPlugHousing038"
  Base = -> Cut039
  Tool = -> Fusion088
FEATURE [Part::MultiFuse] Fusion091  label="removeFromTop"
  Shapes = -> [Fillet038,Fusion085,Fusion084,Fusion083,Extrude045]
FEATURE [Part::Cut] Cut043  label="REAL TOP ====="
  Base = -> Fillet036
  Tool = -> Fusion091
FEATURE [Part::MultiFuse] Fusion092  label="caseScrewPillarBracket016"
  Shapes = -> [Extrude030,Extrude031,Extrude032,Extrude033,Extrude034,Extrude035,Extrude036,Extrude037,Box013,Box014]
FEATURE [Sketcher::SketchObject] Sketch058  label="topSketch015"
  FullyConstrained = true
  sketch-geometry (20):
    g0: LineSegment StartX=5.21097e-06 StartY=3 StartZ=0 EndX=5.21097e-06 EndY=19 EndZ=0
    g1: ArcOfCircle CenterX=19 CenterY=19 CenterZ=0 NormalX=0 NormalY=0 NormalZ=1 AngleXU=0 Radius=19 StartAngle=1.5708 EndAngle=3.14159
    g2: ArcOfCircle CenterX=19 CenterY=19 CenterZ=0 NormalX=0 NormalY=0 NormalZ=1 AngleXU=0 Radius=16 StartAngle=1.5708 EndAngle=3.14159
    g3: LineSegment StartX=114 StartY=35 StartZ=0 EndX=19 EndY=35 EndZ=0
    g4: LineSegment StartX=5.21097e-06 StartY=3 StartZ=0 EndX=5.21097e-06 EndY=0 EndZ=0
    g5: LineSegment StartX=3 StartY=0 StartZ=0 EndX=5.21097e-06 EndY=0 EndZ=0
    g6: LineSegment StartX=3 StartY=19 StartZ=0 EndX=3 EndY=0 EndZ=0
    g7: LineSegment StartX=19 StartY=38 StartZ=0 EndX=124 EndY=38 EndZ=0
    g8: Circle CenterX=119 CenterY=35 CenterZ=0 NormalX=0 NormalY=0 NormalZ=1 AngleXU=0 Radius=1
    g9: Circle CenterX=121 CenterY=35 CenterZ=0 NormalX=0 NormalY=0 NormalZ=1 AngleXU=0 Radius=1
    g10: Circle CenterX=121 CenterY=33 CenterZ=0 NormalX=0 NormalY=0 NormalZ=1 AngleXU=0 Radius=1
    g11: BSplineCurve PolesCount=3 KnotsCount=2 Degree=2 IsPeriodic=0
    g12: GeomPoint X=119 Y=35 Z=0
    g13: GeomPoint X=121 Y=33 Z=0
    g14: LineSegment StartX=119 StartY=35 StartZ=0 EndX=114 EndY=35 EndZ=0
    g15: ArcOfCircle CenterX=105 CenterY=19 CenterZ=0 NormalX=0 NormalY=0 NormalZ=1 AngleXU=0 Radius=19 StartAngle=5.7297 EndAngle=6.28319
    g16: ArcOfCircle CenterX=105 CenterY=19 CenterZ=0 NormalX=0 NormalY=0 NormalZ=1 AngleXU=0 Radius=16 StartAngle=5.60905 EndAngle=6.28319
    g17: LineSegment StartX=121 StartY=33 StartZ=0 EndX=121 EndY=19 EndZ=0
    g18: LineSegment StartX=124 StartY=38 StartZ=0 EndX=124 EndY=19 EndZ=0
    g19: LineSegment StartX=117.5 StartY=9.01251 StartZ=0 EndX=121.163 EndY=9.0125 EndZ=0
  constraints (46):
    c: Vertical(g0)
    c: Block(g0)
    c: Coincident(g1,g0)
    c: Block(g1)
    c: Coincident(g2,g1)
    c: Block(g2)
    c: Coincident(g3,g2)
    c: Horizontal(g3)
    c: Tangent(g3,g2)
    c: Coincident(g4,g0)
    c: Distance(g4) = 3
    c: Vertical(g4)
    c: Coincident(g5,g4)
    c: Horizontal(g5)
    c: Coincident(g6,g2)
    c: Coincident(g6,g5)
    c: Vertical(g6)
    c: Horizontal(g7)
    c: Distance(g7) = 105
    c: Coincident(g7,g1)
    c: Block(g3)
    c: Weight(g8) = 1
    c: Equal(g8,g9)
    c: Equal(g8,g10)
    c: InternalAlignment(g8,g11)
    c: InternalAlignment(g9,g11)
    c: InternalAlignment(g10,g11)
    c: InternalAlignment(g12,g11)
    c: InternalAlignment(g13,g11)
    c: Block(g11)
    c: Coincident(g14,g11)
    c: Coincident(g14,g3)
    c: Horizontal(g14)
    c: Block(g15)
    c: Coincident(g16,g15)
    c: Block(g16)
    c: Coincident(g17,g11)
    c: Coincident(g17,g16)
    c: Vertical(g17)
    c: Distance(g17) = 14
    c: Coincident(g18,g7)
    c: Coincident(g18,g15)
    c: Vertical(g18)
    c: Distance(g18) = 19
    c: Coincident(g19,g16)
    c: Coincident(g19,g15)
FEATURE [Part::Extrusion] Extrude049  label="top023"
  Base = -> Sketch058
  Dir = (0,0,1)
  DirMode = 2
  FaceMakerClass = Part::FaceMakerBullseye
  LengthFwd = 72
  LengthRev = 0
  Solid = true
  Symmetric = false
FEATURE [Sketcher::SketchObject] Sketch059
  FullyConstrained = true
  MapMode = 3
  Placement = pos=(0,0,0) rot=(1,0,0;1.5708rad)
  Support = -> [Extrude049]
  sketch-geometry (8):
    g0: Circle CenterX=80.351 CenterY=-67.6202 CenterZ=0 NormalX=0 NormalY=0 NormalZ=1 AngleXU=0 Radius=2
    g1: Circle CenterX=80.351 CenterY=-67.6202 CenterZ=0 NormalX=0 NormalY=0 NormalZ=1 AngleXU=0 Radius=3
    g2: Circle CenterX=80.351 CenterY=-4.92017 CenterZ=0 NormalX=0 NormalY=0 NormalZ=1 AngleXU=0 Radius=2
    g3: Circle CenterX=80.351 CenterY=-4.92017 CenterZ=0 NormalX=0 NormalY=0 NormalZ=1 AngleXU=0 Radius=3
    g4: Circle CenterX=23.851 CenterY=-4.92017 CenterZ=0 NormalX=0 NormalY=0 NormalZ=1 AngleXU=0 Radius=2
    g5: Circle CenterX=23.851 CenterY=-4.92017 CenterZ=0 NormalX=0 NormalY=0 NormalZ=1 AngleXU=0 Radius=3
    g6: Circle CenterX=23.851 CenterY=-67.6202 CenterZ=0 NormalX=0 NormalY=0 NormalZ=1 AngleXU=0 Radius=2
    g7: Circle CenterX=23.851 CenterY=-67.6202 CenterZ=0 NormalX=0 NormalY=0 NormalZ=1 AngleXU=0 Radius=3
  constraints (8):
    c: Block(g3)
    c: Block(g2)
    c: Block(g1)
    c: Block(g0)
    c: Block(g6)
    c: Block(g7)
    c: Block(g4)
    c: Block(g5)
FEATURE [Sketcher::SketchObject] Sketch060
  FullyConstrained = true
  MapMode = 3
  Placement = pos=(0,0,0) rot=(1,0,0;1.5708rad)
  Support = -> [Extrude049]
  sketch-geometry (8):
    g0: Circle CenterX=80.351 CenterY=-67.6202 CenterZ=0 NormalX=0 NormalY=0 NormalZ=1 AngleXU=0 Radius=3
    g1: Circle CenterX=80.351 CenterY=-4.92017 CenterZ=0 NormalX=0 NormalY=0 NormalZ=1 AngleXU=0 Radius=3
    g2: Circle CenterX=23.851 CenterY=-4.92017 CenterZ=0 NormalX=0 NormalY=0 NormalZ=1 AngleXU=0 Radius=3
    g3: Circle CenterX=23.851 CenterY=-67.6202 CenterZ=0 NormalX=0 NormalY=0 NormalZ=1 AngleXU=0 Radius=3
    g4: Circle CenterX=23.851 CenterY=-67.6202 CenterZ=0 NormalX=0 NormalY=0 NormalZ=1 AngleXU=0 Radius=5
    g5: Circle CenterX=80.351 CenterY=-67.6202 CenterZ=0 NormalX=0 NormalY=0 NormalZ=1 AngleXU=0 Radius=5
    g6: Circle CenterX=23.851 CenterY=-4.92017 CenterZ=0 NormalX=0 NormalY=0 NormalZ=1 AngleXU=0 Radius=5
    g7: Circle CenterX=80.351 CenterY=-4.92017 CenterZ=0 NormalX=0 NormalY=0 NormalZ=1 AngleXU=0 Radius=5
  constraints (8):
    c: Block(g1)
    c: Block(g0)
    c: Block(g3)
    c: Block(g2)
    c: Block(g5)
    c: Block(g4)
    c: Block(g6)
    c: Block(g7)
FEATURE [Sketcher::SketchObject] Sketch061
  FullyConstrained = true
  MapMode = 3
  Placement = pos=(0,0,0) rot=(1,0,0;1.5708rad)
  sketch-geometry (8):
    g0: Circle CenterX=80.351 CenterY=-67.6202 CenterZ=0 NormalX=0 NormalY=0 NormalZ=1 AngleXU=0 Radius=3
    g1: Circle CenterX=80.351 CenterY=-4.92017 CenterZ=0 NormalX=0 NormalY=0 NormalZ=1 AngleXU=0 Radius=3
    g2: Circle CenterX=23.851 CenterY=-4.92017 CenterZ=0 NormalX=0 NormalY=0 NormalZ=1 AngleXU=0 Radius=3
    g3: Circle CenterX=23.851 CenterY=-67.6202 CenterZ=0 NormalX=0 NormalY=0 NormalZ=1 AngleXU=0 Radius=3
    g4: Circle CenterX=23.851 CenterY=-67.6202 CenterZ=0 NormalX=0 NormalY=0 NormalZ=1 AngleXU=0 Radius=5
    g5: Circle CenterX=80.351 CenterY=-67.6202 CenterZ=0 NormalX=0 NormalY=0 NormalZ=1 AngleXU=0 Radius=5
    g6: Circle CenterX=23.851 CenterY=-4.92017 CenterZ=0 NormalX=0 NormalY=0 NormalZ=1 AngleXU=0 Radius=5
    g7: Circle CenterX=80.351 CenterY=-4.92017 CenterZ=0 NormalX=0 NormalY=0 NormalZ=1 AngleXU=0 Radius=5
  constraints (8):
    c: Block(g1)
    c: Block(g0)
    c: Block(g3)
    c: Block(g2)
    c: Block(g5)
    c: Block(g4)
    c: Block(g6)
    c: Block(g7)
FEATURE [Sketcher::SketchObject] Sketch062  label="topSketch016"
  FullyConstrained = true
  sketch-geometry (20):
    g0: LineSegment StartX=5.21097e-06 StartY=3 StartZ=0 EndX=5.21097e-06 EndY=19 EndZ=0
    g1: ArcOfCircle CenterX=19 CenterY=19 CenterZ=0 NormalX=0 NormalY=0 NormalZ=1 AngleXU=0 Radius=19 StartAngle=1.5708 EndAngle=3.14159
    g2: ArcOfCircle CenterX=19 CenterY=19 CenterZ=0 NormalX=0 NormalY=0 NormalZ=1 AngleXU=0 Radius=16 StartAngle=1.5708 EndAngle=3.14159
    g3: LineSegment StartX=114 StartY=35 StartZ=0 EndX=19 EndY=35 EndZ=0
    g4: LineSegment StartX=5.21097e-06 StartY=3 StartZ=0 EndX=5.21097e-06 EndY=0 EndZ=0
    g5: LineSegment StartX=3 StartY=0 StartZ=0 EndX=5.21097e-06 EndY=0 EndZ=0
    g6: LineSegment StartX=3 StartY=19 StartZ=0 EndX=3 EndY=0 EndZ=0
    g7: LineSegment StartX=19 StartY=38 StartZ=0 EndX=124 EndY=38 EndZ=0
    g8: Circle CenterX=119 CenterY=35 CenterZ=0 NormalX=0 NormalY=0 NormalZ=1 AngleXU=0 Radius=1
    g9: Circle CenterX=121 CenterY=35 CenterZ=0 NormalX=0 NormalY=0 NormalZ=1 AngleXU=0 Radius=1
    g10: Circle CenterX=121 CenterY=33 CenterZ=0 NormalX=0 NormalY=0 NormalZ=1 AngleXU=0 Radius=1
    g11: BSplineCurve PolesCount=3 KnotsCount=2 Degree=2 IsPeriodic=0
    g12: GeomPoint X=119 Y=35 Z=0
    g13: GeomPoint X=121 Y=33 Z=0
    g14: LineSegment StartX=119 StartY=35 StartZ=0 EndX=114 EndY=35 EndZ=0
    g15: ArcOfCircle CenterX=105 CenterY=19 CenterZ=0 NormalX=0 NormalY=0 NormalZ=1 AngleXU=0 Radius=19 StartAngle=5.7297 EndAngle=6.28319
    g16: ArcOfCircle CenterX=105 CenterY=19 CenterZ=0 NormalX=0 NormalY=0 NormalZ=1 AngleXU=0 Radius=16 StartAngle=5.60905 EndAngle=6.28319
    g17: LineSegment StartX=121 StartY=33 StartZ=0 EndX=121 EndY=19 EndZ=0
    g18: LineSegment StartX=124 StartY=38 StartZ=0 EndX=124 EndY=19 EndZ=0
    g19: LineSegment StartX=117.5 StartY=9.01251 StartZ=0 EndX=121.163 EndY=9.0125 EndZ=0
  constraints (46):
    c: Vertical(g0)
    c: Block(g0)
    c: Coincident(g1,g0)
    c: Block(g1)
    c: Coincident(g2,g1)
    c: Block(g2)
    c: Coincident(g3,g2)
    c: Horizontal(g3)
    c: Tangent(g3,g2)
    c: Coincident(g4,g0)
    c: Distance(g4) = 3
    c: Vertical(g4)
    c: Coincident(g5,g4)
    c: Horizontal(g5)
    c: Coincident(g6,g2)
    c: Coincident(g6,g5)
    c: Vertical(g6)
    c: Horizontal(g7)
    c: Distance(g7) = 105
    c: Coincident(g7,g1)
    c: Block(g3)
    c: Weight(g8) = 1
    c: Equal(g8,g9)
    c: Equal(g8,g10)
    c: InternalAlignment(g8,g11)
    c: InternalAlignment(g9,g11)
    c: InternalAlignment(g10,g11)
    c: InternalAlignment(g12,g11)
    c: InternalAlignment(g13,g11)
    c: Block(g11)
    c: Coincident(g14,g11)
    c: Coincident(g14,g3)
    c: Horizontal(g14)
    c: Block(g15)
    c: Coincident(g16,g15)
    c: Block(g16)
    c: Coincident(g17,g11)
    c: Coincident(g17,g16)
    c: Vertical(g17)
    c: Distance(g17) = 14
    c: Coincident(g18,g7)
    c: Coincident(g18,g15)
    c: Vertical(g18)
    c: Distance(g18) = 19
    c: Coincident(g19,g16)
    c: Coincident(g19,g15)
FEATURE [Part::Extrusion] Extrude053  label="top024"
  Base = -> Sketch062
  Dir = (0,0,1)
  DirMode = 2
  FaceMakerClass = Part::FaceMakerBullseye
  LengthFwd = 72
  LengthRev = 0
  Solid = true
  Symmetric = false
FEATURE [Sketcher::SketchObject] Sketch063
  FullyConstrained = true
  MapMode = 3
  Placement = pos=(0,0,0) rot=(1,0,0;1.5708rad)
  Support = -> [Extrude053]
  sketch-geometry (8):
    g0: Circle CenterX=80.351 CenterY=-67.6202 CenterZ=0 NormalX=0 NormalY=0 NormalZ=1 AngleXU=0 Radius=2
    g1: Circle CenterX=80.351 CenterY=-67.6202 CenterZ=0 NormalX=0 NormalY=0 NormalZ=1 AngleXU=0 Radius=3
    g2: Circle CenterX=80.351 CenterY=-4.92017 CenterZ=0 NormalX=0 NormalY=0 NormalZ=1 AngleXU=0 Radius=2
    g3: Circle CenterX=80.351 CenterY=-4.92017 CenterZ=0 NormalX=0 NormalY=0 NormalZ=1 AngleXU=0 Radius=3
    g4: Circle CenterX=23.851 CenterY=-4.92017 CenterZ=0 NormalX=0 NormalY=0 NormalZ=1 AngleXU=0 Radius=2
    g5: Circle CenterX=23.851 CenterY=-4.92017 CenterZ=0 NormalX=0 NormalY=0 NormalZ=1 AngleXU=0 Radius=3
    g6: Circle CenterX=23.851 CenterY=-67.6202 CenterZ=0 NormalX=0 NormalY=0 NormalZ=1 AngleXU=0 Radius=2
    g7: Circle CenterX=23.851 CenterY=-67.6202 CenterZ=0 NormalX=0 NormalY=0 NormalZ=1 AngleXU=0 Radius=3
  constraints (8):
    c: Block(g3)
    c: Block(g2)
    c: Block(g1)
    c: Block(g0)
    c: Block(g6)
    c: Block(g7)
    c: Block(g4)
    c: Block(g5)
FEATURE [Part::Extrusion] Extrude054
  Base = -> Sketch063
  Dir = (0,-1,2e-16)
  DirMode = 2
  FaceMakerClass = Part::FaceMakerBullseye
  LengthFwd = 6
  LengthRev = 0
  Placement = pos=(0,9,0) rot=(0,0,1;0rad)
  Solid = true
  Symmetric = false
FEATURE [Sketcher::SketchObject] Sketch064  label="topSketch017"
  FullyConstrained = true
  sketch-geometry (20):
    g0: LineSegment StartX=5.21097e-06 StartY=3 StartZ=0 EndX=5.21097e-06 EndY=19 EndZ=0
    g1: ArcOfCircle CenterX=19 CenterY=19 CenterZ=0 NormalX=0 NormalY=0 NormalZ=1 AngleXU=0 Radius=19 StartAngle=1.5708 EndAngle=3.14159
    g2: ArcOfCircle CenterX=19 CenterY=19 CenterZ=0 NormalX=0 NormalY=0 NormalZ=1 AngleXU=0 Radius=16 StartAngle=1.5708 EndAngle=3.14159
    g3: LineSegment StartX=114 StartY=35 StartZ=0 EndX=19 EndY=35 EndZ=0
    g4: LineSegment StartX=5.21097e-06 StartY=3 StartZ=0 EndX=5.21097e-06 EndY=0 EndZ=0
    g5: LineSegment StartX=3 StartY=0 StartZ=0 EndX=5.21097e-06 EndY=0 EndZ=0
    g6: LineSegment StartX=3 StartY=19 StartZ=0 EndX=3 EndY=0 EndZ=0
    g7: LineSegment StartX=19 StartY=38 StartZ=0 EndX=124 EndY=38 EndZ=0
    g8: Circle CenterX=119 CenterY=35 CenterZ=0 NormalX=0 NormalY=0 NormalZ=1 AngleXU=0 Radius=1
    g9: Circle CenterX=121 CenterY=35 CenterZ=0 NormalX=0 NormalY=0 NormalZ=1 AngleXU=0 Radius=1
    g10: Circle CenterX=121 CenterY=33 CenterZ=0 NormalX=0 NormalY=0 NormalZ=1 AngleXU=0 Radius=1
    g11: BSplineCurve PolesCount=3 KnotsCount=2 Degree=2 IsPeriodic=0
    g12: GeomPoint X=119 Y=35 Z=0
    g13: GeomPoint X=121 Y=33 Z=0
    g14: LineSegment StartX=119 StartY=35 StartZ=0 EndX=114 EndY=35 EndZ=0
    g15: ArcOfCircle CenterX=105 CenterY=19 CenterZ=0 NormalX=0 NormalY=0 NormalZ=1 AngleXU=0 Radius=19 StartAngle=5.7297 EndAngle=6.28319
    g16: ArcOfCircle CenterX=105 CenterY=19 CenterZ=0 NormalX=0 NormalY=0 NormalZ=1 AngleXU=0 Radius=16 StartAngle=5.60905 EndAngle=6.28319
    g17: LineSegment StartX=121 StartY=33 StartZ=0 EndX=121 EndY=19 EndZ=0
    g18: LineSegment StartX=124 StartY=38 StartZ=0 EndX=124 EndY=19 EndZ=0
    g19: LineSegment StartX=117.5 StartY=9.01251 StartZ=0 EndX=121.163 EndY=9.0125 EndZ=0
  constraints (46):
    c: Vertical(g0)
    c: Block(g0)
    c: Coincident(g1,g0)
    c: Block(g1)
    c: Coincident(g2,g1)
    c: Block(g2)
    c: Coincident(g3,g2)
    c: Horizontal(g3)
    c: Tangent(g3,g2)
    c: Coincident(g4,g0)
    c: Distance(g4) = 3
    c: Vertical(g4)
    c: Coincident(g5,g4)
    c: Horizontal(g5)
    c: Coincident(g6,g2)
    c: Coincident(g6,g5)
    c: Vertical(g6)
    c: Horizontal(g7)
    c: Distance(g7) = 105
    c: Coincident(g7,g1)
    c: Block(g3)
    c: Weight(g8) = 1
    c: Equal(g8,g9)
    c: Equal(g8,g10)
    c: InternalAlignment(g8,g11)
    c: InternalAlignment(g9,g11)
    c: InternalAlignment(g10,g11)
    c: InternalAlignment(g12,g11)
    c: InternalAlignment(g13,g11)
    c: Block(g11)
    c: Coincident(g14,g11)
    c: Coincident(g14,g3)
    c: Horizontal(g14)
    c: Block(g15)
    c: Coincident(g16,g15)
    c: Block(g16)
    c: Coincident(g17,g11)
    c: Coincident(g17,g16)
    c: Vertical(g17)
    c: Distance(g17) = 14
    c: Coincident(g18,g7)
    c: Coincident(g18,g15)
    c: Vertical(g18)
    c: Distance(g18) = 19
    c: Coincident(g19,g16)
    c: Coincident(g19,g15)
FEATURE [Sketcher::SketchObject] Sketch065
  FullyConstrained = true
  MapMode = 3
  Placement = pos=(0,0,0) rot=(1,0,0;1.5708rad)
  sketch-geometry (8):
    g0: Circle CenterX=80.351 CenterY=-67.6202 CenterZ=0 NormalX=0 NormalY=0 NormalZ=1 AngleXU=0 Radius=3
    g1: Circle CenterX=80.351 CenterY=-4.92017 CenterZ=0 NormalX=0 NormalY=0 NormalZ=1 AngleXU=0 Radius=3
    g2: Circle CenterX=23.851 CenterY=-4.92017 CenterZ=0 NormalX=0 NormalY=0 NormalZ=1 AngleXU=0 Radius=3
    g3: Circle CenterX=23.851 CenterY=-67.6202 CenterZ=0 NormalX=0 NormalY=0 NormalZ=1 AngleXU=0 Radius=3
    g4: Circle CenterX=23.851 CenterY=-67.6202 CenterZ=0 NormalX=0 NormalY=0 NormalZ=1 AngleXU=0 Radius=5
    g5: Circle CenterX=80.351 CenterY=-67.6202 CenterZ=0 NormalX=0 NormalY=0 NormalZ=1 AngleXU=0 Radius=5
    g6: Circle CenterX=23.851 CenterY=-4.92017 CenterZ=0 NormalX=0 NormalY=0 NormalZ=1 AngleXU=0 Radius=5
    g7: Circle CenterX=80.351 CenterY=-4.92017 CenterZ=0 NormalX=0 NormalY=0 NormalZ=1 AngleXU=0 Radius=5
  constraints (8):
    c: Block(g1)
    c: Block(g0)
    c: Block(g3)
    c: Block(g2)
    c: Block(g5)
    c: Block(g4)
    c: Block(g6)
    c: Block(g7)
FEATURE [Part::Extrusion] Extrude056
  Base = -> Sketch065
  Dir = (0,-1,2e-16)
  DirMode = 2
  FaceMakerClass = Part::FaceMakerBullseye
  LengthFwd = 2
  LengthRev = 0
  Solid = true
  Symmetric = false
FEATURE [Part::Extrusion] Extrude057  label="top025"
  Base = -> Sketch064
  Dir = (0,0,1)
  DirMode = 2
  FaceMakerClass = Part::FaceMakerBullseye
  LengthFwd = 72
  LengthRev = 0
  Solid = true
  Symmetric = false
FEATURE [Sketcher::SketchObject] Sketch066
  FullyConstrained = true
  MapMode = 3
  Placement = pos=(0,0,0) rot=(1,0,0;1.5708rad)
  Support = -> [Extrude057]
  sketch-geometry (8):
    g0: Circle CenterX=80.351 CenterY=-67.6202 CenterZ=0 NormalX=0 NormalY=0 NormalZ=1 AngleXU=0 Radius=3
    g1: Circle CenterX=80.351 CenterY=-4.92017 CenterZ=0 NormalX=0 NormalY=0 NormalZ=1 AngleXU=0 Radius=3
    g2: Circle CenterX=23.851 CenterY=-4.92017 CenterZ=0 NormalX=0 NormalY=0 NormalZ=1 AngleXU=0 Radius=3
    g3: Circle CenterX=23.851 CenterY=-67.6202 CenterZ=0 NormalX=0 NormalY=0 NormalZ=1 AngleXU=0 Radius=3
    g4: Circle CenterX=23.851 CenterY=-67.6202 CenterZ=0 NormalX=0 NormalY=0 NormalZ=1 AngleXU=0 Radius=5
    g5: Circle CenterX=80.351 CenterY=-67.6202 CenterZ=0 NormalX=0 NormalY=0 NormalZ=1 AngleXU=0 Radius=5
    g6: Circle CenterX=23.851 CenterY=-4.92017 CenterZ=0 NormalX=0 NormalY=0 NormalZ=1 AngleXU=0 Radius=5
    g7: Circle CenterX=80.351 CenterY=-4.92017 CenterZ=0 NormalX=0 NormalY=0 NormalZ=1 AngleXU=0 Radius=5
  constraints (8):
    c: Block(g1)
    c: Block(g0)
    c: Block(g3)
    c: Block(g2)
    c: Block(g5)
    c: Block(g4)
    c: Block(g6)
    c: Block(g7)
FEATURE [Part::Extrusion] Extrude055
  Base = -> Sketch066
  Dir = (0,-1,2e-16)
  DirMode = 2
  FaceMakerClass = Part::FaceMakerBullseye
  LengthFwd = 2
  LengthRev = 0
  Solid = true
  Symmetric = false
FEATURE [Part::Fillet] Fillet041
  Base = -> Extrude056
  Edges = 4 edges r=1.99: [Edge6,Edge12,Edge18,Edge24]
FEATURE [Part::Cut] Cut045
  Base = -> Extrude055
  Placement = pos=(0,6,0) rot=(0,0,1;0rad)
  Tool = -> Fillet041
FEATURE [Part::MultiFuse] Fusion095  label="pcbScrewPillars"
  Placement = pos=(-3.2,-1,72.3) rot=(0,0,1;0rad)
  Shapes = -> [Cut045,Extrude054]
FEATURE [Part::Feature] Face113
  shape: bbox 3.2 x 1.5 x 2e-07 mm, 1 faces, 0 solids (baked)
FEATURE [Part::Revolution] Revolve121  label="backCaseScrewRetainer002"
  Angle = 360
  Axis = (0,1,0)
  Base = (0,0,0)
  FaceMakerClass = Part::FaceMakerBullseye
  Placement = pos=(12.5,3,62) rot=(0,0,1;0rad)
  Solid = false
  Source = -> Face113
  Symmetric = false
FEATURE [Part::Feature] Face114
  shape: bbox 3.2 x 1.5 x 2e-07 mm, 1 faces, 0 solids (baked)
FEATURE [Part::Feature] Face115
  shape: bbox 3.2 x 1.5 x 2e-07 mm, 1 faces, 0 solids (baked)
FEATURE [Part::Feature] Face116
  shape: bbox 3.2 x 1.5 x 2e-07 mm, 1 faces, 0 solids (baked)
FEATURE [Part::Revolution] Revolve122  label="frontCaseScrewRetainer004"
  Angle = 360
  Axis = (0,1,0)
  Base = (0,0,0)
  FaceMakerClass = Part::FaceMakerBullseye
  Placement = pos=(89.5,3,68.5) rot=(0,0,1;0rad)
  Solid = false
  Source = -> Face115
  Symmetric = false
FEATURE [Part::Revolution] Revolve123  label="frontCaseScrewRetainer005"
  Angle = 360
  Axis = (0,1,0)
  Base = (0,0,0)
  FaceMakerClass = Part::FaceMakerBullseye
  Placement = pos=(89.5,3,3.5) rot=(0,0,1;0rad)
  Solid = false
  Source = -> Face116
  Symmetric = false
FEATURE [Part::Revolution] Revolve124  label="backCaseScrewRetainer003"
  Angle = 360
  Axis = (0,1,0)
  Base = (0,0,0)
  FaceMakerClass = Part::FaceMakerBullseye
  Placement = pos=(12.5,3,10) rot=(0,0,1;0rad)
  Solid = false
  Source = -> Face114
  Symmetric = false
FEATURE [Part::Feature] Face117
  shape: bbox 3.6 x 3.2 x 2e-07 mm, 1 faces, 0 solids (baked)
FEATURE [Part::Revolution] Revolve125  label="moreFrontCaseScrewRetainer004"
  Angle = 360
  Axis = (0,1,0)
  Base = (0,0,0)
  FaceMakerClass = Part::FaceMakerBullseye
  Placement = pos=(109.5,4.5,68.5) rot=(0,0,1;0rad)
  Solid = false
  Source = -> Face117
  Symmetric = false
FEATURE [Part::Feature] Face118
  shape: bbox 3.6 x 3.2 x 2e-07 mm, 1 faces, 0 solids (baked)
FEATURE [Part::Revolution] Revolve126  label="moreFrontCaseScrewRetainer005"
  Angle = 360
  Axis = (0,1,0)
  Base = (0,0,0)
  FaceMakerClass = Part::FaceMakerBullseye
  Placement = pos=(109.5,4.5,3.5) rot=(0,0,1;0rad)
  Solid = false
  Source = -> Face118
  Symmetric = false
FEATURE [Part::MultiFuse] Fusion096  label="screwRetainers001"
  Shapes = -> [Revolve126,Revolve125,Revolve124,Revolve123,Revolve122,Revolve121]
FEATURE [Part::Feature] Face119
  shape: bbox 10 x 16.5 x 2e-07 mm, 1 faces, 0 solids (baked)
FEATURE [Part::Revolution] Revolve130  label="plugHousing050"
  Angle = 360
  Axis = (0,1,0)
  Base = (0,0,0)
  FaceMakerClass = Part::FaceMakerBullseye
  Placement = pos=(0,0,36.15) rot=(0,0,1;0rad)
  Solid = false
  Source = -> Face119
  Symmetric = false
FEATURE [Part::Feature] Face120
  shape: bbox 10 x 16.5 x 2e-07 mm, 1 faces, 0 solids (baked)
FEATURE [Part::Feature] Face121
  shape: bbox 10 x 16.5 x 2e-07 mm, 1 faces, 0 solids (baked)
FEATURE [Part::Revolution] Revolve127  label="plugHousing047"
  Angle = 360
  Axis = (0,1,0)
  Base = (0,0,0)
  FaceMakerClass = Part::FaceMakerBullseye
  Placement = pos=(0,0,36.15) rot=(0,0,1;0rad)
  Solid = false
  Source = -> Face121
  Symmetric = false
FEATURE [Part::Feature] Face122
  shape: bbox 10 x 16.5 x 2e-07 mm, 1 faces, 0 solids (baked)
FEATURE [Part::Feature] Face123
  shape: bbox 10 x 16.5 x 2e-07 mm, 1 faces, 0 solids (baked)
FEATURE [Part::Revolution] Revolve128  label="plugHousing048"
  Angle = 360
  Axis = (0,1,0)
  Base = (0,0,0)
  FaceMakerClass = Part::FaceMakerBullseye
  Placement = pos=(0,0,36.15) rot=(0,0,1;0rad)
  Solid = false
  Source = -> Face123
  Symmetric = false
FEATURE [Part::MultiFuse] Fusion100  label="plugHousing054"
  Placement = pos=(0,0,0) rot=(0,0,1;1.5708rad)
  Shapes = -> [Revolve130,Revolve128]
FEATURE [Part::Feature] Face124
  shape: bbox 10 x 16.5 x 2e-07 mm, 1 faces, 0 solids (baked)
FEATURE [Part::Feature] Face125
  shape: bbox 10 x 16.5 x 2e-07 mm, 1 faces, 0 solids (baked)
FEATURE [Part::Revolution] Revolve129  label="plugHousing049"
  Angle = 360
  Axis = (0,1,0)
  Base = (0,0,0)
  FaceMakerClass = Part::FaceMakerBullseye
  Placement = pos=(0,0,36.15) rot=(0,0,1;0rad)
  Solid = false
  Source = -> Face125
  Symmetric = false
FEATURE [Part::Feature] Face126
  shape: bbox 10 x 16.5 x 2e-07 mm, 1 faces, 0 solids (baked)
FEATURE [Part::Revolution] Revolve131  label="plugHousing058"
  Angle = 360
  Axis = (0,1,0)
  Base = (0,0,0)
  FaceMakerClass = Part::FaceMakerBullseye
  Placement = pos=(0,0,36.15) rot=(0,0,1;0rad)
  Solid = false
  Source = -> Face120
  Symmetric = false
FEATURE [Part::MultiFuse] Fusion099  label="plugHousing053"
  Placement = pos=(0,0,0) rot=(0,0,1;1.5708rad)
  Shapes = -> [Revolve127,Revolve131]
FEATURE [Part::MultiFuse] Fusion102  label="plugHousing056"
  Placement = pos=(0,19,0) rot=(0,0,1;3.14159rad)
  Shapes = -> [Fusion100,Fusion099]
FEATURE [Part::Revolution] Revolve132  label="plugHousing059"
  Angle = 360
  Axis = (0,1,0)
  Base = (0,0,0)
  FaceMakerClass = Part::FaceMakerBullseye
  Placement = pos=(0,0,36.15) rot=(0,0,1;0rad)
  Solid = false
  Source = -> Face126
  Symmetric = false
FEATURE [Part::Revolution] Revolve133  label="plugHousing060"
  Angle = 360
  Axis = (0,1,0)
  Base = (0,0,0)
  FaceMakerClass = Part::FaceMakerBullseye
  Placement = pos=(0,0,36.15) rot=(0,0,1;0rad)
  Solid = false
  Source = -> Face122
  Symmetric = false
FEATURE [Part::MultiFuse] Fusion097  label="plugHousing051"
  Placement = pos=(0,0,0) rot=(0,0,1;1.5708rad)
  Shapes = -> [Revolve133,Revolve132]
FEATURE [Part::Revolution] Revolve134  label="plugHousing061"
  Angle = 360
  Axis = (0,1,0)
  Base = (0,0,0)
  FaceMakerClass = Part::FaceMakerBullseye
  Placement = pos=(0,0,36.15) rot=(0,0,1;0rad)
  Solid = false
  Source = -> Face124
  Symmetric = false
FEATURE [Part::MultiFuse] Fusion101  label="plugHousing055"
  Placement = pos=(0,0,0) rot=(0,0,1;1.5708rad)
  Shapes = -> [Revolve129,Revolve134]
FEATURE [Part::MultiFuse] Fusion098  label="plugHousing052"
  Placement = pos=(0,19,0) rot=(0,0,1;3.14159rad)
  Shapes = -> [Fusion097,Fusion101]
FEATURE [Part::MultiFuse] Fusion103  label="plugHousing057"
  Placement = pos=(122.621,0,-0.15) rot=(0,0,1;0rad)
  Shapes = -> [Fusion102,Fusion098]
FEATURE [Part::Box] Box028  label="Cube015"
  AttacherType = Attacher::AttachEngine3D
  Height = 28
  Length = 3
  Placement = pos=(110.7,19,22) rot=(0,0,1;0rad)
  Width = 15.7
FEATURE [Part::Cylinder] Cylinder044
  Angle = 360
  AttacherType = Attacher::AttachEngine3D
  Height = 20
  Placement = pos=(0,0,36.15) rot=(0,0,1;0rad)
  Radius = 10.3
FEATURE [Part::Cylinder] Cylinder045
  Angle = 360
  AttacherType = Attacher::AttachEngine3D
  Height = 10
  Placement = pos=(0,0,36.15) rot=(0,0,1;0rad)
  Radius = 4
FEATURE [Part::MultiFuse] Fusion104  label="removeToCreteHoleForPlugHousing040"
  Placement = pos=(70,19,36) rot=(0,1,0;1.5708rad)
  Shapes = -> [Cylinder044,Cylinder045]
FEATURE [Part::Cut] Cut046  label="plugHousingTab003"
  Base = -> Box028
  Tool = -> Fusion104
FEATURE [Part::MultiFuse] Fusion105  label="plugHousing062"
  Shapes = -> [Fusion103,Cut046]
FEATURE [Part::Fillet] Fillet042
  Base = -> Fusion105
  Edges = 1 edges r=2: [Edge25]
FEATURE [Part::Fillet] Fillet043  label="plugHousing063"
  Base = -> Fillet042
  Edges = 1 edges r=2: [Edge8]
  Placement = pos=(7,0,0) rot=(0,0,1;0rad)
FEATURE [Part::Feature] Face127
  shape: bbox 10 x 16.5 x 2e-07 mm, 1 faces, 0 solids (baked)
FEATURE [Part::Feature] Face128
  shape: bbox 10 x 16.5 x 2e-07 mm, 1 faces, 0 solids (baked)
FEATURE [Part::Revolution] Revolve137  label="plugHousing070"
  Angle = 360
  Axis = (0,1,0)
  Base = (0,0,0)
  FaceMakerClass = Part::FaceMakerBullseye
  Placement = pos=(0,0,36.15) rot=(0,0,1;0rad)
  Solid = false
  Source = -> Face127
  Symmetric = false
FEATURE [Part::Revolution] Revolve140  label="plugHousing073"
  Angle = 360
  Axis = (0,1,0)
  Base = (0,0,0)
  FaceMakerClass = Part::FaceMakerBullseye
  Placement = pos=(0,0,36.15) rot=(0,0,1;0rad)
  Solid = false
  Source = -> Face128
  Symmetric = false
FEATURE [Part::Feature] Face129
  shape: bbox 10 x 16.5 x 2e-07 mm, 1 faces, 0 solids (baked)
FEATURE [Part::Revolution] Revolve138  label="plugHousing071"
  Angle = 360
  Axis = (0,1,0)
  Base = (0,0,0)
  FaceMakerClass = Part::FaceMakerBullseye
  Placement = pos=(0,0,36.15) rot=(0,0,1;0rad)
  Solid = false
  Source = -> Face129
  Symmetric = false
FEATURE [Part::Feature] Face130
  shape: bbox 10 x 16.5 x 2e-07 mm, 1 faces, 0 solids (baked)
FEATURE [Part::Revolution] Revolve139  label="plugHousing072"
  Angle = 360
  Axis = (0,1,0)
  Base = (0,0,0)
  FaceMakerClass = Part::FaceMakerBullseye
  Placement = pos=(0,0,36.15) rot=(0,0,1;0rad)
  Solid = false
  Source = -> Face130
  Symmetric = false
FEATURE [Part::Feature] Face131
  shape: bbox 10 x 16.5 x 2e-07 mm, 1 faces, 0 solids (baked)
FEATURE [Part::Revolution] Revolve135  label="plugHousing068"
  Angle = 360
  Axis = (0,1,0)
  Base = (0,0,0)
  FaceMakerClass = Part::FaceMakerBullseye
  Placement = pos=(0,0,36.15) rot=(0,0,1;0rad)
  Solid = false
  Source = -> Face131
  Symmetric = false
FEATURE [Part::MultiFuse] Fusion112  label="plugHousing078"
  Placement = pos=(0,0,0) rot=(0,0,1;1.5708rad)
  Shapes = -> [Revolve135,Revolve139]
FEATURE [Part::Feature] Face132
  shape: bbox 10 x 16.5 x 2e-07 mm, 1 faces, 0 solids (baked)
FEATURE [Part::Revolution] Revolve141  label="plugHousing074"
  Angle = 360
  Axis = (0,1,0)
  Base = (0,0,0)
  FaceMakerClass = Part::FaceMakerBullseye
  Placement = pos=(0,0,36.15) rot=(0,0,1;0rad)
  Solid = false
  Source = -> Face132
  Symmetric = false
FEATURE [Part::MultiFuse] Fusion110  label="plugHousing076"
  Placement = pos=(0,0,0) rot=(0,0,1;1.5708rad)
  Shapes = -> [Revolve141,Revolve140]
FEATURE [Part::Feature] Face133
  shape: bbox 10 x 16.5 x 2e-07 mm, 1 faces, 0 solids (baked)
FEATURE [Part::Revolution] Revolve136  label="plugHousing069"
  Angle = 360
  Axis = (0,1,0)
  Base = (0,0,0)
  FaceMakerClass = Part::FaceMakerBullseye
  Placement = pos=(0,0,36.15) rot=(0,0,1;0rad)
  Solid = false
  Source = -> Face133
  Symmetric = false
FEATURE [Part::MultiFuse] Fusion106  label="plugHousing064"
  Placement = pos=(0,0,0) rot=(0,0,1;1.5708rad)
  Shapes = -> [Revolve138,Revolve136]
FEATURE [Part::MultiFuse] Fusion108  label="plugHousing066"
  Placement = pos=(0,19,0) rot=(0,0,1;3.14159rad)
  Shapes = -> [Fusion106,Fusion112]
FEATURE [Part::Feature] Face134
  shape: bbox 10 x 16.5 x 2e-07 mm, 1 faces, 0 solids (baked)
FEATURE [Part::Revolution] Revolve142  label="plugHousing075"
  Angle = 360
  Axis = (0,1,0)
  Base = (0,0,0)
  FaceMakerClass = Part::FaceMakerBullseye
  Placement = pos=(0,0,36.15) rot=(0,0,1;0rad)
  Solid = false
  Source = -> Face134
  Symmetric = false
FEATURE [Part::MultiFuse] Fusion107  label="plugHousing065"
  Placement = pos=(0,0,0) rot=(0,0,1;1.5708rad)
  Shapes = -> [Revolve137,Revolve142]
FEATURE [Part::MultiFuse] Fusion111  label="plugHousing077"
  Placement = pos=(0,19,0) rot=(0,0,1;3.14159rad)
  Shapes = -> [Fusion110,Fusion107]
FEATURE [Part::MultiFuse] Fusion109  label="plugHousing067"
  Placement = pos=(131.236,0,-0.15) rot=(0,0,1;0rad)
  Shapes = -> [Fusion108,Fusion111]
FEATURE [Part::MultiFuse] Fusion113  label="plugHousing079"
  Shapes = -> [Fillet043,Fusion109]
FEATURE [Part::Feature] Face135
  shape: bbox 3.5 x 17.8 x 2e-07 mm, 1 faces, 0 solids (baked)
FEATURE [Part::Revolution] Revolve143  label="removeToCreateScrewAndThreadedInsertHole049"
  Angle = 360
  Axis = (0,1,0)
  Base = (0,0,0)
  FaceMakerClass = Part::FaceMakerBullseye
  Placement = pos=(12.5,0,10) rot=(0,0,1;0rad)
  Solid = false
  Source = -> Face135
  Symmetric = false
FEATURE [Part::Feature] Face136
  shape: bbox 3.5 x 17.8 x 2e-07 mm, 1 faces, 0 solids (baked)
FEATURE [Part::Revolution] Revolve144  label="removeToCreateScrewAndThreadedInsertHole050"
  Angle = 360
  Axis = (0,1,0)
  Base = (0,0,0)
  FaceMakerClass = Part::FaceMakerBullseye
  Placement = pos=(12.5,0,62) rot=(0,0,1;0rad)
  Solid = false
  Source = -> Face136
  Symmetric = false
FEATURE [Part::Feature] Face137
  shape: bbox 3.5 x 17.8 x 2e-07 mm, 1 faces, 0 solids (baked)
FEATURE [Part::Revolution] Revolve145  label="removeToCreateScrewAndThreadedInsertHole051"
  Angle = 360
  Axis = (0,1,0)
  Base = (0,0,0)
  FaceMakerClass = Part::FaceMakerBullseye
  Placement = pos=(89.5,0,68.5) rot=(0,0,1;0rad)
  Solid = false
  Source = -> Face137
  Symmetric = false
FEATURE [Part::Feature] Face138
  shape: bbox 3.5 x 17.8 x 2e-07 mm, 1 faces, 0 solids (baked)
FEATURE [Part::Revolution] Revolve146  label="removeToCreateScrewAndThreadedInsertHole052"
  Angle = 360
  Axis = (0,1,0)
  Base = (0,0,0)
  FaceMakerClass = Part::FaceMakerBullseye
  Placement = pos=(89.5,0,3.5) rot=(0,0,1;0rad)
  Solid = false
  Source = -> Face138
  Symmetric = false
FEATURE [Part::Feature] Face139
  shape: bbox 3.5 x 17.8 x 2e-07 mm, 1 faces, 0 solids (baked)
FEATURE [Part::Revolution] Revolve147  label="removeToCreateScrewAndThreadedInsertHole053"
  Angle = 360
  Axis = (0,1,0)
  Base = (0,0,0)
  FaceMakerClass = Part::FaceMakerBullseye
  Placement = pos=(109.5,4.7,3.5) rot=(0,0,1;0rad)
  Solid = false
  Source = -> Face139
  Symmetric = false
FEATURE [Part::Feature] Face140
  shape: bbox 3.5 x 17.8 x 2e-07 mm, 1 faces, 0 solids (baked)
FEATURE [Part::Revolution] Revolve148  label="removeToCreateScrewAndThreadedInsertHole054"
  Angle = 360
  Axis = (0,1,0)
  Base = (0,0,0)
  FaceMakerClass = Part::FaceMakerBullseye
  Placement = pos=(109.5,4.7,68.5) rot=(0,0,1;0rad)
  Solid = false
  Source = -> Face140
  Symmetric = false
FEATURE [Part::MultiFuse] Fusion114  label="removeToCreateScrewAndThreadedInsertHole055"
  Shapes = -> [Revolve148,Revolve147,Revolve146,Revolve145,Revolve144,Revolve143]
FEATURE [Part::Cut] Cut047  label="casePillars004"
  Base = -> Cut037
  Tool = -> Fusion114
FEATURE [Part::Feature] Face141
  shape: bbox 3.5 x 17.8 x 2e-07 mm, 1 faces, 0 solids (baked)
FEATURE [Part::Feature] Face142
  shape: bbox 3.5 x 17.8 x 2e-07 mm, 1 faces, 0 solids (baked)
FEATURE [Part::Feature] Face143
  shape: bbox 3.5 x 17.8 x 2e-07 mm, 1 faces, 0 solids (baked)
FEATURE [Part::Revolution] Revolve149  label="removeToCreateScrewAndThreadedInsertHole057"
  Angle = 360
  Axis = (0,1,0)
  Base = (0,0,0)
  FaceMakerClass = Part::FaceMakerBullseye
  Placement = pos=(12.5,0,10) rot=(0,0,1;0rad)
  Solid = false
  Source = -> Face141
  Symmetric = false
FEATURE [Part::Feature] Face144
  shape: bbox 3.5 x 17.8 x 2e-07 mm, 1 faces, 0 solids (baked)
FEATURE [Part::Feature] Face145
  shape: bbox 3.5 x 17.8 x 2e-07 mm, 1 faces, 0 solids (baked)
FEATURE [Part::Feature] Face146
  shape: bbox 3.5 x 17.8 x 2e-07 mm, 1 faces, 0 solids (baked)
FEATURE [Part::Revolution] Revolve150  label="removeToCreateScrewAndThreadedInsertHole058"
  Angle = 360
  Axis = (0,1,0)
  Base = (0,0,0)
  FaceMakerClass = Part::FaceMakerBullseye
  Placement = pos=(12.5,0,62) rot=(0,0,1;0rad)
  Solid = false
  Source = -> Face146
  Symmetric = false
FEATURE [Part::Revolution] Revolve151  label="removeToCreateScrewAndThreadedInsertHole059"
  Angle = 360
  Axis = (0,1,0)
  Base = (0,0,0)
  FaceMakerClass = Part::FaceMakerBullseye
  Placement = pos=(89.5,0,68.5) rot=(0,0,1;0rad)
  Solid = false
  Source = -> Face143
  Symmetric = false
FEATURE [Part::Revolution] Revolve152  label="removeToCreateScrewAndThreadedInsertHole060"
  Angle = 360
  Axis = (0,1,0)
  Base = (0,0,0)
  FaceMakerClass = Part::FaceMakerBullseye
  Placement = pos=(89.5,0,3.5) rot=(0,0,1;0rad)
  Solid = false
  Source = -> Face142
  Symmetric = false
FEATURE [Part::Revolution] Revolve153  label="removeToCreateScrewAndThreadedInsertHole061"
  Angle = 360
  Axis = (0,1,0)
  Base = (0,0,0)
  FaceMakerClass = Part::FaceMakerBullseye
  Placement = pos=(109.5,4.7,3.5) rot=(0,0,1;0rad)
  Solid = false
  Source = -> Face145
  Symmetric = false
FEATURE [Part::Revolution] Revolve154  label="removeToCreateScrewAndThreadedInsertHole062"
  Angle = 360
  Axis = (0,1,0)
  Base = (0,0,0)
  FaceMakerClass = Part::FaceMakerBullseye
  Placement = pos=(109.5,4.7,68.5) rot=(0,0,1;0rad)
  Solid = false
  Source = -> Face144
  Symmetric = false
FEATURE [Part::MultiFuse] Fusion115  label="removeToCreateScrewAndThreadedInsertHole056"
  Shapes = -> [Revolve154,Revolve153,Revolve152,Revolve151,Revolve150,Revolve149]
FEATURE [Part::Feature] Face147
  shape: bbox 9.8 x 26.5 x 2e-07 mm, 1 faces, 0 solids (baked)
FEATURE [Part::Revolution] Revolve155
  Angle = 360
  Axis = (0,1,0)
  Base = (0,0,0)
  FaceMakerClass = Part::FaceMakerBullseye
  Placement = pos=(0,0,0) rot=(0,0,1;1.5708rad)
  Solid = false
  Source = -> Face147
  Symmetric = false
FEATURE [Part::Feature] Face148
  shape: bbox 9.8 x 26.5 x 2e-07 mm, 1 faces, 0 solids (baked)
FEATURE [Part::Revolution] Revolve156
  Angle = 360
  Axis = (0,1,0)
  Base = (0,0,0)
  FaceMakerClass = Part::FaceMakerBullseye
  Placement = pos=(0,0,0) rot=(0,0,1;1.5708rad)
  Solid = false
  Source = -> Face148
  Symmetric = false
FEATURE [Part::MultiFuse] Fusion116
  Placement = pos=(-18,19,36) rot=(0,0,1;0rad)
  Shapes = -> [Revolve156,Revolve155]
FEATURE [Part::Box] Box029  label="Cube016"
  AttacherType = Attacher::AttachEngine3D
  Height = 28
  Length = 3
  Placement = pos=(110.7,19,22) rot=(0,0,1;0rad)
  Width = 15.7
FEATURE [Part::Cylinder] Cylinder046
  Angle = 360
  AttacherType = Attacher::AttachEngine3D
  Height = 10
  Placement = pos=(0,0,36.15) rot=(0,0,1;0rad)
  Radius = 4
FEATURE [Part::Cylinder] Cylinder047
  Angle = 360
  AttacherType = Attacher::AttachEngine3D
  Height = 20
  Placement = pos=(0,0,36.15) rot=(0,0,1;0rad)
  Radius = 10.3
FEATURE [Part::MultiFuse] Fusion117  label="removeToCreteHoleForPlugHousing041"
  Placement = pos=(70,19,36) rot=(0,1,0;1.5708rad)
  Shapes = -> [Cylinder047,Cylinder046]
FEATURE [Part::Cut] Cut049  label="plugHousingTab004"
  Base = -> Box029
  Placement = pos=(-107.4,-14,0) rot=(0,0,1;0rad)
  Tool = -> Fusion117
FEATURE [Part::Box] Box030  label="Cube017"
  AttacherType = Attacher::AttachEngine3D
  Height = 28
  Length = 3
  Placement = pos=(110.7,19,22) rot=(0,0,1;0rad)
  Width = 15.7
FEATURE [Part::Cylinder] Cylinder048
  Angle = 360
  AttacherType = Attacher::AttachEngine3D
  Height = 10
  Placement = pos=(0,0,36.15) rot=(0,0,1;0rad)
  Radius = 4
FEATURE [Part::Cylinder] Cylinder049
  Angle = 360
  AttacherType = Attacher::AttachEngine3D
  Height = 20
  Placement = pos=(0,0,36.15) rot=(0,0,1;0rad)
  Radius = 10.3
FEATURE [Part::MultiFuse] Fusion118  label="removeToCreteHoleForPlugHousing042"
  Placement = pos=(70,19,36) rot=(0,1,0;1.5708rad)
  Shapes = -> [Cylinder049,Cylinder048]
FEATURE [Part::Cut] Cut050  label="plugHousingTab005"
  Base = -> Box030
  Placement = pos=(-107.4,-14,0) rot=(0,0,1;0rad)
  Tool = -> Fusion118
FEATURE [Part::MultiFuse] Fusion119
  Placement = pos=(9.6,23,0) rot=(0,0,1;3.14159rad)
  Shapes = -> [Cut049,Cut050]
FEATURE [Part::Box] Box031  label="Cube018"
  AttacherType = Attacher::AttachEngine3D
  Height = 10
  Length = 3
  Placement = pos=(3.3,4,12) rot=(0,0,1;0rad)
  Width = 10
FEATURE [Part::Fillet] Fillet044
  Base = -> Box031
  Edges = 1 edges r=2: [Edge11]
FEATURE [Part::Box] Box032  label="Cube019"
  AttacherType = Attacher::AttachEngine3D
  Height = 10
  Length = 3
  Placement = pos=(3.3,4,50) rot=(0,0,1;0rad)
  Width = 10
FEATURE [Part::Fillet] Fillet045
  Base = -> Box032
  Edges = 1 edges r=2: [Edge12]
FEATURE [Part::Box] Box033  label="Cube020"
  AttacherType = Attacher::AttachEngine3D
  Height = 28
  Length = 4
  Placement = pos=(5,0,22) rot=(0,0,1;0rad)
  Width = 10
FEATURE [Part::Fillet] Fillet046
  Base = -> Box033
  Edges = 1 edges r=1: [Edge7]
FEATURE [Part::Fillet] Fillet047
  Base = -> Fillet046
  Edges = 1 edges r=2: [Edge5]
FEATURE [Part::Fillet] Fillet048
  Base = -> Fillet047
  Edges = 1 edges r=2: [Edge2]
FEATURE [Part::Cylinder] Cylinder050
  Angle = 360
  AttacherType = Attacher::AttachEngine3D
  Height = 20
  Placement = pos=(0,0,36.15) rot=(0,0,1;0rad)
  Radius = 8.2
FEATURE [Part::Cylinder] Cylinder051
  Angle = 360
  AttacherType = Attacher::AttachEngine3D
  Height = 10
  Placement = pos=(0,0,36.15) rot=(0,0,1;0rad)
  Radius = 4
FEATURE [Part::MultiFuse] Fusion120  label="removeToCreteHoleForPlugHousing043"
  Placement = pos=(-42,19,36) rot=(0,1,0;1.5708rad)
  Shapes = -> [Cylinder050,Cylinder051]
FEATURE [Sketcher::SketchObject] Sketch067  label="topSketch018"
  FullyConstrained = true
  sketch-geometry (4):
    g0: LineSegment StartX=16.8446 StartY=31.512 StartZ=0 EndX=16.3251 EndY=34.4666 EndZ=0
    g1: ArcOfCircle CenterX=19 CenterY=19.2524 CenterZ=0 NormalX=0 NormalY=0 NormalZ=1 AngleXU=0 Radius=15.4476 StartAngle=1.74483 EndAngle=2.72717
    g2: ArcOfCircle CenterX=19 CenterY=19.2524 CenterZ=0 NormalX=0 NormalY=0 NormalZ=1 AngleXU=0 Radius=12.4476 StartAngle=1.74483 EndAngle=2.73189
    g3: LineSegment StartX=4.86004 StartY=25.4725 StartZ=0 EndX=7.58253 EndY=24.2107 EndZ=0
  constraints (7):
    c: Block(g0)
    c: Coincident(g1,g0)
    c: Coincident(g2,g0)
    c: Coincident(g3,g1)
    c: Coincident(g3,g2)
    c: Block(g1)
    c: Block(g2)
FEATURE [Part::Extrusion] Extrude058
  Base = -> Sketch067
  Dir = (0,0,1)
  DirMode = 2
  FaceMakerClass = Part::FaceMakerBullseye
  LengthFwd = 10
  LengthRev = 0
  Placement = pos=(0,0,31) rot=(0,0,1;0rad)
  Solid = true
  Symmetric = false
FEATURE [Part::Cut] Cut051
  Base = -> Extrude058
  Tool = -> Fusion120
FEATURE [Part::Fillet] Fillet049
  Base = -> Cut051
  Edges = 1 edges r=2: [Edge1]
FEATURE [Part::Fillet] Fillet050
  Base = -> Fillet049
  Edges = 1 edges r=2.5: [Edge1]
FEATURE [Part::Fillet] Fillet051
  Base = -> Fillet050
  Edges = 1 edges r=2.5: [Edge2]
FEATURE [Part::MultiFuse] Fusion121  label="wireHolder003"
  Shapes = -> [Fusion116,Fillet051]
FEATURE [Part::MultiFuse] Fusion122
  Shapes = -> [Fillet045,Fusion121]
FEATURE [Part::MultiFuse] Fusion123  label="wireHolder004"
  Shapes = -> [Fusion122,Fillet048]
FEATURE [Part::MultiFuse] Fusion124  label="wireHolder005"
  Shapes = -> [Fillet044,Fusion119,Fusion123]
FEATURE [Sketcher::SketchObject] Sketch068  label="topSketch019"
  FullyConstrained = true
  sketch-geometry (6):
    g0: LineSegment StartX=19 StartY=38 StartZ=0 EndX=117 EndY=38 EndZ=0
    g1: ArcOfCircle CenterX=19 CenterY=19 CenterZ=0 NormalX=0 NormalY=0 NormalZ=1 AngleXU=0 Radius=19 StartAngle=1.5708 EndAngle=3.14159
    g2: LineSegment StartX=117 StartY=38 StartZ=0 EndX=117 EndY=19 EndZ=0
    g3: LineSegment StartX=98 StartY=1.0161e-12 StartZ=0 EndX=5.22862e-06 EndY=1.0161e-12 EndZ=0
    g4: LineSegment StartX=5.22862e-06 StartY=19 StartZ=0 EndX=5.22862e-06 EndY=1.0161e-12 EndZ=0
    g5: ArcOfCircle CenterX=98 CenterY=19 CenterZ=0 NormalX=0 NormalY=0 NormalZ=1 AngleXU=0 Radius=19 StartAngle=4.71239 EndAngle=6.28319
  constraints (16):
    c: Horizontal(g0)
    c: Distance(g0) = 98
    c: Coincident(g1,g0)
    c: Block(g1)
    c: Coincident(g2,g0)
    c: Vertical(g2)
    c: Distance(g2) = 19
    c: Horizontal(g3)
    c: Coincident(g4,g1)
    c: Vertical(g4)
    c: Coincident(g3,g4)
    c: Block(g3)
    c: Coincident(g5,g2)
    c: Coincident(g5,g3)
    c: Block(g0)
    c: Block(g5)
FEATURE [Part::Extrusion] Extrude059  label="sideA002"
  Base = -> Sketch068
  Dir = (0,0,1)
  DirMode = 2
  FaceMakerClass = Part::FaceMakerBullseye
  LengthFwd = 3
  LengthRev = 0
  Placement = pos=(0,0,-2.7) rot=(0,0,1;0rad)
  Solid = true
  Symmetric = false
FEATURE [Sketcher::SketchObject] Sketch069  label="topSketch020"
  FullyConstrained = true
  sketch-geometry (6):
    g0: LineSegment StartX=19 StartY=38 StartZ=0 EndX=117 EndY=38 EndZ=0
    g1: ArcOfCircle CenterX=19 CenterY=19 CenterZ=0 NormalX=0 NormalY=0 NormalZ=1 AngleXU=0 Radius=19 StartAngle=1.5708 EndAngle=3.14159
    g2: LineSegment StartX=117 StartY=38 StartZ=0 EndX=117 EndY=19 EndZ=0
    g3: LineSegment StartX=98 StartY=1.0161e-12 StartZ=0 EndX=5.22862e-06 EndY=1.0161e-12 EndZ=0
    g4: LineSegment StartX=5.22862e-06 StartY=19 StartZ=0 EndX=5.22862e-06 EndY=1.0161e-12 EndZ=0
    g5: ArcOfCircle CenterX=98 CenterY=19 CenterZ=0 NormalX=0 NormalY=0 NormalZ=1 AngleXU=0 Radius=19 StartAngle=4.71239 EndAngle=6.28319
  constraints (16):
    c: Horizontal(g0)
    c: Distance(g0) = 98
    c: Coincident(g1,g0)
    c: Block(g1)
    c: Coincident(g2,g0)
    c: Vertical(g2)
    c: Distance(g2) = 19
    c: Horizontal(g3)
    c: Coincident(g4,g1)
    c: Vertical(g4)
    c: Coincident(g3,g4)
    c: Block(g3)
    c: Coincident(g5,g2)
    c: Coincident(g5,g3)
    c: Block(g0)
    c: Block(g5)
FEATURE [Part::Extrusion] Extrude060  label="sideB002"
  Base = -> Sketch069
  Dir = (0,0,1)
  DirMode = 2
  FaceMakerClass = Part::FaceMakerBullseye
  LengthFwd = 3
  LengthRev = 0
  Placement = pos=(0,0,71.7) rot=(0,0,1;0rad)
  Solid = true
  Symmetric = false
FEATURE [Part::MultiFuse] Fusion127  label="removeFromBottom001"
  Placement = pos=(2,0,0) rot=(0,0,1;0rad)
  Shapes = -> [Extrude059,Extrude060]
FEATURE [Part::Cylinder] Cylinder052
  Angle = 360
  AttacherType = Attacher::AttachEngine3D
  Height = 20
  Placement = pos=(0,0,36.15) rot=(0,0,1;0rad)
  Radius = 14
FEATURE [Part::Cylinder] Cylinder053
  Angle = 360
  AttacherType = Attacher::AttachEngine3D
  Height = 10
  Placement = pos=(0,0,36.15) rot=(0,0,1;0rad)
  Radius = 4
FEATURE [Part::MultiFuse] Fusion128  label="removeToCreteHoleForPlugHousing044"
  Placement = pos=(70,19,36) rot=(0,1,0;1.5708rad)
  Shapes = -> [Cylinder052,Cylinder053]
FEATURE [Part::Cut] Cut052  label="bottom011"
  Base = -> Extrude043
  Tool = -> Fusion128
FEATURE [Part::Cut] Cut054  label="bottom012"
  Base = -> Cut052
  Tool = -> Fusion115
FEATURE [Sketcher::SketchObject] Sketch070
  FullyConstrained = true
  Placement = pos=(117,19,0) rot=(0.57735,0.57735,0.57735;2.0944rad)
  sketch-geometry (48):
    g0: LineSegment StartX=-49.19 StartY=69.25 StartZ=0 EndX=-49.19 EndY=66.25 EndZ=0
    g1: LineSegment StartX=-49.19 StartY=63.5 StartZ=0 EndX=-49.19 EndY=60.5 EndZ=0
    g2: LineSegment StartX=-49.19 StartY=57.75 StartZ=0 EndX=-49.19 EndY=54.75 EndZ=0
    g3: LineSegment StartX=-49.19 StartY=52 StartZ=0 EndX=-49.19 EndY=49 EndZ=0
    g4: LineSegment StartX=-49.19 StartY=46.25 StartZ=0 EndX=-49.19 EndY=43.25 EndZ=0
    g5: LineSegment StartX=-49.19 StartY=40.5 StartZ=0 EndX=-49.19 EndY=37.5 EndZ=0
    g6: LineSegment StartX=-49.19 StartY=34.5 StartZ=0 EndX=-49.19 EndY=31.5 EndZ=0
    g7: LineSegment StartX=-49.19 StartY=28.75 StartZ=0 EndX=-49.19 EndY=25.75 EndZ=0
    g8: LineSegment StartX=-49.19 StartY=23 StartZ=0 EndX=-49.19 EndY=20 EndZ=0
    g9: LineSegment StartX=-49.19 StartY=17.25 StartZ=0 EndX=-49.19 EndY=14.25 EndZ=0
    g10: LineSegment StartX=-49.19 StartY=11.5 StartZ=0 EndX=-49.19 EndY=8.5 EndZ=0
    g11: LineSegment StartX=-49.19 StartY=5.75 StartZ=0 EndX=-49.19 EndY=2.75 EndZ=0
    g12: ArcOfCircle CenterX=-1.5 CenterY=67.75 CenterZ=0 NormalX=0 NormalY=0 NormalZ=1 AngleXU=0 Radius=1.5 StartAngle=4.71239 EndAngle=7.85398
    g13: ArcOfCircle CenterX=-1.5 CenterY=62 CenterZ=0 NormalX=0 NormalY=0 NormalZ=1 AngleXU=0 Radius=1.5 StartAngle=4.71239 EndAngle=7.85398
    g14: ArcOfCircle CenterX=-1.5 CenterY=56.25 CenterZ=0 NormalX=0 NormalY=0 NormalZ=1 AngleXU=0 Radius=1.5 StartAngle=4.71239 EndAngle=7.85398
    g15: ArcOfCircle CenterX=-11.49 CenterY=50.5 CenterZ=0 NormalX=0 NormalY=0 NormalZ=1 AngleXU=0 Radius=1.5 StartAngle=4.71239 EndAngle=7.85398
    g16: ArcOfCircle CenterX=-16.28 CenterY=44.75 CenterZ=0 NormalX=0 NormalY=0 NormalZ=1 AngleXU=0 Radius=1.5 StartAngle=4.71239 EndAngle=7.85398
    g17: ArcOfCircle CenterX=-18.2337 CenterY=39 CenterZ=0 NormalX=0 NormalY=0 NormalZ=1 AngleXU=0 Radius=1.5 StartAngle=4.71485 EndAngle=7.85398
    g18: ArcOfCircle CenterX=-16.2837 CenterY=27.25 CenterZ=0 NormalX=0 NormalY=0 NormalZ=1 AngleXU=0 Radius=1.5 StartAngle=4.71485 EndAngle=7.85398
    g19: ArcOfCircle CenterX=-18.2337 CenterY=33 CenterZ=0 NormalX=0 NormalY=0 NormalZ=1 AngleXU=0 Radius=1.5 StartAngle=4.71485 EndAngle=7.85398
    g20: ArcOfCircle CenterX=-11.49 CenterY=21.5 CenterZ=0 NormalX=0 NormalY=0 NormalZ=1 AngleXU=0 Radius=1.5 StartAngle=4.71239 EndAngle=7.85398
    g21: ArcOfCircle CenterX=-1.5 CenterY=4.25 CenterZ=0 NormalX=0 NormalY=0 NormalZ=1 AngleXU=0 Radius=1.5 StartAngle=4.71239 EndAngle=7.85398
    g22: ArcOfCircle CenterX=-1.5 CenterY=10 CenterZ=0 NormalX=0 NormalY=0 NormalZ=1 AngleXU=0 Radius=1.5 StartAngle=4.71239 EndAngle=7.85398
    g23: ArcOfCircle CenterX=-1.5 CenterY=15.75 CenterZ=0 NormalX=0 NormalY=0 NormalZ=1 AngleXU=0 Radius=1.5 StartAngle=4.71239 EndAngle=7.85398
    g24: LineSegment StartX=-49.19 StartY=69.25 StartZ=0 EndX=-1.5 EndY=69.25 EndZ=0
    g25: LineSegment StartX=-49.19 StartY=66.25 StartZ=0 EndX=-1.5 EndY=66.25 EndZ=0
    g26: LineSegment StartX=-49.19 StartY=63.5 StartZ=0 EndX=-1.5 EndY=63.5 EndZ=0
    g27: LineSegment StartX=-49.19 StartY=60.5 StartZ=0 EndX=-1.5 EndY=60.5 EndZ=0
    g28: LineSegment StartX=-49.19 StartY=57.75 StartZ=0 EndX=-1.5 EndY=57.75 EndZ=0
    g29: LineSegment StartX=-49.19 StartY=54.75 StartZ=0 EndX=-1.5 EndY=54.75 EndZ=0
    g30: LineSegment StartX=-49.19 StartY=52 StartZ=0 EndX=-11.49 EndY=52 EndZ=0
    g31: LineSegment StartX=-49.19 StartY=49 StartZ=0 EndX=-11.49 EndY=49 EndZ=0
    g32: LineSegment StartX=-49.19 StartY=46.25 StartZ=0 EndX=-16.28 EndY=46.25 EndZ=0
    g33: LineSegment StartX=-49.19 StartY=43.25 StartZ=0 EndX=-16.28 EndY=43.25 EndZ=0
    g34: LineSegment StartX=-49.19 StartY=40.5 StartZ=0 EndX=-18.2337 EndY=40.5 EndZ=0
    g35: LineSegment StartX=-49.19 StartY=37.5 StartZ=0 EndX=-18.23 EndY=37.5 EndZ=0
    g36: LineSegment StartX=-49.19 StartY=34.5 StartZ=0 EndX=-18.2337 EndY=34.5 EndZ=0
    g37: LineSegment StartX=-49.19 StartY=31.5 StartZ=0 EndX=-18.23 EndY=31.5 EndZ=0
    g38: LineSegment StartX=-49.19 StartY=28.75 StartZ=0 EndX=-16.2837 EndY=28.75 EndZ=0
    g39: LineSegment StartX=-49.19 StartY=25.75 StartZ=0 EndX=-16.28 EndY=25.75 EndZ=0
    g40: LineSegment StartX=-49.19 StartY=23 StartZ=0 EndX=-11.49 EndY=23 EndZ=0
    g41: LineSegment StartX=-49.19 StartY=20 StartZ=0 EndX=-11.49 EndY=20 EndZ=0
    g42: LineSegment StartX=-49.19 StartY=17.25 StartZ=0 EndX=-1.5 EndY=17.25 EndZ=0
    g43: LineSegment StartX=-49.19 StartY=14.25 StartZ=0 EndX=-1.5 EndY=14.25 EndZ=0
    g44: LineSegment StartX=-49.19 StartY=11.5 StartZ=0 EndX=-1.5 EndY=11.5 EndZ=0
    g45: LineSegment StartX=-49.19 StartY=8.5 StartZ=0 EndX=-1.5 EndY=8.5 EndZ=0
    g46: LineSegment StartX=-49.19 StartY=5.75 StartZ=0 EndX=-1.5 EndY=5.75 EndZ=0
    g47: LineSegment StartX=-49.19 StartY=2.75 StartZ=0 EndX=-1.5 EndY=2.75 EndZ=0
  constraints (120):
    c: Vertical(g0)
    c: Distance(g0) = 3
    c: Block(g0)
    c: Vertical(g1)
    c: Distance(g1) = 3
    c: Vertical(g2)
    c: Equal(g0,g2) = 3
    c: Block(g2)
    c: Vertical(g3)
    c: Equal(g1,g3) = 3
    c: Vertical(g4)
    c: Equal(g0,g4) = 3
    c: Block(g4)
    c: Vertical(g5)
    c: Equal(g1,g5) = 3
    c: Vertical(g6)
    c: Equal(g0,g6) = 3
    c: Block(g6)
    c: Vertical(g7)
    c: Equal(g1,g7) = 3
    c: Vertical(g8)
    c: Equal(g0,g8) = 3
    c: Block(g8)
    c: Vertical(g9)
    c: Equal(g1,g9) = 3
    c: Vertical(g10)
    c: Equal(g0,g10) = 3
    c: Block(g10)
    c: Vertical(g11)
    c: Equal(g1,g11) = 3
    c: Block(g12)
    c: Block(g13)
    c: Block(g14)
    c: Block(g15)
    c: Block(g16)
    c: Block(g17)
    c: Block(g18)
    c: Block(g19)
    c: Block(g20)
    c: Block(g21)
    c: Block(g22)
    c: Block(g23)
    c: Block(g11)
    c: Block(g9)
    c: Block(g7)
    c: Block(g5)
    c: Block(g3)
    c: Block(g1)
    c: Coincident(g24,g0)
    c: Coincident(g24,g12)
    c: Horizontal(g24)
    c: Coincident(g25,g0)
    c: Coincident(g25,g12)
    c: Horizontal(g25)
    c: Coincident(g26,g1)
    c: Coincident(g26,g13)
    c: Horizontal(g26)
    c: Coincident(g27,g1)
    c: Coincident(g27,g13)
    c: Horizontal(g27)
    c: Coincident(g28,g2)
    c: Coincident(g28,g14)
    c: Horizontal(g28)
    c: Coincident(g29,g2)
    c: Coincident(g29,g14)
    c: Horizontal(g29)
    c: Coincident(g30,g3)
    c: Coincident(g30,g15)
    c: Horizontal(g30)
    c: Coincident(g31,g3)
    c: Coincident(g31,g15)
    c: Horizontal(g31)
    c: Coincident(g32,g4)
    c: Coincident(g32,g16)
    c: Horizontal(g32)
    c: Coincident(g33,g4)
    c: Coincident(g33,g16)
    c: Horizontal(g33)
    c: Coincident(g34,g5)
    c: Coincident(g34,g17)
    c: Horizontal(g34)
    c: Coincident(g35,g5)
    c: Coincident(g35,g17)
    c: Horizontal(g35)
    c: Coincident(g36,g6)
    c: Coincident(g36,g19)
    c: Horizontal(g36)
    c: Coincident(g37,g6)
    c: Coincident(g37,g19)
    c: Horizontal(g37)
    c: Coincident(g38,g7)
    c: Coincident(g38,g18)
    c: Horizontal(g38)
    c: Coincident(g39,g7)
    c: Coincident(g39,g18)
    c: Horizontal(g39)
    c: Coincident(g40,g8)
    c: Coincident(g40,g20)
    c: Horizontal(g40)
    c: Coincident(g41,g8)
    c: Coincident(g41,g20)
    c: Horizontal(g41)
    c: Coincident(g42,g9)
    c: Coincident(g42,g23)
    c: Horizontal(g42)
    c: Coincident(g43,g9)
    c: Coincident(g43,g23)
    c: Horizontal(g43)
    c: Coincident(g44,g10)
    c: Coincident(g44,g22)
    c: Horizontal(g44)
    c: Coincident(g45,g10)
    c: Coincident(g45,g22)
    c: Horizontal(g45)
    c: Coincident(g46,g11)
    c: Coincident(g46,g21)
    c: Horizontal(g46)
    c: Coincident(g47,g11)
    c: Coincident(g47,g21)
    c: Horizontal(g47)
FEATURE [Part::Extrusion] Extrude061
  Base = -> Sketch070
  Dir = (1,0,0)
  DirMode = 2
  FaceMakerClass = Part::FaceMakerBullseye
  LengthFwd = 23
  LengthRev = 0
  Placement = pos=(-19,0,0) rot=(0,0,1;0rad)
  Solid = true
  Symmetric = false
FEATURE [Part::Fillet] Fillet052  label="removeToCreateVentalationHoles002"
  Base = -> Extrude061
  Edges = <same value as first occurrence — deduplicated (x6 in doc)>
  Placement = pos=(7,0.02,0) rot=(0,0,1;0rad)
FEATURE [Part::MultiFuse] Fusion130  label="bottom013"
  Shapes = -> [Cut054,Cut034]
FEATURE [Part::Cut] Cut055
  Base = -> Fusion130
  Tool = -> Fillet052
FEATURE [Part::Cylinder] Cylinder054
  Angle = 360
  AttacherType = Attacher::AttachEngine3D
  Height = 20
  Placement = pos=(0,0,36.15) rot=(0,0,1;0rad)
  Radius = 4
FEATURE [Sketcher::SketchObject] Sketch071  label="bottomSketch002"
  FullyConstrained = true
  sketch-geometry (32):
    g0: LineSegment StartX=3.3 StartY=-6.03275e-07 StartZ=0 EndX=98 EndY=-6.03275e-07 EndZ=0
    g1: ArcOfCircle CenterX=98 CenterY=19 CenterZ=0 NormalX=0 NormalY=0 NormalZ=1 AngleXU=0 Radius=19 StartAngle=4.71239 EndAngle=5.71103
    g2: LineSegment StartX=6.3 StartY=8 StartZ=0 EndX=3.3 EndY=8 EndZ=0
    g3: LineSegment StartX=3.3 StartY=8 StartZ=0 EndX=3.3 EndY=-6.03275e-07 EndZ=0
    g4: ArcOfCircle CenterX=8.3 CenterY=5 CenterZ=0 NormalX=0 NormalY=0 NormalZ=1 AngleXU=0 Radius=2 StartAngle=3.14159 EndAngle=4.71239
    g5: LineSegment StartX=6.3 StartY=8 StartZ=0 EndX=6.3 EndY=5 EndZ=0
    g6: ArcOfCircle CenterX=98 CenterY=19 CenterZ=0 NormalX=0 NormalY=0 NormalZ=1 AngleXU=0 Radius=12.7 StartAngle=4.71239 EndAngle=6.28319
    g7: LineSegment StartX=94.7 StartY=3 StartZ=0 EndX=8.3 EndY=3 EndZ=0
    g8-g12: Circle x5 (B-spline internal-alignment scaffolding for g13; pole/knot coordinates omitted)
    g13: BSplineCurve PolesCount=5 KnotsCount=3 Degree=3 IsPeriodic=0
    g14: GeomPoint X=98 Y=6.3 Z=0
    g15: GeomPoint X=96.3938 Y=4.71946 Z=0
    g16: GeomPoint X=94.7 Y=3 Z=0
    g17-g23: Circle x7 (B-spline internal-alignment scaffolding for g24; pole/knot coordinates omitted)
    g24: BSplineCurve PolesCount=7 KnotsCount=5 Degree=3 IsPeriodic=0
    g25-g29: GeomPoint x5 (B-spline internal-alignment scaffolding for g24; pole/knot coordinates omitted)
    g30: ArcOfCircle CenterX=98 CenterY=19 CenterZ=0 NormalX=0 NormalY=0 NormalZ=1 AngleXU=0 Radius=15.7 StartAngle=5.81226 EndAngle=6.28319
    g31: LineSegment StartX=110.7 StartY=19 StartZ=0 EndX=113.7 EndY=19 EndZ=0
  constraints (41):
    c: Horizontal(g0)
    c: Coincident(g1,g0)
    c: Block(g1)
    c: Horizontal(g2)
    c: Distance(g2) = 3
    c: Coincident(g3,g2)
    c: Vertical(g3)
    c: Coincident(g3,g0)
    c: Block(g4)
    c: Block(g2)
    c: Coincident(g5,g2)
    c: Coincident(g5,g4)
    c: Vertical(g5)
    c: Coincident(g6,g1)
    c: Block(g6)
    c: Coincident(g7,g4)
    c: Horizontal(g7)
    c: Block(g0)
    c: Block(g7)
    c: Block(g3)
    c: Coincident(g13,g6)
    c: Weight(g8) = 1
    c: Equal(g8, g9-g12) x4
    c: Coincident(g13,g7)
    c: InternalAlignment(g8-g12 -> g13) x5
    c: InternalAlignment(g14,g13)
    c: InternalAlignment(g15,g13)
    c: InternalAlignment(g16,g13)
    c: Block(g13)
    c: Weight(g17) = 1
    c: Equal(g17, g18-g23) x6
    c: Coincident(g24,g1)
    c: InternalAlignment(g17-g23 -> g24) x7
    c: InternalAlignment(g25-g29 -> g24) x5
    c: Block(g24)
    c: Coincident(g30,g24)
    c: Coincident(g31,g6)
    c: Coincident(g31,g30)
    c: Horizontal(g31)
    c: Block(g31)
    c: Block(g30)
FEATURE [Part::Extrusion] Extrude062  label="bottom014"
  Base = -> Sketch071
  Dir = (0,0,1)
  DirMode = 2
  FaceMakerClass = Part::FaceMakerBullseye
  LengthFwd = 71.4
  LengthRev = 0
  Placement = pos=(0,0,0.3) rot=(0,0,1;0rad)
  Solid = true
  Symmetric = false
FEATURE [Part::Fillet] Fillet054
  Base = -> Extrude062
  Edges = 1 edges r=2.4: [Edge17]
FEATURE [Part::Fillet] Fillet055  label="bottom015"
  Base = -> Fillet054
  Edges = 1 edges r=2.4: [Edge36]
FEATURE [Part::Cylinder] Cylinder055
  Angle = 360
  AttacherType = Attacher::AttachEngine3D
  Height = 10
  Placement = pos=(0,0,36.15) rot=(0,0,1;0rad)
  Radius = 4
FEATURE [Part::MultiFuse] Fusion131  label="removeToCreateHoleForPlugHousing002"
  Placement = pos=(70,19,36.15) rot=(0,1,0;1.5708rad)
  Shapes = -> [Cylinder054,Cylinder055]
FEATURE [Part::Cut] Cut056  label="Bottom001"
  Base = -> Fillet055
  Placement = pos=(9,0,0) rot=(0,0,1;0rad)
  Tool = -> Fusion131
FEATURE [Part::Cut] Cut057
  Base = -> Cut055
  Tool = -> Cut056
FEATURE [Sketcher::SketchObject] Sketch072  label="topSketch021"
  FullyConstrained = true
  sketch-geometry (4):
    g0: ArcOfCircle CenterX=105 CenterY=19 CenterZ=0 NormalX=0 NormalY=0 NormalZ=1 AngleXU=0 Radius=20.6155 StartAngle=5.54125 EndAngle=6.28319
    g1: ArcOfCircle CenterX=105 CenterY=19 CenterZ=0 NormalX=0 NormalY=0 NormalZ=1 AngleXU=0 Radius=13 StartAngle=5.54125 EndAngle=6.28319
    g2: LineSegment StartX=118 StartY=19 StartZ=0 EndX=125.616 EndY=19 EndZ=0
    g3: LineSegment StartX=114.583 StartY=10.2157 StartZ=0 EndX=120.197 EndY=5.06982 EndZ=0
  constraints (7):
    c: Block(g0)
    c: Block(g1)
    c: Coincident(g2,g1)
    c: Coincident(g2,g0)
    c: Horizontal(g2)
    c: Coincident(g3,g1)
    c: Coincident(g3,g0)
FEATURE [Part::Extrusion] Extrude063  label="bottomPlugHousingBit003"
  Base = -> Sketch072
  Dir = (0,0,1)
  DirMode = 2
  FaceMakerClass = Part::FaceMakerBullseye
  LengthFwd = 72
  LengthRev = 0
  Solid = true
  Symmetric = false
FEATURE [Part::Cylinder] Cylinder056
  Angle = 360
  AttacherType = Attacher::AttachEngine3D
  Height = 20
  Placement = pos=(0,0,36.15) rot=(0,0,1;0rad)
  Radius = 14.3
FEATURE [Part::Cylinder] Cylinder057
  Angle = 360
  AttacherType = Attacher::AttachEngine3D
  Height = 10
  Placement = pos=(0,0,36.15) rot=(0,0,1;0rad)
  Radius = 4
FEATURE [Part::Box] Box034  label="removeToCreteHoleForPlugHousing047"
  AttacherType = Attacher::AttachEngine3D
  Height = 28.6
  Length = 20
  Placement = pos=(106.15,0,21.7) rot=(0,0,1;0rad)
  Width = 19
FEATURE [Part::Cylinder] Cylinder058
  Angle = 360
  AttacherType = Attacher::AttachEngine3D
  Height = 20
  Placement = pos=(0,0,36.15) rot=(0,0,1;0rad)
  Radius = 14.3
FEATURE [Part::Cylinder] Cylinder059
  Angle = 360
  AttacherType = Attacher::AttachEngine3D
  Height = 10
  Placement = pos=(0,0,36.15) rot=(0,0,1;0rad)
  Radius = 4
FEATURE [Part::MultiFuse] Fusion134  label="removeToCreteHoleForPlugHousing046"
  Placement = pos=(70,19,36) rot=(0,1,0;1.5708rad)
  Shapes = -> [Cylinder058,Cylinder059]
FEATURE [Part::Cylinder] Cylinder060
  Angle = 360
  AttacherType = Attacher::AttachEngine3D
  Height = 20
  Placement = pos=(0,0,36.15) rot=(0,0,1;0rad)
  Radius = 14
FEATURE [Part::Cylinder] Cylinder061
  Angle = 360
  AttacherType = Attacher::AttachEngine3D
  Height = 10
  Placement = pos=(0,0,36.15) rot=(0,0,1;0rad)
  Radius = 4
FEATURE [Part::MultiFuse] Fusion135  label="removeToCreteHoleForPlugHousing048"
  Placement = pos=(70,19,36) rot=(0,1,0;1.5708rad)
  Shapes = -> [Cylinder060,Cylinder061]
FEATURE [Part::Box] Box035  label="removeToCreteHoleForPlugHousing049"
  AttacherType = Attacher::AttachEngine3D
  Height = 28.6
  Length = 20
  Placement = pos=(106.15,0,21.7) rot=(0,0,1;0rad)
  Width = 19
FEATURE [Part::MultiFuse] Fusion133  label="removeToCreteHoleForPlugHousing045"
  Placement = pos=(0,0,-28.3) rot=(0,0,1;0rad)
  Shapes = -> [Box035,Fusion134]
FEATURE [Part::MultiFuse] Fusion138  label="removeToCreteHoleForPlugHousing051"
  Placement = pos=(70,19,36) rot=(0,1,0;1.5708rad)
  Shapes = -> [Cylinder056,Cylinder057]
FEATURE [Part::MultiFuse] Fusion137  label="removeToCreteHoleForPlugHousing050"
  Placement = pos=(0,0,28.3) rot=(0,0,1;0rad)
  Shapes = -> [Box034,Fusion138]
FEATURE [Part::MultiFuse] Fusion132  label="removeToCreatePlugHousingBottomBit002"
  Shapes = -> [Fusion133,Fusion137]
FEATURE [Part::MultiFuse] Fusion136  label="removeToCreatePlugHousingBottomBit003"
  Shapes = -> [Fusion135,Fusion132]
FEATURE [Part::Cut] Cut058  label="bottomPlugHousingBit002"
  Base = -> Extrude063
  Placement = pos=(-0.09,0,0) rot=(0,0,1;0rad)
  Tool = -> Fusion136
FEATURE [Sketcher::SketchObject] Sketch073  label="bottomSketch003"
  FullyConstrained = true
  sketch-geometry (45):
    g0: LineSegment StartX=6.29999 StartY=8 StartZ=0 EndX=3.29999 EndY=8 EndZ=0
    g1: LineSegment StartX=3.29999 StartY=8 StartZ=0 EndX=3.29999 EndY=-6.03275e-07 EndZ=0
    g2: ArcOfCircle CenterX=8.29999 CenterY=5 CenterZ=0 NormalX=0 NormalY=0 NormalZ=1 AngleXU=0 Radius=2 StartAngle=3.14159 EndAngle=4.71239
    g3: LineSegment StartX=6.29999 StartY=8 StartZ=0 EndX=6.29999 EndY=5 EndZ=0
    g4: ArcOfCircle CenterX=105 CenterY=19 CenterZ=0 NormalX=0 NormalY=0 NormalZ=1 AngleXU=0 Radius=12.7 StartAngle=4.71239 EndAngle=5.94289
    g5-g11: Circle x7 (B-spline internal-alignment scaffolding for g12; pole/knot coordinates omitted)
    g12: BSplineCurve PolesCount=7 KnotsCount=5 Degree=3 IsPeriodic=0
    g13-g17: GeomPoint x5 (B-spline internal-alignment scaffolding for g12; pole/knot coordinates omitted)
    g18: ArcOfCircle CenterX=105 CenterY=19 CenterZ=0 NormalX=0 NormalY=0 NormalZ=1 AngleXU=0 Radius=15.7 StartAngle=5.81226 EndAngle=6.28319
    g19: BSplineCurve PolesCount=5 KnotsCount=3 Degree=3 IsPeriodic=0
    g20: LineSegment StartX=8.29999 StartY=3 StartZ=0 EndX=101.7 EndY=3 EndZ=0
    g21: LineSegment StartX=3.29999 StartY=-6.03275e-07 StartZ=0 EndX=105 EndY=-6.03275e-07 EndZ=0
    g22: LineSegment StartX=120.974 StartY=8.71251 StartZ=0 EndX=122.332 EndY=7.83778 EndZ=0
    g23: LineSegment StartX=105 StartY=-6.03274e-07 StartZ=0 EndX=113 EndY=-6.03274e-07 EndZ=0
    g24: ArcOfCircle CenterX=105 CenterY=19 CenterZ=0 NormalX=0 NormalY=0 NormalZ=1 AngleXU=0 Radius=20.6155 StartAngle=5.11091 EndAngle=5.71103
    g25: ArcOfCircle CenterX=117.7 CenterY=19 CenterZ=0 NormalX=0 NormalY=0 NormalZ=1 AngleXU=0 Radius=3 StartAngle=1.2e-15 EndAngle=2.10468
    g26: Circle CenterX=116.345 CenterY=16.3232 CenterZ=0 NormalX=0 NormalY=0 NormalZ=1 AngleXU=0 Radius=1
    g27: Circle CenterX=117.24 CenterY=15.7584 CenterZ=0 NormalX=0 NormalY=0 NormalZ=1 AngleXU=0 Radius=1
    g28: Circle CenterX=116.972 CenterY=14.7612 CenterZ=0 NormalX=0 NormalY=0 NormalZ=1 AngleXU=0 Radius=1
    g29: BSplineCurve PolesCount=3 KnotsCount=2 Degree=2 IsPeriodic=0
    g30: GeomPoint X=116.345 Y=16.3232 Z=0
    g31: GeomPoint X=116.972 Y=14.7612 Z=0
    g32: Circle CenterX=115.828 CenterY=17.157 CenterZ=0 NormalX=0 NormalY=0 NormalZ=1 AngleXU=0 Radius=1
    g33: Circle CenterX=115.841 CenterY=16.639 CenterZ=0 NormalX=0 NormalY=0 NormalZ=1 AngleXU=0 Radius=1
    g34: Circle CenterX=116.345 CenterY=16.3232 CenterZ=0 NormalX=0 NormalY=0 NormalZ=1 AngleXU=0 Radius=1
    g35: BSplineCurve PolesCount=3 KnotsCount=2 Degree=2 IsPeriodic=0
    g36: GeomPoint X=115.828 Y=17.157 Z=0
    g37: GeomPoint X=116.345 Y=16.3232 Z=0
    g38: LineSegment StartX=115.828 StartY=17.157 StartZ=0 EndX=115.828 EndY=20.8307 EndZ=0
    g39: Circle CenterX=115.828 CenterY=20.8307 CenterZ=0 NormalX=0 NormalY=0 NormalZ=1 AngleXU=0 Radius=1
    g40: Circle CenterX=115.831 CenterY=21.3396 CenterZ=0 NormalX=0 NormalY=0 NormalZ=1 AngleXU=0 Radius=1
    g41: Circle CenterX=116.173 CenterY=21.5825 CenterZ=0 NormalX=0 NormalY=0 NormalZ=1 AngleXU=0 Radius=1
    g42: BSplineCurve PolesCount=3 KnotsCount=2 Degree=2 IsPeriodic=0
    g43: GeomPoint X=115.828 Y=20.8307 Z=0
    g44: GeomPoint X=116.173 Y=21.5825 Z=0
  constraints (70):
    c: Horizontal(g0)
    c: Distance(g0) = 3
    c: Coincident(g1,g0)
    c: Vertical(g1)
    c: Block(g2)
    c: Block(g0)
    c: Coincident(g3,g0)
    c: Coincident(g3,g2)
    c: Vertical(g3)
    c: Block(g1)
    c: Block(g4)
    c: Coincident(g19,g4)
    c: Block(g19)
    c: Equal(g5, g6-g11) x6
    c: InternalAlignment(g5-g11 -> g12) x7
    c: InternalAlignment(g13-g17 -> g12) x5
    c: Block(g12)
    c: Coincident(g18,g12)
    c: Block(g18)
    c: Coincident(g20,g2)
    c: Coincident(g20,g19)
    c: Horizontal(g20)
    c: Distance(g20) = 93.4
    c: Coincident(g21,g1)
    c: Horizontal(g21)
    c: Distance(g21) = 101.7
    c: Horizontal(g23)
    c: Distance(g23) = 8
    c: Coincident(g24,g23)
    c: Block(g23)
    c: Coincident(g22,g24)
    c: Block(g24)
    c: Block(g22)
    c: Distance(g22) = 1.61553
    c: Coincident(g25,g18)
    c: Block(g25)
    c: Weight(g26) = 1
    c: Equal(g26,g27)
    c: Equal(g26,g28)
    c: Coincident(g29,g4)
    c: InternalAlignment(g26,g29)
    c: InternalAlignment(g27,g29)
    c: InternalAlignment(g28,g29)
    c: InternalAlignment(g30,g29)
    c: InternalAlignment(g31,g29)
    c: Block(g29)
    c: Weight(g32) = 1
    c: Equal(g32,g33)
    c: Equal(g32,g34)
    c: Coincident(g35,g29)
    c: InternalAlignment(g32,g35)
    c: InternalAlignment(g33,g35)
    c: InternalAlignment(g34,g35)
    c: InternalAlignment(g36,g35)
    c: InternalAlignment(g37,g35)
    c: Block(g35)
    c: Coincident(g38,g35)
    c: Vertical(g38)
    c: Block(g38)
    c: Coincident(g42,g38)
    c: Weight(g39) = 1
    c: Equal(g39,g40)
    c: Equal(g39,g41)
    c: Coincident(g42,g25)
    c: InternalAlignment(g39,g42)
    c: InternalAlignment(g40,g42)
    c: InternalAlignment(g41,g42)
    c: InternalAlignment(g43,g42)
    c: InternalAlignment(g44,g42)
    c: Block(g42)
FEATURE [Part::Extrusion] Extrude064  label="bottom016"
  Base = -> Sketch073
  Dir = (0,0,1)
  DirMode = 2
  FaceMakerClass = Part::FaceMakerBullseye
  LengthFwd = 71.4
  LengthRev = 0
  Placement = pos=(0,0,0.3) rot=(0,0,1;0rad)
  Solid = true
  Symmetric = false
FEATURE [Part::Revolution] Revolve157  label="removeToCreateScrewAndThreadedInsertHole063"
  Angle = 360
  Axis = (0,1,0)
  Base = (0,0,0)
  FaceMakerClass = Part::FaceMakerBullseye
  Placement = pos=(12.5,0,10) rot=(0,0,1;0rad)
  Solid = false
  Source = -> Face141
  Symmetric = false
FEATURE [Sketcher::SketchObject] Sketch074
  FullyConstrained = true
  Placement = pos=(117,19,0) rot=(0.57735,0.57735,0.57735;2.0944rad)
  sketch-geometry (48):
    g0: LineSegment StartX=-49.19 StartY=69.25 StartZ=0 EndX=-49.19 EndY=66.25 EndZ=0
    g1: LineSegment StartX=-49.19 StartY=63.5 StartZ=0 EndX=-49.19 EndY=60.5 EndZ=0
    g2: LineSegment StartX=-49.19 StartY=57.75 StartZ=0 EndX=-49.19 EndY=54.75 EndZ=0
    g3: LineSegment StartX=-49.19 StartY=52 StartZ=0 EndX=-49.19 EndY=49 EndZ=0
    g4: LineSegment StartX=-49.19 StartY=46.25 StartZ=0 EndX=-49.19 EndY=43.25 EndZ=0
    g5: LineSegment StartX=-49.19 StartY=40.5 StartZ=0 EndX=-49.19 EndY=37.5 EndZ=0
    g6: LineSegment StartX=-49.19 StartY=34.5 StartZ=0 EndX=-49.19 EndY=31.5 EndZ=0
    g7: LineSegment StartX=-49.19 StartY=28.75 StartZ=0 EndX=-49.19 EndY=25.75 EndZ=0
    g8: LineSegment StartX=-49.19 StartY=23 StartZ=0 EndX=-49.19 EndY=20 EndZ=0
    g9: LineSegment StartX=-49.19 StartY=17.25 StartZ=0 EndX=-49.19 EndY=14.25 EndZ=0
    g10: LineSegment StartX=-49.19 StartY=11.5 StartZ=0 EndX=-49.19 EndY=8.5 EndZ=0
    g11: LineSegment StartX=-49.19 StartY=5.75 StartZ=0 EndX=-49.19 EndY=2.75 EndZ=0
    g12: ArcOfCircle CenterX=-1.5 CenterY=67.75 CenterZ=0 NormalX=0 NormalY=0 NormalZ=1 AngleXU=0 Radius=1.5 StartAngle=4.71239 EndAngle=7.85398
    g13: ArcOfCircle CenterX=-1.5 CenterY=62 CenterZ=0 NormalX=0 NormalY=0 NormalZ=1 AngleXU=0 Radius=1.5 StartAngle=4.71239 EndAngle=7.85398
    g14: ArcOfCircle CenterX=-1.5 CenterY=56.25 CenterZ=0 NormalX=0 NormalY=0 NormalZ=1 AngleXU=0 Radius=1.5 StartAngle=4.71239 EndAngle=7.85398
    g15: ArcOfCircle CenterX=-11.49 CenterY=50.5 CenterZ=0 NormalX=0 NormalY=0 NormalZ=1 AngleXU=0 Radius=1.5 StartAngle=4.71239 EndAngle=7.85398
    g16: ArcOfCircle CenterX=-16.28 CenterY=44.75 CenterZ=0 NormalX=0 NormalY=0 NormalZ=1 AngleXU=0 Radius=1.5 StartAngle=4.71239 EndAngle=7.85398
    g17: ArcOfCircle CenterX=-18.2337 CenterY=39 CenterZ=0 NormalX=0 NormalY=0 NormalZ=1 AngleXU=0 Radius=1.5 StartAngle=4.71485 EndAngle=7.85398
    g18: ArcOfCircle CenterX=-16.2837 CenterY=27.25 CenterZ=0 NormalX=0 NormalY=0 NormalZ=1 AngleXU=0 Radius=1.5 StartAngle=4.71485 EndAngle=7.85398
    g19: ArcOfCircle CenterX=-18.2337 CenterY=33 CenterZ=0 NormalX=0 NormalY=0 NormalZ=1 AngleXU=0 Radius=1.5 StartAngle=4.71485 EndAngle=7.85398
    g20: ArcOfCircle CenterX=-11.49 CenterY=21.5 CenterZ=0 NormalX=0 NormalY=0 NormalZ=1 AngleXU=0 Radius=1.5 StartAngle=4.71239 EndAngle=7.85398
    g21: ArcOfCircle CenterX=-1.5 CenterY=4.25 CenterZ=0 NormalX=0 NormalY=0 NormalZ=1 AngleXU=0 Radius=1.5 StartAngle=4.71239 EndAngle=7.85398
    g22: ArcOfCircle CenterX=-1.5 CenterY=10 CenterZ=0 NormalX=0 NormalY=0 NormalZ=1 AngleXU=0 Radius=1.5 StartAngle=4.71239 EndAngle=7.85398
    g23: ArcOfCircle CenterX=-1.5 CenterY=15.75 CenterZ=0 NormalX=0 NormalY=0 NormalZ=1 AngleXU=0 Radius=1.5 StartAngle=4.71239 EndAngle=7.85398
    g24: LineSegment StartX=-49.19 StartY=69.25 StartZ=0 EndX=-1.5 EndY=69.25 EndZ=0
    g25: LineSegment StartX=-49.19 StartY=66.25 StartZ=0 EndX=-1.5 EndY=66.25 EndZ=0
    g26: LineSegment StartX=-49.19 StartY=63.5 StartZ=0 EndX=-1.5 EndY=63.5 EndZ=0
    g27: LineSegment StartX=-49.19 StartY=60.5 StartZ=0 EndX=-1.5 EndY=60.5 EndZ=0
    g28: LineSegment StartX=-49.19 StartY=57.75 StartZ=0 EndX=-1.5 EndY=57.75 EndZ=0
    g29: LineSegment StartX=-49.19 StartY=54.75 StartZ=0 EndX=-1.5 EndY=54.75 EndZ=0
    g30: LineSegment StartX=-49.19 StartY=52 StartZ=0 EndX=-11.49 EndY=52 EndZ=0
    g31: LineSegment StartX=-49.19 StartY=49 StartZ=0 EndX=-11.49 EndY=49 EndZ=0
    g32: LineSegment StartX=-49.19 StartY=46.25 StartZ=0 EndX=-16.28 EndY=46.25 EndZ=0
    g33: LineSegment StartX=-49.19 StartY=43.25 StartZ=0 EndX=-16.28 EndY=43.25 EndZ=0
    g34: LineSegment StartX=-49.19 StartY=40.5 StartZ=0 EndX=-18.2337 EndY=40.5 EndZ=0
    g35: LineSegment StartX=-49.19 StartY=37.5 StartZ=0 EndX=-18.23 EndY=37.5 EndZ=0
    g36: LineSegment StartX=-49.19 StartY=34.5 StartZ=0 EndX=-18.2337 EndY=34.5 EndZ=0
    g37: LineSegment StartX=-49.19 StartY=31.5 StartZ=0 EndX=-18.23 EndY=31.5 EndZ=0
    g38: LineSegment StartX=-49.19 StartY=28.75 StartZ=0 EndX=-16.2837 EndY=28.75 EndZ=0
    g39: LineSegment StartX=-49.19 StartY=25.75 StartZ=0 EndX=-16.28 EndY=25.75 EndZ=0
    g40: LineSegment StartX=-49.19 StartY=23 StartZ=0 EndX=-11.49 EndY=23 EndZ=0
    g41: LineSegment StartX=-49.19 StartY=20 StartZ=0 EndX=-11.49 EndY=20 EndZ=0
    g42: LineSegment StartX=-49.19 StartY=17.25 StartZ=0 EndX=-1.5 EndY=17.25 EndZ=0
    g43: LineSegment StartX=-49.19 StartY=14.25 StartZ=0 EndX=-1.5 EndY=14.25 EndZ=0
    g44: LineSegment StartX=-49.19 StartY=11.5 StartZ=0 EndX=-1.5 EndY=11.5 EndZ=0
    g45: LineSegment StartX=-49.19 StartY=8.5 StartZ=0 EndX=-1.5 EndY=8.5 EndZ=0
    g46: LineSegment StartX=-49.19 StartY=5.75 StartZ=0 EndX=-1.5 EndY=5.75 EndZ=0
    g47: LineSegment StartX=-49.19 StartY=2.75 StartZ=0 EndX=-1.5 EndY=2.75 EndZ=0
  constraints (120):
    c: Vertical(g0)
    c: Distance(g0) = 3
    c: Block(g0)
    c: Vertical(g1)
    c: Distance(g1) = 3
    c: Vertical(g2)
    c: Equal(g0,g2) = 3
    c: Block(g2)
    c: Vertical(g3)
    c: Equal(g1,g3) = 3
    c: Vertical(g4)
    c: Equal(g0,g4) = 3
    c: Block(g4)
    c: Vertical(g5)
    c: Equal(g1,g5) = 3
    c: Vertical(g6)
    c: Equal(g0,g6) = 3
    c: Block(g6)
    c: Vertical(g7)
    c: Equal(g1,g7) = 3
    c: Vertical(g8)
    c: Equal(g0,g8) = 3
    c: Block(g8)
    c: Vertical(g9)
    c: Equal(g1,g9) = 3
    c: Vertical(g10)
    c: Equal(g0,g10) = 3
    c: Block(g10)
    c: Vertical(g11)
    c: Equal(g1,g11) = 3
    c: Block(g12)
    c: Block(g13)
    c: Block(g14)
    c: Block(g15)
    c: Block(g16)
    c: Block(g17)
    c: Block(g18)
    c: Block(g19)
    c: Block(g20)
    c: Block(g21)
    c: Block(g22)
    c: Block(g23)
    c: Block(g11)
    c: Block(g9)
    c: Block(g7)
    c: Block(g5)
    c: Block(g3)
    c: Block(g1)
    c: Coincident(g24,g0)
    c: Coincident(g24,g12)
    c: Horizontal(g24)
    c: Coincident(g25,g0)
    c: Coincident(g25,g12)
    c: Horizontal(g25)
    c: Coincident(g26,g1)
    c: Coincident(g26,g13)
    c: Horizontal(g26)
    c: Coincident(g27,g1)
    c: Coincident(g27,g13)
    c: Horizontal(g27)
    c: Coincident(g28,g2)
    c: Coincident(g28,g14)
    c: Horizontal(g28)
    c: Coincident(g29,g2)
    c: Coincident(g29,g14)
    c: Horizontal(g29)
    c: Coincident(g30,g3)
    c: Coincident(g30,g15)
    c: Horizontal(g30)
    c: Coincident(g31,g3)
    c: Coincident(g31,g15)
    c: Horizontal(g31)
    c: Coincident(g32,g4)
    c: Coincident(g32,g16)
    c: Horizontal(g32)
    c: Coincident(g33,g4)
    c: Coincident(g33,g16)
    c: Horizontal(g33)
    c: Coincident(g34,g5)
    c: Coincident(g34,g17)
    c: Horizontal(g34)
    c: Coincident(g35,g5)
    c: Coincident(g35,g17)
    c: Horizontal(g35)
    c: Coincident(g36,g6)
    c: Coincident(g36,g19)
    c: Horizontal(g36)
    c: Coincident(g37,g6)
    c: Coincident(g37,g19)
    c: Horizontal(g37)
    c: Coincident(g38,g7)
    c: Coincident(g38,g18)
    c: Horizontal(g38)
    c: Coincident(g39,g7)
    c: Coincident(g39,g18)
    c: Horizontal(g39)
    c: Coincident(g40,g8)
    c: Coincident(g40,g20)
    c: Horizontal(g40)
    c: Coincident(g41,g8)
    c: Coincident(g41,g20)
    c: Horizontal(g41)
    c: Coincident(g42,g9)
    c: Coincident(g42,g23)
    c: Horizontal(g42)
    c: Coincident(g43,g9)
    c: Coincident(g43,g23)
    c: Horizontal(g43)
    c: Coincident(g44,g10)
    c: Coincident(g44,g22)
    c: Horizontal(g44)
    c: Coincident(g45,g10)
    c: Coincident(g45,g22)
    c: Horizontal(g45)
    c: Coincident(g46,g11)
    c: Coincident(g46,g21)
    c: Horizontal(g46)
    c: Coincident(g47,g11)
    c: Coincident(g47,g21)
    c: Horizontal(g47)
FEATURE [Part::Extrusion] Extrude065
  Base = -> Sketch074
  Dir = (1,0,0)
  DirMode = 2
  FaceMakerClass = Part::FaceMakerBullseye
  LengthFwd = 23
  LengthRev = 0
  Placement = pos=(-19,0,0) rot=(0,0,1;0rad)
  Solid = true
  Symmetric = false
FEATURE [Part::Fillet] Fillet056  label="removeToCreateVentalationHoles003"
  Base = -> Extrude065
  Edges = <same value as first occurrence — deduplicated (x6 in doc)>
  Placement = pos=(7,0.02,0) rot=(0,0,1;0rad)
FEATURE [Part::Revolution] Revolve158  label="removeToCreateScrewAndThreadedInsertHole065"
  Angle = 360
  Axis = (0,1,0)
  Base = (0,0,0)
  FaceMakerClass = Part::FaceMakerBullseye
  Placement = pos=(12.5,0,62) rot=(0,0,1;0rad)
  Solid = false
  Source = -> Face146
  Symmetric = false
FEATURE [Part::Revolution] Revolve159  label="removeToCreateScrewAndThreadedInsertHole066"
  Angle = 360
  Axis = (0,1,0)
  Base = (0,0,0)
  FaceMakerClass = Part::FaceMakerBullseye
  Placement = pos=(89.5,0,68.5) rot=(0,0,1;0rad)
  Solid = false
  Source = -> Face143
  Symmetric = false
FEATURE [Part::Revolution] Revolve160  label="removeToCreateScrewAndThreadedInsertHole067"
  Angle = 360
  Axis = (0,1,0)
  Base = (0,0,0)
  FaceMakerClass = Part::FaceMakerBullseye
  Placement = pos=(89.5,0,3.5) rot=(0,0,1;0rad)
  Solid = false
  Source = -> Face142
  Symmetric = false
FEATURE [Part::Revolution] Revolve161  label="removeToCreateScrewAndThreadedInsertHole068"
  Angle = 360
  Axis = (0,1,0)
  Base = (0,0,0)
  FaceMakerClass = Part::FaceMakerBullseye
  Placement = pos=(109.5,4.7,3.5) rot=(0,0,1;0rad)
  Solid = false
  Source = -> Face145
  Symmetric = false
FEATURE [Part::Revolution] Revolve162  label="removeToCreateScrewAndThreadedInsertHole069"
  Angle = 360
  Axis = (0,1,0)
  Base = (0,0,0)
  FaceMakerClass = Part::FaceMakerBullseye
  Placement = pos=(109.5,4.7,68.5) rot=(0,0,1;0rad)
  Solid = false
  Source = -> Face144
  Symmetric = false
FEATURE [Part::MultiFuse] Fusion141  label="removeToCreateScrewAndThreadedInsertHole064"
  Shapes = -> [Revolve162,Revolve161,Revolve160,Revolve159,Revolve158,Revolve157]
FEATURE [Part::Cylinder] Cylinder062
  Angle = 360
  AttacherType = Attacher::AttachEngine3D
  Height = 20
  Placement = pos=(0,0,36.15) rot=(0,0,1;0rad)
  Radius = 14
FEATURE [Part::Cylinder] Cylinder063
  Angle = 360
  AttacherType = Attacher::AttachEngine3D
  Height = 10
  Placement = pos=(0,0,36.15) rot=(0,0,1;0rad)
  Radius = 4
FEATURE [Part::MultiFuse] Fusion139  label="removeToCreteHoleForPlugHousing052"
  Placement = pos=(70,19,36) rot=(0,1,0;1.5708rad)
  Shapes = -> [Cylinder062,Cylinder063]
FEATURE [Part::Cut] Cut060  label="bottom017"
  Base = -> Extrude064
  Tool = -> Fusion139
FEATURE [Part::Cut] Cut061  label="bottom019"
  Base = -> Cut060
  Tool = -> Fusion141
FEATURE [Part::MultiFuse] Fusion140  label="bottom018"
  Shapes = -> [Cut061,Cut058]
FEATURE [Part::Cut] Cut059  label="bottom020"
  Base = -> Fusion140
  Tool = -> Fillet056
FEATURE [Part::Box] Box036  label="Cube021"
  AttacherType = Attacher::AttachEngine3D
  Height = 80
  Length = 26
  Placement = pos=(0,-1,-5) rot=(0,0,1;0rad)
  Width = 11
FEATURE [Part::Cut] Cut062  label="removeFromBottom002"
  Base = -> Cut057
  Tool = -> Box036
FEATURE [Part::Cut] Cut063
  Base = -> Cut059
  Tool = -> Cut062
FEATURE [Part::Cut] Cut064  label="pcbStands"
  Base = -> Fusion095
  Tool = -> Fusion127
FEATURE [Sketcher::SketchObject] Sketch075  label="topSketch022"
  FullyConstrained = true
  sketch-geometry (6):
    g0: LineSegment StartX=19 StartY=38 StartZ=0 EndX=117 EndY=38 EndZ=0
    g1: ArcOfCircle CenterX=19 CenterY=19 CenterZ=0 NormalX=0 NormalY=0 NormalZ=1 AngleXU=0 Radius=19 StartAngle=1.5708 EndAngle=3.14159
    g2: LineSegment StartX=117 StartY=38 StartZ=0 EndX=117 EndY=19 EndZ=0
    g3: LineSegment StartX=98 StartY=1.0161e-12 StartZ=0 EndX=5.22862e-06 EndY=1.0161e-12 EndZ=0
    g4: LineSegment StartX=5.22862e-06 StartY=19 StartZ=0 EndX=5.22862e-06 EndY=1.0161e-12 EndZ=0
    g5: ArcOfCircle CenterX=98 CenterY=19 CenterZ=0 NormalX=0 NormalY=0 NormalZ=1 AngleXU=0 Radius=19 StartAngle=4.71239 EndAngle=6.28319
  constraints (16):
    c: Horizontal(g0)
    c: Distance(g0) = 98
    c: Coincident(g1,g0)
    c: Block(g1)
    c: Coincident(g2,g0)
    c: Vertical(g2)
    c: Distance(g2) = 19
    c: Horizontal(g3)
    c: Coincident(g4,g1)
    c: Vertical(g4)
    c: Coincident(g3,g4)
    c: Block(g3)
    c: Coincident(g5,g2)
    c: Coincident(g5,g3)
    c: Block(g0)
    c: Block(g5)
FEATURE [Part::Extrusion] Extrude067  label="sideB003"
  Base = -> Sketch075
  Dir = (0,0,1)
  DirMode = 2
  FaceMakerClass = Part::FaceMakerBullseye
  LengthFwd = 3
  LengthRev = 0
  Placement = pos=(0,0,71.7) rot=(0,0,1;0rad)
  Solid = true
  Symmetric = false
FEATURE [Sketcher::SketchObject] Sketch076  label="topSketch023"
  FullyConstrained = true
  sketch-geometry (6):
    g0: LineSegment StartX=19 StartY=38 StartZ=0 EndX=117 EndY=38 EndZ=0
    g1: ArcOfCircle CenterX=19 CenterY=19 CenterZ=0 NormalX=0 NormalY=0 NormalZ=1 AngleXU=0 Radius=19 StartAngle=1.5708 EndAngle=3.14159
    g2: LineSegment StartX=117 StartY=38 StartZ=0 EndX=117 EndY=19 EndZ=0
    g3: LineSegment StartX=98 StartY=1.0161e-12 StartZ=0 EndX=5.22862e-06 EndY=1.0161e-12 EndZ=0
    g4: LineSegment StartX=5.22862e-06 StartY=19 StartZ=0 EndX=5.22862e-06 EndY=1.0161e-12 EndZ=0
    g5: ArcOfCircle CenterX=98 CenterY=19 CenterZ=0 NormalX=0 NormalY=0 NormalZ=1 AngleXU=0 Radius=19 StartAngle=4.71239 EndAngle=6.28319
  constraints (16):
    c: Horizontal(g0)
    c: Distance(g0) = 98
    c: Coincident(g1,g0)
    c: Block(g1)
    c: Coincident(g2,g0)
    c: Vertical(g2)
    c: Distance(g2) = 19
    c: Horizontal(g3)
    c: Coincident(g4,g1)
    c: Vertical(g4)
    c: Coincident(g3,g4)
    c: Block(g3)
    c: Coincident(g5,g2)
    c: Coincident(g5,g3)
    c: Block(g0)
    c: Block(g5)
FEATURE [Part::Extrusion] Extrude066  label="sideA003"
  Base = -> Sketch076
  Dir = (0,0,1)
  DirMode = 2
  FaceMakerClass = Part::FaceMakerBullseye
  LengthFwd = 3
  LengthRev = 0
  Placement = pos=(0,0,-2.7) rot=(0,0,1;0rad)
  Solid = true
  Symmetric = false
FEATURE [Part::MultiFuse] Fusion142  label="removeFromBottom003"
  Placement = pos=(2,0,0) rot=(0,0,1;0rad)
  Shapes = -> [Extrude066,Extrude067]
FEATURE [Part::Cut] Cut065  label="screwRetainers002"
  Base = -> Fusion096
  Tool = -> Fusion142
FEATURE [Sketcher::SketchObject] Sketch077
  FullyConstrained = true
  Placement = pos=(117,19,0) rot=(0.57735,0.57735,0.57735;2.0944rad)
  sketch-geometry (8):
    g0: LineSegment StartX=-49.19 StartY=63.5 StartZ=0 EndX=-49.19 EndY=60.5 EndZ=0
    g1: LineSegment StartX=-49.19 StartY=11.5 StartZ=0 EndX=-49.19 EndY=8.5 EndZ=0
    g2: ArcOfCircle CenterX=-1.5 CenterY=62 CenterZ=0 NormalX=0 NormalY=0 NormalZ=1 AngleXU=0 Radius=1.5 StartAngle=4.71239 EndAngle=7.85398
    g3: ArcOfCircle CenterX=-1.5 CenterY=10 CenterZ=0 NormalX=0 NormalY=0 NormalZ=1 AngleXU=0 Radius=1.5 StartAngle=4.71239 EndAngle=7.85398
    g4: LineSegment StartX=-49.19 StartY=63.5 StartZ=0 EndX=-1.5 EndY=63.5 EndZ=0
    g5: LineSegment StartX=-49.19 StartY=60.5 StartZ=0 EndX=-1.5 EndY=60.5 EndZ=0
    g6: LineSegment StartX=-49.19 StartY=11.5 StartZ=0 EndX=-1.5 EndY=11.5 EndZ=0
    g7: LineSegment StartX=-49.19 StartY=8.5 StartZ=0 EndX=-1.5 EndY=8.5 EndZ=0
  constraints (19):
    c: Vertical(g0)
    c: Distance(g0) = 3
    c: Vertical(g1)
    c: Block(g1)
    c: Block(g2)
    c: Block(g3)
    c: Block(g0)
    c: Coincident(g4,g0)
    c: Coincident(g4,g2)
    c: Horizontal(g4)
    c: Coincident(g5,g0)
    c: Coincident(g5,g2)
    c: Horizontal(g5)
    c: Coincident(g6,g1)
    c: Coincident(g6,g3)
    c: Horizontal(g6)
    c: Coincident(g7,g1)
    c: Coincident(g7,g3)
    c: Horizontal(g7)
FEATURE [Part::Extrusion] Extrude068
  Base = -> Sketch077
  Dir = (1,0,0)
  DirMode = 2
  FaceMakerClass = Part::FaceMakerBullseye
  LengthFwd = 10
  LengthRev = 0
  Solid = true
  Symmetric = false
FEATURE [Part::Fillet] Fillet057  label="removeFromtMoreFrontCaseScrewRetainers002"
  Base = -> Extrude068
  Edges = 4 edges r=1.49: [Edge6,Edge11,Edge18,Edge23]
  Placement = pos=(-12,0,0) rot=(0,0,1;0rad)
FEATURE [Sketcher::SketchObject] Sketch078
  FullyConstrained = true
  Placement = pos=(117,19,0) rot=(0.57735,0.57735,0.57735;2.0944rad)
  sketch-geometry (8):
    g0: LineSegment StartX=-49.19 StartY=69.25 StartZ=0 EndX=-49.19 EndY=66.25 EndZ=0
    g1: LineSegment StartX=-49.19 StartY=5.75 StartZ=0 EndX=-49.19 EndY=2.75 EndZ=0
    g2: ArcOfCircle CenterX=-1.5 CenterY=67.75 CenterZ=0 NormalX=0 NormalY=0 NormalZ=1 AngleXU=0 Radius=1.5 StartAngle=4.71239 EndAngle=7.85398
    g3: ArcOfCircle CenterX=-1.5 CenterY=4.25 CenterZ=0 NormalX=0 NormalY=0 NormalZ=1 AngleXU=0 Radius=1.5 StartAngle=4.71239 EndAngle=7.85398
    g4: LineSegment StartX=-49.19 StartY=69.25 StartZ=0 EndX=-1.5 EndY=69.25 EndZ=0
    g5: LineSegment StartX=-49.19 StartY=66.25 StartZ=0 EndX=-1.5 EndY=66.25 EndZ=0
    g6: LineSegment StartX=-49.19 StartY=5.75 StartZ=0 EndX=-1.5 EndY=5.75 EndZ=0
    g7: LineSegment StartX=-49.19 StartY=2.75 StartZ=0 EndX=-1.5 EndY=2.75 EndZ=0
  constraints (19):
    c: Vertical(g0)
    c: Distance(g0) = 3
    c: Block(g0)
    c: Vertical(g1)
    c: Block(g2)
    c: Block(g3)
    c: Block(g1)
    c: Coincident(g4,g0)
    c: Coincident(g4,g2)
    c: Horizontal(g4)
    c: Coincident(g5,g0)
    c: Coincident(g5,g2)
    c: Horizontal(g5)
    c: Coincident(g6,g1)
    c: Coincident(g6,g3)
    c: Horizontal(g6)
    c: Coincident(g7,g1)
    c: Coincident(g7,g3)
    c: Horizontal(g7)
FEATURE [Part::Extrusion] Extrude069
  Base = -> Sketch078
  Dir = (1,0,0)
  DirMode = 2
  FaceMakerClass = Part::FaceMakerBullseye
  LengthFwd = 10
  LengthRev = 0
  Solid = true
  Symmetric = false
FEATURE [Part::Fillet] Fillet058  label="removeFromtMoreFrontCaseScrewRetainers003"
  Base = -> Extrude069
  Edges = 4 edges r=1.49: [Edge6,Edge11,Edge18,Edge23]
  Placement = pos=(-4,0,0) rot=(0,0,1;0rad)
FEATURE [Part::Cut] Cut066
  Base = -> Cut065
  Tool = -> Fillet058
FEATURE [Part::Cut] Cut067  label="screwPillars"
  Base = -> Cut066
  Tool = -> Fillet057
FEATURE [Part::MultiFuse] Fusion143  label="bottom021"
  Shapes = -> [Cut031,Cut063]
FEATURE [Part::Cylinder] Cylinder
  Angle = 360
  AttacherType = Attacher::AttachEngine3D
  Height = 10
  Placement = pos=(20.65,12,4.68) rot=(1,0,0;1.5708rad)
  Radius = 2
FEATURE [Part::Cylinder] Cylinder064
  Angle = 360
  AttacherType = Attacher::AttachEngine3D
  Height = 10
  Placement = pos=(20.65,12,67.38) rot=(1,0,0;1.5708rad)
  Radius = 2
FEATURE [Part::Cylinder] Cylinder065
  Angle = 360
  AttacherType = Attacher::AttachEngine3D
  Height = 10
  Placement = pos=(77.15,12,67.38) rot=(1,0,0;1.5708rad)
  Radius = 2
FEATURE [Part::Cylinder] Cylinder066
  Angle = 360
  AttacherType = Attacher::AttachEngine3D
  Height = 10
  Placement = pos=(77.15,12,4.68) rot=(1,0,0;1.5708rad)
  Radius = 2
FEATURE [Part::MultiFuse] Fusion144  label="removeFromThreadedInsertHousing"
  Shapes = -> [Cylinder065,Cylinder064,Cylinder,Cylinder066]
FEATURE [Part::Cut] Cut068  label="pcbStands001"
  Base = -> Cut064
  Tool = -> Fusion144
FEATURE [Part::MultiFuse] Fusion145
  Shapes = -> [Cut068,Fusion143]
FEATURE [Part::MultiFuse] Fusion146
  Shapes = -> [Fusion145]
FEATURE [Part::MultiFuse] Fusion147  label="bottom022"
  Shapes = -> [Cut067,Fusion146]
FEATURE [Part::MultiFuse] Fusion148  label="casePillars005"
  Shapes = -> [Cut047,Fusion092]
FEATURE [Part::MultiFuse] Fusion149  label="bottom023"
  Shapes = -> [Fusion124,Fusion113,Fusion147]
FEATURE [Part::MultiFuse] Fusion150  label="topBits"
  Shapes = -> [Cut025,Fusion148,Cut030,Fillet034]
FEATURE [Part::Feature] Face149 .. Face152  x4 (patterned run collapsed; names and placements below)
  shape: bbox 3.2 x 1.5 x 2e-07 mm, 1 faces, 0 solids (baked)
FEATURE [Part::Feature] Face153
  shape: bbox 3.6 x 3.2 x 2e-07 mm, 1 faces, 0 solids (baked)
FEATURE [Part::Feature] Face154
  shape: bbox 3.6 x 3.2 x 2e-07 mm, 1 faces, 0 solids (baked)
FEATURE [Sketcher::SketchObject] Sketch079  label="topSketch024"
  FullyConstrained = true
  sketch-geometry (6):
    g0: LineSegment StartX=19 StartY=38 StartZ=0 EndX=117 EndY=38 EndZ=0
    g1: ArcOfCircle CenterX=19 CenterY=19 CenterZ=0 NormalX=0 NormalY=0 NormalZ=1 AngleXU=0 Radius=19 StartAngle=1.5708 EndAngle=3.14159
    g2: LineSegment StartX=117 StartY=38 StartZ=0 EndX=117 EndY=19 EndZ=0
    g3: LineSegment StartX=98 StartY=1.0161e-12 StartZ=0 EndX=5.22862e-06 EndY=1.0161e-12 EndZ=0
    g4: LineSegment StartX=5.22862e-06 StartY=19 StartZ=0 EndX=5.22862e-06 EndY=1.0161e-12 EndZ=0
    g5: ArcOfCircle CenterX=98 CenterY=19 CenterZ=0 NormalX=0 NormalY=0 NormalZ=1 AngleXU=0 Radius=19 StartAngle=4.71239 EndAngle=6.28319
  constraints (16):
    c: Horizontal(g0)
    c: Distance(g0) = 98
    c: Coincident(g1,g0)
    c: Block(g1)
    c: Coincident(g2,g0)
    c: Vertical(g2)
    c: Distance(g2) = 19
    c: Horizontal(g3)
    c: Coincident(g4,g1)
    c: Vertical(g4)
    c: Coincident(g3,g4)
    c: Block(g3)
    c: Coincident(g5,g2)
    c: Coincident(g5,g3)
    c: Block(g0)
    c: Block(g5)
FEATURE [Sketcher::SketchObject] Sketch080  label="topSketch025"
  FullyConstrained = true
  sketch-geometry (6):
    g0: LineSegment StartX=19 StartY=38 StartZ=0 EndX=117 EndY=38 EndZ=0
    g1: ArcOfCircle CenterX=19 CenterY=19 CenterZ=0 NormalX=0 NormalY=0 NormalZ=1 AngleXU=0 Radius=19 StartAngle=1.5708 EndAngle=3.14159
    g2: LineSegment StartX=117 StartY=38 StartZ=0 EndX=117 EndY=19 EndZ=0
    g3: LineSegment StartX=98 StartY=1.0161e-12 StartZ=0 EndX=5.22862e-06 EndY=1.0161e-12 EndZ=0
    g4: LineSegment StartX=5.22862e-06 StartY=19 StartZ=0 EndX=5.22862e-06 EndY=1.0161e-12 EndZ=0
    g5: ArcOfCircle CenterX=98 CenterY=19 CenterZ=0 NormalX=0 NormalY=0 NormalZ=1 AngleXU=0 Radius=19 StartAngle=4.71239 EndAngle=6.28319
  constraints (16):
    c: Horizontal(g0)
    c: Distance(g0) = 98
    c: Coincident(g1,g0)
    c: Block(g1)
    c: Coincident(g2,g0)
    c: Vertical(g2)
    c: Distance(g2) = 19
    c: Horizontal(g3)
    c: Coincident(g4,g1)
    c: Vertical(g4)
    c: Coincident(g3,g4)
    c: Block(g3)
    c: Coincident(g5,g2)
    c: Coincident(g5,g3)
    c: Block(g0)
    c: Block(g5)
FEATURE [Part::Extrusion] Extrude070  label="sideA004"
  Base = -> Sketch080
  Dir = (0,0,1)
  DirMode = 2
  FaceMakerClass = Part::FaceMakerBullseye
  LengthFwd = 3
  LengthRev = 0
  Placement = pos=(0,0,-2.7) rot=(0,0,1;0rad)
  Solid = true
  Symmetric = false
FEATURE [Sketcher::SketchObject] Sketch081
  FullyConstrained = true
  Placement = pos=(117,19,0) rot=(0.57735,0.57735,0.57735;2.0944rad)
  sketch-geometry (8):
    g0: LineSegment StartX=-49.19 StartY=63.5 StartZ=0 EndX=-49.19 EndY=60.5 EndZ=0
    g1: LineSegment StartX=-49.19 StartY=11.5 StartZ=0 EndX=-49.19 EndY=8.5 EndZ=0
    g2: ArcOfCircle CenterX=-1.5 CenterY=62 CenterZ=0 NormalX=0 NormalY=0 NormalZ=1 AngleXU=0 Radius=1.5 StartAngle=4.71239 EndAngle=7.85398
    g3: ArcOfCircle CenterX=-1.5 CenterY=10 CenterZ=0 NormalX=0 NormalY=0 NormalZ=1 AngleXU=0 Radius=1.5 StartAngle=4.71239 EndAngle=7.85398
    g4: LineSegment StartX=-49.19 StartY=63.5 StartZ=0 EndX=-1.5 EndY=63.5 EndZ=0
    g5: LineSegment StartX=-49.19 StartY=60.5 StartZ=0 EndX=-1.5 EndY=60.5 EndZ=0
    g6: LineSegment StartX=-49.19 StartY=11.5 StartZ=0 EndX=-1.5 EndY=11.5 EndZ=0
    g7: LineSegment StartX=-49.19 StartY=8.5 StartZ=0 EndX=-1.5 EndY=8.5 EndZ=0
  constraints (19):
    c: Vertical(g0)
    c: Distance(g0) = 3
    c: Vertical(g1)
    c: Block(g1)
    c: Block(g2)
    c: Block(g3)
    c: Block(g0)
    c: Coincident(g4,g0)
    c: Coincident(g4,g2)
    c: Horizontal(g4)
    c: Coincident(g5,g0)
    c: Coincident(g5,g2)
    c: Horizontal(g5)
    c: Coincident(g6,g1)
    c: Coincident(g6,g3)
    c: Horizontal(g6)
    c: Coincident(g7,g1)
    c: Coincident(g7,g3)
    c: Horizontal(g7)
FEATURE [Part::Extrusion] Extrude071  label="sideB004"
  Base = -> Sketch079
  Dir = (0,0,1)
  DirMode = 2
  FaceMakerClass = Part::FaceMakerBullseye
  LengthFwd = 3
  LengthRev = 0
  Placement = pos=(0,0,71.7) rot=(0,0,1;0rad)
  Solid = true
  Symmetric = false
FEATURE [Part::MultiFuse] Fusion152  label="removeFromBottom004"
  Placement = pos=(2,0,0) rot=(0,0,1;0rad)
  Shapes = -> [Extrude070,Extrude071]
FEATURE [Part::Extrusion] Extrude072
  Base = -> Sketch081
  Dir = (1,0,0)
  DirMode = 2
  FaceMakerClass = Part::FaceMakerBullseye
  LengthFwd = 10
  LengthRev = 0
  Solid = true
  Symmetric = false
FEATURE [Part::Fillet] Fillet059  label="removeFromtMoreFrontCaseScrewRetainers004"
  Base = -> Extrude072
  Edges = 4 edges r=1.49: [Edge6,Edge11,Edge18,Edge23]
  Placement = pos=(-12,0,0) rot=(0,0,1;0rad)
FEATURE [Sketcher::SketchObject] Sketch082
  FullyConstrained = true
  Placement = pos=(117,19,0) rot=(0.57735,0.57735,0.57735;2.0944rad)
  sketch-geometry (8):
    g0: LineSegment StartX=-49.19 StartY=69.25 StartZ=0 EndX=-49.19 EndY=66.25 EndZ=0
    g1: LineSegment StartX=-49.19 StartY=5.75 StartZ=0 EndX=-49.19 EndY=2.75 EndZ=0
    g2: ArcOfCircle CenterX=-1.5 CenterY=67.75 CenterZ=0 NormalX=0 NormalY=0 NormalZ=1 AngleXU=0 Radius=1.5 StartAngle=4.71239 EndAngle=7.85398
    g3: ArcOfCircle CenterX=-1.5 CenterY=4.25 CenterZ=0 NormalX=0 NormalY=0 NormalZ=1 AngleXU=0 Radius=1.5 StartAngle=4.71239 EndAngle=7.85398
    g4: LineSegment StartX=-49.19 StartY=69.25 StartZ=0 EndX=-1.5 EndY=69.25 EndZ=0
    g5: LineSegment StartX=-49.19 StartY=66.25 StartZ=0 EndX=-1.5 EndY=66.25 EndZ=0
    g6: LineSegment StartX=-49.19 StartY=5.75 StartZ=0 EndX=-1.5 EndY=5.75 EndZ=0
    g7: LineSegment StartX=-49.19 StartY=2.75 StartZ=0 EndX=-1.5 EndY=2.75 EndZ=0
  constraints (19):
    c: Vertical(g0)
    c: Distance(g0) = 3
    c: Block(g0)
    c: Vertical(g1)
    c: Block(g2)
    c: Block(g3)
    c: Block(g1)
    c: Coincident(g4,g0)
    c: Coincident(g4,g2)
    c: Horizontal(g4)
    c: Coincident(g5,g0)
    c: Coincident(g5,g2)
    c: Horizontal(g5)
    c: Coincident(g6,g1)
    c: Coincident(g6,g3)
    c: Horizontal(g6)
    c: Coincident(g7,g1)
    c: Coincident(g7,g3)
    c: Horizontal(g7)
FEATURE [Part::Extrusion] Extrude073
  Base = -> Sketch082
  Dir = (1,0,0)
  DirMode = 2
  FaceMakerClass = Part::FaceMakerBullseye
  LengthFwd = 10
  LengthRev = 0
  Solid = true
  Symmetric = false
FEATURE [Part::Fillet] Fillet060  label="removeFromtMoreFrontCaseScrewRetainers005"
  Base = -> Extrude073
  Edges = 4 edges r=1.49: [Edge6,Edge11,Edge18,Edge23]
  Placement = pos=(-4,0,0) rot=(0,0,1;0rad)
FEATURE [Part::Revolution] Revolve163  label="backCaseScrewRetainer004"
  Angle = 360
  Axis = (0,1,0)
  Base = (0,0,0)
  FaceMakerClass = Part::FaceMakerBullseye
  Placement = pos=(12.5,3,62) rot=(0,0,1;0rad)
  Solid = false
  Source = -> Face149
  Symmetric = false
FEATURE [Part::Revolution] Revolve164  label="frontCaseScrewRetainer006"
  Angle = 360
  Axis = (0,1,0)
  Base = (0,0,0)
  FaceMakerClass = Part::FaceMakerBullseye
  Placement = pos=(89.5,3,68.5) rot=(0,0,1;0rad)
  Solid = false
  Source = -> Face151
  Symmetric = false
FEATURE [Part::Revolution] Revolve165  label="frontCaseScrewRetainer007"
  Angle = 360
  Axis = (0,1,0)
  Base = (0,0,0)
  FaceMakerClass = Part::FaceMakerBullseye
  Placement = pos=(89.5,3,3.5) rot=(0,0,1;0rad)
  Solid = false
  Source = -> Face152
  Symmetric = false
FEATURE [Part::Revolution] Revolve166  label="backCaseScrewRetainer005"
  Angle = 360
  Axis = (0,1,0)
  Base = (0,0,0)
  FaceMakerClass = Part::FaceMakerBullseye
  Placement = pos=(12.5,3,10) rot=(0,0,1;0rad)
  Solid = false
  Source = -> Face150
  Symmetric = false
FEATURE [Part::Revolution] Revolve167  label="moreFrontCaseScrewRetainer006"
  Angle = 360
  Axis = (0,1,0)
  Base = (0,0,0)
  FaceMakerClass = Part::FaceMakerBullseye
  Placement = pos=(109.5,4.5,68.5) rot=(0,0,1;0rad)
  Solid = false
  Source = -> Face153
  Symmetric = false
FEATURE [Part::Revolution] Revolve168  label="moreFrontCaseScrewRetainer007"
  Angle = 360
  Axis = (0,1,0)
  Base = (0,0,0)
  FaceMakerClass = Part::FaceMakerBullseye
  Placement = pos=(109.5,4.5,3.5) rot=(0,0,1;0rad)
  Solid = false
  Source = -> Face154
  Symmetric = false
FEATURE [Part::MultiFuse] Fusion151  label="screwRetainers003"
  Shapes = -> [Revolve168,Revolve167,Revolve166,Revolve165,Revolve164,Revolve163]
FEATURE [Part::Cut] Cut069  label="screwRetainers004"
  Base = -> Fusion151
  Tool = -> Fusion152
FEATURE [Part::Cut] Cut070
  Base = -> Cut069
  Tool = -> Fillet060
FEATURE [Part::Cut] Cut071  label="screwPillars001"
  Base = -> Cut070
  Tool = -> Fillet059
FEATURE [Part::MultiFuse] Fusion153  label="bottom024"
  Shapes = -> [Fusion149,Cut071]
FEATURE [Part::Cylinder] Cylinder067
  Angle = 360
  AttacherType = Attacher::AttachEngine3D
  Height = 10
  Placement = pos=(20.65,12,4.68) rot=(1,0,0;1.5708rad)
  Radius = 2
FEATURE [Part::Cylinder] Cylinder068
  Angle = 360
  AttacherType = Attacher::AttachEngine3D
  Height = 10
  Placement = pos=(20.65,12,67.38) rot=(1,0,0;1.5708rad)
  Radius = 2
FEATURE [Part::Cylinder] Cylinder069
  Angle = 360
  AttacherType = Attacher::AttachEngine3D
  Height = 10
  Placement = pos=(77.15,12,67.38) rot=(1,0,0;1.5708rad)
  Radius = 2
FEATURE [Part::Cylinder] Cylinder070
  Angle = 360
  AttacherType = Attacher::AttachEngine3D
  Height = 10
  Placement = pos=(77.15,12,4.68) rot=(1,0,0;1.5708rad)
  Radius = 2
FEATURE [Part::MultiFuse] Fusion154  label="removeFromThreadedInsertHousing001"
  Shapes = -> [Cylinder069,Cylinder068,Cylinder067,Cylinder070]
FEATURE [Part::Cut] Cut072  label="bottom025"
  Base = -> Fusion153
  Tool = -> Fusion154
FEATURE [Image::ImagePlane] ImagePlane
  XSize = 339
  YSize = 72
FEATURE [Sketcher::SketchObject] Sketch083
  FullyConstrained = true
  MapMode = 5
  Support = -> [XY_Plane]
  sketch-geometry (248):
    g0: LineSegment StartX=-151.619 StartY=28.8932 StartZ=0 EndX=-140.819 EndY=28.8932 EndZ=0
    g1: LineSegment StartX=-151.619 StartY=24.0313 StartZ=0 EndX=-151.619 EndY=28.8932 EndZ=0
    g2: LineSegment StartX=-140.819 StartY=17.7713 StartZ=0 EndX=-151.619 EndY=17.7713 EndZ=0
    g3: LineSegment StartX=-151.619 StartY=17.7713 StartZ=0 EndX=-151.619 EndY=22.6313 EndZ=0
    g4: LineSegment StartX=-151.619 StartY=22.6313 StartZ=0 EndX=-145.128 EndY=22.6313 EndZ=0
    g5: LineSegment StartX=-145.128 StartY=24.0313 StartZ=0 EndX=-140.819 EndY=28.8932 EndZ=0
    g6: LineSegment StartX=-145.128 StartY=22.6313 StartZ=0 EndX=-140.819 EndY=17.7713 EndZ=0
    g7: ArcOfCircle CenterX=-155.157 CenterY=23.3323 CenterZ=0 NormalX=0 NormalY=0 NormalZ=1 AngleXU=0 Radius=6.92354 StartAngle=1.03434 EndAngle=5.24885
    g8: ArcOfCircle CenterX=-155.157 CenterY=23.3323 CenterZ=0 NormalX=0 NormalY=0 NormalZ=1 AngleXU=0 Radius=12.6269 StartAngle=1.28675 EndAngle=4.99643
    g9: LineSegment StartX=-151.619 StartY=35.4532 StartZ=0 EndX=-151.619 EndY=29.2832 EndZ=0
    g10: LineSegment StartX=-151.619 StartY=17.3813 StartZ=0 EndX=-151.619 EndY=11.2113 EndZ=0
    g11-g21: Circle x11 (B-spline internal-alignment scaffolding for g22; pole/knot coordinates omitted)
    g22: BSplineCurve PolesCount=11 KnotsCount=9 Degree=3 IsPeriodic=0
    g23-g31: GeomPoint x9 (B-spline internal-alignment scaffolding for g22; pole/knot coordinates omitted)
    g32-g49: Circle x18 (B-spline internal-alignment scaffolding for g50; pole/knot coordinates omitted)
    g50: BSplineCurve PolesCount=18 KnotsCount=16 Degree=3 IsPeriodic=0
    g51-g66: GeomPoint x16 (B-spline internal-alignment scaffolding for g50; pole/knot coordinates omitted)
    g67: LineSegment StartX=-117.124 StartY=30.093 StartZ=0 EndX=-117.603 EndY=26.5272 EndZ=0
    g68: LineSegment StartX=-117.603 StartY=17.8472 StartZ=0 EndX=-117.124 EndY=14.2659 EndZ=0
    g69: Ellipse CenterX=-109.671 CenterY=20.025 CenterZ=0 NormalX=0 NormalY=0 NormalZ=1 MajorRadius=3.34798 MinorRadius=2.71052 AngleXU=-1.56793
    g70: GeomPoint X=-109.666 Y=18.0598 Z=0
    g71: GeomPoint X=-109.677 Y=21.9902 Z=0
    g72: Ellipse CenterX=-109.671 CenterY=20.0123 CenterZ=0 NormalX=0 NormalY=0 NormalZ=1 MajorRadius=6.93002 MinorRadius=6.36273 AngleXU=-3.13976
    g73: GeomPoint X=-112.417 Y=20.0073 Z=0
    g74: GeomPoint X=-106.925 Y=20.0173 Z=0
    g75: Ellipse CenterX=-51.7682 CenterY=20.1463 CenterZ=0 NormalX=0 NormalY=0 NormalZ=1 MajorRadius=3.19279 MinorRadius=2.71052 AngleXU=-1.52774
    g76: GeomPoint X=-51.6955 Y=18.4606 Z=0
    g77: GeomPoint X=-51.8408 Y=21.832 Z=0
    g78: GeomPoint X=-54.5142 Y=20.1413 Z=0
    g79: GeomPoint X=-49.0221 Y=20.1513 Z=0
    g80: Ellipse CenterX=-51.7682 CenterY=20.1463 CenterZ=0 NormalX=0 NormalY=0 NormalZ=1 MajorRadius=6.93002 MinorRadius=6.36273 AngleXU=-3.13976
    g81: Ellipse CenterX=-22.8436 CenterY=20.1783 CenterZ=0 NormalX=0 NormalY=0 NormalZ=1 MajorRadius=3.31512 MinorRadius=2.71052 AngleXU=-1.60214
    g82: GeomPoint X=-22.9034 Y=18.2706 Z=0
    g83: GeomPoint X=-22.7838 Y=22.0861 Z=0
    g84: GeomPoint X=-25.5897 Y=20.1733 Z=0
    g85: GeomPoint X=-20.0976 Y=20.1833 Z=0
    g86: Ellipse CenterX=-22.8436 CenterY=20.1783 CenterZ=0 NormalX=0 NormalY=0 NormalZ=1 MajorRadius=6.93002 MinorRadius=6.36273 AngleXU=-3.13976
    g87: LineSegment StartX=-101.889 StartY=14.1107 StartZ=0 EndX=-97.7455 EndY=14.1107 EndZ=0
    g88: LineSegment StartX=-93.8155 StartY=14.1107 StartZ=0 EndX=-89.6755 EndY=14.1107 EndZ=0
    g89: LineSegment StartX=-85.7455 StartY=14.1107 StartZ=0 EndX=-81.6055 EndY=14.1107 EndZ=0
    g90: LineSegment StartX=-101.889 StartY=14.1107 StartZ=0 EndX=-101.889 EndY=25.9907 EndZ=0
    g91: LineSegment StartX=-101.889 StartY=25.9907 StartZ=0 EndX=-97.8594 EndY=25.9907 EndZ=0
    g92: LineSegment StartX=-97.8594 StartY=25.9907 StartZ=0 EndX=-97.8594 EndY=24.0907 EndZ=0
    g93: LineSegment StartX=-97.7455 StartY=14.1107 StartZ=0 EndX=-97.7455 EndY=19.9107 EndZ=0
    g94: LineSegment StartX=-89.6755 StartY=14.1107 StartZ=0 EndX=-89.6755 EndY=19.9107 EndZ=0
    g95: LineSegment StartX=-93.8155 StartY=14.1107 StartZ=0 EndX=-93.8155 EndY=21.0107 EndZ=0
    g96-g106: Circle x11 (B-spline internal-alignment scaffolding for g107; pole/knot coordinates omitted)
    g107: BSplineCurve PolesCount=11 KnotsCount=9 Degree=3 IsPeriodic=0
    g108-g116: GeomPoint x9 (B-spline internal-alignment scaffolding for g107; pole/knot coordinates omitted)
    g117: BSplineCurve PolesCount=11 KnotsCount=9 Degree=3 IsPeriodic=0
    g118-g125: Circle x8 (B-spline internal-alignment scaffolding for g126; pole/knot coordinates omitted)
    g126: BSplineCurve PolesCount=8 KnotsCount=6 Degree=3 IsPeriodic=0
    g127-g132: GeomPoint x6 (B-spline internal-alignment scaffolding for g126; pole/knot coordinates omitted)
    g133: BSplineCurve PolesCount=8 KnotsCount=6 Degree=3 IsPeriodic=0
    g134: LineSegment StartX=-85.7455 StartY=21.0107 StartZ=0 EndX=-85.7455 EndY=14.1107 EndZ=0
    g135: LineSegment StartX=-80.0879 StartY=14.1107 StartZ=0 EndX=-75.944 EndY=14.1107 EndZ=0
    g136: LineSegment StartX=-72.014 StartY=14.1107 StartZ=0 EndX=-67.874 EndY=14.1107 EndZ=0
    g137: LineSegment StartX=-63.944 StartY=14.1107 StartZ=0 EndX=-59.804 EndY=14.1107 EndZ=0
    g138: LineSegment StartX=-80.0879 StartY=14.1107 StartZ=0 EndX=-80.0879 EndY=25.9907 EndZ=0
    g139: LineSegment StartX=-80.0879 StartY=25.9907 StartZ=0 EndX=-76.0579 EndY=25.9907 EndZ=0
    g140: LineSegment StartX=-76.0579 StartY=25.9907 StartZ=0 EndX=-76.0579 EndY=24.0907 EndZ=0
    g141: LineSegment StartX=-75.944 StartY=14.1107 StartZ=0 EndX=-75.944 EndY=19.9107 EndZ=0
    g142: LineSegment StartX=-67.874 StartY=14.1107 StartZ=0 EndX=-67.874 EndY=19.9107 EndZ=0
    g143: LineSegment StartX=-72.014 StartY=14.1107 StartZ=0 EndX=-72.014 EndY=21.0107 EndZ=0
    g144-g148: Circle x5 (B-spline internal-alignment scaffolding for g149; pole/knot coordinates omitted)
    g149: BSplineCurve PolesCount=11 KnotsCount=9 Degree=3 IsPeriodic=0
    g150-g158: GeomPoint x9 (B-spline internal-alignment scaffolding for g149; pole/knot coordinates omitted)
    g159: BSplineCurve PolesCount=11 KnotsCount=9 Degree=3 IsPeriodic=0
    g160-g167: Circle x8 (B-spline internal-alignment scaffolding for g168; pole/knot coordinates omitted)
    g168: BSplineCurve PolesCount=8 KnotsCount=6 Degree=3 IsPeriodic=0
    g169-g174: GeomPoint x6 (B-spline internal-alignment scaffolding for g168; pole/knot coordinates omitted)
    g175: BSplineCurve PolesCount=8 KnotsCount=6 Degree=3 IsPeriodic=0
    g176: LineSegment StartX=-63.944 StartY=21.0107 StartZ=0 EndX=-63.944 EndY=14.1107 EndZ=0
    g177: LineSegment StartX=-59.804 StartY=14.1107 StartZ=0 EndX=-59.804 EndY=21.5868 EndZ=0
    g178: BSplineCurve PolesCount=4 KnotsCount=2 Degree=3 IsPeriodic=0
    g179: GeomPoint X=-59.804 Y=21.5868 Z=0
    g180: GeomPoint X=-60.2379 Y=24.0907 Z=0
    g181: LineSegment StartX=-81.6055 StartY=14.1107 StartZ=0 EndX=-81.6055 EndY=21.5868 EndZ=0
    g182: LineSegment StartX=-151.619 StartY=24.0313 StartZ=0 EndX=-145.128 EndY=24.0313 EndZ=0
    g183: Circle CenterX=-82.0394 CenterY=24.0907 CenterZ=0 NormalX=0 NormalY=0 NormalZ=1 AngleXU=0 Radius=1
    g184: Circle CenterX=-81.7131 CenterY=23.2736 CenterZ=0 NormalX=0 NormalY=0 NormalZ=1 AngleXU=0 Radius=1
    g185: Circle CenterX=-81.6055 CenterY=21.5868 CenterZ=0 NormalX=0 NormalY=0 NormalZ=1 AngleXU=0 Radius=1
    g186: BSplineCurve PolesCount=3 KnotsCount=2 Degree=2 IsPeriodic=0
    g187: GeomPoint X=-82.0394 Y=24.0907 Z=0
    g188: GeomPoint X=-81.6055 Y=21.5868 Z=0
    g189: Ellipse CenterX=-37.3522 CenterY=19.9515 CenterZ=0 NormalX=0 NormalY=0 NormalZ=1 MajorRadius=2.99755 MinorRadius=2.49 AngleXU=1.5708
    g190: GeomPoint X=-37.3522 Y=21.6203 Z=0
    g191: GeomPoint X=-37.3522 Y=18.2826 Z=0
    g192: ArcOfEllipse CenterX=-38.7647 CenterY=20.06 CenterZ=0 NormalX=0 NormalY=0 NormalZ=1 MajorRadius=6.30025 MinorRadius=5.3849 AngleXU=1.57276 StartAngle=5.50632 EndAngle=10.3035
    g193: GeomPoint X=-38.7711 Y=23.3304 Z=0
    g194: GeomPoint X=-38.7583 Y=16.7895 Z=0
    g195: LineSegment StartX=-34.6109 StartY=14.1107 StartZ=0 EndX=-30.8984 EndY=14.1107 EndZ=0
    g196: LineSegment StartX=-30.8984 StartY=14.1107 StartZ=0 EndX=-30.8984 EndY=31.1784 EndZ=0
    g197: LineSegment StartX=-30.8984 StartY=31.1784 StartZ=0 EndX=-34.9984 EndY=31.1784 EndZ=0
    g198: LineSegment StartX=-34.9984 StartY=24.5602 StartZ=0 EndX=-34.9984 EndY=31.1784 EndZ=0
    g199: LineSegment StartX=-34.6109 StartY=16.0476 StartZ=0 EndX=-34.6109 EndY=14.1107 EndZ=0
    g200: LineSegment StartX=-14.8781 StartY=14.1107 StartZ=0 EndX=-10.5106 EndY=14.1107 EndZ=0
    g201: LineSegment StartX=-14.8781 StartY=14.1107 StartZ=0 EndX=-14.8781 EndY=25.8504 EndZ=0
    g202: LineSegment StartX=-14.8781 StartY=25.8504 StartZ=0 EndX=-10.8534 EndY=25.8504 EndZ=0
    g203: LineSegment StartX=-10.8534 StartY=25.8504 StartZ=0 EndX=-10.8534 EndY=24.0923 EndZ=0
    g204: LineSegment StartX=-10.5106 StartY=14.1107 StartZ=0 EndX=-10.5106 EndY=19.7752 EndZ=0
    g205: LineSegment StartX=-5.96397 StartY=25.9304 StartZ=0 EndX=-5.96397 EndY=22.574 EndZ=0
    g206-g214: Circle x9 (B-spline internal-alignment scaffolding for g215; pole/knot coordinates omitted)
    g215: BSplineCurve PolesCount=9 KnotsCount=7 Degree=3 IsPeriodic=0
    g216-g222: GeomPoint x7 (B-spline internal-alignment scaffolding for g215; pole/knot coordinates omitted)
    g223-g232: Circle x10 (B-spline internal-alignment scaffolding for g233; pole/knot coordinates omitted)
    g233: BSplineCurve PolesCount=10 KnotsCount=8 Degree=3 IsPeriodic=0
    g234-g241: GeomPoint x8 (B-spline internal-alignment scaffolding for g233; pole/knot coordinates omitted)
    g242: LineSegment StartX=-1.58923 StartY=21.0696 StartZ=0 EndX=2.62034 EndY=21.0696 EndZ=0
    g243: LineSegment StartX=-1.55856 StartY=18.7342 StartZ=0 EndX=6.45946 EndY=18.7342 EndZ=0
    g244: LineSegment StartX=5.29231 StartY=17.386 StartZ=0 EndX=5.29231 EndY=14.3674 EndZ=0
    g245: LineSegment StartX=0.528324 StartY=26.3804 StartZ=0 EndX=0.528324 EndY=13.5804 EndZ=0
    g246: LineSegment StartX=0.528324 StartY=26.3804 StartZ=0 EndX=0.528324 EndY=19.9804 EndZ=0
    g247: LineSegment StartX=0.528324 StartY=19.9804 StartZ=0 EndX=-5.87168 EndY=19.9804 EndZ=0
  constraints (240):
    c: Coincident(g1,g0)
    c: Horizontal(g0)
    c: Vertical(g1)
    c: Coincident(g2,g3)
    c: Coincident(g3,g4)
    c: Horizontal(g4)
    c: Horizontal(g2)
    c: Vertical(g3)
    c: Block(g1)
    c: Distance(g3) = 4.86
    c: Block(g4)
    c: Distance(g0) = 10.8
    c: Distance(g2) = 10.8
    c: Coincident(g5,g0)
    c: Coincident(g6,g4)
    c: Coincident(g6,g2)
    c: Block(g8)
    c: Block(g7)
    c: Coincident(g9,g8)
    c: Coincident(g9,g7)
    c: Vertical(g9)
    c: Coincident(g10,g7)
    c: Coincident(g10,g8)
    c: Vertical(g10)
    c: Weight(g11) = 1
    c: Equal(g11, g12-g21) x10
    c: InternalAlignment(g11-g21 -> g22) x11
    c: InternalAlignment(g23-g31 -> g22) x9
    c: Block(g22)
    c: Weight(g32) = 1
    c: Equal(g32, g33-g49) x17
    c: InternalAlignment(g32-g49 -> g50) x18
    c: InternalAlignment(g51-g66 -> g50) x16
    c: Block(g50)
    c: Coincident(g67,g50)
    c: Coincident(g67,g22)
    c: Coincident(g68,g22)
    c: Coincident(g68,g50)
    c: InternalAlignment(g70,g69)
    c: InternalAlignment(g71,g69)
    c: Block(g69)
    c: InternalAlignment(g73,g72)
    c: InternalAlignment(g74,g72)
    c: Block(g72)
    c: InternalAlignment(g76,g75)
    c: InternalAlignment(g77,g75)
    c: InternalAlignment(g78,g80)
    c: InternalAlignment(g79,g80)
    c: Block(g80)
    c: Coincident(g75,g80)
    c: Block(g75)
    c: InternalAlignment(g82,g81)
    c: InternalAlignment(g83,g81)
    c: InternalAlignment(g84,g86)
    c: InternalAlignment(g85,g86)
    c: Block(g86)
    c: Coincident(g81,g86)
    c: Block(g81)
    c: Horizontal(g87)
    c: Block(g87)
    c: Horizontal(g88)
    c: Distance(g88) = 4.14
    c: Horizontal(g89)
    c: Equal(g88,g89) = 4.14
    c: Block(g89)
    c: Block(g88)
    c: Coincident(g90,g87)
    c: Vertical(g90)
    c: Distance(g90) = 11.88
    c: Coincident(g91,g90)
    c: Horizontal(g91)
    c: Coincident(g92,g91)
    c: Vertical(g92)
    c: Distance(g91) = 4.03
    c: Distance(g92) = 1.9
    c: Coincident(g93,g87)
    c: Vertical(g93)
    c: Vertical(g94)
    c: Coincident(g94,g88)
    c: Distance(g93) = 5.8
    c: Distance(g94) = 5.8
    c: Vertical(g95)
    c: Coincident(g95,g88)
    c: Distance(g95) = 6.9
    c: Coincident(g107,g92)
    c: Weight(g96) = 1
    c: Equal(g96, g97-g106) x10
    c: InternalAlignment(g96-g106 -> g107) x11
    c: InternalAlignment(g108-g116 -> g107) x9
    c: Block(g107)
    c: Block(g117)
    c: Coincident(g126,g93)
    c: Weight(g118) = 1
    c: Equal(g118, g119-g125) x7
    c: Coincident(g126,g95)
    c: InternalAlignment(g118-g125 -> g126) x8
    c: InternalAlignment(g127-g132 -> g126) x6
    c: Coincident(g133,g94)
    c: Block(g126)
    c: Block(g133)
    c: Coincident(g134,g133)
    c: Coincident(g134,g89)
    c: Vertical(g134)
    c: Horizontal(g135)
    c: Block(g135)
    c: Horizontal(g136)
    c: Equal(g88,g136) = 4.14
    c: Horizontal(g137)
    c: Equal(g136,g137) = 4.14
    c: Block(g137)
    c: Block(g136)
    c: Coincident(g138,g135)
    c: Vertical(g138)
    c: Equal(g90,g138) = 11.88
    c: Coincident(g139,g138)
    c: Horizontal(g139)
    c: Coincident(g140,g139)
    c: Vertical(g140)
    c: Equal(g91,g139) = 4.03
    c: Equal(g92,g140) = 1.9
    c: Coincident(g141,g135)
    c: Vertical(g141)
    c: Vertical(g142)
    c: Coincident(g142,g136)
    c: Equal(g93,g141) = 5.8
    c: Equal(g94,g142) = 5.8
    c: Vertical(g143)
    c: Coincident(g143,g136)
    c: Equal(g95,g143) = 6.9
    c: Coincident(g149,g140)
    c: Equal(g96,g144) = 1
    c: Equal(g144, g145-g148) x4
    c: InternalAlignment(g144-g148 -> g149) x5
    c: InternalAlignment(g150-g158 -> g149) x9
    c: Block(g149)
    c: Block(g159)
    c: Coincident(g168,g141)
    c: Equal(g118,g160) = 1
    c: Equal(g160, g161-g167) x7
    c: Coincident(g168,g143)
    c: InternalAlignment(g160-g167 -> g168) x8
    c: InternalAlignment(g169-g174 -> g168) x6
    c: Coincident(g175,g142)
    c: Block(g168)
    c: Block(g175)
    c: Coincident(g176,g175)
    c: Coincident(g176,g137)
    c: Vertical(g176)
    c: Coincident(g177,g137)
    c: Vertical(g177)
    c: Coincident(g178,g177)
    c: Coincident(g178,g159)
    c: InternalAlignment(g179,g178)
    c: InternalAlignment(g180,g178)
    c: Block(g178)
    c: Vertical(g181)
    c: Coincident(g181,g89)
    c: Block(g5)
    c: Coincident(g182,g1)
    c: Coincident(g182,g5)
    c: Horizontal(g182)
    c: Coincident(g186,g117)
    c: Weight(g183) = 1
    c: Equal(g183,g184)
    c: Equal(g183,g185)
    c: Coincident(g186,g181)
    c: InternalAlignment(g183,g186)
    c: InternalAlignment(g184,g186)
    c: InternalAlignment(g185,g186)
    c: InternalAlignment(g187,g186)
    c: InternalAlignment(g188,g186)
    c: Block(g186)
    c: InternalAlignment(g190,g189)
    c: InternalAlignment(g191,g189)
    c: Block(g189)
    c: InternalAlignment(g193,g192)
    c: InternalAlignment(g194,g192)
    c: Block(g192)
    c: Horizontal(g195)
    c: Block(g195)
    c: Coincident(g196,g195)
    c: Vertical(g196)
    c: Block(g196)
    c: Distance(g195) = 3.71244
    c: Coincident(g197,g196)
    c: Horizontal(g197)
    c: Distance(g197) = 4.1
    c: Coincident(g198,g192)
    c: Coincident(g198,g197)
    c: Vertical(g198)
    c: Block(g198)
    c: Coincident(g199,g192)
    c: Coincident(g199,g195)
    c: Vertical(g199)
    c: Block(g199)
    c: Horizontal(g200)
    c: Block(g200)
    c: Coincident(g201,g200)
    c: Vertical(g201)
    c: Block(g201)
    c: Coincident(g202,g201)
    c: Horizontal(g202)
    c: Block(g202)
    c: Coincident(g203,g202)
    c: Vertical(g203)
    c: Block(g203)
    c: Coincident(g204,g200)
    c: Vertical(g204)
    c: Block(g204)
    c: Coincident(g215,g203)
    c: Weight(g206) = 1
    c: Equal(g206, g207-g214) x8
    c: Coincident(g215,g205)
    c: InternalAlignment(g206-g214 -> g215) x9
    c: InternalAlignment(g216-g222 -> g215) x7
    c: Coincident(g233,g204)
    c: Weight(g223) = 1
    c: Equal(g223, g224-g232) x9
    c: Coincident(g233,g205)
    c: InternalAlignment(g223-g232 -> g233) x10
    c: InternalAlignment(g234-g241 -> g233) x8
    c: Vertical(g205)
    c: Block(g205)
    c: Block(g215)
    c: Block(g233)
    c: Horizontal(g242)
    c: Horizontal(g243)
    c: Block(g242)
    c: Block(g243)
    c: Vertical(g244)
    c: Block(g244)
    c: Vertical(g245)
    c: Distance(g245) = 12.8
    c: Vertical(g246)
    c: Distance(g246) = 6.4
    c: Block(g245)
    c: Coincident(g246,g245)
    c: Coincident(g247,g246)
    c: Horizontal(g247)
    c: Distance(g247) = 6.4
FEATURE [PartDesign::Body] Body
  Group = -> [Sketch083]
  Origin = -> Origin
FEATURE [Sketcher::SketchObject] Sketch084
  FullyConstrained = true
  MapMode = 5
  Support = -> [XY_Plane001]
FEATURE [PartDesign::Body] Body001
  Group = -> [Sketch084]
  Origin = -> Origin001
